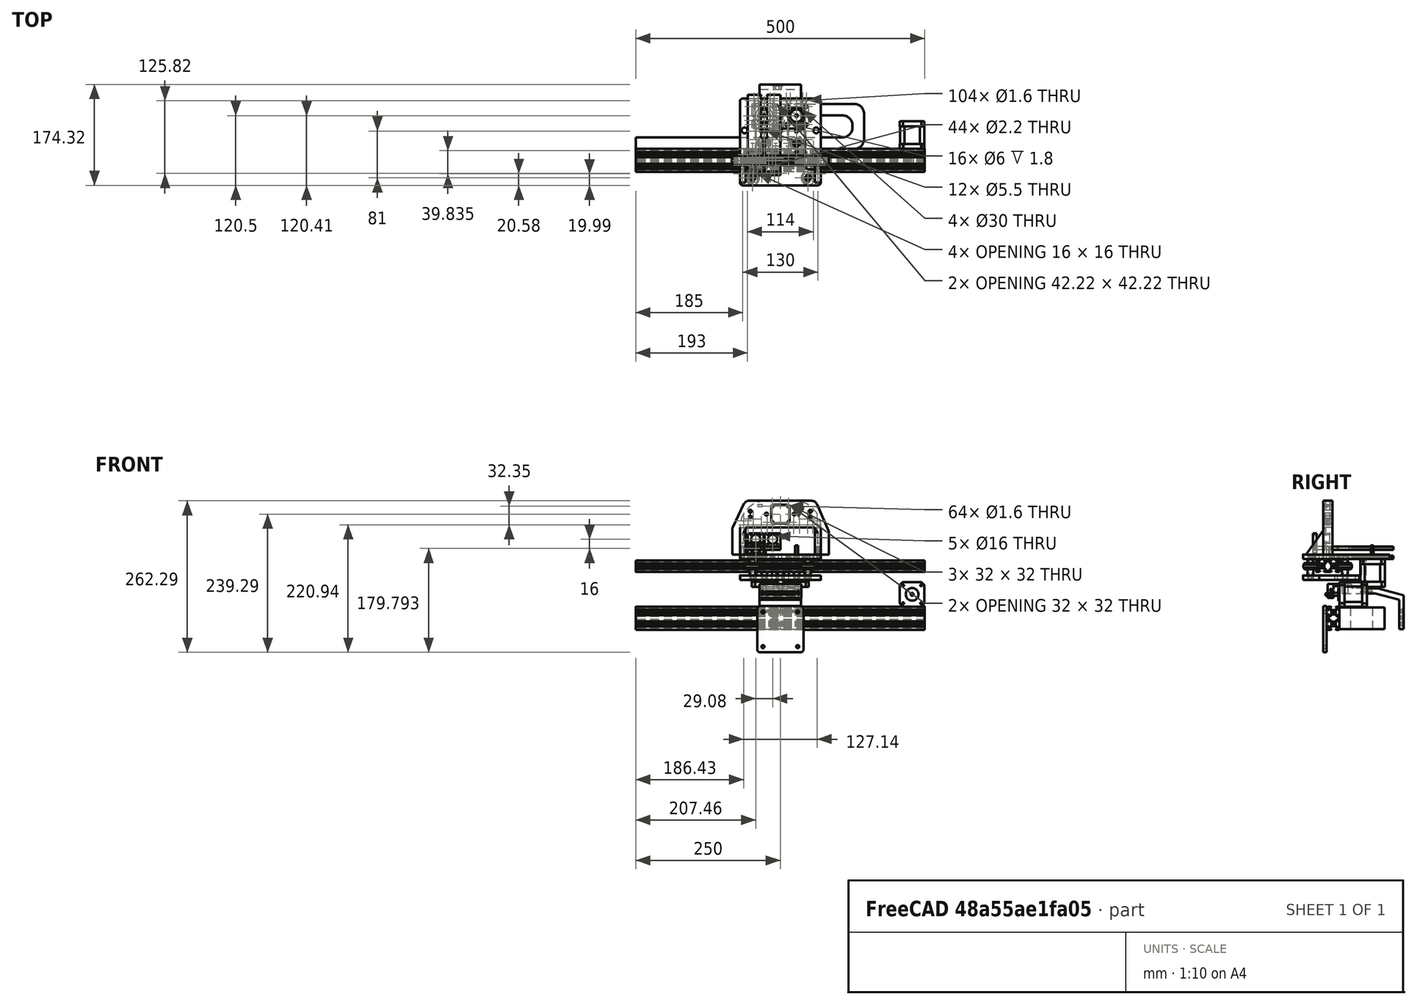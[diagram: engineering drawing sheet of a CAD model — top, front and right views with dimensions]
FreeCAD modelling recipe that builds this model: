
FCSTD DOCUMENT  (FreeCAD 0.18R16146 (Git))
Label: Head
License: All rights reserved
LicenseURL: http://en.wikipedia.org/wiki/All_rights_reserved
objects: Drawing::FeatureViewPython×332, Sketcher::SketchObject×49, Part::Feature×35, PartDesign::Hole×22, PartDesign::Pocket×15, PartDesign::Body×13, Drawing::FeatureViewPart×13, PartDesign::Pad×12, App::Part×8, App::DocumentObjectGroup×6, Drawing::FeaturePage×5, Part::MultiFuse×3, Mesh::Feature×2, Part::Mirroring×2, PartDesign::FeatureBase×1
note: 201 computed .brp shape members not serialized (recipe doc carries the construction recipe); baked Part::Feature solids carry a one-line shape summary decoded from their .brp

FEATURE [Part::Feature] Part__Feature001  label="Nema 17 Stepper Motor"
  Placement = pos=(-28,-9,0) rot=(0,0,1;0rad)
  shape: bbox 42.42 x 42.42 x 72 mm, 64 faces (baked)
FEATURE [Part::Feature] Part__Feature002  label="Nema 17 Stepper Motor001"
  Placement = pos=(28,-9,0) rot=(0,0,1;0rad)
  shape: bbox 42.42 x 42.42 x 72 mm, 64 faces (baked)
FEATURE [Part::Feature] Part__Feature  label="V-Slot 20x40x500 Linear Rail"
  Placement = pos=(-250,-86.5,-12) rot=(0,1,0;1.5708rad)
  shape: bbox 500 x 40 x 20 mm, 116 faces (baked)
FEATURE [Part::Feature] Part__Feature003  label="Solid V Wheel"
  Placement = pos=(-28,-56.5666,-12.1) rot=(0,1,0;1.5708rad)
  shape: bbox 23.9 x 23.9 x 10.2 mm, 16 faces (baked)
FEATURE [Part::Feature] Part__Feature004  label="Solid V Wheel001"
  Placement = pos=(28,-56.57,-12.1) rot=(0,1,0;1.5708rad)
  shape: bbox 23.9 x 23.9 x 10.2 mm, 16 faces (baked)
FEATURE [Part::Feature] Part__Feature005  label="Solid V Wheel002"
  Placement = pos=(-48,-116.57,-12.1) rot=(0,1,0;1.5708rad)
  shape: bbox 23.9 x 23.9 x 10.2 mm, 16 faces (baked)
FEATURE [Part::Feature] Part__Feature006  label="Solid V Wheel003"
  Placement = pos=(48,-116.57,-12.1) rot=(0,1,0;1.5708rad)
  shape: bbox 23.9 x 23.9 x 10.2 mm, 16 faces (baked)
FEATURE [Part::Feature] Part__Feature007  label="V-Slot 20x40x500 Linear Rail001"
  Placement = pos=(-250,-76.5,-102) rot=(0.57735,0.57735,0.57735;2.0944rad)
  shape: bbox 500 x 20 x 40 mm, 116 faces (baked)
FEATURE [Part::Feature] Part__Feature008  label="Nema 17 Stepper Motor002"
  Placement = pos=(228,-66.5,-60.85) rot=(1,0,0;1.5708rad)
  shape: bbox 42.42 x 72 x 42.42 mm, 64 faces (baked)
FEATURE [Part::Feature] Body006021001  label="Cable Chain Support Main001"
  shape: bbox 72 x 106 x 78.33 mm, 55 faces (baked)
FEATURE [Mesh::Feature] Mesh  label="Cable Chain Support Main001 (Meshed)"
FEATURE [Sketcher::SketchObject] Sketch025  label="BottomWheel"
  MapMode = 5
  Placement = pos=(0,0,8) rot=(0,0,1;0rad)
  sketch-geometry (2):
    g0: Circle CenterX=-48 CenterY=-116.56 CenterZ=0 NormalX=0 NormalY=0 NormalZ=1 AngleXU=0 Radius=2.6
    g1: Circle CenterX=48 CenterY=-116.56 CenterZ=0 NormalX=0 NormalY=0 NormalZ=1 AngleXU=0 Radius=2.6
  constraints (6):
    c: DistanceX(g0,g-1) = 48
    c: DistanceX(g-1,g1) = 48
    c: Radius(g0) = 2.6  'M5 Hole'
    c: Equal(g0,g1)
    c: Horizontal(g1,g0)
    c: DistanceY(g0,g-1) = 116.56
FEATURE [Sketcher::SketchObject] Sketch027  label="TopWheel"
  ExternalGeometry = -> [Sketch025]
  MapMode = 5
  Placement = pos=(0,0,8) rot=(0,0,1;0rad)
  sketch-geometry (2):
    g0: Circle CenterX=-28 CenterY=-56.56 CenterZ=0 NormalX=0 NormalY=0 NormalZ=1 AngleXU=0 Radius=2.6
    g1: Circle CenterX=28 CenterY=-56.56 CenterZ=0 NormalX=0 NormalY=0 NormalZ=1 AngleXU=0 Radius=2.6
  constraints (6):
    c: Horizontal(g0,g1)
    c: DistanceX(g0,g-1) = 28
    c: DistanceX(g-1,g1) = 28
    c: Equal(g-3,g0)
    c: Equal(g0,g1)
    c: DistanceY(g-3,g0) = 60
FEATURE [Sketcher::SketchObject] Sketch029  label="StepperFixHoles"
  MapMode = 5
  Placement = pos=(0,0,8) rot=(0,0,1;0rad)
  sketch-geometry (14):
    g0: Circle CenterX=-43.5 CenterY=6.59 CenterZ=0 NormalX=0 NormalY=0 NormalZ=1 AngleXU=0 Radius=1.6
    g1: Circle CenterX=-12.5 CenterY=6.59 CenterZ=0 NormalX=0 NormalY=0 NormalZ=1 AngleXU=0 Radius=1.6
    g2: LineSegment [constr] StartX=-43.5 StartY=6.59 StartZ=0 EndX=-12.5 EndY=6.59 EndZ=0
    g3: Circle CenterX=-43.5 CenterY=-24.41 CenterZ=0 NormalX=0 NormalY=0 NormalZ=1 AngleXU=0 Radius=1.6
    g4: LineSegment [constr] StartX=-43.5 StartY=6.59 StartZ=0 EndX=-43.5 EndY=-24.41 EndZ=0
    g5: Circle CenterX=-12.5 CenterY=-24.41 CenterZ=0 NormalX=0 NormalY=0 NormalZ=1 AngleXU=0 Radius=1.6
    g6: LineSegment [constr] StartX=-43.5 StartY=-24.41 StartZ=0 EndX=-12.5 EndY=-24.41 EndZ=0
    g7: Circle CenterX=12.5 CenterY=6.59 CenterZ=0 NormalX=0 NormalY=0 NormalZ=1 AngleXU=0 Radius=1.6
    g8: Circle CenterX=43.5 CenterY=6.59 CenterZ=0 NormalX=0 NormalY=0 NormalZ=1 AngleXU=0 Radius=1.6
    g9: LineSegment [constr] StartX=12.5 StartY=6.59 StartZ=0 EndX=43.5 EndY=6.59 EndZ=0
    g10: Circle CenterX=12.5 CenterY=-24.41 CenterZ=0 NormalX=0 NormalY=0 NormalZ=1 AngleXU=0 Radius=1.6
    g11: LineSegment [constr] StartX=12.5 StartY=6.59 StartZ=0 EndX=12.5 EndY=-24.41 EndZ=0
    g12: Circle CenterX=43.5 CenterY=-24.41 CenterZ=0 NormalX=0 NormalY=0 NormalZ=1 AngleXU=0 Radius=1.6
    g13: LineSegment [constr] StartX=12.5 StartY=-24.41 StartZ=0 EndX=43.5 EndY=-24.41 EndZ=0
  constraints (36):
    c: Radius(g0) = 1.6
    c: Equal(g0,g1) = 1.6
    c: Coincident(g0,g2)
    c: Coincident(g1,g2)
    c: Distance(g2) = 31
    c: Angle(g2) = 0
    c: Equal(g0,g3) = 1.6
    c: Coincident(g0,g4)
    c: Coincident(g3,g4)
    c: Distance(g4) = 31
    c: Perpendicular(g4,g2)
    c: Equal(g0,g5) = 1.6
    c: Coincident(g3,g6)
    c: Coincident(g5,g6)
    c: Equal(g2,g6)
    c: Parallel(g6,g2)
    c: Radius(g7) = 1.6
    c: Equal(g7,g8) = 1.6
    c: Coincident(g7,g9)
    c: Coincident(g8,g9)
    c: Distance(g9) = 31
    c: Angle(g9) = 0
    c: Equal(g7,g10) = 1.6
    c: Coincident(g7,g11)
    c: Coincident(g10,g11)
    c: Distance(g11) = 31
    c: Perpendicular(g11,g9)
    c: Equal(g7,g12) = 1.6
    c: Coincident(g10,g13)
    c: Coincident(g12,g13)
    c: Equal(g9,g13)
    c: Parallel(g13,g9)
    c: Horizontal(g1,g8)
    c: DistanceX(g-1,g7) = 12.5
    c: DistanceX(g5,g-1) = 12.5
    c: DistanceY(g5,g-1) = 24.41
FEATURE [Part::Feature] Part__Feature009  label="BeltTensor"
  Placement = pos=(16.6,-86.5,-58.6) rot=(0,0.707107,0.707107;3.14159rad)
  shape: bbox 72 x 20 x 24.2 mm, 41 faces, 2 solids (baked)
FEATURE [Part::Feature] Part__Feature012  label="Aluminum Spacer 35mm002"
  Placement = pos=(-28,-56.56,-35) rot=(0,0,-1;0.087266rad)
  shape: bbox 10 x 10 x 35 mm, 14 faces (baked)
FEATURE [Part::Feature] Part__Feature013  label="Aluminum Spacer 35mm003"
  Placement = pos=(28,-56.56,-35) rot=(0,0,1;0rad)
  shape: bbox 10 x 10 x 35 mm, 14 faces (baked)
FEATURE [Part::Feature] Part__Feature014  label="Aluminum Spacer 35mm004"
  Placement = pos=(-48,-116.56,-35) rot=(0,0,1;0rad)
  shape: bbox 10 x 10 x 35 mm, 14 faces (baked)
FEATURE [Part::Feature] Part__Feature016  label="Aluminum Spacer 35mm006"
  Placement = pos=(48,-116.56,-35) rot=(0,0,1;0rad)
  shape: bbox 10 x 10 x 35 mm, 14 faces (baked)
FEATURE [App::DocumentObjectGroup] Group  label="Spacer"
  Group = -> [Part__Feature012,Part__Feature013,Part__Feature014,Part__Feature016]
FEATURE [App::DocumentObjectGroup] Group001  label="Wheel"
  Group = -> [Part__Feature003,Part__Feature004,Part__Feature005,Part__Feature006]
FEATURE [App::DocumentObjectGroup] Group002  label="Motor"
  Group = -> [Part__Feature001,Part__Feature002]
FEATURE [Mesh::Feature] gear
  Placement = pos=(-28,-8.91,17) rot=(0,0,1;0rad)
FEATURE [Sketcher::SketchObject] Sketch040
  MapMode = 5
  Placement = pos=(0,0,0) rot=(1,0,0;1.5708rad)
  Support = -> [XZ_Plane020]
  sketch-geometry (4):
    g0: LineSegment StartX=-56.04 StartY=30.9627 StartZ=0 EndX=-29.04 EndY=30.9627 EndZ=0
    g1: LineSegment StartX=-29.04 StartY=30.9627 StartZ=0 EndX=-29.04 EndY=7.9627 EndZ=0
    g2: LineSegment StartX=-29.04 StartY=7.9627 StartZ=0 EndX=-56.04 EndY=7.9627 EndZ=0
    g3: LineSegment StartX=-56.04 StartY=7.9627 StartZ=0 EndX=-56.04 EndY=30.9627 EndZ=0
  constraints (11):
    c: Coincident(g0,g1)
    c: Coincident(g1,g2)
    c: Coincident(g2,g3)
    c: Coincident(g3,g0)
    c: Horizontal(g0)
    c: Horizontal(g2)
    c: Vertical(g1)
    c: Vertical(g3)
    c: DistanceY(g1,g1) = 23
    c: DistanceX(g2,g2) = 27
    c: DistanceX(g2,g-1) = 56.04
FEATURE [PartDesign::Pad] Pad011
  Length = 6
  Length2 = 100
  Placement = pos=(0,0,0) rot=(1,0,0;1.5708rad)
  Profile = -> Sketch040
  Type = 0
FEATURE [Sketcher::SketchObject] Sketch041
  ExternalGeometry = -> [Sketch040]
  MapMode = 5
  Placement = pos=(0,-6,1.3e-15) rot=(1,0,0;1.5708rad)
  Support = -> [Pad011]
  sketch-geometry (2):
    g0: Circle CenterX=-42.54 CenterY=20.4627 CenterZ=0 NormalX=0 NormalY=0 NormalZ=1 AngleXU=0 Radius=8
    g1: GeomPoint X=-42.54 Y=30.9627 Z=0
  constraints (4):
    c: Symmetric(g-3,g-3,g1)
    c: Radius(g0) = 8
    c: Vertical(g0,g1)
    c: DistanceY(g0,g-3) = 10.5
FEATURE [PartDesign::Hole] Hole013
  BaseFeature = -> Pad011
  Depth = 25
  DepthType = 0
  Diameter = 16
  DrillPoint = 1
  DrillPointAngle = 118
  HoleCutCountersinkAngle = 90
  HoleCutDepth = 0
  HoleCutDiameter = 0
  HoleCutType = 0
  ModelActualThread = false
  Placement = pos=(0,0,0) rot=(1,0,0;1.5708rad)
  Profile = -> Sketch041
  Tapered = false
  TaperedAngle = 90
  ThreadAngle = 0
  ThreadClass = 0
  ThreadCutOffInner = 0
  ThreadCutOffOuter = 0
  ThreadDirection = 0
  ThreadFit = 0
  ThreadPitch = 0
  ThreadSize = 0
  ThreadType = 0
  Threaded = false
FEATURE [Sketcher::SketchObject] Sketch042
  ExternalGeometry = -> [Sketch041]
  MapMode = 5
  Placement = pos=(0,-6,1.3e-15) rot=(1,0,0;1.5708rad)
  Support = -> [Hole013]
  sketch-geometry (6):
    g0: Circle CenterX=-50.54 CenterY=28.4627 CenterZ=0 NormalX=0 NormalY=0 NormalZ=1 AngleXU=0 Radius=1.2
    g1: Circle CenterX=-34.54 CenterY=28.4627 CenterZ=0 NormalX=0 NormalY=0 NormalZ=1 AngleXU=0 Radius=1.2
    g2: Circle CenterX=-50.54 CenterY=12.4627 CenterZ=0 NormalX=0 NormalY=0 NormalZ=1 AngleXU=0 Radius=1.2
    g3: Circle CenterX=-34.54 CenterY=12.4627 CenterZ=0 NormalX=0 NormalY=0 NormalZ=1 AngleXU=0 Radius=1.2
    g4: LineSegment [constr] StartX=-50.54 StartY=28.4627 StartZ=0 EndX=-34.54 EndY=12.4627 EndZ=0
    g5: GeomPoint X=-42.54 Y=20.4627 Z=0
  constraints (15):
    c: Equal(g0,g1)
    c: Equal(g1,g3)
    c: Equal(g3,g2)
    c: Radius(g1) = 1.2
    c: Horizontal(g0,g1)
    c: Vertical(g0,g2)
    c: Vertical(g3,g1)
    c: Horizontal(g2,g3)
    c: DistanceY(g3,g1) = 16
    c: DistanceX(g0,g1) = 16
    c: Coincident(g4,g0)
    c: Coincident(g4,g3)
    c: Symmetric(g4,g4,g5)
    c: Vertical(g5,g-3)
    c: Horizontal(g5,g-3)
FEATURE [PartDesign::Hole] Hole014
  BaseFeature = -> Hole013
  Depth = 25
  DepthType = 0
  Diameter = 2.2
  DrillPoint = 1
  DrillPointAngle = 118
  HoleCutCountersinkAngle = 90
  HoleCutDepth = 0
  HoleCutDiameter = 2
  HoleCutType = 0
  ModelActualThread = false
  Placement = pos=(0,0,0) rot=(1,0,0;1.5708rad)
  Profile = -> Sketch042
  Tapered = false
  TaperedAngle = 90
  ThreadAngle = 0
  ThreadClass = 0
  ThreadCutOffInner = 0
  ThreadCutOffOuter = 0
  ThreadDirection = 0
  ThreadFit = 0
  ThreadPitch = 0
  ThreadSize = 1
  ThreadType = 1
  Threaded = false
FEATURE [Sketcher::SketchObject] Sketch043
  ExternalGeometry = -> [Sketch040]
  Placement = pos=(0,1.2e-14,7.9627) rot=(1,0,0;3.14159rad)
  Support = -> [Hole014]
  sketch-geometry (7):
    g0: Circle CenterX=-53.04 CenterY=3 CenterZ=0 NormalX=0 NormalY=0 NormalZ=1 AngleXU=0 Radius=1.1
    g1: Circle CenterX=-46.04 CenterY=3 CenterZ=0 NormalX=0 NormalY=0 NormalZ=1 AngleXU=0 Radius=1.1
    g2: Circle CenterX=-39.04 CenterY=3 CenterZ=0 NormalX=0 NormalY=0 NormalZ=1 AngleXU=0 Radius=1.1
    g3: Circle CenterX=-32.04 CenterY=3 CenterZ=0 NormalX=0 NormalY=0 NormalZ=1 AngleXU=0 Radius=1.1
    g4: LineSegment [constr] StartX=-46.04 StartY=3 StartZ=0 EndX=-39.04 EndY=3 EndZ=0
    g5: GeomPoint X=-42.54 Y=3 Z=0
    g6: GeomPoint X=-42.54 Y=4.13e-14 Z=0
  constraints (16):
    c: Equal(g0,g1)
    c: Equal(g1,g3)
    c: Equal(g3,g2)
    c: Radius(g3) = 1.1
    c: Horizontal(g0,g1)
    c: Horizontal(g1,g2)
    c: Horizontal(g2,g3)
    c: DistanceY(g3,g-3) = -3
    c: DistanceX(g0,g1) = 7
    c: DistanceX(g1,g2) = 7
    c: DistanceX(g2,g3) = 7
    c: Coincident(g4,g1)
    c: Coincident(g4,g2)
    c: Symmetric(g-3,g-3,g6)
    c: Symmetric(g4,g4,g5)
    c: Vertical(g5,g6)
FEATURE [PartDesign::Hole] Hole015
  BaseFeature = -> Hole014
  Depth = 4
  DepthType = 0
  Diameter = 1.6
  DrillPoint = 1
  DrillPointAngle = 118
  HoleCutCountersinkAngle = 90
  HoleCutDepth = 0
  HoleCutDiameter = 2
  HoleCutType = 0
  ModelActualThread = false
  Placement = pos=(0,0,0) rot=(1,0,0;1.5708rad)
  Profile = -> Sketch043
  Tapered = false
  TaperedAngle = 90
  ThreadAngle = 60
  ThreadClass = 0
  ThreadCutOffInner = 0.0433013
  ThreadCutOffOuter = 0.0866025
  ThreadDirection = 1
  ThreadFit = 0
  ThreadPitch = 0.4
  ThreadSize = 1
  ThreadType = 1
  Threaded = true
FEATURE [PartDesign::Body] Body006021004  label="Fix"
  Group = -> [Sketch040,Pad011,Sketch041,Hole013,Sketch042,Hole014,Sketch043,Hole015]
  Origin = -> Origin020
  Placement = pos=(0,-105.83,-1.96) rot=(0,0,1;0rad)
  Tip = -> Hole015
FEATURE [Part::Mirroring] Part__Mirroring001  label="Fix (Mirror #2)"
  Base = (0,0,0)
  Normal = (1,0,0)
  Placement = pos=(-56,0,16) rot=(0,0,1;0rad)
  Source = -> Body006021004
FEATURE [Sketcher::SketchObject] Sketch045  label="Camera Support Contour"
  MapMode = 5
  Placement = pos=(0,0,0) rot=(1,0,0;1.5708rad)
  Support = -> [XZ_Plane022]
  sketch-geometry (11):
    g0: LineSegment StartX=-70 StartY=0 StartZ=0 EndX=-70 EndY=47 EndZ=0
    g1: LineSegment StartX=-24 StartY=93 StartZ=0 EndX=24 EndY=93 EndZ=0
    g2: LineSegment StartX=70 StartY=47 StartZ=0 EndX=70 EndY=0 EndZ=0
    g3: LineSegment StartX=70 StartY=0 StartZ=0 EndX=60 EndY=0 EndZ=0
    g4: LineSegment StartX=60 StartY=0 StartZ=0 EndX=60 EndY=47 EndZ=0
    g5: LineSegment StartX=60 StartY=47 StartZ=0 EndX=-60 EndY=47 EndZ=0
    g6: LineSegment StartX=-60 StartY=47 StartZ=0 EndX=-60 EndY=0 EndZ=0
    g7: LineSegment StartX=-60 StartY=0 StartZ=0 EndX=-70 EndY=0 EndZ=0
    g8: ArcOfCircle CenterX=24 CenterY=47 CenterZ=0 NormalX=0 NormalY=0 NormalZ=1 AngleXU=0 Radius=46 StartAngle=0 EndAngle=1.5708
    g9: ArcOfCircle CenterX=-24 CenterY=47 CenterZ=0 NormalX=0 NormalY=0 NormalZ=1 AngleXU=0 Radius=46 StartAngle=1.5708 EndAngle=3.14159
    g10: GeomPoint X=0 Y=47 Z=0
  constraints (29):
    c: PointOnObject(g0,g-1)
    c: Vertical(g0)
    c: Horizontal(g1)
    c: PointOnObject(g2,g-1)
    c: Vertical(g2)
    c: Coincident(g2,g3)
    c: Horizontal(g3)
    c: Coincident(g3,g4)
    c: Vertical(g4)
    c: Coincident(g4,g5)
    c: Horizontal(g5)
    c: Coincident(g5,g6)
    c: Vertical(g6)
    c: Coincident(g6,g7)
    c: Coincident(g7,g0)
    c: Horizontal(g7)
    c: DistanceX(g7,g7) = 10
    c: Equal(g7,g3)
    c: DistanceY(g4,g4) = 47
    c: Tangent(g1,g8) = 1.5708
    c: Tangent(g2,g8) = 1.5708
    c: Tangent(g0,g9) = 1.5708
    c: Tangent(g1,g9) = 1.5708
    c: DistanceY(g4,g1) = 46
    c: Equal(g9,g8)
    c: Symmetric(g5,g5,g10)
    c: Vertical(g10,g-1)
    c: DistanceX(g5,g5) = 120
    c: Horizontal(g0,g5)
FEATURE [PartDesign::Pad] Pad012
  Length = 8
  Length2 = 100
  Placement = pos=(0,0,0) rot=(1,0,0;1.5708rad)
  Profile = -> Sketch045
  Type = 0
FEATURE [Sketcher::SketchObject] Sketch046  label="Camera Hole"
  ExternalGeometry = -> [Sketch045]
  MapMode = 5
  Placement = pos=(0,0,0) rot=(1,0,0;1.5708rad)
  Support = -> [XZ_Plane022]
  sketch-geometry (17):
    g0: GeomPoint X=1.12e-14 Y=93 Z=0
    g1: LineSegment StartX=-12 StartY=82 StartZ=0 EndX=-12 EndY=86 EndZ=0
    g2: LineSegment StartX=-12 StartY=86 StartZ=0 EndX=12 EndY=86 EndZ=0
    g3: LineSegment StartX=12 StartY=86 StartZ=0 EndX=12 EndY=82 EndZ=0
    g4: LineSegment StartX=12 StartY=82 StartZ=0 EndX=16 EndY=82 EndZ=0
    g5: LineSegment StartX=16 StartY=82 StartZ=0 EndX=16 EndY=58 EndZ=0
    g6: LineSegment StartX=16 StartY=58 StartZ=0 EndX=12 EndY=58 EndZ=0
    g7: LineSegment StartX=12 StartY=58 StartZ=0 EndX=12 EndY=54 EndZ=0
    g8: LineSegment StartX=12 StartY=54 StartZ=0 EndX=-12 EndY=54 EndZ=0
    g9: LineSegment StartX=-12 StartY=54 StartZ=0 EndX=-12 EndY=58 EndZ=0
    g10: LineSegment StartX=-12 StartY=58 StartZ=0 EndX=-16 EndY=58 EndZ=0
    g11: LineSegment StartX=-16 StartY=58 StartZ=0 EndX=-16 EndY=82 EndZ=0
    g12: LineSegment StartX=-16 StartY=82 StartZ=0 EndX=-12 EndY=82 EndZ=0
    g13: LineSegment [constr] StartX=1.12e-14 StartY=93 StartZ=0 EndX=1.12e-14 EndY=47 EndZ=0
    g14: GeomPoint X=1.12e-14 Y=70 Z=0
    g15: LineSegment [constr] StartX=-12 StartY=82 StartZ=0 EndX=12 EndY=58 EndZ=0
    g16: GeomPoint X=1.12e-14 Y=70 Z=0
  constraints (44):
    c: Symmetric(g-3,g-3,g0)
    c: Vertical(g1)
    c: Coincident(g1,g2)
    c: Horizontal(g2)
    c: Coincident(g2,g3)
    c: Vertical(g3)
    c: Coincident(g3,g4)
    c: Horizontal(g4)
    c: Coincident(g4,g5)
    c: Vertical(g5)
    c: Coincident(g5,g6)
    c: Horizontal(g6)
    c: Coincident(g6,g7)
    c: Vertical(g7)
    c: Coincident(g7,g8)
    c: Horizontal(g8)
    c: Coincident(g8,g9)
    c: Vertical(g9)
    c: Coincident(g9,g10)
    c: Horizontal(g10)
    c: Coincident(g10,g11)
    c: Vertical(g11)
    c: Coincident(g11,g12)
    c: Coincident(g12,g1)
    c: Horizontal(g12)
    c: Coincident(g13,g0)
    c: PointOnObject(g13,g-4)
    c: Vertical(g13)
    c: Symmetric(g13,g13,g14)
    c: Equal(g11,g2)
    c: Equal(g2,g5)
    c: Equal(g5,g8)
    c: Coincident(g15,g1)
    c: Coincident(g15,g6)
    c: Symmetric(g15,g15,g16)
    c: Horizontal(g16,g14)
    c: Vertical(g16,g14)
    c: DistanceX(g2,g2) = 24
    c: DistanceX(g10,g10) = 4
    c: Horizontal(g1,g3)
    c: Vertical(g6,g3)
    c: DistanceY(g9,g9) = 4
    c: DistanceX(g6,g6) = 4
    c: DistanceY(g3,g3) = 4
FEATURE [PartDesign::Pocket] Pocket
  BaseFeature = -> Pad012
  Length = 5
  Length2 = 100
  Placement = pos=(0,0,0) rot=(1,0,0;1.5708rad)
  Profile = -> Sketch046
  Reversed = true
  Type = 1
FEATURE [Drawing::FeatureViewPython] dim001  # drawing view (typed FeaturePython)
  Rotation = 0
  ViewResult = <g> \n  <line x1="83.000000" y1="159.410000" x2="30.711514" y2="159.410000" style="stroke:rgb(0,0,255);stroke-width:0.50" />\n<line x1="110.000000" y1="61.560000" x2="30.711514" y2="61.560000" style="stroke:rgb(0,0,255);stroke-width:0.50" />\n<line x1="31.711514" y1="159.410000" x2="31.711514" y2="61.560000" style="stroke:rgb(0,0,255);stroke-width:0.50" /> \n  <polygon points="31.711514,61.560000 30.711514,64.560000 31.711514,65.560000 32.711514,64.560000" style="fill:rgb(0,0,255);stroke:rgb(0,0,255);stroke-width:0" /><polygon points="31.711514,159.410000 32.711514,156.410000 31.711514,155.410000 30.711514,156.410000" style="fill:rgb(0,0,255);stroke:rgb(0,0,255);stroke-width:0" /> \n  <text x="29.711514" y="110.485000" font-family="inherit" font-size="3.6" fill="rgb(0,0,255)" text-anchor="middle" transform="rotate(-90.000000 29.711514,110.485000)" >97.85</text> </g>
  Visible = true
  X = 0
  Y = 0
  arrowL1 = 3
  arrowL2 = 1
  arrowW = 2
  arrow_scheme = 0
  autoPlaceOffset = 2
  autoPlaceText = true
  click1_x = 31.7115
  click1_y = 70.7978
  click2_x = 31.7115
  click2_y = 70.7978
  comma_decimal_place = false
  dimension_line_overshoot = 1
  gap_datum_points = 2
  halfDimension_linear = false
  lineColor = rgb(0,0,255)
  strokeWidth = 0.5
  textFormat_linear = %(value)3.3f
  textRenderer_color = rgb(0,0,255)
  textRenderer_family = inherit
  textRenderer_size = 3.6
  unit_custom_scale = 1
  unit_scheme = 0
FEATURE [Drawing::FeatureViewPython] dim002  # drawing view (typed FeaturePython)
  Rotation = 0
  ViewResult = <g> \n  <line x1="83.000000" y1="159.410000" x2="46.716721" y2="159.410000" style="stroke:rgb(0,0,255);stroke-width:0.50" />\n<line x1="83.000000" y1="131.544000" x2="46.716721" y2="131.544000" style="stroke:rgb(0,0,255);stroke-width:0.50" />\n<line x1="47.716721" y1="159.410000" x2="47.716721" y2="131.544000" style="stroke:rgb(0,0,255);stroke-width:0.50" /> \n  <polygon points="47.716721,131.544000 46.716721,134.544000 47.716721,135.544000 48.716721,134.544000" style="fill:rgb(0,0,255);stroke:rgb(0,0,255);stroke-width:0" /><polygon points="47.716721,159.410000 48.716721,156.410000 47.716721,155.410000 46.716721,156.410000" style="fill:rgb(0,0,255);stroke:rgb(0,0,255);stroke-width:0" /> \n  <text x="45.716721" y="145.477000" font-family="inherit" font-size="3.6" fill="rgb(0,0,255)" text-anchor="middle" transform="rotate(-90.000000 45.716721,145.477000)" >27.866</text> </g>
  Visible = true
  X = 0
  Y = 0
  arrowL1 = 3
  arrowL2 = 1
  arrowW = 2
  arrow_scheme = 0
  autoPlaceOffset = 2
  autoPlaceText = true
  click1_x = 47.7167
  click1_y = 130
  click2_x = 47.7167
  click2_y = 130
  comma_decimal_place = false
  dimension_line_overshoot = 1
  gap_datum_points = 2
  halfDimension_linear = false
  lineColor = rgb(0,0,255)
  strokeWidth = 0.5
  textFormat_linear = %(value)3.3f
  textRenderer_color = rgb(0,0,255)
  textRenderer_family = inherit
  textRenderer_size = 3.6
  unit_custom_scale = 1
  unit_scheme = 0
FEATURE [Drawing::FeatureViewPython] dim003  # drawing view (typed FeaturePython)
  Rotation = 0
  ViewResult = <g> \n  <line x1="78.000000" y1="154.410000" x2="64.751387" y2="154.410000" style="stroke:rgb(0,0,255);stroke-width:0.50" />\n<line x1="78.000000" y1="136.544000" x2="64.751387" y2="136.544000" style="stroke:rgb(0,0,255);stroke-width:0.50" />\n<line x1="65.751387" y1="154.410000" x2="65.751387" y2="136.544000" style="stroke:rgb(0,0,255);stroke-width:0.50" /> \n  <polygon points="65.751387,136.544000 64.751387,139.544000 65.751387,140.544000 66.751387,139.544000" style="fill:rgb(0,0,255);stroke:rgb(0,0,255);stroke-width:0" /><polygon points="65.751387,154.410000 66.751387,151.410000 65.751387,150.410000 64.751387,151.410000" style="fill:rgb(0,0,255);stroke:rgb(0,0,255);stroke-width:0" /> \n  <text x="63.751387" y="145.477000" font-family="inherit" font-size="3.6" fill="rgb(0,0,255)" text-anchor="middle" transform="rotate(-90.000000 63.751387,145.477000)" >17.866</text> </g>
  Visible = true
  X = 0
  Y = 0
  arrowL1 = 3
  arrowL2 = 1
  arrowW = 2
  arrow_scheme = 0
  autoPlaceOffset = 2
  autoPlaceText = true
  click1_x = 65.7514
  click1_y = 139.017
  click2_x = 65.7514
  click2_y = 139.017
  comma_decimal_place = false
  dimension_line_overshoot = 1
  gap_datum_points = 2
  halfDimension_linear = false
  lineColor = rgb(0,0,255)
  strokeWidth = 0.5
  textFormat_linear = %(value)3.3f
  textRenderer_color = rgb(0,0,255)
  textRenderer_family = inherit
  textRenderer_size = 3.6
  unit_custom_scale = 1
  unit_scheme = 0
FEATURE [Drawing::FeatureViewPython] dim004  # drawing view (typed FeaturePython)
  Rotation = 0
  ViewResult = <g> \n  <line x1="107.000000" y1="64.560000" x2="107.000000" y2="24.173388" style="stroke:rgb(0,0,255);stroke-width:0.50" />\n<line x1="193.000000" y1="64.560000" x2="193.000000" y2="24.173388" style="stroke:rgb(0,0,255);stroke-width:0.50" />\n<line x1="107.000000" y1="25.173388" x2="193.000000" y2="25.173388" style="stroke:rgb(0,0,255);stroke-width:0.50" /> \n  <polygon points="193.000000,25.173388 190.000000,24.173388 189.000000,25.173388 190.000000,26.173388" style="fill:rgb(0,0,255);stroke:rgb(0,0,255);stroke-width:0" /><polygon points="107.000000,25.173388 110.000000,26.173388 111.000000,25.173388 110.000000,24.173388" style="fill:rgb(0,0,255);stroke:rgb(0,0,255);stroke-width:0" /> \n  <text x="150.000000" y="23.173388" font-family="inherit" font-size="3.6" fill="rgb(0,0,255)" text-anchor="middle" transform="rotate(0.000000 150.000000,23.173388)" >86</text> </g>
  Visible = true
  X = 0
  Y = 0
  arrowL1 = 3
  arrowL2 = 1
  arrowW = 2
  arrow_scheme = 0
  autoPlaceOffset = 2
  autoPlaceText = true
  click1_x = 187.861
  click1_y = 25.1734
  click2_x = 187.861
  click2_y = 25.1734
  comma_decimal_place = false
  dimension_line_overshoot = 1
  gap_datum_points = 2
  halfDimension_linear = false
  lineColor = rgb(0,0,255)
  strokeWidth = 0.5
  textFormat_linear = %(value)3.3f
  textRenderer_color = rgb(0,0,255)
  textRenderer_family = inherit
  textRenderer_size = 3.6
  unit_custom_scale = 1
  unit_scheme = 0
FEATURE [Drawing::FeatureViewPython] dim005  # drawing view (typed FeaturePython)
  Rotation = 0
  ViewResult = <g> \n  <line x1="112.000000" y1="59.560000" x2="112.000000" y2="37.699388" style="stroke:rgb(0,0,255);stroke-width:0.50" />\n<line x1="188.000000" y1="59.560000" x2="188.000000" y2="37.699388" style="stroke:rgb(0,0,255);stroke-width:0.50" />\n<line x1="112.000000" y1="38.699388" x2="188.000000" y2="38.699388" style="stroke:rgb(0,0,255);stroke-width:0.50" /> \n  <polygon points="188.000000,38.699388 185.000000,37.699388 184.000000,38.699388 185.000000,39.699388" style="fill:rgb(0,0,255);stroke:rgb(0,0,255);stroke-width:0" /><polygon points="112.000000,38.699388 115.000000,39.699388 116.000000,38.699388 115.000000,37.699388" style="fill:rgb(0,0,255);stroke:rgb(0,0,255);stroke-width:0" /> \n  <text x="150.000000" y="36.699388" font-family="inherit" font-size="3.6" fill="rgb(0,0,255)" text-anchor="middle" transform="rotate(0.000000 150.000000,36.699388)" >76</text> </g>
  Visible = true
  X = 0
  Y = 0
  arrowL1 = 3
  arrowL2 = 1
  arrowW = 2
  arrow_scheme = 0
  autoPlaceOffset = 2
  autoPlaceText = true
  click1_x = 186.358
  click1_y = 38.6994
  click2_x = 186.358
  click2_y = 38.6994
  comma_decimal_place = false
  dimension_line_overshoot = 1
  gap_datum_points = 2
  halfDimension_linear = false
  lineColor = rgb(0,0,255)
  strokeWidth = 0.5
  textFormat_linear = %(value)3.3f
  textRenderer_color = rgb(0,0,255)
  textRenderer_family = inherit
  textRenderer_size = 3.6
  unit_custom_scale = 1
  unit_scheme = 0
FEATURE [Drawing::FeatureViewPython] centerLines001  # drawing view (typed FeaturePython)
  Rotation = 0
  ViewResult = <g transform="scale(1.000000,1.000000)" stroke="rgb(0,0,255)"  stroke-width="0.320000" > <path d="M 150.000000,62.810000 L 150.000000,65.810000 M 150.000000,67.810000 L 150.000000,73.810000 M 150.000000,75.810000 L 150.000000,78.810000 M 150.000000,80.810000 L 150.000000,86.810000 M 150.000000,88.810000 L 150.000000,91.810000 M 150.000000,93.810000 L 150.000000,99.810000 M 150.000000,101.810000 L 150.000000,104.810000 M 150.000000,106.810000 L 150.000000,112.810000 M 150.000000,114.810000 L 150.000000,117.810000 M 150.000000,119.810000 L 150.000000,125.810000 M 150.000000,127.810000 L 150.000000,130.810000 M 150.000000,132.810000 L 150.000000,138.810000 M 150.000000,140.810000 L 150.000000,143.810000 M 150.000000,145.810000 L 150.000000,151.810000 M 150.000000,153.810000 L 150.000000,156.810000 M 150.000000,158.810000 L 150.000000,164.810000 M 150.000000,166.810000 L 150.000000,169.810000 "/>\n<path d="M 150.000000,62.810000 L 150.000000,65.810000 M 150.000000,67.810000 L 150.000000,73.810000 M 150.000000,75.810000 L 150.000000,78.810000 M 150.000000,80.810000 L 150.000000,86.810000 M 150.000000,88.810000 L 150.000000,91.810000 M 150.000000,93.810000 L 150.000000,99.810000 M 150.000000,101.810000 L 150.000000,104.810000 M 150.000000,106.810000 L 150.000000,112.810000 M 150.000000,114.810000 L 150.000000,117.810000 M 150.000000,119.810000 L 150.000000,125.810000 M 150.000000,127.810000 L 150.000000,130.810000 M 150.000000,132.810000 L 150.000000,138.810000 M 150.000000,140.810000 L 150.000000,143.810000 M 150.000000,145.810000 L 150.000000,151.810000 M 150.000000,153.810000 L 150.000000,156.810000 M 150.000000,158.810000 L 150.000000,164.810000 M 150.000000,166.810000 L 150.000000,169.810000 "/> </g> 
  Visible = true
  X = 0
  Y = 0
  centerLine_color = rgb(0,0,255)
  centerLine_len_dash = 6
  centerLine_len_dot = 3
  centerLine_len_gap = 2
  centerLine_width = 0.32
  click1_x = 151.04
  click1_y = 170.578
  click2_x = 152.919
  click2_y = 170.954
FEATURE [Drawing::FeatureViewPython] dim006  # drawing view (typed FeaturePython)
  Rotation = 0
  ViewResult = <g> \n  <line x1="102.000000" y1="146.460000" x2="102.000000" y2="176.608774" style="stroke:rgb(0,0,255);stroke-width:0.50" />\n<line x1="150.000000" y1="171.810000" x2="150.000000" y2="176.608774" style="stroke:rgb(0,0,255);stroke-width:0.50" />\n<line x1="102.000000" y1="175.608774" x2="150.000000" y2="175.608774" style="stroke:rgb(0,0,255);stroke-width:0.50" /> \n  <polygon points="150.000000,175.608774 147.000000,174.608774 146.000000,175.608774 147.000000,176.608774" style="fill:rgb(0,0,255);stroke:rgb(0,0,255);stroke-width:0" /><polygon points="102.000000,175.608774 105.000000,176.608774 106.000000,175.608774 105.000000,174.608774" style="fill:rgb(0,0,255);stroke:rgb(0,0,255);stroke-width:0" /> \n  <text x="126.000000" y="173.608774" font-family="inherit" font-size="3.6" fill="rgb(0,0,255)" text-anchor="middle" transform="rotate(0.000000 126.000000,173.608774)" >48</text> </g>
  Visible = true
  X = 0
  Y = 0
  arrowL1 = 3
  arrowL2 = 1
  arrowW = 2
  arrow_scheme = 0
  autoPlaceOffset = 2
  autoPlaceText = true
  click1_x = 126.219
  click1_y = 175.609
  click2_x = 126.219
  click2_y = 175.609
  comma_decimal_place = false
  dimension_line_overshoot = 1
  gap_datum_points = 2
  halfDimension_linear = false
  lineColor = rgb(0,0,255)
  strokeWidth = 0.5
  textFormat_linear = %(value)3.3f
  textRenderer_color = rgb(0,0,255)
  textRenderer_family = inherit
  textRenderer_size = 3.6
  unit_custom_scale = 1
  unit_scheme = 0
FEATURE [Drawing::FeatureViewPython] dim007  # drawing view (typed FeaturePython)
  Rotation = 0
  ViewResult = <g> \n  <line x1="198.000000" y1="146.460000" x2="198.000000" y2="176.606407" style="stroke:rgb(0,0,255);stroke-width:0.50" />\n<line x1="150.000000" y1="171.810000" x2="150.000000" y2="176.606407" style="stroke:rgb(0,0,255);stroke-width:0.50" />\n<line x1="198.000000" y1="175.606407" x2="150.000000" y2="175.606407" style="stroke:rgb(0,0,255);stroke-width:0.50" /> \n  <polygon points="150.000000,175.606407 153.000000,176.606407 154.000000,175.606407 153.000000,174.606407" style="fill:rgb(0,0,255);stroke:rgb(0,0,255);stroke-width:0" /><polygon points="198.000000,175.606407 195.000000,174.606407 194.000000,175.606407 195.000000,176.606407" style="fill:rgb(0,0,255);stroke:rgb(0,0,255);stroke-width:0" /> \n  <text x="174.000000" y="173.606407" font-family="inherit" font-size="3.6" fill="rgb(0,0,255)" text-anchor="middle" transform="rotate(0.000000 174.000000,173.606407)" >48</text> </g>
  Visible = true
  X = 0
  Y = 0
  arrowL1 = 3
  arrowL2 = 1
  arrowW = 2
  arrow_scheme = 0
  autoPlaceOffset = 2
  autoPlaceText = true
  click1_x = 157.789
  click1_y = 175.606
  click2_x = 157.789
  click2_y = 175.606
  comma_decimal_place = false
  dimension_line_overshoot = 1
  gap_datum_points = 2
  halfDimension_linear = false
  lineColor = rgb(0,0,255)
  strokeWidth = 0.5
  textFormat_linear = %(value)3.3f
  textRenderer_color = rgb(0,0,255)
  textRenderer_family = inherit
  textRenderer_size = 3.6
  unit_custom_scale = 1
  unit_scheme = 0
FEATURE [Drawing::FeatureViewPython] dim008  # drawing view (typed FeaturePython)
  Rotation = 0
  ViewResult = <g> \n  <line x1="80.000000" y1="156.410000" x2="80.000000" y2="210.604290" style="stroke:rgb(0,0,255);stroke-width:0.50" />\n<line x1="220.000000" y1="156.410000" x2="220.000000" y2="210.604290" style="stroke:rgb(0,0,255);stroke-width:0.50" />\n<line x1="80.000000" y1="209.604290" x2="220.000000" y2="209.604290" style="stroke:rgb(0,0,255);stroke-width:0.50" /> \n  <polygon points="220.000000,209.604290 217.000000,208.604290 216.000000,209.604290 217.000000,210.604290" style="fill:rgb(0,0,255);stroke:rgb(0,0,255);stroke-width:0" /><polygon points="80.000000,209.604290 83.000000,210.604290 84.000000,209.604290 83.000000,208.604290" style="fill:rgb(0,0,255);stroke:rgb(0,0,255);stroke-width:0" /> \n  <text x="150.000000" y="207.604290" font-family="inherit" font-size="3.6" fill="rgb(0,0,255)" text-anchor="middle" transform="rotate(0.000000 150.000000,207.604290)" >140</text> </g>
  Visible = true
  X = 0
  Y = 0
  arrowL1 = 3
  arrowL2 = 1
  arrowW = 2
  arrow_scheme = 0
  autoPlaceOffset = 2
  autoPlaceText = true
  click1_x = 216.127
  click1_y = 209.604
  click2_x = 216.127
  click2_y = 209.604
  comma_decimal_place = false
  dimension_line_overshoot = 1
  gap_datum_points = 2
  halfDimension_linear = false
  lineColor = rgb(0,0,255)
  strokeWidth = 0.5
  textFormat_linear = %(value)3.3f
  textRenderer_color = rgb(0,0,255)
  textRenderer_family = inherit
  textRenderer_size = 3.6
  unit_custom_scale = 1
  unit_scheme = 0
FEATURE [Drawing::FeatureViewPython] dim009  # drawing view (typed FeaturePython)
  Rotation = 0
  ViewResult = <g> \n  <line x1="85.000000" y1="161.410000" x2="85.000000" y2="197.993244" style="stroke:rgb(0,0,255);stroke-width:0.50" />\n<line x1="215.000000" y1="161.410000" x2="215.000000" y2="197.993244" style="stroke:rgb(0,0,255);stroke-width:0.50" />\n<line x1="85.000000" y1="196.993244" x2="215.000000" y2="196.993244" style="stroke:rgb(0,0,255);stroke-width:0.50" /> \n  <polygon points="215.000000,196.993244 212.000000,195.993244 211.000000,196.993244 212.000000,197.993244" style="fill:rgb(0,0,255);stroke:rgb(0,0,255);stroke-width:0" /><polygon points="85.000000,196.993244 88.000000,197.993244 89.000000,196.993244 88.000000,195.993244" style="fill:rgb(0,0,255);stroke:rgb(0,0,255);stroke-width:0" /> \n  <text x="150.000000" y="194.993244" font-family="inherit" font-size="3.6" fill="rgb(0,0,255)" text-anchor="middle" transform="rotate(0.000000 150.000000,194.993244)" >130</text> </g>
  Visible = true
  X = 0
  Y = 0
  arrowL1 = 3
  arrowL2 = 1
  arrowW = 2
  arrow_scheme = 0
  autoPlaceOffset = 2
  autoPlaceText = true
  click1_x = 207.43
  click1_y = 196.993
  click2_x = 207.43
  click2_y = 196.993
  comma_decimal_place = false
  dimension_line_overshoot = 1
  gap_datum_points = 2
  halfDimension_linear = false
  lineColor = rgb(0,0,255)
  strokeWidth = 0.5
  textFormat_linear = %(value)3.3f
  textRenderer_color = rgb(0,0,255)
  textRenderer_family = inherit
  textRenderer_size = 3.6
  unit_custom_scale = 1
  unit_scheme = 0
FEATURE [Drawing::FeatureViewPython] dim010  # drawing view (typed FeaturePython)
  Rotation = 0
  ViewResult = <g> \n  <line x1="122.000000" y1="101.470000" x2="122.000000" y2="118.791475" style="stroke:rgb(0,0,255);stroke-width:0.50" />\n<line x1="150.000000" y1="67.560000" x2="150.000000" y2="118.791475" style="stroke:rgb(0,0,255);stroke-width:0.50" />\n<line x1="122.000000" y1="117.791475" x2="150.000000" y2="117.791475" style="stroke:rgb(0,0,255);stroke-width:0.50" /> \n  <polygon points="150.000000,117.791475 147.000000,116.791475 146.000000,117.791475 147.000000,118.791475" style="fill:rgb(0,0,255);stroke:rgb(0,0,255);stroke-width:0" /><polygon points="122.000000,117.791475 125.000000,118.791475 126.000000,117.791475 125.000000,116.791475" style="fill:rgb(0,0,255);stroke:rgb(0,0,255);stroke-width:0" /> \n  <text x="136.000000" y="115.791475" font-family="inherit" font-size="3.6" fill="rgb(0,0,255)" text-anchor="middle" transform="rotate(0.000000 136.000000,115.791475)" >28</text> </g>
  Visible = true
  X = 0
  Y = 0
  arrowL1 = 3
  arrowL2 = 1
  arrowW = 2
  arrow_scheme = 0
  autoPlaceOffset = 2
  autoPlaceText = true
  click1_x = 133.156
  click1_y = 117.791
  click2_x = 133.156
  click2_y = 117.791
  comma_decimal_place = false
  dimension_line_overshoot = 1
  gap_datum_points = 2
  halfDimension_linear = false
  lineColor = rgb(0,0,255)
  strokeWidth = 0.5
  textFormat_linear = %(value)3.3f
  textRenderer_color = rgb(0,0,255)
  textRenderer_family = inherit
  textRenderer_size = 3.6
  unit_custom_scale = 1
  unit_scheme = 0
FEATURE [Drawing::FeatureViewPython] dim011  # drawing view (typed FeaturePython)
  Rotation = 0
  ViewResult = <g> \n  <line x1="150.000000" y1="67.560000" x2="150.000000" y2="118.775578" style="stroke:rgb(0,0,255);stroke-width:0.50" />\n<line x1="178.000000" y1="103.570000" x2="178.000000" y2="118.775578" style="stroke:rgb(0,0,255);stroke-width:0.50" />\n<line x1="150.000000" y1="117.775578" x2="178.000000" y2="117.775578" style="stroke:rgb(0,0,255);stroke-width:0.50" /> \n  <polygon points="178.000000,117.775578 175.000000,116.775578 174.000000,117.775578 175.000000,118.775578" style="fill:rgb(0,0,255);stroke:rgb(0,0,255);stroke-width:0" /><polygon points="150.000000,117.775578 153.000000,118.775578 154.000000,117.775578 153.000000,116.775578" style="fill:rgb(0,0,255);stroke:rgb(0,0,255);stroke-width:0" /> \n  <text x="164.000000" y="115.775578" font-family="inherit" font-size="3.6" fill="rgb(0,0,255)" text-anchor="middle" transform="rotate(0.000000 164.000000,115.775578)" >28</text> </g>
  Visible = true
  X = 0
  Y = 0
  arrowL1 = 3
  arrowL2 = 1
  arrowW = 2
  arrow_scheme = 0
  autoPlaceOffset = 2
  autoPlaceText = true
  click1_x = 175.606
  click1_y = 117.776
  click2_x = 175.606
  click2_y = 117.776
  comma_decimal_place = false
  dimension_line_overshoot = 1
  gap_datum_points = 2
  halfDimension_linear = false
  lineColor = rgb(0,0,255)
  strokeWidth = 0.5
  textFormat_linear = %(value)3.3f
  textRenderer_color = rgb(0,0,255)
  textRenderer_family = inherit
  textRenderer_size = 3.6
  unit_custom_scale = 1
  unit_scheme = 0
FEATURE [Drawing::FeatureViewPython] dim012  # drawing view (typed FeaturePython)
  Rotation = 0
  ViewResult = <g> \n  <line x1="122.000000" y1="88.560000" x2="122.000000" y2="96.428417" style="stroke:rgb(0,0,255);stroke-width:0.50" />\n<line x1="150.000000" y1="67.560000" x2="150.000000" y2="96.428417" style="stroke:rgb(0,0,255);stroke-width:0.50" />\n<line x1="122.000000" y1="95.428417" x2="150.000000" y2="95.428417" style="stroke:rgb(0,0,255);stroke-width:0.50" /> \n  <polygon points="150.000000,95.428417 147.000000,94.428417 146.000000,95.428417 147.000000,96.428417" style="fill:rgb(0,0,255);stroke:rgb(0,0,255);stroke-width:0" /><polygon points="122.000000,95.428417 125.000000,96.428417 126.000000,95.428417 125.000000,94.428417" style="fill:rgb(0,0,255);stroke:rgb(0,0,255);stroke-width:0" /> \n  <text x="136.000000" y="93.428417" font-family="inherit" font-size="3.6" fill="rgb(0,0,255)" text-anchor="middle" transform="rotate(0.000000 136.000000,93.428417)" >28</text> </g>
  Visible = true
  X = 0
  Y = 0
  arrowL1 = 3
  arrowL2 = 1
  arrowW = 2
  arrow_scheme = 0
  autoPlaceOffset = 2
  autoPlaceText = true
  click1_x = 145.559
  click1_y = 95.4284
  click2_x = 145.559
  click2_y = 95.4284
  comma_decimal_place = false
  dimension_line_overshoot = 1
  gap_datum_points = 2
  halfDimension_linear = false
  lineColor = rgb(0,0,255)
  strokeWidth = 0.5
  textFormat_linear = %(value)3.3f
  textRenderer_color = rgb(0,0,255)
  textRenderer_family = inherit
  textRenderer_size = 3.6
  unit_custom_scale = 1
  unit_scheme = 0
FEATURE [Drawing::FeatureViewPython] dim013  # drawing view (typed FeaturePython)
  Rotation = 0
  ViewResult = <g> \n  <line x1="150.000000" y1="67.560000" x2="150.000000" y2="96.428417" style="stroke:rgb(0,0,255);stroke-width:0.50" />\n<line x1="178.000000" y1="88.560000" x2="178.000000" y2="96.428417" style="stroke:rgb(0,0,255);stroke-width:0.50" />\n<line x1="150.000000" y1="95.428417" x2="178.000000" y2="95.428417" style="stroke:rgb(0,0,255);stroke-width:0.50" /> \n  <polygon points="178.000000,95.428417 175.000000,94.428417 174.000000,95.428417 175.000000,96.428417" style="fill:rgb(0,0,255);stroke:rgb(0,0,255);stroke-width:0" /><polygon points="150.000000,95.428417 153.000000,96.428417 154.000000,95.428417 153.000000,94.428417" style="fill:rgb(0,0,255);stroke:rgb(0,0,255);stroke-width:0" /> \n  <text x="164.000000" y="93.428417" font-family="inherit" font-size="3.6" fill="rgb(0,0,255)" text-anchor="middle" transform="rotate(0.000000 164.000000,93.428417)" >28</text> </g>
  Visible = true
  X = 0
  Y = 0
  arrowL1 = 3
  arrowL2 = 1
  arrowW = 2
  arrow_scheme = 0
  autoPlaceOffset = 2
  autoPlaceText = true
  click1_x = 177.569
  click1_y = 95.4284
  click2_x = 177.569
  click2_y = 95.4284
  comma_decimal_place = false
  dimension_line_overshoot = 1
  gap_datum_points = 2
  halfDimension_linear = false
  lineColor = rgb(0,0,255)
  strokeWidth = 0.5
  textFormat_linear = %(value)3.3f
  textRenderer_color = rgb(0,0,255)
  textRenderer_family = inherit
  textRenderer_size = 3.6
  unit_custom_scale = 1
  unit_scheme = 0
FEATURE [Drawing::FeatureViewPython] dim014  # drawing view (typed FeaturePython)
  Rotation = 0
  ViewResult = <g> \n  <line x1="122.000000" y1="67.560000" x2="122.000000" y2="78.611086" style="stroke:rgb(0,0,255);stroke-width:0.50" />\n<line x1="150.000000" y1="67.560000" x2="150.000000" y2="78.611086" style="stroke:rgb(0,0,255);stroke-width:0.50" />\n<line x1="122.000000" y1="77.611086" x2="150.000000" y2="77.611086" style="stroke:rgb(0,0,255);stroke-width:0.50" /> \n  <polygon points="150.000000,77.611086 147.000000,76.611086 146.000000,77.611086 147.000000,78.611086" style="fill:rgb(0,0,255);stroke:rgb(0,0,255);stroke-width:0" /><polygon points="122.000000,77.611086 125.000000,78.611086 126.000000,77.611086 125.000000,76.611086" style="fill:rgb(0,0,255);stroke:rgb(0,0,255);stroke-width:0" /> \n  <text x="136.000000" y="75.611086" font-family="inherit" font-size="3.6" fill="rgb(0,0,255)" text-anchor="middle" transform="rotate(0.000000 136.000000,75.611086)" >28</text> </g>
  Visible = true
  X = 0
  Y = 0
  arrowL1 = 3
  arrowL2 = 1
  arrowW = 2
  arrow_scheme = 0
  autoPlaceOffset = 2
  autoPlaceText = true
  click1_x = 149.484
  click1_y = 77.6111
  click2_x = 149.484
  click2_y = 77.6111
  comma_decimal_place = false
  dimension_line_overshoot = 1
  gap_datum_points = 2
  halfDimension_linear = false
  lineColor = rgb(0,0,255)
  strokeWidth = 0.5
  textFormat_linear = %(value)3.3f
  textRenderer_color = rgb(0,0,255)
  textRenderer_family = inherit
  textRenderer_size = 3.6
  unit_custom_scale = 1
  unit_scheme = 0
FEATURE [Drawing::FeatureViewPython] dim015  # drawing view (typed FeaturePython)
  Rotation = 0
  ViewResult = <g> \n  <line x1="178.000000" y1="67.560000" x2="178.000000" y2="78.611086" style="stroke:rgb(0,0,255);stroke-width:0.50" />\n<line x1="150.000000" y1="67.560000" x2="150.000000" y2="78.611086" style="stroke:rgb(0,0,255);stroke-width:0.50" />\n<line x1="178.000000" y1="77.611086" x2="150.000000" y2="77.611086" style="stroke:rgb(0,0,255);stroke-width:0.50" /> \n  <polygon points="150.000000,77.611086 153.000000,78.611086 154.000000,77.611086 153.000000,76.611086" style="fill:rgb(0,0,255);stroke:rgb(0,0,255);stroke-width:0" /><polygon points="178.000000,77.611086 175.000000,76.611086 174.000000,77.611086 175.000000,78.611086" style="fill:rgb(0,0,255);stroke:rgb(0,0,255);stroke-width:0" /> \n  <text x="164.000000" y="75.611086" font-family="inherit" font-size="3.6" fill="rgb(0,0,255)" text-anchor="middle" transform="rotate(0.000000 164.000000,75.611086)" >28</text> </g>
  Visible = true
  X = 0
  Y = 0
  arrowL1 = 3
  arrowL2 = 1
  arrowW = 2
  arrow_scheme = 0
  autoPlaceOffset = 2
  autoPlaceText = true
  click1_x = 152.353
  click1_y = 77.6111
  click2_x = 152.353
  click2_y = 77.6111
  comma_decimal_place = false
  dimension_line_overshoot = 1
  gap_datum_points = 2
  halfDimension_linear = false
  lineColor = rgb(0,0,255)
  strokeWidth = 0.5
  textFormat_linear = %(value)3.3f
  textRenderer_color = rgb(0,0,255)
  textRenderer_family = inherit
  textRenderer_size = 3.6
  unit_custom_scale = 1
  unit_scheme = 0
FEATURE [Drawing::FeatureViewPython] rad001  # drawing view (typed FeaturePython)
  Rotation = 0
  ViewResult = <g>  <circle cx ="112.000000" cy ="66.560000" r="0.250000" stroke="none" fill="rgb(0,0,255)" /> \n<line x1="102.555350" y1="71.208926" x2="112.000000" y2="66.560000" style="stroke:rgb(0,0,255);stroke-width:0.50" />\n<polygon points="107.514006,68.768134 110.647229,68.340453 111.102801,67.001627 109.763976,66.546055" style="fill:rgb(0,0,255);stroke:rgb(0,0,255);stroke-width:0" />\n<line x1="102.555350" y1="71.208926" x2="95.488815" y2="71.208926" style="stroke:rgb(0,0,255);stroke-width:0.50" />\n<text x="99.022082" y="69.208926" font-family="inherit" font-size="3.6" fill="rgb(0,0,255)" text-anchor="middle" transform="rotate(0.000000 99.022082,69.208926)" >R5</text> </g>
  Visible = true
  X = 0
  Y = 0
  arrowL1 = 3
  arrowL2 = 1
  arrowW = 2
  arrow_scheme = 0
  autoPlaceOffset = 2
  autoPlaceText = true
  centerPointDia = 0.5
  click1_x = 102.555
  click1_y = 71.2089
  click2_x = 95.4888
  click2_y = 71.5713
  click3_x = 95.4888
  click3_y = 71.5713
  comma_decimal_place = false
  lineColor = rgb(0,0,255)
  strokeWidth = 0.5
  textFormat_radial = R%(value)3.3f
  textRenderer_color = rgb(0,0,255)
  textRenderer_family = inherit
  textRenderer_size = 3.6
  unit_custom_scale = 1
  unit_scheme = 0
FEATURE [Drawing::FeatureViewPython] centerLines002  # drawing view (typed FeaturePython)
  Rotation = 0
  ViewResult = <g transform="scale(1.000000,1.000000)" stroke="rgb(0,0,255)"  stroke-width="0.320000" > <path d="M 102.000000,146.560000 L 105.000000,146.560000 M 107.000000,146.560000 L 113.000000,146.560000 M 115.000000,146.560000 L 118.000000,146.560000 M 120.000000,146.560000 L 126.000000,146.560000 M 128.000000,146.560000 L 131.000000,146.560000 M 133.000000,146.560000 L 139.000000,146.560000 M 141.000000,146.560000 L 144.000000,146.560000 M 146.000000,146.560000 L 152.000000,146.560000 M 154.000000,146.560000 L 157.000000,146.560000 M 159.000000,146.560000 L 165.000000,146.560000 M 167.000000,146.560000 L 170.000000,146.560000 M 172.000000,146.560000 L 178.000000,146.560000 M 180.000000,146.560000 L 183.000000,146.560000 M 185.000000,146.560000 L 191.000000,146.560000 M 193.000000,146.560000 L 196.000000,146.560000 M 198.000000,146.560000 L 198.026247,146.560000 "/>\n<path d="M 102.000000,146.560000 L 105.000000,146.560000 M 107.000000,146.560000 L 113.000000,146.560000 M 115.000000,146.560000 L 118.000000,146.560000 M 120.000000,146.560000 L 126.000000,146.560000 M 128.000000,146.560000 L 131.000000,146.560000 M 133.000000,146.560000 L 139.000000,146.560000 M 141.000000,146.560000 L 144.000000,146.560000 M 146.000000,146.560000 L 152.000000,146.560000 M 154.000000,146.560000 L 157.000000,146.560000 M 159.000000,146.560000 L 165.000000,146.560000 M 167.000000,146.560000 L 170.000000,146.560000 M 172.000000,146.560000 L 178.000000,146.560000 M 180.000000,146.560000 L 183.000000,146.560000 M 185.000000,146.560000 L 191.000000,146.560000 M 193.000000,146.560000 L 196.000000,146.560000 M 198.000000,146.560000 L 198.026247,146.560000 "/> </g> 
  Visible = true
  X = 0
  Y = 0
  centerLine_color = rgb(0,0,255)
  centerLine_len_dash = 6
  centerLine_len_dot = 3
  centerLine_len_gap = 2
  centerLine_width = 0.32
  click1_x = 198.026
  click1_y = 146.386
  click2_x = 198.026
  click2_y = 146.386
FEATURE [Drawing::FeatureViewPython] dim016  # drawing view (typed FeaturePython)
  Rotation = 0
  ViewResult = <g> \n  <line x1="180.000000" y1="101.570000" x2="231.575967" y2="101.570000" style="stroke:rgb(0,0,255);stroke-width:0.50" />\n<line x1="200.000000" y1="146.560000" x2="231.575967" y2="146.560000" style="stroke:rgb(0,0,255);stroke-width:0.50" />\n<line x1="230.575967" y1="101.570000" x2="230.575967" y2="146.560000" style="stroke:rgb(0,0,255);stroke-width:0.50" /> \n  <polygon points="230.575967,146.560000 231.575967,143.560000 230.575967,142.560000 229.575967,143.560000" style="fill:rgb(0,0,255);stroke:rgb(0,0,255);stroke-width:0" /><polygon points="230.575967,101.570000 229.575967,104.570000 230.575967,105.570000 231.575967,104.570000" style="fill:rgb(0,0,255);stroke:rgb(0,0,255);stroke-width:0" /> \n  <text x="228.575967" y="124.065000" font-family="inherit" font-size="3.6" fill="rgb(0,0,255)" text-anchor="middle" transform="rotate(-90.000000 228.575967,124.065000)" >44.99</text> </g>
  Visible = true
  X = 0
  Y = 0
  arrowL1 = 3
  arrowL2 = 1
  arrowW = 2
  arrow_scheme = 0
  autoPlaceOffset = 2
  autoPlaceText = true
  click1_x = 230.576
  click1_y = 143.903
  click2_x = 230.576
  click2_y = 143.903
  comma_decimal_place = false
  dimension_line_overshoot = 1
  gap_datum_points = 2
  halfDimension_linear = false
  lineColor = rgb(0,0,255)
  strokeWidth = 0.5
  textFormat_linear = %(value)3.3f
  textRenderer_color = rgb(0,0,255)
  textRenderer_family = inherit
  textRenderer_size = 3.6
  unit_custom_scale = 1
  unit_scheme = 0
FEATURE [Drawing::FeatureViewPython] dim017  # drawing view (typed FeaturePython)
  Rotation = 0
  ViewResult = <g> \n  <line x1="180.000000" y1="86.560000" x2="242.658169" y2="86.560000" style="stroke:rgb(0,0,255);stroke-width:0.50" />\n<line x1="200.000000" y1="146.560000" x2="242.658169" y2="146.560000" style="stroke:rgb(0,0,255);stroke-width:0.50" />\n<line x1="241.658169" y1="86.560000" x2="241.658169" y2="146.560000" style="stroke:rgb(0,0,255);stroke-width:0.50" /> \n  <polygon points="241.658169,146.560000 242.658169,143.560000 241.658169,142.560000 240.658169,143.560000" style="fill:rgb(0,0,255);stroke:rgb(0,0,255);stroke-width:0" /><polygon points="241.658169,86.560000 240.658169,89.560000 241.658169,90.560000 242.658169,89.560000" style="fill:rgb(0,0,255);stroke:rgb(0,0,255);stroke-width:0" /> \n  <text x="239.658169" y="116.560000" font-family="inherit" font-size="3.6" fill="rgb(0,0,255)" text-anchor="middle" transform="rotate(-90.000000 239.658169,116.560000)" >60</text> </g>
  Visible = true
  X = 0
  Y = 0
  arrowL1 = 3
  arrowL2 = 1
  arrowW = 2
  arrow_scheme = 0
  autoPlaceOffset = 2
  autoPlaceText = true
  click1_x = 241.658
  click1_y = 122.235
  click2_x = 241.658
  click2_y = 122.235
  comma_decimal_place = false
  dimension_line_overshoot = 1
  gap_datum_points = 2
  halfDimension_linear = false
  lineColor = rgb(0,0,255)
  strokeWidth = 0.5
  textFormat_linear = %(value)3.3f
  textRenderer_color = rgb(0,0,255)
  textRenderer_family = inherit
  textRenderer_size = 3.6
  unit_custom_scale = 1
  unit_scheme = 0
FEATURE [Drawing::FeatureViewPython] dim018  # drawing view (typed FeaturePython)
  Rotation = 0
  ViewResult = <g> \n  <line x1="180.000000" y1="65.560000" x2="252.086311" y2="65.560000" style="stroke:rgb(0,0,255);stroke-width:0.50" />\n<line x1="200.000000" y1="146.560000" x2="252.086311" y2="146.560000" style="stroke:rgb(0,0,255);stroke-width:0.50" />\n<line x1="251.086311" y1="65.560000" x2="251.086311" y2="146.560000" style="stroke:rgb(0,0,255);stroke-width:0.50" /> \n  <polygon points="251.086311,146.560000 252.086311,143.560000 251.086311,142.560000 250.086311,143.560000" style="fill:rgb(0,0,255);stroke:rgb(0,0,255);stroke-width:0" /><polygon points="251.086311,65.560000 250.086311,68.560000 251.086311,69.560000 252.086311,68.560000" style="fill:rgb(0,0,255);stroke:rgb(0,0,255);stroke-width:0" /> \n  <text x="249.086311" y="106.060000" font-family="inherit" font-size="3.6" fill="rgb(0,0,255)" text-anchor="middle" transform="rotate(-90.000000 249.086311,106.060000)" >81</text> </g>
  Visible = true
  X = 0
  Y = 0
  arrowL1 = 3
  arrowL2 = 1
  arrowW = 2
  arrow_scheme = 0
  autoPlaceOffset = 2
  autoPlaceText = true
  click1_x = 251.086
  click1_y = 144.896
  click2_x = 251.086
  click2_y = 144.896
  comma_decimal_place = false
  dimension_line_overshoot = 1
  gap_datum_points = 2
  halfDimension_linear = false
  lineColor = rgb(0,0,255)
  strokeWidth = 0.5
  textFormat_linear = %(value)3.3f
  textRenderer_color = rgb(0,0,255)
  textRenderer_family = inherit
  textRenderer_size = 3.6
  unit_custom_scale = 1
  unit_scheme = 0
FEATURE [Drawing::FeatureViewPython] dim019  # drawing view (typed FeaturePython)
  Rotation = 0
  ViewResult = <g> \n  <line x1="102.000000" y1="144.560000" x2="102.000000" y2="138.543928" style="stroke:rgb(0,0,255);stroke-width:0.50" />\n<line x1="80.000000" y1="138.544000" x2="80.000000" y2="140.543928" style="stroke:rgb(0,0,255);stroke-width:0.50" />\n<line x1="102.000000" y1="139.543928" x2="80.000000" y2="139.543928" style="stroke:rgb(0,0,255);stroke-width:0.50" /> \n  <polygon points="80.000000,139.543928 83.000000,140.543928 84.000000,139.543928 83.000000,138.543928" style="fill:rgb(0,0,255);stroke:rgb(0,0,255);stroke-width:0" /><polygon points="102.000000,139.543928 99.000000,138.543928 98.000000,139.543928 99.000000,140.543928" style="fill:rgb(0,0,255);stroke:rgb(0,0,255);stroke-width:0" /> \n  <text x="91.000000" y="137.543928" font-family="inherit" font-size="3.6" fill="rgb(0,0,255)" text-anchor="middle" transform="rotate(0.000000 91.000000,137.543928)" >22</text> </g>
  Visible = true
  X = 0
  Y = 0
  arrowL1 = 3
  arrowL2 = 1
  arrowW = 2
  arrow_scheme = 0
  autoPlaceOffset = 2
  autoPlaceText = true
  click1_x = 86.3184
  click1_y = 139.544
  click2_x = 86.3184
  click2_y = 139.544
  comma_decimal_place = false
  dimension_line_overshoot = 1
  gap_datum_points = 2
  halfDimension_linear = false
  lineColor = rgb(0,0,255)
  strokeWidth = 0.5
  textFormat_linear = %(value)3.3f
  textRenderer_color = rgb(0,0,255)
  textRenderer_family = inherit
  textRenderer_size = 3.6
  unit_custom_scale = 1
  unit_scheme = 0
FEATURE [Drawing::FeatureViewPython] dim020  # drawing view (typed FeaturePython)
  Rotation = 0
  ViewResult = <g> \n  <line x1="198.000000" y1="144.560000" x2="198.000000" y2="138.156375" style="stroke:rgb(0,0,255);stroke-width:0.50" />\n<line x1="220.000000" y1="138.544000" x2="220.000000" y2="140.156375" style="stroke:rgb(0,0,255);stroke-width:0.50" />\n<line x1="198.000000" y1="139.156375" x2="220.000000" y2="139.156375" style="stroke:rgb(0,0,255);stroke-width:0.50" /> \n  <polygon points="220.000000,139.156375 217.000000,138.156375 216.000000,139.156375 217.000000,140.156375" style="fill:rgb(0,0,255);stroke:rgb(0,0,255);stroke-width:0" /><polygon points="198.000000,139.156375 201.000000,140.156375 202.000000,139.156375 201.000000,138.156375" style="fill:rgb(0,0,255);stroke:rgb(0,0,255);stroke-width:0" /> \n  <text x="209.000000" y="137.156375" font-family="inherit" font-size="3.6" fill="rgb(0,0,255)" text-anchor="middle" transform="rotate(0.000000 209.000000,137.156375)" >22</text> </g>
  Visible = true
  X = 0
  Y = 0
  arrowL1 = 3
  arrowL2 = 1
  arrowW = 2
  arrow_scheme = 0
  autoPlaceOffset = 2
  autoPlaceText = true
  click1_x = 218.338
  click1_y = 139.156
  click2_x = 218.338
  click2_y = 139.156
  comma_decimal_place = false
  dimension_line_overshoot = 1
  gap_datum_points = 2
  halfDimension_linear = false
  lineColor = rgb(0,0,255)
  strokeWidth = 0.5
  textFormat_linear = %(value)3.3f
  textRenderer_color = rgb(0,0,255)
  textRenderer_family = inherit
  textRenderer_size = 3.6
  unit_custom_scale = 1
  unit_scheme = 0
FEATURE [Drawing::FeatureViewPython] dia001  # drawing view (typed FeaturePython)
  Rotation = 0
  ViewResult = <g>  <circle cx ="102.000000" cy ="146.560000" r="0.250000" stroke="none" fill="rgb(0,0,255)" /> \n<line x1="107.846191" y1="141.113262" x2="100.463512" y2="147.991504" style="stroke:rgb(0,0,255);stroke-width:0.50" />\n<polygon points="103.536488,145.128496 106.413140,143.815150 106.463132,142.401821 105.049802,142.351829" style="fill:rgb(0,0,255);stroke:rgb(0,0,255);stroke-width:0" />\n<polygon points="100.463512,147.991504 97.586860,149.304850 97.536868,150.718179 98.950198,150.768171" style="fill:rgb(0,0,255);stroke:rgb(0,0,255);stroke-width:0" />\n<line x1="107.846191" y1="141.113262" x2="115.238873" y2="141.113262" style="stroke:rgb(0,0,255);stroke-width:0.50" />\n<text x="111.542532" y="139.113262" font-family="inherit" font-size="3.6" fill="rgb(0,0,255)" text-anchor="middle" transform="rotate(0.000000 111.542532,139.113262)" >Ø4.2</text> </g>
  Visible = true
  X = 0
  Y = 0
  arrowL1 = 3
  arrowL2 = 1
  arrowW = 2
  arrow_scheme = 0
  autoPlaceOffset = 2
  autoPlaceText = true
  centerPointDia = 0.5
  click1_x = 107.846
  click1_y = 141.113
  click2_x = 115.239
  click2_y = 141.113
  click3_x = 115.239
  click3_y = 141.113
  comma_decimal_place = false
  lineColor = rgb(0,0,255)
  strokeWidth = 0.5
  textFormat_circular = Ø%(value)3.3f
  textRenderer_color = rgb(0,0,255)
  textRenderer_family = inherit
  textRenderer_size = 3.6
  unit_custom_scale = 1
  unit_scheme = 0
FEATURE [Drawing::FeatureViewPython] text001  # drawing view (typed FeaturePython)
  Rotation = 0
  ViewResult = <g> <text x="109.066180" y="144.483051" font-family="inherit" font-size="3,6" fill="rgb(0,0,255)" text-anchor="inherit" transform="rotate(0.000000 109.066180,144.483051)" >H1</text> </g>
  Visible = true
  X = 0
  Y = 0
  click1_x = 109.066
  click1_y = 144.483
  rotation = 0
  text = H1
  textRenderer_addText_color = rgb(0,0,255)
  textRenderer_addText_family = inherit
  textRenderer_addText_size = 3,6
FEATURE [Drawing::FeatureViewPython] dia002  # drawing view (typed FeaturePython)
  Rotation = 0
  ViewResult = <g>  <circle cx ="198.000000" cy ="146.560000" r="0.250000" stroke="none" fill="rgb(0,0,255)" /> \n<line x1="193.524401" y1="141.557185" x2="199.400164" y2="148.125101" style="stroke:rgb(0,0,255);stroke-width:0.50" />\n<polygon points="196.599836,144.994899 195.344887,142.092297 193.932856,142.013755 193.854315,143.425786" style="fill:rgb(0,0,255);stroke:rgb(0,0,255);stroke-width:0" />\n<polygon points="199.400164,148.125101 200.655113,151.027703 202.067144,151.106245 202.145685,149.694214" style="fill:rgb(0,0,255);stroke:rgb(0,0,255);stroke-width:0" />\n<line x1="193.524401" y1="141.557185" x2="186.603827" y2="141.557185" style="stroke:rgb(0,0,255);stroke-width:0.50" />\n<text x="190.064114" y="139.557185" font-family="inherit" font-size="3.6" fill="rgb(0,0,255)" text-anchor="middle" transform="rotate(0.000000 190.064114,139.557185)" >Ø4.2</text> </g>
  Visible = true
  X = 0
  Y = 0
  arrowL1 = 3
  arrowL2 = 1
  arrowW = 2
  arrow_scheme = 0
  autoPlaceOffset = 2
  autoPlaceText = true
  centerPointDia = 0.5
  click1_x = 193.524
  click1_y = 141.557
  click2_x = 186.604
  click2_y = 141.18
  click3_x = 186.604
  click3_y = 141.18
  comma_decimal_place = false
  lineColor = rgb(0,0,255)
  strokeWidth = 0.5
  textFormat_circular = Ø%(value)3.3f
  textRenderer_color = rgb(0,0,255)
  textRenderer_family = inherit
  textRenderer_size = 3.6
  unit_custom_scale = 2.6
  unit_scheme = 0
FEATURE [Drawing::FeatureViewPython] text002  # drawing view (typed FeaturePython)
  Rotation = 0
  ViewResult = <g> <text x="187.383965" y="144.954558" font-family="inherit" font-size="3,6" fill="rgb(0,0,255)" text-anchor="inherit" transform="rotate(0.000000 187.383965,144.954558)" >H1</text> </g>
  Visible = true
  X = 0
  Y = 0
  click1_x = 187.384
  click1_y = 144.955
  rotation = 0
  text = H1
  textRenderer_addText_color = rgb(0,0,255)
  textRenderer_addText_family = inherit
  textRenderer_addText_size = 3,6
FEATURE [Drawing::FeatureViewPython] dia003  # drawing view (typed FeaturePython)
  Rotation = 0
  ViewResult = <g>  <circle cx ="122.000000" cy ="101.570000" r="0.250000" stroke="none" fill="rgb(0,0,255)" /> \n<line x1="131.328829" y1="101.540668" x2="119.900010" y2="101.576603" style="stroke:rgb(0,0,255);stroke-width:0.50" />\n<polygon points="124.099990,101.563397 127.103119,102.553959 128.099970,101.550820 127.096831,100.553969" style="fill:rgb(0,0,255);stroke:rgb(0,0,255);stroke-width:0" />\n<polygon points="119.900010,101.576603 116.896881,100.586041 115.900030,101.589180 116.903169,102.586031" style="fill:rgb(0,0,255);stroke:rgb(0,0,255);stroke-width:0" />\n<line x1="131.328829" y1="101.540668" x2="136.547193" y2="101.540668" style="stroke:rgb(0,0,255);stroke-width:0.50" />\n<text x="133.938011" y="99.540668" font-family="inherit" font-size="3.6" fill="rgb(0,0,255)" text-anchor="middle" transform="rotate(0.000000 133.938011,99.540668)" >Ø4.2</text> </g>
  Visible = true
  X = 0
  Y = 0
  arrowL1 = 3
  arrowL2 = 1
  arrowW = 2
  arrow_scheme = 0
  autoPlaceOffset = 2
  autoPlaceText = true
  centerPointDia = 0.5
  click1_x = 131.329
  click1_y = 101.541
  click2_x = 136.547
  click2_y = 101.758
  click3_x = 136.547
  click3_y = 101.758
  comma_decimal_place = false
  lineColor = rgb(0,0,255)
  strokeWidth = 0.5
  textFormat_circular = Ø%(value)3.3f
  textRenderer_color = rgb(0,0,255)
  textRenderer_family = inherit
  textRenderer_size = 3.6
  unit_custom_scale = 2.6
  unit_scheme = 0
FEATURE [Drawing::FeatureViewPython] dia004  # drawing view (typed FeaturePython)
  Rotation = 0
  ViewResult = <g>  <circle cx ="178.000000" cy ="101.570000" r="0.250000" stroke="none" fill="rgb(0,0,255)" /> \n<line x1="169.596833" y1="101.758100" x2="180.099474" y2="101.523005" style="stroke:rgb(0,0,255);stroke-width:0.50" />\n<polygon points="175.900526,101.616995 172.878898,100.684382 171.901528,101.706510 172.923656,102.683881" style="fill:rgb(0,0,255);stroke:rgb(0,0,255);stroke-width:0" />\n<polygon points="180.099474,101.523005 183.121102,102.455618 184.098472,101.433490 183.076344,100.456119" style="fill:rgb(0,0,255);stroke:rgb(0,0,255);stroke-width:0" />\n<line x1="169.596833" y1="101.758100" x2="162.421582" y2="101.758100" style="stroke:rgb(0,0,255);stroke-width:0.50" />\n<text x="166.009207" y="99.758100" font-family="inherit" font-size="3.6" fill="rgb(0,0,255)" text-anchor="middle" transform="rotate(0.000000 166.009207,99.758100)" >Ø4.2</text> </g>
  Visible = true
  X = 0
  Y = 0
  arrowL1 = 3
  arrowL2 = 1
  arrowW = 2
  arrow_scheme = 0
  autoPlaceOffset = 2
  autoPlaceText = true
  centerPointDia = 0.5
  click1_x = 169.597
  click1_y = 101.758
  click2_x = 162.422
  click2_y = 100.888
  click3_x = 162.422
  click3_y = 100.888
  comma_decimal_place = false
  lineColor = rgb(0,0,255)
  strokeWidth = 0.5
  textFormat_circular = Ø%(value)3.3f
  textRenderer_color = rgb(0,0,255)
  textRenderer_family = inherit
  textRenderer_size = 3.6
  unit_custom_scale = 2.6
  unit_scheme = 0
FEATURE [Drawing::FeatureViewPython] text003  # drawing view (typed FeaturePython)
  Rotation = 0
  ViewResult = <g> <text x="130.241670" y="105.019577" font-family="inherit" font-size="3,6" fill="rgb(0,0,255)" text-anchor="inherit" transform="rotate(0.000000 130.241670,105.019577)" >H1</text> </g>
  Visible = true
  X = 0
  Y = 0
  click1_x = 130.242
  click1_y = 105.02
  rotation = 0
  text = H1
  textRenderer_addText_color = rgb(0,0,255)
  textRenderer_addText_family = inherit
  textRenderer_addText_size = 3,6
FEATURE [Drawing::FeatureViewPython] text004  # drawing view (typed FeaturePython)
  Rotation = 0
  ViewResult = <g> <text x="164.161037" y="105.019577" font-family="inherit" font-size="3,6" fill="rgb(0,0,255)" text-anchor="inherit" transform="rotate(0.000000 164.161037,105.019577)" >H1</text> </g>
  Visible = true
  X = 0
  Y = 0
  click1_x = 164.161
  click1_y = 105.02
  rotation = 0
  text = H1
  textRenderer_addText_color = rgb(0,0,255)
  textRenderer_addText_family = inherit
  textRenderer_addText_size = 3,6
FEATURE [Drawing::FeatureViewPython] dia005  # drawing view (typed FeaturePython)
  Rotation = 0
  ViewResult = <g>  <circle cx ="150.000000" cy ="65.560000" r="0.250000" stroke="none" fill="rgb(0,0,255)" /> \n<line x1="149.906723" y1="52.636287" x2="150.019848" y2="68.309928" style="stroke:rgb(0,0,255);stroke-width:0.50" />\n<polygon points="149.980152,62.810072 150.958474,59.802932 149.951283,58.810176 148.958526,59.817367" style="fill:rgb(0,0,255);stroke:rgb(0,0,255);stroke-width:0" />\n<polygon points="150.019848,68.309928 149.041526,71.317068 150.048717,72.309824 151.041474,71.302633" style="fill:rgb(0,0,255);stroke:rgb(0,0,255);stroke-width:0" />\n<line x1="149.906723" y1="52.636287" x2="141.726759" y2="52.636287" style="stroke:rgb(0,0,255);stroke-width:0.50" />\n<text x="145.816741" y="50.636287" font-family="inherit" font-size="3.6" fill="rgb(0,0,255)" text-anchor="middle" transform="rotate(0.000000 145.816741,50.636287)" >Ø5.5</text> </g>
  Visible = true
  X = 0
  Y = 0
  arrowL1 = 3
  arrowL2 = 1
  arrowW = 2
  arrow_scheme = 0
  autoPlaceOffset = 2
  autoPlaceText = true
  centerPointDia = 0.5
  click1_x = 149.907
  click1_y = 52.6363
  click2_x = 141.727
  click2_y = 47.1237
  click3_x = 141.727
  click3_y = 47.1237
  comma_decimal_place = false
  lineColor = rgb(0,0,255)
  strokeWidth = 0.5
  textFormat_circular = Ø%(value)3.3f
  textRenderer_color = rgb(0,0,255)
  textRenderer_family = inherit
  textRenderer_size = 3.6
  unit_custom_scale = 2.6
  unit_scheme = 0
FEATURE [Drawing::FeatureViewPython] dia006  # drawing view (typed FeaturePython)
  Rotation = 0
  ViewResult = <g>  <circle cx ="178.000000" cy ="65.560000" r="0.250000" stroke="none" fill="rgb(0,0,255)" /> \n<line x1="177.647469" y1="53.525413" x2="178.080522" y2="68.308821" style="stroke:rgb(0,0,255);stroke-width:0.50" />\n<polygon points="177.919478,62.811179 178.831208,59.783185 177.802356,58.812894 176.832065,59.841746" style="fill:rgb(0,0,255);stroke:rgb(0,0,255);stroke-width:0" />\n<polygon points="178.080522,68.308821 177.168792,71.336815 178.197644,72.307106 179.167935,71.278254" style="fill:rgb(0,0,255);stroke:rgb(0,0,255);stroke-width:0" />\n<line x1="177.647469" y1="53.525413" x2="167.867077" y2="53.525413" style="stroke:rgb(0,0,255);stroke-width:0.50" />\n<text x="172.757273" y="51.525413" font-family="inherit" font-size="3.6" fill="rgb(0,0,255)" text-anchor="middle" transform="rotate(0.000000 172.757273,51.525413)" >Ø5.5</text> </g>
  Visible = true
  X = 0
  Y = 0
  arrowL1 = 3
  arrowL2 = 1
  arrowW = 2
  arrow_scheme = 0
  autoPlaceOffset = 2
  autoPlaceText = true
  centerPointDia = 0.5
  click1_x = 177.647
  click1_y = 53.5254
  click2_x = 167.867
  click2_y = 52.9919
  click3_x = 167.867
  click3_y = 52.9919
  comma_decimal_place = false
  lineColor = rgb(0,0,255)
  strokeWidth = 0.5
  textFormat_circular = Ø%(value)3.3f
  textRenderer_color = rgb(0,0,255)
  textRenderer_family = inherit
  textRenderer_size = 3.6
  unit_custom_scale = 2.6
  unit_scheme = 0
FEATURE [Drawing::FeatureViewPython] dia007  # drawing view (typed FeaturePython)
  Rotation = 0
  ViewResult = <g>  <circle cx ="122.000000" cy ="65.560000" r="0.250000" stroke="none" fill="rgb(0,0,255)" /> \n<line x1="121.988152" y1="52.102811" x2="122.002421" y2="68.309999" style="stroke:rgb(0,0,255);stroke-width:0.50" />\n<polygon points="121.997579,62.810001 122.994937,59.809122 121.994057,58.810003 120.994938,59.810883" style="fill:rgb(0,0,255);stroke:rgb(0,0,255);stroke-width:0" />\n<polygon points="122.002421,68.309999 121.005063,71.310878 122.005943,72.309997 123.005062,71.309117" style="fill:rgb(0,0,255);stroke:rgb(0,0,255);stroke-width:0" />\n<line x1="121.988152" y1="52.102811" x2="130.523766" y2="52.102811" style="stroke:rgb(0,0,255);stroke-width:0.50" />\n<text x="126.255959" y="50.102811" font-family="inherit" font-size="3.6" fill="rgb(0,0,255)" text-anchor="middle" transform="rotate(0.000000 126.255959,50.102811)" >Ø5.5</text> </g>
  Visible = true
  X = 0
  Y = 0
  arrowL1 = 3
  arrowL2 = 1
  arrowW = 2
  arrow_scheme = 0
  autoPlaceOffset = 2
  autoPlaceText = true
  centerPointDia = 0.5
  click1_x = 121.988
  click1_y = 52.1028
  click2_x = 130.524
  click2_y = 52.2806
  click3_x = 130.524
  click3_y = 52.2806
  comma_decimal_place = false
  lineColor = rgb(0,0,255)
  strokeWidth = 0.5
  textFormat_circular = Ø%(value)3.3f
  textRenderer_color = rgb(0,0,255)
  textRenderer_family = inherit
  textRenderer_size = 3.6
  unit_custom_scale = 2.6
  unit_scheme = 0
FEATURE [Drawing::FeatureViewPython] text005  # drawing view (typed FeaturePython)
  Rotation = 0
  ViewResult = <g> <text x="123.944230" y="55.481492" font-family="inherit" font-size="3,6" fill="rgb(0,0,255)" text-anchor="inherit" transform="rotate(0.000000 123.944230,55.481492)" >H3</text> </g>
  Visible = true
  X = 0
  Y = 0
  click1_x = 123.944
  click1_y = 55.4815
  rotation = 0
  text = H3
  textRenderer_addText_color = rgb(0,0,255)
  textRenderer_addText_family = inherit
  textRenderer_addText_size = 3,6
FEATURE [Drawing::FeatureViewPython] text006  # drawing view (typed FeaturePython)
  Rotation = 0
  ViewResult = <g> <text x="142.971536" y="55.837142" font-family="inherit" font-size="3,6" fill="rgb(0,0,255)" text-anchor="inherit" transform="rotate(0.000000 142.971536,55.837142)" >H3</text> </g>
  Visible = true
  X = 0
  Y = 0
  click1_x = 142.972
  click1_y = 55.8371
  rotation = 0
  text = H3
  textRenderer_addText_color = rgb(0,0,255)
  textRenderer_addText_family = inherit
  textRenderer_addText_size = 3,6
FEATURE [Drawing::FeatureViewPython] text007  # drawing view (typed FeaturePython)
  Rotation = 0
  ViewResult = <g> <text x="170.712282" y="56.726269" font-family="inherit" font-size="3,6" fill="rgb(0,0,255)" text-anchor="inherit" transform="rotate(0.000000 170.712282,56.726269)" >H3</text> </g>
  Visible = true
  X = 0
  Y = 0
  click1_x = 170.712
  click1_y = 56.7263
  rotation = 0
  text = H3
  textRenderer_addText_color = rgb(0,0,255)
  textRenderer_addText_family = inherit
  textRenderer_addText_size = 3,6
FEATURE [Drawing::FeatureViewPython] dia008  # drawing view (typed FeaturePython)
  Rotation = 0
  ViewResult = <g>  <circle cx ="122.000000" cy ="86.560000" r="0.250000" stroke="none" fill="rgb(0,0,255)" /> \n<line x1="130.168115" y1="84.075799" x2="118.555769" y2="87.607508" style="stroke:rgb(0,0,255);stroke-width:0.50" />\n<polygon points="125.444231,85.512492 128.605398,85.596300 129.271155,84.348595 128.023449,83.682839" style="fill:rgb(0,0,255);stroke:rgb(0,0,255);stroke-width:0" />\n<polygon points="118.555769,87.607508 115.394602,87.523700 114.728845,88.771405 115.976551,89.437161" style="fill:rgb(0,0,255);stroke:rgb(0,0,255);stroke-width:0" />\n<line x1="130.168115" y1="84.075799" x2="140.624242" y2="84.075799" style="stroke:rgb(0,0,255);stroke-width:0.50" />\n<text x="135.396179" y="82.075799" font-family="inherit" font-size="3.6" fill="rgb(0,0,255)" text-anchor="middle" transform="rotate(0.000000 135.396179,82.075799)" >Ø7.2</text> </g>
  Visible = true
  X = 0
  Y = 0
  arrowL1 = 3
  arrowL2 = 1
  arrowW = 2
  arrow_scheme = 0
  autoPlaceOffset = 2
  autoPlaceText = true
  centerPointDia = 0.5
  click1_x = 130.168
  click1_y = 84.0758
  click2_x = 140.624
  click2_y = 84.2892
  click3_x = 140.624
  click3_y = 84.2892
  comma_decimal_place = false
  lineColor = rgb(0,0,255)
  strokeWidth = 0.5
  textFormat_circular = Ø%(value)3.3f
  textRenderer_color = rgb(0,0,255)
  textRenderer_family = inherit
  textRenderer_size = 3.6
  unit_custom_scale = 2.6
  unit_scheme = 0
FEATURE [Drawing::FeatureViewPython] dia009  # drawing view (typed FeaturePython)
  Rotation = 0
  ViewResult = <g>  <circle cx ="178.000000" cy ="86.560000" r="0.250000" stroke="none" fill="rgb(0,0,255)" /> \n<line x1="170.498892" y1="83.435628" x2="181.323248" y2="87.944204" style="stroke:rgb(0,0,255);stroke-width:0.50" />\n<polygon points="174.676752,85.175796 172.291879,83.099168 170.984254,83.637791 171.522877,84.945417" style="fill:rgb(0,0,255);stroke:rgb(0,0,255);stroke-width:0" />\n<polygon points="181.323248,87.944204 183.708121,90.020832 185.015746,89.482209 184.477123,88.174583" style="fill:rgb(0,0,255);stroke:rgb(0,0,255);stroke-width:0" />\n<line x1="170.498892" y1="83.435628" x2="160.256155" y2="83.435628" style="stroke:rgb(0,0,255);stroke-width:0.50" />\n<text x="165.377523" y="81.435628" font-family="inherit" font-size="3.6" fill="rgb(0,0,255)" text-anchor="middle" transform="rotate(0.000000 165.377523,81.435628)" >Ø7.2</text> </g>
  Visible = true
  X = 0
  Y = 0
  arrowL1 = 3
  arrowL2 = 1
  arrowW = 2
  arrow_scheme = 0
  autoPlaceOffset = 2
  autoPlaceText = true
  centerPointDia = 0.5
  click1_x = 170.499
  click1_y = 83.4356
  click2_x = 160.256
  click2_y = 83.2222
  click3_x = 160.256
  click3_y = 83.2222
  comma_decimal_place = false
  lineColor = rgb(0,0,255)
  strokeWidth = 0.5
  textFormat_circular = Ø%(value)3.3f
  textRenderer_color = rgb(0,0,255)
  textRenderer_family = inherit
  textRenderer_size = 3.6
  unit_custom_scale = 2.6
  unit_scheme = 0
FEATURE [Drawing::FeatureViewPython] text008  # drawing view (typed FeaturePython)
  Rotation = 0
  ViewResult = <g> <text x="132.942190" y="87.276654" font-family="inherit" font-size="3,6" fill="rgb(0,0,255)" text-anchor="inherit" transform="rotate(0.000000 132.942190,87.276654)" >H2</text> </g>
  Visible = true
  X = 0
  Y = 0
  click1_x = 132.942
  click1_y = 87.2767
  rotation = 0
  text = H2
  textRenderer_addText_color = rgb(0,0,255)
  textRenderer_addText_family = inherit
  textRenderer_addText_size = 3,6
FEATURE [Drawing::FeatureViewPython] text009  # drawing view (typed FeaturePython)
  Rotation = 0
  ViewResult = <g> <text x="163.030229" y="86.849874" font-family="inherit" font-size="3,6" fill="rgb(0,0,255)" text-anchor="inherit" transform="rotate(0.000000 163.030229,86.849874)" >H2</text> </g>
  Visible = true
  X = 0
  Y = 0
  click1_x = 163.03
  click1_y = 86.8499
  rotation = 0
  text = H2
  textRenderer_addText_color = rgb(0,0,255)
  textRenderer_addText_family = inherit
  textRenderer_addText_size = 3,6
FEATURE [Drawing::FeatureViewPython] text010  # drawing view (typed FeaturePython)
  Rotation = 0
  ViewResult = <g> <text x="20.000000" y="270.000000" font-family="inherit" font-size="10" fill="rgb(0,0,255)" text-anchor="inherit" transform="rotate(0.000000 20.000000,270.000000)" >Material: aluminium 8mm</text> </g>
  Visible = true
  X = 0
  Y = 0
  click1_x = 20
  click1_y = 270
  rotation = 0
  text = Material: aluminium 8mm
  textRenderer_addText_color = rgb(0,0,255)
  textRenderer_addText_family = inherit
  textRenderer_addText_size = 10
FEATURE [Drawing::FeatureViewPython] table001  # drawing view (typed FeaturePython)
  Rotation = 0
  ViewResult = <blob: 3741 chars omitted>
  Visible = true
  X = 0
  Y = 0
  border_color = rgb(0,0,0)
  border_width = 0.3
  click1_x = 270
  click1_y = 190
  column_widths = [20,20,20,24,22]
  contents = Ref | Metric | Drill | Threaded | Direction | H1 | M5 | 4.2 | Yes | CCW | H2 | - | 7.2 | No | - | H3 | M5 | 5.5 | No | -
  extra_rows = 0
  padding_x = 1
  padding_y = 1
  row_heights = [7]
  textRenderer_table_color = rgb(0,0,0)
  textRenderer_table_family = inherit
  textRenderer_table_size = 5
FEATURE [Drawing::FeatureViewPython] dim021  # drawing view (typed FeaturePython)
  Rotation = 0
  ViewResult = <g> \n  <line x1="113.563320" y1="201.092000" x2="113.563320" y2="213.762131" style="stroke:rgb(0,0,255);stroke-width:0.50" />\n<line x1="145.963320" y1="201.092000" x2="145.963320" y2="213.762131" style="stroke:rgb(0,0,255);stroke-width:0.50" />\n<line x1="113.563320" y1="212.762131" x2="145.963320" y2="212.762131" style="stroke:rgb(0,0,255);stroke-width:0.50" /> \n  <polygon points="145.963320,212.762131 142.963320,211.762131 141.963320,212.762131 142.963320,213.762131" style="fill:rgb(0,0,255);stroke:rgb(0,0,255);stroke-width:0" /><polygon points="113.563320,212.762131 116.563320,213.762131 117.563320,212.762131 116.563320,211.762131" style="fill:rgb(0,0,255);stroke:rgb(0,0,255);stroke-width:0" /> \n  <text x="129.763320" y="210.762131" font-family="inherit" font-size="3.6" fill="rgb(0,0,255)" text-anchor="middle" transform="rotate(0.000000 129.763320,210.762131)" >27</text> </g>
  Visible = false
  X = 0
  Y = 0
  arrowL1 = 3
  arrowL2 = 1
  arrowW = 2
  arrow_scheme = 0
  autoPlaceOffset = 2
  autoPlaceText = true
  click1_x = 150.814
  click1_y = 212.762
  click2_x = 150.814
  click2_y = 212.762
  comma_decimal_place = false
  dimension_line_overshoot = 1
  gap_datum_points = 2
  halfDimension_linear = false
  lineColor = rgb(0,0,255)
  strokeWidth = 0.5
  textFormat_linear = %(value)3.3f
  textRenderer_color = rgb(0,0,255)
  textRenderer_family = inherit
  textRenderer_size = 3.6
  unit_custom_scale = 1
  unit_scheme = 0
FEATURE [Drawing::FeatureViewPython] dim022  # drawing view (typed FeaturePython)
  Rotation = 0
  ViewResult = <g> \n  <line x1="147.963320" y1="199.092000" x2="162.876214" y2="199.092000" style="stroke:rgb(0,0,255);stroke-width:0.50" />\n<line x1="147.963320" y1="123.840000" x2="162.876214" y2="123.840000" style="stroke:rgb(0,0,255);stroke-width:0.50" />\n<line x1="161.876214" y1="199.092000" x2="161.876214" y2="123.840000" style="stroke:rgb(0,0,255);stroke-width:0.50" /> \n  <polygon points="161.876214,123.840000 160.876214,126.840000 161.876214,127.840000 162.876214,126.840000" style="fill:rgb(0,0,255);stroke:rgb(0,0,255);stroke-width:0" /><polygon points="161.876214,199.092000 162.876214,196.092000 161.876214,195.092000 160.876214,196.092000" style="fill:rgb(0,0,255);stroke:rgb(0,0,255);stroke-width:0" /> \n  <text x="159.876214" y="161.466000" font-family="inherit" font-size="3.6" fill="rgb(0,0,255)" text-anchor="middle" transform="rotate(-90.000000 159.876214,161.466000)" >62.71</text> </g>
  Visible = false
  X = 0
  Y = 0
  arrowL1 = 3
  arrowL2 = 1
  arrowW = 2
  arrow_scheme = 0
  autoPlaceOffset = 2
  autoPlaceText = true
  click1_x = 161.876
  click1_y = 129.427
  click2_x = 161.876
  click2_y = 129.427
  comma_decimal_place = false
  dimension_line_overshoot = 1
  gap_datum_points = 2
  halfDimension_linear = false
  lineColor = rgb(0,0,255)
  strokeWidth = 0.5
  textFormat_linear = %(value)3.3f
  textRenderer_color = rgb(0,0,255)
  textRenderer_family = inherit
  textRenderer_size = 3.6
  unit_custom_scale = 1
  unit_scheme = 0
FEATURE [Drawing::FeatureViewPython] dim023  # drawing view (typed FeaturePython)
  Rotation = 0
  ViewResult = <g> \n  <line x1="111.563320" y1="199.092000" x2="72.378967" y2="199.092000" style="stroke:rgb(0,0,255);stroke-width:0.50" />\n<line x1="111.563320" y1="32.472000" x2="72.378967" y2="32.472000" style="stroke:rgb(0,0,255);stroke-width:0.50" />\n<line x1="73.378967" y1="199.092000" x2="73.378967" y2="32.472000" style="stroke:rgb(0,0,255);stroke-width:0.50" /> \n  <polygon points="73.378967,32.472000 72.378967,35.472000 73.378967,36.472000 74.378967,35.472000" style="fill:rgb(0,0,255);stroke:rgb(0,0,255);stroke-width:0" /><polygon points="73.378967,199.092000 74.378967,196.092000 73.378967,195.092000 72.378967,196.092000" style="fill:rgb(0,0,255);stroke:rgb(0,0,255);stroke-width:0" /> \n  <text x="71.378967" y="115.782000" font-family="inherit" font-size="3.6" fill="rgb(0,0,255)" text-anchor="middle" transform="rotate(-90.000000 71.378967,115.782000)" >138.85</text> </g>
  Visible = false
  X = 0
  Y = 0
  arrowL1 = 3
  arrowL2 = 1
  arrowW = 2
  arrow_scheme = 0
  autoPlaceOffset = 2
  autoPlaceText = true
  click1_x = 73.379
  click1_y = 40.5612
  click2_x = 73.379
  click2_y = 40.5612
  comma_decimal_place = false
  dimension_line_overshoot = 1
  gap_datum_points = 2
  halfDimension_linear = false
  lineColor = rgb(0,0,255)
  strokeWidth = 0.5
  textFormat_linear = %(value)3.3f
  textRenderer_color = rgb(0,0,255)
  textRenderer_family = inherit
  textRenderer_size = 3.6
  unit_custom_scale = 1
  unit_scheme = 0
FEATURE [Drawing::FeatureViewPython] dim024  # drawing view (typed FeaturePython)
  Rotation = 0
  ViewResult = <g> \n  <line x1="142.010000" y1="32.472000" x2="162.880620" y2="32.472000" style="stroke:rgb(0,0,255);stroke-width:0.50" />\n<line x1="142.010000" y1="118.692000" x2="162.880620" y2="118.692000" style="stroke:rgb(0,0,255);stroke-width:0.50" />\n<line x1="161.880620" y1="32.472000" x2="161.880620" y2="118.692000" style="stroke:rgb(0,0,255);stroke-width:0.50" /> \n  <polygon points="161.880620,118.692000 162.880620,115.692000 161.880620,114.692000 160.880620,115.692000" style="fill:rgb(0,0,255);stroke:rgb(0,0,255);stroke-width:0" /><polygon points="161.880620,32.472000 160.880620,35.472000 161.880620,36.472000 162.880620,35.472000" style="fill:rgb(0,0,255);stroke:rgb(0,0,255);stroke-width:0" /> \n  <text x="159.880620" y="75.582000" font-family="inherit" font-size="3.6" fill="rgb(0,0,255)" text-anchor="middle" transform="rotate(-90.000000 159.880620,75.582000)" >71.85</text> </g>
  Visible = false
  X = 0
  Y = 0
  arrowL1 = 3
  arrowL2 = 1
  arrowW = 2
  arrow_scheme = 0
  autoPlaceOffset = 2
  autoPlaceText = true
  click1_x = 161.881
  click1_y = 134.374
  click2_x = 161.881
  click2_y = 134.374
  comma_decimal_place = false
  dimension_line_overshoot = 1
  gap_datum_points = 2
  halfDimension_linear = false
  lineColor = rgb(0,0,255)
  strokeWidth = 0.5
  textFormat_linear = %(value)3.3f
  textRenderer_color = rgb(0,0,255)
  textRenderer_family = inherit
  textRenderer_size = 3.6
  unit_custom_scale = 1
  unit_scheme = 0
FEATURE [Drawing::FeatureViewPython] rad002  # drawing view (typed FeaturePython)
  Rotation = 0
  ViewResult = <g>  <circle cx ="147.209997" cy ="116.381991" r="0.250000" stroke="none" fill="rgb(0,0,255)" /> \n<line x1="152.396277" y1="107.762128" x2="147.209997" y2="116.381991" style="stroke:rgb(0,0,255);stroke-width:0.50" />\n<polygon points="151.108285,109.902836 148.704788,111.957878 149.046105,113.330286 150.418512,112.988968" style="fill:rgb(0,0,255);stroke:rgb(0,0,255);stroke-width:0" />\n<line x1="152.396277" y1="107.762128" x2="158.442337" y2="107.762128" style="stroke:rgb(0,0,255);stroke-width:0.50" />\n<text x="155.419307" y="105.762128" font-family="inherit" font-size="3.6" fill="rgb(0,0,255)" text-anchor="middle" transform="rotate(0.000000 155.419307,105.762128)" >R6.301</text> </g>
  Visible = false
  X = 0
  Y = 0
  arrowL1 = 3
  arrowL2 = 1
  arrowW = 2
  arrow_scheme = 0
  autoPlaceOffset = 2
  autoPlaceText = true
  centerPointDia = 0.5
  click1_x = 152.396
  click1_y = 107.762
  click2_x = 158.442
  click2_y = 107.406
  click3_x = 158.442
  click3_y = 107.406
  comma_decimal_place = false
  lineColor = rgb(0,0,255)
  strokeWidth = 0.5
  textFormat_radial = R%(value)3.3f
  textRenderer_color = rgb(0,0,255)
  textRenderer_family = inherit
  textRenderer_size = 3.6
  unit_custom_scale = 1
  unit_scheme = 0
FEATURE [Drawing::FeatureViewPython] dim025  # drawing view (typed FeaturePython)
  Rotation = 0
  ViewResult = <g> \n  <line x1="113.563320" y1="30.472000" x2="113.563320" y2="22.265476" style="stroke:rgb(0,0,255);stroke-width:0.50" />\n<line x1="140.010000" y1="30.472000" x2="140.010000" y2="22.265476" style="stroke:rgb(0,0,255);stroke-width:0.50" />\n<line x1="113.563320" y1="23.265476" x2="140.010000" y2="23.265476" style="stroke:rgb(0,0,255);stroke-width:0.50" /> \n  <polygon points="140.010000,23.265476 137.010000,22.265476 136.010000,23.265476 137.010000,24.265476" style="fill:rgb(0,0,255);stroke:rgb(0,0,255);stroke-width:0" /><polygon points="113.563320,23.265476 116.563320,24.265476 117.563320,23.265476 116.563320,22.265476" style="fill:rgb(0,0,255);stroke:rgb(0,0,255);stroke-width:0" /> \n  <text x="126.786660" y="21.265476" font-family="inherit" font-size="3.6" fill="rgb(0,0,255)" text-anchor="middle" transform="rotate(0.000000 126.786660,21.265476)" >22.039</text> </g>
  Visible = false
  X = 0
  Y = 0
  arrowL1 = 3
  arrowL2 = 1
  arrowW = 2
  arrow_scheme = 0
  autoPlaceOffset = 2
  autoPlaceText = true
  click1_x = 136.185
  click1_y = 23.2655
  click2_x = 136.185
  click2_y = 23.2655
  comma_decimal_place = false
  dimension_line_overshoot = 1
  gap_datum_points = 2
  halfDimension_linear = false
  lineColor = rgb(0,0,255)
  strokeWidth = 0.5
  textFormat_linear = %(value)3.3f
  textRenderer_color = rgb(0,0,255)
  textRenderer_family = inherit
  textRenderer_size = 3.6
  unit_custom_scale = 1
  unit_scheme = 0
FEATURE [Drawing::FeatureViewPython] dim026  # drawing view (typed FeaturePython)
  Rotation = 0
  ViewResult = <g> \n  <line x1="147.963320" y1="199.092000" x2="153.015928" y2="199.092000" style="stroke:rgb(0,0,255);stroke-width:0.50" />\n<line x1="144.363320" y1="195.492000" x2="153.015928" y2="195.492000" style="stroke:rgb(0,0,255);stroke-width:0.50" />\n<line x1="152.015928" y1="199.092000" x2="152.015928" y2="195.492000" style="stroke:rgb(0,0,255);stroke-width:0.50" /> \n  <polygon points="152.015928,195.492000 153.015928,192.492000 152.015928,191.492000 151.015928,192.492000" style="fill:rgb(0,0,255);stroke:rgb(0,0,255);stroke-width:0" /><polygon points="152.015928,199.092000 151.015928,202.092000 152.015928,203.092000 153.015928,202.092000" style="fill:rgb(0,0,255);stroke:rgb(0,0,255);stroke-width:0" /> \n  <text x="150.015928" y="197.292000" font-family="inherit" font-size="3.6" fill="rgb(0,0,255)" text-anchor="middle" transform="rotate(-90.000000 150.015928,197.292000)" >3</text> </g>
  Visible = false
  X = 0
  Y = 0
  arrowL1 = 3
  arrowL2 = 1
  arrowW = 2
  arrow_scheme = 0
  autoPlaceOffset = 2
  autoPlaceText = true
  click1_x = 152.016
  click1_y = 197.707
  click2_x = 152.016
  click2_y = 197.707
  comma_decimal_place = false
  dimension_line_overshoot = 1
  gap_datum_points = 2
  halfDimension_linear = false
  lineColor = rgb(0,0,255)
  strokeWidth = 0.5
  textFormat_linear = %(value)3.3f
  textRenderer_color = rgb(0,0,255)
  textRenderer_family = inherit
  textRenderer_size = 3.6
  unit_custom_scale = 1
  unit_scheme = 0
FEATURE [Drawing::FeatureViewPython] dim027  # drawing view (typed FeaturePython)
  Rotation = 0
  ViewResult = <g> \n  <line x1="144.363320" y1="195.492000" x2="153.003922" y2="195.492000" style="stroke:rgb(0,0,255);stroke-width:0.50" />\n<line x1="139.610000" y1="163.992000" x2="153.003922" y2="163.992000" style="stroke:rgb(0,0,255);stroke-width:0.50" />\n<line x1="152.003922" y1="195.492000" x2="152.003922" y2="163.992000" style="stroke:rgb(0,0,255);stroke-width:0.50" /> \n  <polygon points="152.003922,163.992000 151.003922,166.992000 152.003922,167.992000 153.003922,166.992000" style="fill:rgb(0,0,255);stroke:rgb(0,0,255);stroke-width:0" /><polygon points="152.003922,195.492000 153.003922,192.492000 152.003922,191.492000 151.003922,192.492000" style="fill:rgb(0,0,255);stroke:rgb(0,0,255);stroke-width:0" /> \n  <text x="150.003922" y="179.742000" font-family="inherit" font-size="3.6" fill="rgb(0,0,255)" text-anchor="middle" transform="rotate(-90.000000 150.003922,179.742000)" >26.25</text> </g>
  Visible = false
  X = 0
  Y = 0
  arrowL1 = 3
  arrowL2 = 1
  arrowW = 2
  arrow_scheme = 0
  autoPlaceOffset = 2
  autoPlaceText = true
  click1_x = 152.004
  click1_y = 171.371
  click2_x = 152.004
  click2_y = 171.371
  comma_decimal_place = false
  dimension_line_overshoot = 1
  gap_datum_points = 2
  halfDimension_linear = false
  lineColor = rgb(0,0,255)
  strokeWidth = 0.5
  textFormat_linear = %(value)3.3f
  textRenderer_color = rgb(0,0,255)
  textRenderer_family = inherit
  textRenderer_size = 3.6
  unit_custom_scale = 1
  unit_scheme = 0
FEATURE [Drawing::FeatureViewPython] dim028  # drawing view (typed FeaturePython)
  Rotation = 0
  ViewResult = <g> \n  <line x1="139.610000" y1="163.992000" x2="153.133630" y2="163.992000" style="stroke:rgb(0,0,255);stroke-width:0.50" />\n<line x1="139.610000" y1="148.392000" x2="153.133630" y2="148.392000" style="stroke:rgb(0,0,255);stroke-width:0.50" />\n<line x1="152.133630" y1="163.992000" x2="152.133630" y2="148.392000" style="stroke:rgb(0,0,255);stroke-width:0.50" /> \n  <polygon points="152.133630,148.392000 151.133630,151.392000 152.133630,152.392000 153.133630,151.392000" style="fill:rgb(0,0,255);stroke:rgb(0,0,255);stroke-width:0" /><polygon points="152.133630,163.992000 153.133630,160.992000 152.133630,159.992000 151.133630,160.992000" style="fill:rgb(0,0,255);stroke:rgb(0,0,255);stroke-width:0" /> \n  <text x="150.133630" y="156.192000" font-family="inherit" font-size="3.6" fill="rgb(0,0,255)" text-anchor="middle" transform="rotate(-90.000000 150.133630,156.192000)" >13</text> </g>
  Visible = false
  X = 0
  Y = 0
  arrowL1 = 3
  arrowL2 = 1
  arrowW = 2
  arrow_scheme = 0
  autoPlaceOffset = 2
  autoPlaceText = true
  click1_x = 152.134
  click1_y = 150.242
  click2_x = 152.134
  click2_y = 150.242
  comma_decimal_place = false
  dimension_line_overshoot = 1
  gap_datum_points = 2
  halfDimension_linear = false
  lineColor = rgb(0,0,255)
  strokeWidth = 0.5
  textFormat_linear = %(value)3.3f
  textRenderer_color = rgb(0,0,255)
  textRenderer_family = inherit
  textRenderer_size = 3.6
  unit_custom_scale = 1
  unit_scheme = 0
FEATURE [Drawing::FeatureViewPython] dim029  # drawing view (typed FeaturePython)
  Rotation = 0
  ViewResult = <g> \n  <line x1="123.210000" y1="146.392000" x2="123.210000" y2="138.592856" style="stroke:rgb(0,0,255);stroke-width:0.50" />\n<line x1="137.610000" y1="146.392000" x2="137.610000" y2="138.592856" style="stroke:rgb(0,0,255);stroke-width:0.50" />\n<line x1="123.210000" y1="139.592856" x2="137.610000" y2="139.592856" style="stroke:rgb(0,0,255);stroke-width:0.50" /> \n  <polygon points="137.610000,139.592856 134.610000,138.592856 133.610000,139.592856 134.610000,140.592856" style="fill:rgb(0,0,255);stroke:rgb(0,0,255);stroke-width:0" /><polygon points="123.210000,139.592856 126.210000,140.592856 127.210000,139.592856 126.210000,138.592856" style="fill:rgb(0,0,255);stroke:rgb(0,0,255);stroke-width:0" /> \n  <text x="130.410000" y="137.592856" font-family="inherit" font-size="3.6" fill="rgb(0,0,255)" text-anchor="middle" transform="rotate(0.000000 130.410000,137.592856)" >12</text> </g>
  Visible = false
  X = 0
  Y = 0
  arrowL1 = 3
  arrowL2 = 1
  arrowW = 2
  arrow_scheme = 0
  autoPlaceOffset = 2
  autoPlaceText = true
  click1_x = 133.665
  click1_y = 139.593
  click2_x = 133.665
  click2_y = 139.593
  comma_decimal_place = false
  dimension_line_overshoot = 1
  gap_datum_points = 2
  halfDimension_linear = false
  lineColor = rgb(0,0,255)
  strokeWidth = 0.5
  textFormat_linear = %(value)3.3f
  textRenderer_color = rgb(0,0,255)
  textRenderer_family = inherit
  textRenderer_size = 3.6
  unit_custom_scale = 1
  unit_scheme = 0
FEATURE [Drawing::FeatureViewPython] dim030  # drawing view (typed FeaturePython)
  Rotation = 0
  ViewResult = <g> \n  <line x1="115.163320" y1="195.492000" x2="107.228856" y2="195.492000" style="stroke:rgb(0,0,255);stroke-width:0.50" />\n<line x1="111.563320" y1="199.092000" x2="107.228856" y2="199.092000" style="stroke:rgb(0,0,255);stroke-width:0.50" />\n<line x1="108.228856" y1="195.492000" x2="108.228856" y2="199.092000" style="stroke:rgb(0,0,255);stroke-width:0.50" /> \n  <polygon points="108.228856,199.092000 107.228856,202.092000 108.228856,203.092000 109.228856,202.092000" style="fill:rgb(0,0,255);stroke:rgb(0,0,255);stroke-width:0" /><polygon points="108.228856,195.492000 109.228856,192.492000 108.228856,191.492000 107.228856,192.492000" style="fill:rgb(0,0,255);stroke:rgb(0,0,255);stroke-width:0" /> \n  <text x="106.228856" y="197.292000" font-family="inherit" font-size="3.6" fill="rgb(0,0,255)" text-anchor="middle" transform="rotate(-90.000000 106.228856,197.292000)" >3</text> </g>
  Visible = false
  X = 0
  Y = 0
  arrowL1 = 3
  arrowL2 = 1
  arrowW = 2
  arrow_scheme = 0
  autoPlaceOffset = 2
  autoPlaceText = true
  click1_x = 108.229
  click1_y = 196.821
  click2_x = 108.229
  click2_y = 196.821
  comma_decimal_place = false
  dimension_line_overshoot = 1
  gap_datum_points = 2
  halfDimension_linear = false
  lineColor = rgb(0,0,255)
  strokeWidth = 0.5
  textFormat_linear = %(value)3.3f
  textRenderer_color = rgb(0,0,255)
  textRenderer_family = inherit
  textRenderer_size = 3.6
  unit_custom_scale = 1
  unit_scheme = 0
FEATURE [Drawing::FeatureViewPython] dim031  # drawing view (typed FeaturePython)
  Rotation = 0
  ViewResult = <g> \n  <line x1="113.563320" y1="197.092000" x2="113.563320" y2="188.318951" style="stroke:rgb(0,0,255);stroke-width:0.50" />\n<line x1="117.163320" y1="193.492000" x2="117.163320" y2="188.318951" style="stroke:rgb(0,0,255);stroke-width:0.50" />\n<line x1="113.563320" y1="189.318951" x2="117.163320" y2="189.318951" style="stroke:rgb(0,0,255);stroke-width:0.50" /> \n  <polygon points="117.163320,189.318951 120.163320,190.318951 121.163320,189.318951 120.163320,188.318951" style="fill:rgb(0,0,255);stroke:rgb(0,0,255);stroke-width:0" /><polygon points="113.563320,189.318951 110.563320,188.318951 109.563320,189.318951 110.563320,190.318951" style="fill:rgb(0,0,255);stroke:rgb(0,0,255);stroke-width:0" /> \n  <text x="115.363320" y="187.318951" font-family="inherit" font-size="3.6" fill="rgb(0,0,255)" text-anchor="middle" transform="rotate(0.000000 115.363320,187.318951)" >3</text> </g>
  Visible = false
  X = 0
  Y = 0
  arrowL1 = 3
  arrowL2 = 1
  arrowW = 2
  arrow_scheme = 0
  autoPlaceOffset = 2
  autoPlaceText = true
  click1_x = 116.644
  click1_y = 189.319
  click2_x = 116.644
  click2_y = 189.319
  comma_decimal_place = false
  dimension_line_overshoot = 1
  gap_datum_points = 2
  halfDimension_linear = false
  lineColor = rgb(0,0,255)
  strokeWidth = 0.5
  textFormat_linear = %(value)3.3f
  textRenderer_color = rgb(0,0,255)
  textRenderer_family = inherit
  textRenderer_size = 3.6
  unit_custom_scale = 1
  unit_scheme = 0
FEATURE [Drawing::FeatureViewPython] dim032  # drawing view (typed FeaturePython)
  Rotation = 0
  ViewResult = <g> \n  <line x1="117.163320" y1="193.492000" x2="117.163320" y2="179.316189" style="stroke:rgb(0,0,255);stroke-width:0.50" />\n<line x1="125.563320" y1="193.492000" x2="125.563320" y2="179.316189" style="stroke:rgb(0,0,255);stroke-width:0.50" />\n<line x1="117.163320" y1="180.316189" x2="125.563320" y2="180.316189" style="stroke:rgb(0,0,255);stroke-width:0.50" /> \n  <polygon points="125.563320,180.316189 128.563320,181.316189 129.563320,180.316189 128.563320,179.316189" style="fill:rgb(0,0,255);stroke:rgb(0,0,255);stroke-width:0" /><polygon points="117.163320,180.316189 114.163320,179.316189 113.163320,180.316189 114.163320,181.316189" style="fill:rgb(0,0,255);stroke:rgb(0,0,255);stroke-width:0" /> \n  <text x="121.363320" y="178.316189" font-family="inherit" font-size="3.6" fill="rgb(0,0,255)" text-anchor="middle" transform="rotate(0.000000 121.363320,178.316189)" >7</text> </g>
  Visible = false
  X = 0
  Y = 0
  arrowL1 = 3
  arrowL2 = 1
  arrowW = 2
  arrow_scheme = 0
  autoPlaceOffset = 2
  autoPlaceText = true
  click1_x = 129.561
  click1_y = 180.316
  click2_x = 129.561
  click2_y = 180.316
  comma_decimal_place = false
  dimension_line_overshoot = 1
  gap_datum_points = 2
  halfDimension_linear = false
  lineColor = rgb(0,0,255)
  strokeWidth = 0.5
  textFormat_linear = %(value)3.3f
  textRenderer_color = rgb(0,0,255)
  textRenderer_family = inherit
  textRenderer_size = 3.6
  unit_custom_scale = 1
  unit_scheme = 0
FEATURE [Drawing::FeatureViewPython] dim033  # drawing view (typed FeaturePython)
  Rotation = 0
  ViewResult = <g> \n  <line x1="125.563320" y1="193.492000" x2="125.563320" y2="179.250952" style="stroke:rgb(0,0,255);stroke-width:0.50" />\n<line x1="133.963320" y1="193.492000" x2="133.963320" y2="179.250952" style="stroke:rgb(0,0,255);stroke-width:0.50" />\n<line x1="125.563320" y1="180.250952" x2="133.963320" y2="180.250952" style="stroke:rgb(0,0,255);stroke-width:0.50" /> \n  <polygon points="133.963320,180.250952 136.963320,181.250952 137.963320,180.250952 136.963320,179.250952" style="fill:rgb(0,0,255);stroke:rgb(0,0,255);stroke-width:0" /><polygon points="125.563320,180.250952 122.563320,179.250952 121.563320,180.250952 122.563320,181.250952" style="fill:rgb(0,0,255);stroke:rgb(0,0,255);stroke-width:0" /> \n  <text x="129.763320" y="178.250952" font-family="inherit" font-size="3.6" fill="rgb(0,0,255)" text-anchor="middle" transform="rotate(0.000000 129.763320,178.250952)" >7</text> </g>
  Visible = false
  X = 0
  Y = 0
  arrowL1 = 3
  arrowL2 = 1
  arrowW = 2
  arrow_scheme = 0
  autoPlaceOffset = 2
  autoPlaceText = true
  click1_x = 137.912
  click1_y = 180.251
  click2_x = 137.912
  click2_y = 180.251
  comma_decimal_place = false
  dimension_line_overshoot = 1
  gap_datum_points = 2
  halfDimension_linear = false
  lineColor = rgb(0,0,255)
  strokeWidth = 0.5
  textFormat_linear = %(value)3.3f
  textRenderer_color = rgb(0,0,255)
  textRenderer_family = inherit
  textRenderer_size = 3.6
  unit_custom_scale = 1
  unit_scheme = 0
FEATURE [Drawing::FeatureViewPython] dim034  # drawing view (typed FeaturePython)
  Rotation = 0
  ViewResult = <g> \n  <line x1="133.963320" y1="193.492000" x2="133.963320" y2="179.250952" style="stroke:rgb(0,0,255);stroke-width:0.50" />\n<line x1="142.363320" y1="193.492000" x2="142.363320" y2="179.250952" style="stroke:rgb(0,0,255);stroke-width:0.50" />\n<line x1="133.963320" y1="180.250952" x2="142.363320" y2="180.250952" style="stroke:rgb(0,0,255);stroke-width:0.50" /> \n  <polygon points="142.363320,180.250952 145.363320,181.250952 146.363320,180.250952 145.363320,179.250952" style="fill:rgb(0,0,255);stroke:rgb(0,0,255);stroke-width:0" /><polygon points="133.963320,180.250952 130.963320,179.250952 129.963320,180.250952 130.963320,181.250952" style="fill:rgb(0,0,255);stroke:rgb(0,0,255);stroke-width:0" /> \n  <text x="138.163320" y="178.250952" font-family="inherit" font-size="3.6" fill="rgb(0,0,255)" text-anchor="middle" transform="rotate(0.000000 138.163320,178.250952)" >7</text> </g>
  Visible = false
  X = 0
  Y = 0
  arrowL1 = 3
  arrowL2 = 1
  arrowW = 2
  arrow_scheme = 0
  autoPlaceOffset = 2
  autoPlaceText = true
  click1_x = 144.175
  click1_y = 180.251
  click2_x = 144.175
  click2_y = 180.251
  comma_decimal_place = false
  dimension_line_overshoot = 1
  gap_datum_points = 2
  halfDimension_linear = false
  lineColor = rgb(0,0,255)
  strokeWidth = 0.5
  textFormat_linear = %(value)3.3f
  textRenderer_color = rgb(0,0,255)
  textRenderer_family = inherit
  textRenderer_size = 3.6
  unit_custom_scale = 1
  unit_scheme = 0
FEATURE [Drawing::FeatureViewPython] dim035  # drawing view (typed FeaturePython)
  Rotation = 0
  ViewResult = <g> \n  <line x1="117.163320" y1="192.172000" x2="117.163320" y2="155.487606" style="stroke:rgb(0,0,255);stroke-width:0.50" />\n<line x1="123.210000" y1="160.672000" x2="123.210000" y2="155.487606" style="stroke:rgb(0,0,255);stroke-width:0.50" />\n<line x1="117.163320" y1="156.487606" x2="123.210000" y2="156.487606" style="stroke:rgb(0,0,255);stroke-width:0.50" /> \n  <polygon points="123.210000,156.487606 126.210000,157.487606 127.210000,156.487606 126.210000,155.487606" style="fill:rgb(0,0,255);stroke:rgb(0,0,255);stroke-width:0" /><polygon points="117.163320,156.487606 114.163320,155.487606 113.163320,156.487606 114.163320,157.487606" style="fill:rgb(0,0,255);stroke:rgb(0,0,255);stroke-width:0" /> \n  <text x="120.186660" y="154.487606" font-family="inherit" font-size="3.6" fill="rgb(0,0,255)" text-anchor="middle" transform="rotate(0.000000 120.186660,154.487606)" >5.039</text> </g>
  Visible = false
  X = 0
  Y = 0
  arrowL1 = 3
  arrowL2 = 1
  arrowW = 2
  arrow_scheme = 0
  autoPlaceOffset = 2
  autoPlaceText = true
  click1_x = 123.21
  click1_y = 156.488
  click2_x = 123.21
  click2_y = 156.488
  comma_decimal_place = false
  dimension_line_overshoot = 1
  gap_datum_points = 2
  halfDimension_linear = false
  lineColor = rgb(0,0,255)
  strokeWidth = 0.5
  textFormat_linear = %(value)3.3f
  textRenderer_color = rgb(0,0,255)
  textRenderer_family = inherit
  textRenderer_size = 3.6
  unit_custom_scale = 1
  unit_scheme = 0
FEATURE [Drawing::FeatureViewPython] dia010  # drawing view (typed FeaturePython)
  Rotation = 0
  ViewResult = <g>  <circle cx ="123.210000" cy ="148.392000" r="0.250000" stroke="none" fill="rgb(0,0,255)" /> \n<line x1="105.570203" y1="134.384955" x2="124.243736" y2="149.212847" style="stroke:rgb(0,0,255);stroke-width:0.50" />\n<polygon points="122.176264,147.571153 120.448719,144.922457 119.043732,145.083736 119.205011,146.488723" style="fill:rgb(0,0,255);stroke:rgb(0,0,255);stroke-width:0" />\n<polygon points="124.243736,149.212847 125.971281,151.861543 127.376268,151.700264 127.214989,150.295277" style="fill:rgb(0,0,255);stroke:rgb(0,0,255);stroke-width:0" />\n<line x1="105.570203" y1="134.384955" x2="87.954198" y2="134.384955" style="stroke:rgb(0,0,255);stroke-width:0.50" />\n<text x="96.762200" y="132.384955" font-family="inherit" font-size="3.6" fill="rgb(0,0,255)" text-anchor="middle" transform="rotate(0.000000 96.762200,132.384955)" >Ø2.2</text> </g>
  Visible = false
  X = 0
  Y = 0
  arrowL1 = 3
  arrowL2 = 1
  arrowW = 2
  arrow_scheme = 0
  autoPlaceOffset = 2
  autoPlaceText = true
  centerPointDia = 0.5
  click1_x = 105.57
  click1_y = 134.385
  click2_x = 87.9542
  click2_y = 134.259
  click3_x = 87.9542
  click3_y = 134.259
  comma_decimal_place = false
  lineColor = rgb(0,0,255)
  strokeWidth = 0.5
  textFormat_circular = Ø%(value)3.3f
  textRenderer_color = rgb(0,0,255)
  textRenderer_family = inherit
  textRenderer_size = 3.6
  unit_custom_scale = 1
  unit_scheme = 0
FEATURE [Drawing::FeatureViewPython] text011  # drawing view (typed FeaturePython)
  Rotation = 0
  ViewResult = <g> <text x="93.993971" y="138.033984" font-family="inherit" font-size="3,6" fill="rgb(0,0,255)" text-anchor="inherit" transform="rotate(0.000000 93.993971,138.033984)" >H1</text> </g>
  Visible = false
  X = 0
  Y = 0
  click1_x = 93.994
  click1_y = 138.034
  rotation = 0
  text = H1
  textRenderer_addText_color = rgb(0,0,255)
  textRenderer_addText_family = inherit
  textRenderer_addText_size = 3,6
FEATURE [Drawing::FeatureViewPython] text012  # drawing view (typed FeaturePython)
  Rotation = 0
  ViewResult = <g> <text x="135.265755" y="152.755932" font-family="inherit" font-size="3,6" fill="rgb(0,0,255)" text-anchor="inherit" transform="rotate(0.000000 135.265755,152.755932)" >H1</text> </g>
  Visible = false
  X = 0
  Y = 0
  click1_x = 135.266
  click1_y = 152.756
  rotation = 0
  text = H1
  textRenderer_addText_color = rgb(0,0,255)
  textRenderer_addText_family = inherit
  textRenderer_addText_size = 3,6
FEATURE [Drawing::FeatureViewPython] text013  # drawing view (typed FeaturePython)
  Rotation = 0
  ViewResult = <g> <text x="120.921293" y="168.358679" font-family="inherit" font-size="3,6" fill="rgb(0,0,255)" text-anchor="inherit" transform="rotate(0.000000 120.921293,168.358679)" >H1</text> </g>
  Visible = false
  X = 0
  Y = 0
  click1_x = 120.921
  click1_y = 168.359
  rotation = 0
  text = H1
  textRenderer_addText_color = rgb(0,0,255)
  textRenderer_addText_family = inherit
  textRenderer_addText_size = 3,6
FEATURE [Drawing::FeatureViewPython] text014  # drawing view (typed FeaturePython)
  Rotation = 0
  ViewResult = <g> <text x="135.265755" y="168.358679" font-family="inherit" font-size="3,6" fill="rgb(0,0,255)" text-anchor="inherit" transform="rotate(0.000000 135.265755,168.358679)" >H1</text> </g>
  Visible = false
  X = 0
  Y = 0
  click1_x = 135.266
  click1_y = 168.359
  rotation = 0
  text = H1
  textRenderer_addText_color = rgb(0,0,255)
  textRenderer_addText_family = inherit
  textRenderer_addText_size = 3,6
FEATURE [Drawing::FeatureViewPython] dia011  # drawing view (typed FeaturePython)
  Rotation = 0
  ViewResult = <g>  <circle cx ="142.363320" cy ="195.492000" r="0.250000" stroke="none" fill="rgb(0,0,255)" /> \n<line x1="155.647048" y1="210.065623" x2="141.474111" y2="194.516445" style="stroke:rgb(0,0,255);stroke-width:0.50" />\n<polygon points="143.252529,196.467555 144.534403,199.358368 145.947103,199.423781 146.012516,198.011081" style="fill:rgb(0,0,255);stroke:rgb(0,0,255);stroke-width:0" />\n<polygon points="141.474111,194.516445 140.192237,191.625632 138.779537,191.560219 138.714124,192.972919" style="fill:rgb(0,0,255);stroke:rgb(0,0,255);stroke-width:0" />\n<line x1="155.647048" y1="210.065623" x2="174.834144" y2="210.065623" style="stroke:rgb(0,0,255);stroke-width:0.50" />\n<text x="165.240596" y="208.065623" font-family="inherit" font-size="3.6" fill="rgb(0,0,255)" text-anchor="middle" transform="rotate(0.000000 165.240596,208.065623)" >Ø2.2</text> </g>
  Visible = false
  X = 0
  Y = 0
  arrowL1 = 3
  arrowL2 = 1
  arrowW = 2
  arrow_scheme = 0
  autoPlaceOffset = 2
  autoPlaceText = true
  centerPointDia = 0.5
  click1_x = 155.647
  click1_y = 210.066
  click2_x = 174.834
  click2_y = 213.539
  click3_x = 174.834
  click3_y = 213.539
  comma_decimal_place = false
  lineColor = rgb(0,0,255)
  strokeWidth = 0.5
  textFormat_circular = Ø%(value)3.3f
  textRenderer_color = rgb(0,0,255)
  textRenderer_family = inherit
  textRenderer_size = 3.6
  unit_custom_scale = 1
  unit_scheme = 0
FEATURE [Drawing::FeatureViewPython] text015  # drawing view (typed FeaturePython)
  Rotation = 0
  ViewResult = <g> <text x="163.255724" y="213.704555" font-family="inherit" font-size="3,6" fill="rgb(0,0,255)" text-anchor="inherit" transform="rotate(0.000000 163.255724,213.704555)" >H1</text> </g>
  Visible = false
  X = 0
  Y = 0
  click1_x = 163.256
  click1_y = 213.705
  rotation = 0
  text = H1
  textRenderer_addText_color = rgb(0,0,255)
  textRenderer_addText_family = inherit
  textRenderer_addText_size = 3,6
FEATURE [Drawing::FeatureViewPython] text016  # drawing view (typed FeaturePython)
  Rotation = 0
  ViewResult = <g> <text x="135.561879" y="198.063551" font-family="inherit" font-size="3,6" fill="rgb(0,0,255)" text-anchor="inherit" transform="rotate(0.000000 135.561879,198.063551)" >H1</text> </g>
  Visible = false
  X = 0
  Y = 0
  click1_x = 135.562
  click1_y = 198.064
  rotation = 0
  text = H1
  textRenderer_addText_color = rgb(0,0,255)
  textRenderer_addText_family = inherit
  textRenderer_addText_size = 3,6
FEATURE [Drawing::FeatureViewPython] text017  # drawing view (typed FeaturePython)
  Rotation = 0
  ViewResult = <g> <text x="127.127188" y="198.063551" font-family="inherit" font-size="3,6" fill="rgb(0,0,255)" text-anchor="inherit" transform="rotate(0.000000 127.127188,198.063551)" >H1</text> </g>
  Visible = false
  X = 0
  Y = 0
  click1_x = 127.127
  click1_y = 198.064
  rotation = 0
  text = H1
  textRenderer_addText_color = rgb(0,0,255)
  textRenderer_addText_family = inherit
  textRenderer_addText_size = 3,6
FEATURE [Drawing::FeatureViewPython] text018  # drawing view (typed FeaturePython)
  Rotation = 0
  ViewResult = <g> <text x="118.753177" y="197.820827" font-family="inherit" font-size="3,6" fill="rgb(0,0,255)" text-anchor="inherit" transform="rotate(0.000000 118.753177,197.820827)" >H1</text> </g>
  Visible = false
  X = 0
  Y = 0
  click1_x = 118.753
  click1_y = 197.821
  rotation = 0
  text = H1
  textRenderer_addText_color = rgb(0,0,255)
  textRenderer_addText_family = inherit
  textRenderer_addText_size = 3,6
FEATURE [Drawing::FeatureViewPart] Ortho001  label="Ortho_Right_Nozzle_Fix"
  Direction = (0,1,0)
  HiddenWidth = 0.15
  LineWidth = 0.35
  Rotation = -90
  Scale = 1.2
  ShowHiddenLines = false
  ShowSmoothLines = false
  Source = -> Body006021004
  Tolerance = 0.05
  ViewResult = <g id="Ortho_Right_Nozzle_Fix"\n   transform="rotate(-90,180,160) translate(180,160) scale(1.2,1.2)"\n  >\n<g   fill="none"\n   stroke="rgb(0, 0, 0)"\n   stroke-linecap="butt"\n   stroke-linejoin="miter"\n   stroke-width="0.291667"\n   transform="scale(1,-1)"\n  >\n<path id= "1" d=" M 29.0027 -56.04 L 29.0027 -29.04 " />\n<path id= "2" d=" M 6.0027 -56.04 L 29.0027 -56.04 " />\n<path id= "3" d=" M 29.0027 -29.04 L 6.0027 -29.04 " />\n<path id= "4" d=" M 6.0027 -29.04 L 6.0027 -56.04 " />\n<circle cx ="26.5027" cy ="-34.54" r ="1.1" /><circle cx ="18.5027" cy ="-42.54" r ="8" /><circle cx ="10.5027" cy ="-50.54" r ="1.1" /><circle cx ="10.5027" cy ="-34.54" r ="1.1" /><circle cx ="26.5027" cy ="-50.54" r ="1.1" /></g>\n</g>
  Visible = false
  X = 180
  Y = 160
FEATURE [Drawing::FeatureViewPython] dim036  # drawing view (typed FeaturePython)
  Rotation = 0
  ViewResult = <g> \n  <line x1="214.848000" y1="123.196760" x2="214.848000" y2="111.746176" style="stroke:rgb(0,0,255);stroke-width:0.50" />\n<line x1="247.248000" y1="123.196760" x2="247.248000" y2="111.746176" style="stroke:rgb(0,0,255);stroke-width:0.50" />\n<line x1="214.848000" y1="112.746176" x2="247.248000" y2="112.746176" style="stroke:rgb(0,0,255);stroke-width:0.50" /> \n  <polygon points="247.248000,112.746176 244.248000,111.746176 243.248000,112.746176 244.248000,113.746176" style="fill:rgb(0,0,255);stroke:rgb(0,0,255);stroke-width:0" /><polygon points="214.848000,112.746176 217.848000,113.746176 218.848000,112.746176 217.848000,111.746176" style="fill:rgb(0,0,255);stroke:rgb(0,0,255);stroke-width:0" /> \n  <text x="231.048000" y="110.746176" font-family="inherit" font-size="3.6" fill="rgb(0,0,255)" text-anchor="middle" transform="rotate(0.000000 231.048000,110.746176)" >27</text> </g>
  Visible = false
  X = 0
  Y = 0
  arrowL1 = 3
  arrowL2 = 1
  arrowW = 2
  arrow_scheme = 0
  autoPlaceOffset = 2
  autoPlaceText = true
  click1_x = 248.832
  click1_y = 112.746
  click2_x = 248.832
  click2_y = 112.746
  comma_decimal_place = false
  dimension_line_overshoot = 1
  gap_datum_points = 2
  halfDimension_linear = false
  lineColor = rgb(0,0,255)
  strokeWidth = 0.5
  textFormat_linear = %(value)3.3f
  textRenderer_color = rgb(0,0,255)
  textRenderer_family = inherit
  textRenderer_size = 3.6
  unit_custom_scale = 1
  unit_scheme = 0
FEATURE [Drawing::FeatureViewPython] centerLines003  # drawing view (typed FeaturePython)
  Rotation = 0
  ViewResult = <g transform="scale(1.200000,1.200000)" stroke="rgb(0,0,255)"  stroke-width="0.266667" > <path d="M 192.540000,114.830633 L 192.540000,117.330633 M 192.540000,118.997300 L 192.540000,123.997300 M 192.540000,125.663967 L 192.540000,128.163967 M 192.540000,129.830633 L 192.540000,133.220783 "/>\n<path d="M 192.540000,114.830633 L 192.540000,117.330633 M 192.540000,118.997300 L 192.540000,123.997300 M 192.540000,125.663967 L 192.540000,128.163967 M 192.540000,129.830633 L 192.540000,133.220783 "/> </g> 
  Visible = false
  X = 0
  Y = 0
  centerLine_color = rgb(0,0,255)
  centerLine_len_dash = 6
  centerLine_len_dot = 3
  centerLine_len_gap = 2
  centerLine_width = 0.32
  click1_x = 230.995
  click1_y = 159.865
  click2_x = 230.995
  click2_y = 159.865
FEATURE [Drawing::FeatureViewPython] centerLines004  # drawing view (typed FeaturePython)
  Rotation = 0
  ViewResult = <g transform="scale(1.200000,1.200000)" stroke="rgb(0,0,255)"  stroke-width="0.266667" > <path d="M 192.540000,114.830633 L 192.540000,112.330633 M 192.540000,110.663967 L 192.540000,105.663967 M 192.540000,103.997300 L 192.540000,101.497300 M 192.540000,99.830633 L 192.540000,98.100287 "/>\n<path d="M 192.540000,114.830633 L 192.540000,112.330633 M 192.540000,110.663967 L 192.540000,105.663967 M 192.540000,103.997300 L 192.540000,101.497300 M 192.540000,99.830633 L 192.540000,98.100287 "/> </g> 
  Visible = false
  X = 0
  Y = 0
  centerLine_color = rgb(0,0,255)
  centerLine_len_dash = 6
  centerLine_len_dot = 3
  centerLine_len_gap = 2
  centerLine_width = 0.32
  click1_x = 232.24
  click1_y = 117.72
  click2_x = 232.24
  click2_y = 117.72
FEATURE [Drawing::FeatureViewPython] centerLines006  # drawing view (typed FeaturePython)
  Rotation = 0
  ViewResult = <g transform="scale(1.200000,1.200000)" stroke="rgb(0,0,255)"  stroke-width="0.266667" > <path d="M 192.540000,114.830633 L 190.040000,114.830633 M 188.373333,114.830633 L 183.373333,114.830633 M 181.706667,114.830633 L 179.206667,114.830633 M 177.540000,114.830633 L 174.416976,114.830633 "/>\n<path d="M 192.540000,114.830633 L 190.040000,114.830633 M 188.373333,114.830633 L 183.373333,114.830633 M 181.706667,114.830633 L 179.206667,114.830633 M 177.540000,114.830633 L 174.416976,114.830633 "/> </g> 
  Visible = false
  X = 0
  Y = 0
  centerLine_color = rgb(0,0,255)
  centerLine_len_dash = 6
  centerLine_len_dot = 3
  centerLine_len_gap = 2
  centerLine_width = 0.32
  click1_x = 209.3
  click1_y = 139.771
  click2_x = 209.3
  click2_y = 139.771
FEATURE [Drawing::FeatureViewPython] rad003  # drawing view (typed FeaturePython)
  Rotation = 0
  ViewResult = <g>  <circle cx ="231.048000" cy ="137.796760" r="0.250000" stroke="none" fill="rgb(0,0,255)" /> \n<line x1="221.095559" y1="169.311798" x2="231.048000" y2="137.796760" style="stroke:rgb(0,0,255);stroke-width:0.50" />\n<polygon points="228.157053,146.951127 230.014054,144.391527 229.361614,143.136807 228.106894,143.789247" style="fill:rgb(0,0,255);stroke:rgb(0,0,255);stroke-width:0" />\n<line x1="221.095559" y1="169.311798" x2="211.680330" y2="169.311798" style="stroke:rgb(0,0,255);stroke-width:0.50" />\n<text x="216.387944" y="167.311798" font-family="inherit" font-size="3.6" fill="rgb(0,0,255)" text-anchor="middle" transform="rotate(0.000000 216.387944,167.311798)" >R8</text> </g>
  Visible = false
  X = 0
  Y = 0
  arrowL1 = 3
  arrowL2 = 1
  arrowW = 2
  arrow_scheme = 0
  autoPlaceOffset = 2
  autoPlaceText = true
  centerPointDia = 0.5
  click1_x = 221.096
  click1_y = 169.312
  click2_x = 211.68
  click2_y = 173.532
  click3_x = 211.68
  click3_y = 173.532
  comma_decimal_place = false
  lineColor = rgb(0,0,255)
  strokeWidth = 0.5
  textFormat_radial = R%(value)3.3f
  textRenderer_color = rgb(0,0,255)
  textRenderer_family = inherit
  textRenderer_size = 3.6
  unit_custom_scale = 1
  unit_scheme = 0
FEATURE [Drawing::FeatureViewPython] dim038  # drawing view (typed FeaturePython)
  Rotation = 0
  ViewResult = <g> \n  <line x1="221.448000" y1="126.196760" x2="221.448000" y2="117.756012" style="stroke:rgb(0,0,255);stroke-width:0.50" />\n<line x1="231.048000" y1="119.720344" x2="231.048000" y2="119.756012" style="stroke:rgb(0,0,255);stroke-width:0.50" />\n<line x1="221.448000" y1="118.756012" x2="231.048000" y2="118.756012" style="stroke:rgb(0,0,255);stroke-width:0.50" /> \n  <polygon points="231.048000,118.756012 234.048000,119.756012 235.048000,118.756012 234.048000,117.756012" style="fill:rgb(0,0,255);stroke:rgb(0,0,255);stroke-width:0" /><polygon points="221.448000,118.756012 218.448000,117.756012 217.448000,118.756012 218.448000,119.756012" style="fill:rgb(0,0,255);stroke:rgb(0,0,255);stroke-width:0" /> \n  <text x="226.248000" y="116.756012" font-family="inherit" font-size="3.6" fill="rgb(0,0,255)" text-anchor="middle" transform="rotate(0.000000 226.248000,116.756012)" >8</text> </g>
  Visible = false
  X = 0
  Y = 0
  arrowL1 = 3
  arrowL2 = 1
  arrowW = 2
  arrow_scheme = 0
  autoPlaceOffset = 2
  autoPlaceText = true
  click1_x = 230.823
  click1_y = 118.756
  click2_x = 230.823
  click2_y = 118.756
  comma_decimal_place = false
  dimension_line_overshoot = 1
  gap_datum_points = 2
  halfDimension_linear = false
  lineColor = rgb(0,0,255)
  strokeWidth = 0.5
  textFormat_linear = %(value)3.3f
  textRenderer_color = rgb(0,0,255)
  textRenderer_family = inherit
  textRenderer_size = 3.6
  unit_custom_scale = 1
  unit_scheme = 0
FEATURE [Drawing::FeatureViewPython] dim040  # drawing view (typed FeaturePython)
  Rotation = 0
  ViewResult = <g> \n  <line x1="219.448000" y1="128.196760" x2="208.103656" y2="128.196760" style="stroke:rgb(0,0,255);stroke-width:0.50" />\n<line x1="207.300371" y1="137.796760" x2="208.103656" y2="137.796760" style="stroke:rgb(0,0,255);stroke-width:0.50" />\n<line x1="209.103656" y1="128.196760" x2="209.103656" y2="137.796760" style="stroke:rgb(0,0,255);stroke-width:0.50" /> \n  <polygon points="209.103656,137.796760 208.103656,140.796760 209.103656,141.796760 210.103656,140.796760" style="fill:rgb(0,0,255);stroke:rgb(0,0,255);stroke-width:0" /><polygon points="209.103656,128.196760 210.103656,125.196760 209.103656,124.196760 208.103656,125.196760" style="fill:rgb(0,0,255);stroke:rgb(0,0,255);stroke-width:0" /> \n  <text x="207.103656" y="132.996760" font-family="inherit" font-size="3.6" fill="rgb(0,0,255)" text-anchor="middle" transform="rotate(-90.000000 207.103656,132.996760)" >8</text> </g>
  Visible = false
  X = 0
  Y = 0
  arrowL1 = 3
  arrowL2 = 1
  arrowW = 2
  arrow_scheme = 0
  autoPlaceOffset = 2
  autoPlaceText = true
  click1_x = 209.104
  click1_y = 131.637
  click2_x = 209.104
  click2_y = 131.637
  comma_decimal_place = false
  dimension_line_overshoot = 1
  gap_datum_points = 2
  halfDimension_linear = false
  lineColor = rgb(0,0,255)
  strokeWidth = 0.5
  textFormat_linear = %(value)3.3f
  textRenderer_color = rgb(0,0,255)
  textRenderer_family = inherit
  textRenderer_size = 3.6
  unit_custom_scale = 1
  unit_scheme = 0
FEATURE [Drawing::FeatureViewPython] dim041  # drawing view (typed FeaturePython)
  Rotation = 0
  ViewResult = <g> \n  <line x1="219.448000" y1="147.396760" x2="208.139719" y2="147.396760" style="stroke:rgb(0,0,255);stroke-width:0.50" />\n<line x1="207.300371" y1="137.796760" x2="208.139719" y2="137.796760" style="stroke:rgb(0,0,255);stroke-width:0.50" />\n<line x1="209.139719" y1="147.396760" x2="209.139719" y2="137.796760" style="stroke:rgb(0,0,255);stroke-width:0.50" /> \n  <polygon points="209.139719,137.796760 210.139719,134.796760 209.139719,133.796760 208.139719,134.796760" style="fill:rgb(0,0,255);stroke:rgb(0,0,255);stroke-width:0" /><polygon points="209.139719,147.396760 208.139719,150.396760 209.139719,151.396760 210.139719,150.396760" style="fill:rgb(0,0,255);stroke:rgb(0,0,255);stroke-width:0" /> \n  <text x="207.139719" y="142.596760" font-family="inherit" font-size="3.6" fill="rgb(0,0,255)" text-anchor="middle" transform="rotate(-90.000000 207.139719,142.596760)" >8</text> </g>
  Visible = false
  X = 0
  Y = 0
  arrowL1 = 3
  arrowL2 = 1
  arrowW = 2
  arrow_scheme = 0
  autoPlaceOffset = 2
  autoPlaceText = true
  click1_x = 209.14
  click1_y = 141.15
  click2_x = 209.14
  click2_y = 141.15
  comma_decimal_place = false
  dimension_line_overshoot = 1
  gap_datum_points = 2
  halfDimension_linear = false
  lineColor = rgb(0,0,255)
  strokeWidth = 0.5
  textFormat_linear = %(value)3.3f
  textRenderer_color = rgb(0,0,255)
  textRenderer_family = inherit
  textRenderer_size = 3.6
  unit_custom_scale = 1
  unit_scheme = 0
FEATURE [Drawing::FeatureViewPython] dia012  # drawing view (typed FeaturePython)
  Rotation = 0
  ViewResult = <g>  <circle cx ="240.648000" cy ="147.396760" r="0.250000" stroke="none" fill="rgb(0,0,255)" /> \n<line x1="235.380735" y1="166.065167" x2="241.006442" y2="146.126359" style="stroke:rgb(0,0,255);stroke-width:0.50" />\n<polygon points="240.289558,148.667161 238.512492,151.282890 239.203370,152.516862 240.437342,151.825984" style="fill:rgb(0,0,255);stroke:rgb(0,0,255);stroke-width:0" />\n<polygon points="241.006442,146.126359 242.783508,143.510630 242.092630,142.276658 240.858658,142.967536" style="fill:rgb(0,0,255);stroke:rgb(0,0,255);stroke-width:0" />\n<line x1="235.380735" y1="166.065167" x2="226.939495" y2="166.065167" style="stroke:rgb(0,0,255);stroke-width:0.50" />\n<text x="231.160115" y="164.065167" font-family="inherit" font-size="3.6" fill="rgb(0,0,255)" text-anchor="middle" transform="rotate(0.000000 231.160115,164.065167)" >Ø2.2</text> </g>
  Visible = false
  X = 0
  Y = 0
  arrowL1 = 3
  arrowL2 = 1
  arrowW = 2
  arrow_scheme = 0
  autoPlaceOffset = 2
  autoPlaceText = true
  centerPointDia = 0.5
  click1_x = 235.381
  click1_y = 166.065
  click2_x = 226.939
  click2_y = 166.39
  click3_x = 226.939
  click3_y = 166.39
  comma_decimal_place = false
  lineColor = rgb(0,0,255)
  strokeWidth = 0.5
  textFormat_circular = Ø%(value)3.3f
  textRenderer_color = rgb(0,0,255)
  textRenderer_family = inherit
  textRenderer_size = 3.6
  unit_custom_scale = 1
  unit_scheme = 0
FEATURE [Drawing::FeatureViewPython] text019  # drawing view (typed FeaturePython)
  Rotation = 0
  ViewResult = <g> <text x="228.950066" y="168.687050" font-family="inherit" font-size="3,6" fill="rgb(0,0,255)" text-anchor="inherit" transform="rotate(0.000000 228.950066,168.687050)" >H1</text> </g>
  Visible = false
  X = 0
  Y = 0
  click1_x = 228.95
  click1_y = 168.687
  rotation = 0
  text = H1
  textRenderer_addText_color = rgb(0,0,255)
  textRenderer_addText_family = inherit
  textRenderer_addText_size = 3,6
FEATURE [Drawing::FeatureViewPython] text020  # drawing view (typed FeaturePython)
  Rotation = 0
  ViewResult = <g> <text x="219.108616" y="151.360746" font-family="inherit" font-size="3,6" fill="rgb(0,0,255)" text-anchor="inherit" transform="rotate(0.000000 219.108616,151.360746)" >H1</text> </g>
  Visible = false
  X = 0
  Y = 0
  click1_x = 219.109
  click1_y = 151.361
  rotation = 0
  text = H1
  textRenderer_addText_color = rgb(0,0,255)
  textRenderer_addText_family = inherit
  textRenderer_addText_size = 3,6
FEATURE [Drawing::FeatureViewPython] text021  # drawing view (typed FeaturePython)
  Rotation = 0
  ViewResult = <g> <text x="218.165291" y="131.979710" font-family="inherit" font-size="3,6" fill="rgb(0,0,255)" text-anchor="inherit" transform="rotate(0.000000 218.165291,131.979710)" >H1</text> </g>
  Visible = false
  X = 0
  Y = 0
  click1_x = 218.165
  click1_y = 131.98
  rotation = 0
  text = H1
  textRenderer_addText_color = rgb(0,0,255)
  textRenderer_addText_family = inherit
  textRenderer_addText_size = 3,6
FEATURE [Drawing::FeatureViewPython] text022  # drawing view (typed FeaturePython)
  Rotation = 0
  ViewResult = <g> <text x="239.947517" y="131.979710" font-family="inherit" font-size="3,6" fill="rgb(0,0,255)" text-anchor="inherit" transform="rotate(0.000000 239.947517,131.979710)" >H1</text> </g>
  Visible = false
  X = 0
  Y = 0
  click1_x = 239.948
  click1_y = 131.98
  rotation = 0
  text = H1
  textRenderer_addText_color = rgb(0,0,255)
  textRenderer_addText_family = inherit
  textRenderer_addText_size = 3,6
FEATURE [Drawing::FeatureViewPython] dim039  # drawing view (typed FeaturePython)
  Rotation = 0
  ViewResult = <g> \n  <line x1="240.648000" y1="126.196760" x2="240.648000" y2="117.771342" style="stroke:rgb(0,0,255);stroke-width:0.50" />\n<line x1="231.048000" y1="119.720344" x2="231.048000" y2="119.771342" style="stroke:rgb(0,0,255);stroke-width:0.50" />\n<line x1="240.648000" y1="118.771342" x2="231.048000" y2="118.771342" style="stroke:rgb(0,0,255);stroke-width:0.50" /> \n  <polygon points="231.048000,118.771342 228.048000,117.771342 227.048000,118.771342 228.048000,119.771342" style="fill:rgb(0,0,255);stroke:rgb(0,0,255);stroke-width:0" /><polygon points="240.648000,118.771342 243.648000,119.771342 244.648000,118.771342 243.648000,117.771342" style="fill:rgb(0,0,255);stroke:rgb(0,0,255);stroke-width:0" /> \n  <text x="235.848000" y="116.771342" font-family="inherit" font-size="3.6" fill="rgb(0,0,255)" text-anchor="middle" transform="rotate(0.000000 235.848000,116.771342)" >8</text> </g>
  Visible = false
  X = 0
  Y = 0
  arrowL1 = 3
  arrowL2 = 1
  arrowW = 2
  arrow_scheme = 0
  autoPlaceOffset = 2
  autoPlaceText = true
  click1_x = 232.484
  click1_y = 118.771
  click2_x = 232.484
  click2_y = 118.771
  comma_decimal_place = false
  dimension_line_overshoot = 1
  gap_datum_points = 2
  halfDimension_linear = false
  lineColor = rgb(0,0,255)
  strokeWidth = 0.5
  textFormat_linear = %(value)3.3f
  textRenderer_color = rgb(0,0,255)
  textRenderer_family = inherit
  textRenderer_size = 3.6
  unit_custom_scale = 1
  unit_scheme = 0
FEATURE [Drawing::FeatureViewPython] dim037  # drawing view (typed FeaturePython)
  Rotation = 0
  ViewResult = <g> \n  <line x1="249.248000" y1="125.196760" x2="257.544710" y2="125.196760" style="stroke:rgb(0,0,255);stroke-width:0.50" />\n<line x1="249.248000" y1="152.796760" x2="257.544710" y2="152.796760" style="stroke:rgb(0,0,255);stroke-width:0.50" />\n<line x1="256.544710" y1="125.196760" x2="256.544710" y2="152.796760" style="stroke:rgb(0,0,255);stroke-width:0.50" /> \n  <polygon points="256.544710,152.796760 257.544710,149.796760 256.544710,148.796760 255.544710,149.796760" style="fill:rgb(0,0,255);stroke:rgb(0,0,255);stroke-width:0" /><polygon points="256.544710,125.196760 255.544710,128.196760 256.544710,129.196760 257.544710,128.196760" style="fill:rgb(0,0,255);stroke:rgb(0,0,255);stroke-width:0" /> \n  <text x="254.544710" y="138.996760" font-family="inherit" font-size="3.6" fill="rgb(0,0,255)" text-anchor="middle" transform="rotate(-90.000000 254.544710,138.996760)" >23</text> </g>
  Visible = false
  X = 0
  Y = 0
  arrowL1 = 3
  arrowL2 = 1
  arrowW = 2
  arrow_scheme = 0
  autoPlaceOffset = 2
  autoPlaceText = true
  click1_x = 256.545
  click1_y = 153.001
  click2_x = 256.545
  click2_y = 153.001
  comma_decimal_place = false
  dimension_line_overshoot = 1
  gap_datum_points = 2
  halfDimension_linear = false
  lineColor = rgb(0,0,255)
  strokeWidth = 0.5
  textFormat_linear = %(value)3.3f
  textRenderer_color = rgb(0,0,255)
  textRenderer_family = inherit
  textRenderer_size = 3.6
  unit_custom_scale = 1
  unit_scheme = 0
FEATURE [Drawing::FeatureViewPart] Ortho007  label="Ortho_Right_Nozzle_Fix_Section"
  Direction = (0,0,-1)
  HiddenWidth = 0.15
  LineWidth = 0.35
  Rotation = 180
  Scale = 1.2
  ShowHiddenLines = false
  ShowSmoothLines = false
  Source = -> Body006021004
  Tolerance = 0.05
  ViewResult = <g id="Ortho_Right_Nozzle_Fix_Section"\n   transform="rotate(180,282.1,317) translate(282.1,317) scale(1.2,1.2)"\n  >\n<g   fill="none"\n   stroke="rgb(0, 0, 0)"\n   stroke-linecap="butt"\n   stroke-linejoin="miter"\n   stroke-width="0.291667"\n   transform="scale(1,-1)"\n  >\n<path id= "1" d=" M 56.04 -105.83 L 56.04 -111.83 " />\n<path id= "2" d=" M 29.04 -105.83 L 29.04 -111.83 " />\n<path id= "3" d=" M 29.04 -105.83 L 56.04 -105.83 " />\n<path id= "4" d=" M 29.04 -111.83 L 56.04 -111.83 " />\n<circle cx ="46.04" cy ="-108.83" r ="0.8" /><circle cx ="53.04" cy ="-108.83" r ="0.8" /><circle cx ="32.04" cy ="-108.83" r ="0.8" /><circle cx ="39.04" cy ="-108.83" r ="0.8" /></g>\n</g>
  Visible = false
  X = 282.1
  Y = 317
FEATURE [Drawing::FeatureViewPython] dim042  # drawing view (typed FeaturePython)
  Rotation = 0
  ViewResult = <g> \n  <line x1="249.252000" y1="182.804000" x2="257.068423" y2="182.804000" style="stroke:rgb(0,0,255);stroke-width:0.50" />\n<line x1="249.252000" y1="190.004000" x2="257.068423" y2="190.004000" style="stroke:rgb(0,0,255);stroke-width:0.50" />\n<line x1="256.068423" y1="182.804000" x2="256.068423" y2="190.004000" style="stroke:rgb(0,0,255);stroke-width:0.50" /> \n  <polygon points="256.068423,190.004000 255.068423,193.004000 256.068423,194.004000 257.068423,193.004000" style="fill:rgb(0,0,255);stroke:rgb(0,0,255);stroke-width:0" /><polygon points="256.068423,182.804000 257.068423,179.804000 256.068423,178.804000 255.068423,179.804000" style="fill:rgb(0,0,255);stroke:rgb(0,0,255);stroke-width:0" /> \n  <text x="254.068423" y="186.404000" font-family="inherit" font-size="3.6" fill="rgb(0,0,255)" text-anchor="middle" transform="rotate(-90.000000 254.068423,186.404000)" >6</text> </g>
  Visible = false
  X = 0
  Y = 0
  arrowL1 = 3
  arrowL2 = 1
  arrowW = 2
  arrow_scheme = 0
  autoPlaceOffset = 2
  autoPlaceText = true
  click1_x = 256.068
  click1_y = 191.162
  click2_x = 256.068
  click2_y = 191.162
  comma_decimal_place = false
  dimension_line_overshoot = 1
  gap_datum_points = 2
  halfDimension_linear = false
  lineColor = rgb(0,0,255)
  strokeWidth = 0.5
  textFormat_linear = %(value)3.3f
  textRenderer_color = rgb(0,0,255)
  textRenderer_family = inherit
  textRenderer_size = 3.6
  unit_custom_scale = 1
  unit_scheme = 0
FEATURE [Drawing::FeatureViewPython] dim043  # drawing view (typed FeaturePython)
  Rotation = 0
  ViewResult = <g> \n  <line x1="214.852000" y1="180.804000" x2="214.852000" y2="175.580517" style="stroke:rgb(0,0,255);stroke-width:0.50" />\n<line x1="247.252000" y1="180.804000" x2="247.252000" y2="175.580517" style="stroke:rgb(0,0,255);stroke-width:0.50" />\n<line x1="214.852000" y1="176.580517" x2="247.252000" y2="176.580517" style="stroke:rgb(0,0,255);stroke-width:0.50" /> \n  <polygon points="247.252000,176.580517 244.252000,175.580517 243.252000,176.580517 244.252000,177.580517" style="fill:rgb(0,0,255);stroke:rgb(0,0,255);stroke-width:0" /><polygon points="214.852000,176.580517 217.852000,177.580517 218.852000,176.580517 217.852000,175.580517" style="fill:rgb(0,0,255);stroke:rgb(0,0,255);stroke-width:0" /> \n  <text x="231.052000" y="174.580517" font-family="inherit" font-size="3.6" fill="rgb(0,0,255)" text-anchor="middle" transform="rotate(0.000000 231.052000,174.580517)" >27</text> </g>
  Visible = false
  X = 0
  Y = 0
  arrowL1 = 3
  arrowL2 = 1
  arrowW = 2
  arrow_scheme = 0
  autoPlaceOffset = 2
  autoPlaceText = true
  click1_x = 249.489
  click1_y = 176.581
  click2_x = 249.489
  click2_y = 176.581
  comma_decimal_place = false
  dimension_line_overshoot = 1
  gap_datum_points = 2
  halfDimension_linear = false
  lineColor = rgb(0,0,255)
  strokeWidth = 0.5
  textFormat_linear = %(value)3.3f
  textRenderer_color = rgb(0,0,255)
  textRenderer_family = inherit
  textRenderer_size = 3.6
  unit_custom_scale = 1
  unit_scheme = 0
FEATURE [Drawing::FeatureViewPython] dim044  # drawing view (typed FeaturePython)
  Rotation = 0
  ViewResult = <g> \n  <line x1="218.452000" y1="188.404000" x2="218.452000" y2="197.886490" style="stroke:rgb(0,0,255);stroke-width:0.50" />\n<line x1="226.852000" y1="188.404000" x2="226.852000" y2="197.886490" style="stroke:rgb(0,0,255);stroke-width:0.50" />\n<line x1="218.452000" y1="196.886490" x2="226.852000" y2="196.886490" style="stroke:rgb(0,0,255);stroke-width:0.50" /> \n  <polygon points="226.852000,196.886490 229.852000,197.886490 230.852000,196.886490 229.852000,195.886490" style="fill:rgb(0,0,255);stroke:rgb(0,0,255);stroke-width:0" /><polygon points="218.452000,196.886490 215.452000,195.886490 214.452000,196.886490 215.452000,197.886490" style="fill:rgb(0,0,255);stroke:rgb(0,0,255);stroke-width:0" /> \n  <text x="222.652000" y="194.886490" font-family="inherit" font-size="3.6" fill="rgb(0,0,255)" text-anchor="middle" transform="rotate(0.000000 222.652000,194.886490)" >7</text> </g>
  Visible = false
  X = 0
  Y = 0
  arrowL1 = 3
  arrowL2 = 1
  arrowW = 2
  arrow_scheme = 0
  autoPlaceOffset = 2
  autoPlaceText = true
  click1_x = 228.005
  click1_y = 196.886
  click2_x = 228.005
  click2_y = 196.886
  comma_decimal_place = false
  dimension_line_overshoot = 1
  gap_datum_points = 2
  halfDimension_linear = false
  lineColor = rgb(0,0,255)
  strokeWidth = 0.5
  textFormat_linear = %(value)3.3f
  textRenderer_color = rgb(0,0,255)
  textRenderer_family = inherit
  textRenderer_size = 3.6
  unit_custom_scale = 1
  unit_scheme = 0
FEATURE [Drawing::FeatureViewPython] dim045  # drawing view (typed FeaturePython)
  Rotation = 0
  ViewResult = <g> \n  <line x1="226.852000" y1="188.404000" x2="226.852000" y2="197.882564" style="stroke:rgb(0,0,255);stroke-width:0.50" />\n<line x1="235.252000" y1="188.404000" x2="235.252000" y2="197.882564" style="stroke:rgb(0,0,255);stroke-width:0.50" />\n<line x1="226.852000" y1="196.882564" x2="235.252000" y2="196.882564" style="stroke:rgb(0,0,255);stroke-width:0.50" /> \n  <polygon points="235.252000,196.882564 238.252000,197.882564 239.252000,196.882564 238.252000,195.882564" style="fill:rgb(0,0,255);stroke:rgb(0,0,255);stroke-width:0" /><polygon points="226.852000,196.882564 223.852000,195.882564 222.852000,196.882564 223.852000,197.882564" style="fill:rgb(0,0,255);stroke:rgb(0,0,255);stroke-width:0" /> \n  <text x="231.052000" y="194.882564" font-family="inherit" font-size="3.6" fill="rgb(0,0,255)" text-anchor="middle" transform="rotate(0.000000 231.052000,194.882564)" >7</text> </g>
  Visible = false
  X = 0
  Y = 0
  arrowL1 = 3
  arrowL2 = 1
  arrowW = 2
  arrow_scheme = 0
  autoPlaceOffset = 2
  autoPlaceText = true
  click1_x = 235.995
  click1_y = 196.883
  click2_x = 235.995
  click2_y = 196.883
  comma_decimal_place = false
  dimension_line_overshoot = 1
  gap_datum_points = 2
  halfDimension_linear = false
  lineColor = rgb(0,0,255)
  strokeWidth = 0.5
  textFormat_linear = %(value)3.3f
  textRenderer_color = rgb(0,0,255)
  textRenderer_family = inherit
  textRenderer_size = 3.6
  unit_custom_scale = 1
  unit_scheme = 0
FEATURE [Drawing::FeatureViewPython] dim046  # drawing view (typed FeaturePython)
  Rotation = 0
  ViewResult = <g> \n  <line x1="235.252000" y1="188.404000" x2="235.252000" y2="197.874076" style="stroke:rgb(0,0,255);stroke-width:0.50" />\n<line x1="243.652000" y1="188.404000" x2="243.652000" y2="197.874076" style="stroke:rgb(0,0,255);stroke-width:0.50" />\n<line x1="235.252000" y1="196.874076" x2="243.652000" y2="196.874076" style="stroke:rgb(0,0,255);stroke-width:0.50" /> \n  <polygon points="243.652000,196.874076 246.652000,197.874076 247.652000,196.874076 246.652000,195.874076" style="fill:rgb(0,0,255);stroke:rgb(0,0,255);stroke-width:0" /><polygon points="235.252000,196.874076 232.252000,195.874076 231.252000,196.874076 232.252000,197.874076" style="fill:rgb(0,0,255);stroke:rgb(0,0,255);stroke-width:0" /> \n  <text x="239.452000" y="194.874076" font-family="inherit" font-size="3.6" fill="rgb(0,0,255)" text-anchor="middle" transform="rotate(0.000000 239.452000,194.874076)" >7</text> </g>
  Visible = false
  X = 0
  Y = 0
  arrowL1 = 3
  arrowL2 = 1
  arrowW = 2
  arrow_scheme = 0
  autoPlaceOffset = 2
  autoPlaceText = true
  click1_x = 244.635
  click1_y = 196.874
  click2_x = 244.635
  click2_y = 196.874
  comma_decimal_place = false
  dimension_line_overshoot = 1
  gap_datum_points = 2
  halfDimension_linear = false
  lineColor = rgb(0,0,255)
  strokeWidth = 0.5
  textFormat_linear = %(value)3.3f
  textRenderer_color = rgb(0,0,255)
  textRenderer_family = inherit
  textRenderer_size = 3.6
  unit_custom_scale = 1
  unit_scheme = 0
FEATURE [Drawing::FeatureViewPython] dim047  # drawing view (typed FeaturePython)
  Rotation = 0
  ViewResult = <g> \n  <line x1="214.852000" y1="192.004000" x2="214.852000" y2="204.726084" style="stroke:rgb(0,0,255);stroke-width:0.50" />\n<line x1="218.452000" y1="188.404000" x2="218.452000" y2="204.726084" style="stroke:rgb(0,0,255);stroke-width:0.50" />\n<line x1="214.852000" y1="203.726084" x2="218.452000" y2="203.726084" style="stroke:rgb(0,0,255);stroke-width:0.50" /> \n  <polygon points="218.452000,203.726084 221.452000,204.726084 222.452000,203.726084 221.452000,202.726084" style="fill:rgb(0,0,255);stroke:rgb(0,0,255);stroke-width:0" /><polygon points="214.852000,203.726084 211.852000,202.726084 210.852000,203.726084 211.852000,204.726084" style="fill:rgb(0,0,255);stroke:rgb(0,0,255);stroke-width:0" /> \n  <text x="216.652000" y="201.726084" font-family="inherit" font-size="3.6" fill="rgb(0,0,255)" text-anchor="middle" transform="rotate(0.000000 216.652000,201.726084)" >3</text> </g>
  Visible = false
  X = 0
  Y = 0
  arrowL1 = 3
  arrowL2 = 1
  arrowW = 2
  arrow_scheme = 0
  autoPlaceOffset = 2
  autoPlaceText = true
  click1_x = 215.36
  click1_y = 203.726
  click2_x = 215.36
  click2_y = 203.726
  comma_decimal_place = false
  dimension_line_overshoot = 1
  gap_datum_points = 2
  halfDimension_linear = false
  lineColor = rgb(0,0,255)
  strokeWidth = 0.5
  textFormat_linear = %(value)3.3f
  textRenderer_color = rgb(0,0,255)
  textRenderer_family = inherit
  textRenderer_size = 3.6
  unit_custom_scale = 1
  unit_scheme = 0
FEATURE [Drawing::FeatureViewPython] dim048  # drawing view (typed FeaturePython)
  Rotation = 0
  ViewResult = <g> \n  <line x1="243.652000" y1="187.444000" x2="243.652000" y2="204.996637" style="stroke:rgb(0,0,255);stroke-width:0.50" />\n<line x1="247.252000" y1="192.004000" x2="247.252000" y2="204.996637" style="stroke:rgb(0,0,255);stroke-width:0.50" />\n<line x1="243.652000" y1="203.996637" x2="247.252000" y2="203.996637" style="stroke:rgb(0,0,255);stroke-width:0.50" /> \n  <polygon points="247.252000,203.996637 250.252000,204.996637 251.252000,203.996637 250.252000,202.996637" style="fill:rgb(0,0,255);stroke:rgb(0,0,255);stroke-width:0" /><polygon points="243.652000,203.996637 240.652000,202.996637 239.652000,203.996637 240.652000,204.996637" style="fill:rgb(0,0,255);stroke:rgb(0,0,255);stroke-width:0" /> \n  <text x="245.452000" y="201.996637" font-family="inherit" font-size="3.6" fill="rgb(0,0,255)" text-anchor="middle" transform="rotate(0.000000 245.452000,201.996637)" >3</text> </g>
  Visible = false
  X = 0
  Y = 0
  arrowL1 = 3
  arrowL2 = 1
  arrowW = 2
  arrow_scheme = 0
  autoPlaceOffset = 2
  autoPlaceText = true
  click1_x = 246.338
  click1_y = 203.997
  click2_x = 246.338
  click2_y = 203.997
  comma_decimal_place = false
  dimension_line_overshoot = 1
  gap_datum_points = 2
  halfDimension_linear = false
  lineColor = rgb(0,0,255)
  strokeWidth = 0.5
  textFormat_linear = %(value)3.3f
  textRenderer_color = rgb(0,0,255)
  textRenderer_family = inherit
  textRenderer_size = 3.6
  unit_custom_scale = 1
  unit_scheme = 0
FEATURE [Drawing::FeatureViewPython] dim049  # drawing view (typed FeaturePython)
  Rotation = 0
  ViewResult = <g> \n  <line x1="217.412000" y1="186.404000" x2="208.829730" y2="186.404000" style="stroke:rgb(0,0,255);stroke-width:0.50" />\n<line x1="212.852000" y1="182.804000" x2="208.829730" y2="182.804000" style="stroke:rgb(0,0,255);stroke-width:0.50" />\n<line x1="209.829730" y1="186.404000" x2="209.829730" y2="182.804000" style="stroke:rgb(0,0,255);stroke-width:0.50" /> \n  <polygon points="209.829730,182.804000 210.829730,179.804000 209.829730,178.804000 208.829730,179.804000" style="fill:rgb(0,0,255);stroke:rgb(0,0,255);stroke-width:0" /><polygon points="209.829730,186.404000 208.829730,189.404000 209.829730,190.404000 210.829730,189.404000" style="fill:rgb(0,0,255);stroke:rgb(0,0,255);stroke-width:0" /> \n  <text x="207.829730" y="184.604000" font-family="inherit" font-size="3.6" fill="rgb(0,0,255)" text-anchor="middle" transform="rotate(-90.000000 207.829730,184.604000)" >3</text> </g>
  Visible = false
  X = 0
  Y = 0
  arrowL1 = 3
  arrowL2 = 1
  arrowW = 2
  arrow_scheme = 0
  autoPlaceOffset = 2
  autoPlaceText = true
  click1_x = 209.83
  click1_y = 183.691
  click2_x = 209.83
  click2_y = 183.691
  comma_decimal_place = false
  dimension_line_overshoot = 1
  gap_datum_points = 2
  halfDimension_linear = false
  lineColor = rgb(0,0,255)
  strokeWidth = 0.5
  textFormat_linear = %(value)3.3f
  textRenderer_color = rgb(0,0,255)
  textRenderer_family = inherit
  textRenderer_size = 3.6
  unit_custom_scale = 1
  unit_scheme = 0
FEATURE [Drawing::FeatureViewPython] dia013  # drawing view (typed FeaturePython)
  Rotation = 0
  ViewResult = <g>  <circle cx ="218.452000" cy ="186.404000" r="0.250000" stroke="none" fill="rgb(0,0,255)" /> \n<line x1="205.559042" y1="198.784255" x2="219.144451" y2="185.739085" style="stroke:rgb(0,0,255);stroke-width:0.50" />\n<polygon points="217.759549,187.068915 214.903020,188.425471 214.874337,189.839393 216.288260,189.868077" style="fill:rgb(0,0,255);stroke:rgb(0,0,255);stroke-width:0" />\n<polygon points="219.144451,185.739085 222.000980,184.382529 222.029663,182.968607 220.615740,182.939923" style="fill:rgb(0,0,255);stroke:rgb(0,0,255);stroke-width:0" />\n<line x1="205.559042" y1="198.784255" x2="190.465846" y2="198.784255" style="stroke:rgb(0,0,255);stroke-width:0.50" />\n<text x="198.012444" y="196.784255" font-family="inherit" font-size="3.6" fill="rgb(0,0,255)" text-anchor="middle" transform="rotate(0.000000 198.012444,196.784255)" >Ø1.6</text> </g>
  Visible = false
  X = 0
  Y = 0
  arrowL1 = 3
  arrowL2 = 1
  arrowW = 2
  arrow_scheme = 0
  autoPlaceOffset = 2
  autoPlaceText = true
  centerPointDia = 0.5
  click1_x = 205.559
  click1_y = 198.784
  click2_x = 190.466
  click2_y = 197.584
  click3_x = 190.466
  click3_y = 197.584
  comma_decimal_place = false
  lineColor = rgb(0,0,255)
  strokeWidth = 0.5
  textFormat_circular = Ø%(value)3.3f
  textRenderer_color = rgb(0,0,255)
  textRenderer_family = inherit
  textRenderer_size = 3.6
  unit_custom_scale = 1
  unit_scheme = 0
FEATURE [Drawing::FeatureViewPython] text023  # drawing view (typed FeaturePython)
  Rotation = 0
  ViewResult = <g> <text x="195.203678" y="202.508598" font-family="inherit" font-size="3,6" fill="rgb(0,0,255)" text-anchor="inherit" transform="rotate(0.000000 195.203678,202.508598)" >H2</text> </g>
  Visible = false
  X = 0
  Y = 0
  click1_x = 195.204
  click1_y = 202.509
  rotation = 0
  text = H2
  textRenderer_addText_color = rgb(0,0,255)
  textRenderer_addText_family = inherit
  textRenderer_addText_size = 3,6
FEATURE [Drawing::FeatureViewPython] text024  # drawing view (typed FeaturePython)
  Rotation = 0
  ViewResult = <g> <text x="224.516058" y="185.091753" font-family="inherit" font-size="3,6" fill="rgb(0,0,255)" text-anchor="inherit" transform="rotate(0.000000 224.516058,185.091753)" >H2</text> </g>
  Visible = false
  X = 0
  Y = 0
  click1_x = 224.516
  click1_y = 185.092
  rotation = 0
  text = H2
  textRenderer_addText_color = rgb(0,0,255)
  textRenderer_addText_family = inherit
  textRenderer_addText_size = 3,6
FEATURE [Drawing::FeatureViewPython] text025  # drawing view (typed FeaturePython)
  Rotation = 0
  ViewResult = <g> <text x="232.913078" y="185.091753" font-family="inherit" font-size="3,6" fill="rgb(0,0,255)" text-anchor="inherit" transform="rotate(0.000000 232.913078,185.091753)" >H2</text> </g>
  Visible = false
  X = 0
  Y = 0
  click1_x = 232.913
  click1_y = 185.092
  rotation = 0
  text = H2
  textRenderer_addText_color = rgb(0,0,255)
  textRenderer_addText_family = inherit
  textRenderer_addText_size = 3,6
FEATURE [Drawing::FeatureViewPython] text026  # drawing view (typed FeaturePython)
  Rotation = 0
  ViewResult = <g> <text x="241.369651" y="185.091753" font-family="inherit" font-size="3,6" fill="rgb(0,0,255)" text-anchor="inherit" transform="rotate(0.000000 241.369651,185.091753)" >H2</text> </g>
  Visible = false
  X = 0
  Y = 0
  click1_x = 241.37
  click1_y = 185.092
  rotation = 0
  text = H2
  textRenderer_addText_color = rgb(0,0,255)
  textRenderer_addText_family = inherit
  textRenderer_addText_size = 3,6
FEATURE [Drawing::FeatureViewPython] dim050  # drawing view (typed FeaturePython)
  Rotation = 0
  ViewResult = <g> \n  <line x1="32.800000" y1="201.092000" x2="32.800000" y2="211.918439" style="stroke:rgb(0,0,255);stroke-width:0.50" />\n<line x1="40.000000" y1="201.092000" x2="40.000000" y2="211.918439" style="stroke:rgb(0,0,255);stroke-width:0.50" />\n<line x1="32.800000" y1="210.918439" x2="40.000000" y2="210.918439" style="stroke:rgb(0,0,255);stroke-width:0.50" /> \n  <polygon points="40.000000,210.918439 43.000000,211.918439 44.000000,210.918439 43.000000,209.918439" style="fill:rgb(0,0,255);stroke:rgb(0,0,255);stroke-width:0" /><polygon points="32.800000,210.918439 29.800000,209.918439 28.800000,210.918439 29.800000,211.918439" style="fill:rgb(0,0,255);stroke:rgb(0,0,255);stroke-width:0" /> \n  <text x="36.400000" y="208.918439" font-family="inherit" font-size="3.6" fill="rgb(0,0,255)" text-anchor="middle" transform="rotate(0.000000 36.400000,208.918439)" >6</text> </g>
  Visible = false
  X = 0
  Y = 0
  arrowL1 = 3
  arrowL2 = 1
  arrowW = 2
  arrow_scheme = 0
  autoPlaceOffset = 2
  autoPlaceText = true
  click1_x = 43.1424
  click1_y = 210.918
  click2_x = 43.1424
  click2_y = 210.918
  comma_decimal_place = false
  dimension_line_overshoot = 1
  gap_datum_points = 2
  halfDimension_linear = false
  lineColor = rgb(0,0,255)
  strokeWidth = 0.5
  textFormat_linear = %(value)3.3f
  textRenderer_color = rgb(0,0,255)
  textRenderer_family = inherit
  textRenderer_size = 3.6
  unit_custom_scale = 1
  unit_scheme = 0
FEATURE [Drawing::FeatureViewPython] dim051  # drawing view (typed FeaturePython)
  Rotation = 0
  ViewResult = <g> \n  <line x1="42.000000" y1="199.092000" x2="55.948016" y2="199.092000" style="stroke:rgb(0,0,255);stroke-width:0.50" />\n<line x1="42.000000" y1="123.840000" x2="55.948016" y2="123.840000" style="stroke:rgb(0,0,255);stroke-width:0.50" />\n<line x1="54.948016" y1="199.092000" x2="54.948016" y2="123.840000" style="stroke:rgb(0,0,255);stroke-width:0.50" /> \n  <polygon points="54.948016,123.840000 53.948016,126.840000 54.948016,127.840000 55.948016,126.840000" style="fill:rgb(0,0,255);stroke:rgb(0,0,255);stroke-width:0" /><polygon points="54.948016,199.092000 55.948016,196.092000 54.948016,195.092000 53.948016,196.092000" style="fill:rgb(0,0,255);stroke:rgb(0,0,255);stroke-width:0" /> \n  <text x="52.948016" y="161.466000" font-family="inherit" font-size="3.6" fill="rgb(0,0,255)" text-anchor="middle" transform="rotate(-90.000000 52.948016,161.466000)" >62.71</text> </g>
  Visible = false
  X = 0
  Y = 0
  arrowL1 = 3
  arrowL2 = 1
  arrowW = 2
  arrow_scheme = 0
  autoPlaceOffset = 2
  autoPlaceText = true
  click1_x = 54.948
  click1_y = 125.189
  click2_x = 54.948
  click2_y = 125.189
  comma_decimal_place = false
  dimension_line_overshoot = 1
  gap_datum_points = 2
  halfDimension_linear = false
  lineColor = rgb(0,0,255)
  strokeWidth = 0.5
  textFormat_linear = %(value)3.3f
  textRenderer_color = rgb(0,0,255)
  textRenderer_family = inherit
  textRenderer_size = 3.6
  unit_custom_scale = 1
  unit_scheme = 0
FEATURE [Drawing::FeatureViewPython] dim052  # drawing view (typed FeaturePython)
  Rotation = 0
  ViewResult = <g> \n  <line x1="42.000000" y1="118.692000" x2="55.829466" y2="118.692000" style="stroke:rgb(0,0,255);stroke-width:0.50" />\n<line x1="42.000000" y1="32.472000" x2="55.829466" y2="32.472000" style="stroke:rgb(0,0,255);stroke-width:0.50" />\n<line x1="54.829466" y1="118.692000" x2="54.829466" y2="32.472000" style="stroke:rgb(0,0,255);stroke-width:0.50" /> \n  <polygon points="54.829466,32.472000 53.829466,35.472000 54.829466,36.472000 55.829466,35.472000" style="fill:rgb(0,0,255);stroke:rgb(0,0,255);stroke-width:0" /><polygon points="54.829466,118.692000 55.829466,115.692000 54.829466,114.692000 53.829466,115.692000" style="fill:rgb(0,0,255);stroke:rgb(0,0,255);stroke-width:0" /> \n  <text x="52.829466" y="75.582000" font-family="inherit" font-size="3.6" fill="rgb(0,0,255)" text-anchor="middle" transform="rotate(-90.000000 52.829466,75.582000)" >71.85</text> </g>
  Visible = false
  X = 0
  Y = 0
  arrowL1 = 3
  arrowL2 = 1
  arrowW = 2
  arrow_scheme = 0
  autoPlaceOffset = 2
  autoPlaceText = true
  click1_x = 54.8295
  click1_y = 83.1333
  click2_x = 54.8295
  click2_y = 83.1333
  comma_decimal_place = false
  dimension_line_overshoot = 1
  gap_datum_points = 2
  halfDimension_linear = false
  lineColor = rgb(0,0,255)
  strokeWidth = 0.5
  textFormat_linear = %(value)3.3f
  textRenderer_color = rgb(0,0,255)
  textRenderer_family = inherit
  textRenderer_size = 3.6
  unit_custom_scale = 1
  unit_scheme = 0
FEATURE [Drawing::FeatureViewPython] dim053  # drawing view (typed FeaturePython)
  Rotation = 0
  ViewResult = <g> \n  <line x1="30.800000" y1="199.092000" x2="20.924377" y2="199.092000" style="stroke:rgb(0,0,255);stroke-width:0.50" />\n<line x1="30.800000" y1="32.472000" x2="20.924377" y2="32.472000" style="stroke:rgb(0,0,255);stroke-width:0.50" />\n<line x1="21.924377" y1="199.092000" x2="21.924377" y2="32.472000" style="stroke:rgb(0,0,255);stroke-width:0.50" /> \n  <polygon points="21.924377,32.472000 20.924377,35.472000 21.924377,36.472000 22.924377,35.472000" style="fill:rgb(0,0,255);stroke:rgb(0,0,255);stroke-width:0" /><polygon points="21.924377,199.092000 22.924377,196.092000 21.924377,195.092000 20.924377,196.092000" style="fill:rgb(0,0,255);stroke:rgb(0,0,255);stroke-width:0" /> \n  <text x="19.924377" y="115.782000" font-family="inherit" font-size="3.6" fill="rgb(0,0,255)" text-anchor="middle" transform="rotate(-90.000000 19.924377,115.782000)" >138.85</text> </g>
  Visible = false
  X = 0
  Y = 0
  arrowL1 = 3
  arrowL2 = 1
  arrowW = 2
  arrow_scheme = 0
  autoPlaceOffset = 2
  autoPlaceText = true
  click1_x = 21.9244
  click1_y = 52.0024
  click2_x = 21.9244
  click2_y = 52.0024
  comma_decimal_place = false
  dimension_line_overshoot = 1
  gap_datum_points = 2
  halfDimension_linear = false
  lineColor = rgb(0,0,255)
  strokeWidth = 0.5
  textFormat_linear = %(value)3.3f
  textRenderer_color = rgb(0,0,255)
  textRenderer_family = inherit
  textRenderer_size = 3.6
  unit_custom_scale = 1
  unit_scheme = 0
FEATURE [Drawing::FeatureViewPython] dim054  # drawing view (typed FeaturePython)
  Rotation = 0
  ViewResult = <g> \n  <line x1="140.010000" y1="120.692000" x2="140.010000" y2="126.599630" style="stroke:rgb(0,0,255);stroke-width:0.50" />\n<line x1="141.726000" y1="119.384000" x2="141.726000" y2="126.599630" style="stroke:rgb(0,0,255);stroke-width:0.50" />\n<line x1="140.010000" y1="125.599630" x2="141.726000" y2="125.599630" style="stroke:rgb(0,0,255);stroke-width:0.50" /> \n  <polygon points="141.726000,125.599630 144.726000,126.599630 145.726000,125.599630 144.726000,124.599630" style="fill:rgb(0,0,255);stroke:rgb(0,0,255);stroke-width:0" /><polygon points="140.010000,125.599630 137.010000,124.599630 136.010000,125.599630 137.010000,126.599630" style="fill:rgb(0,0,255);stroke:rgb(0,0,255);stroke-width:0" /> \n  <text x="128.825435" y="126.840324" font-family="inherit" font-size="3.6" fill="rgb(0,0,255)" text-anchor="inherit" transform="rotate(0.000000 128.825435,126.840324)" >1.43</text> </g>
  Visible = false
  X = 0
  Y = 0
  arrowL1 = 3
  arrowL2 = 1
  arrowW = 2
  arrow_scheme = 0
  autoPlaceOffset = 2
  autoPlaceText = false
  click1_x = 141.067
  click1_y = 125.6
  click2_x = 128.825
  click2_y = 126.84
  comma_decimal_place = false
  dimension_line_overshoot = 1
  gap_datum_points = 2
  halfDimension_linear = false
  lineColor = rgb(0,0,255)
  strokeWidth = 0.5
  textFormat_linear = %(value)3.3f
  textRenderer_color = rgb(0,0,255)
  textRenderer_family = inherit
  textRenderer_size = 3.6
  unit_custom_scale = 1
  unit_scheme = 0
FEATURE [Drawing::FeatureViewPython] dim055  # drawing view (typed FeaturePython)
  Rotation = 0
  ViewResult = <g> \n  <line x1="138.010000" y1="118.692000" x2="132.736682" y2="118.692000" style="stroke:rgb(0,0,255);stroke-width:0.50" />\n<line x1="138.010000" y1="116.292000" x2="132.736682" y2="116.292000" style="stroke:rgb(0,0,255);stroke-width:0.50" />\n<line x1="133.736682" y1="118.692000" x2="133.736682" y2="116.292000" style="stroke:rgb(0,0,255);stroke-width:0.50" /> \n  <polygon points="133.736682,116.292000 134.736682,113.292000 133.736682,112.292000 132.736682,113.292000" style="fill:rgb(0,0,255);stroke:rgb(0,0,255);stroke-width:0" /><polygon points="133.736682,118.692000 132.736682,121.692000 133.736682,122.692000 134.736682,121.692000" style="fill:rgb(0,0,255);stroke:rgb(0,0,255);stroke-width:0" /> \n  <text x="131.844797" y="118.601603" font-family="inherit" font-size="3.6" fill="rgb(0,0,255)" text-anchor="inherit" transform="rotate(-90.000000 131.844797,118.601603)" >2</text> </g>
  Visible = false
  X = 0
  Y = 0
  arrowL1 = 3
  arrowL2 = 1
  arrowW = 2
  arrow_scheme = 0
  autoPlaceOffset = 2
  autoPlaceText = false
  click1_x = 133.737
  click1_y = 116.123
  click2_x = 131.845
  click2_y = 118.602
  comma_decimal_place = false
  dimension_line_overshoot = 1
  gap_datum_points = 2
  halfDimension_linear = false
  lineColor = rgb(0,0,255)
  strokeWidth = 0.5
  textFormat_linear = %(value)3.3f
  textRenderer_color = rgb(0,0,255)
  textRenderer_family = inherit
  textRenderer_size = 3.6
  unit_custom_scale = 1
  unit_scheme = 0
FEATURE [Drawing::FeatureViewPython] dim056  # drawing view (typed FeaturePython)
  Rotation = 0
  ViewResult = <g> \n  <line x1="143.726000" y1="110.184000" x2="145.913106" y2="110.184000" style="stroke:rgb(0,0,255);stroke-width:0.50" />\n<line x1="143.726000" y1="107.784000" x2="145.913106" y2="107.784000" style="stroke:rgb(0,0,255);stroke-width:0.50" />\n<line x1="144.913106" y1="110.184000" x2="144.913106" y2="107.784000" style="stroke:rgb(0,0,255);stroke-width:0.50" /> \n  <polygon points="144.913106,107.784000 145.913106,104.784000 144.913106,103.784000 143.913106,104.784000" style="fill:rgb(0,0,255);stroke:rgb(0,0,255);stroke-width:0" /><polygon points="144.913106,110.184000 143.913106,113.184000 144.913106,114.184000 145.913106,113.184000" style="fill:rgb(0,0,255);stroke:rgb(0,0,255);stroke-width:0" /> \n  <text x="145.905661" y="103.771679" font-family="inherit" font-size="3.6" fill="rgb(0,0,255)" text-anchor="inherit" transform="rotate(-90.000000 145.905661,103.771679)" >2</text> </g>
  Visible = false
  X = 0
  Y = 0
  arrowL1 = 3
  arrowL2 = 1
  arrowW = 2
  arrow_scheme = 0
  autoPlaceOffset = 2
  autoPlaceText = false
  click1_x = 144.913
  click1_y = 107.99
  click2_x = 145.906
  click2_y = 103.772
  comma_decimal_place = false
  dimension_line_overshoot = 1
  gap_datum_points = 2
  halfDimension_linear = false
  lineColor = rgb(0,0,255)
  strokeWidth = 0.5
  textFormat_linear = %(value)3.3f
  textRenderer_color = rgb(0,0,255)
  textRenderer_family = inherit
  textRenderer_size = 3.6
  unit_custom_scale = 1
  unit_scheme = 0
FEATURE [Drawing::FeatureViewPython] text027  # drawing view (typed FeaturePython)
  Rotation = 0
  ViewResult = <g> <text x="20.000000" y="270.000000" font-family="inherit" font-size="10" fill="rgb(0,0,255)" text-anchor="inherit" transform="rotate(0.000000 20.000000,270.000000)" >Material: aluminium 6mm</text> </g>
  Visible = false
  X = 0
  Y = 0
  click1_x = 20
  click1_y = 270
  rotation = 0
  text = Material: aluminium 6mm
  textRenderer_addText_color = rgb(0,0,255)
  textRenderer_addText_family = inherit
  textRenderer_addText_size = 10
FEATURE [Drawing::FeatureViewPython] table002  # drawing view (typed FeaturePython)
  Rotation = 0
  ViewResult = <blob: 4355 chars omitted>
  Visible = false
  X = 0
  Y = 0
  border_color = rgb(0,0,0)
  border_width = 0.3
  click1_x = 270
  click1_y = 190
  column_widths = [20,20,20,20,24,22]
  contents = Ref | Metric | Drill | Depth | Threaded | Direction | H1 | M2 | 2.20 | - | No | - | H2 | M2 | 1.60 | 4.00 | Yes | CW | H3 | M2 | 1.60 | - | Yes | CCW
  extra_rows = 0
  padding_x = 1
  padding_y = 1
  row_heights = [7]
  textRenderer_table_color = rgb(0,0,0)
  textRenderer_table_family = inherit
  textRenderer_table_size = 5
FEATURE [Drawing::FeatureViewPython] centerLines005  # drawing view (typed FeaturePython)
  Rotation = 0
  ViewResult = <blob: 2584 chars omitted>
  Visible = false
  X = 0
  Y = 0
  centerLine_color = rgb(0,0,255)
  centerLine_len_dash = 6
  centerLine_len_dot = 3
  centerLine_len_gap = 2
  centerLine_width = 0.32
  click1_x = 139.752
  click1_y = 213.5
  click2_x = 139.752
  click2_y = 213.5
FEATURE [Drawing::FeatureViewPython] text028  # drawing view (typed FeaturePython)
  Rotation = 0
  ViewResult = <g> <text x="91.000000" y="106.500000" font-family="inherit" font-size="3,6" fill="rgb(0,0,255)" text-anchor="inherit" transform="rotate(0.000000 91.000000,106.500000)" >H1</text> </g>
  Visible = false
  X = 0
  Y = 0
  click1_x = 91
  click1_y = 106.5
  rotation = 0
  text = H1
  textRenderer_addText_color = rgb(0,0,255)
  textRenderer_addText_family = inherit
  textRenderer_addText_size = 3,6
FEATURE [Drawing::FeatureViewPython] text029  # drawing view (typed FeaturePython)
  Rotation = 0
  ViewResult = <g> <text x="91.000000" y="121.500000" font-family="inherit" font-size="3,6" fill="rgb(0,0,255)" text-anchor="inherit" transform="rotate(0.000000 91.000000,121.500000)" >H1</text> </g>
  Visible = false
  X = 0
  Y = 0
  click1_x = 91
  click1_y = 121.5
  rotation = 0
  text = H1
  textRenderer_addText_color = rgb(0,0,255)
  textRenderer_addText_family = inherit
  textRenderer_addText_size = 3,6
FEATURE [Drawing::FeatureViewPython] text030  # drawing view (typed FeaturePython)
  Rotation = 0
  ViewResult = <g> <text x="91.000000" y="136.500000" font-family="inherit" font-size="3,6" fill="rgb(0,0,255)" text-anchor="inherit" transform="rotate(0.000000 91.000000,136.500000)" >H1</text> </g>
  Visible = false
  X = 0
  Y = 0
  click1_x = 91
  click1_y = 136.5
  rotation = 0
  text = H1
  textRenderer_addText_color = rgb(0,0,255)
  textRenderer_addText_family = inherit
  textRenderer_addText_size = 3,6
FEATURE [Drawing::FeatureViewPython] text031  # drawing view (typed FeaturePython)
  Rotation = 0
  ViewResult = <g> <text x="91.000000" y="151.500000" font-family="inherit" font-size="3,6" fill="rgb(0,0,255)" text-anchor="inherit" transform="rotate(0.000000 91.000000,151.500000)" >H1</text> </g>
  Visible = false
  X = 0
  Y = 0
  click1_x = 91
  click1_y = 151.5
  rotation = 0
  text = H1
  textRenderer_addText_color = rgb(0,0,255)
  textRenderer_addText_family = inherit
  textRenderer_addText_size = 3,6
FEATURE [Drawing::FeatureViewPython] text032  # drawing view (typed FeaturePython)
  Rotation = 0
  ViewResult = <g> <text x="91.000000" y="166.500000" font-family="inherit" font-size="3,6" fill="rgb(0,0,255)" text-anchor="inherit" transform="rotate(0.000000 91.000000,166.500000)" >H1</text> </g>
  Visible = false
  X = 0
  Y = 0
  click1_x = 91
  click1_y = 166.5
  rotation = 0
  text = H1
  textRenderer_addText_color = rgb(0,0,255)
  textRenderer_addText_family = inherit
  textRenderer_addText_size = 3,6
FEATURE [Drawing::FeatureViewPython] text033  # drawing view (typed FeaturePython)
  Rotation = 0
  ViewResult = <g> <text x="128.000000" y="106.500000" font-family="inherit" font-size="3,6" fill="rgb(0,0,255)" text-anchor="inherit" transform="rotate(0.000000 128.000000,106.500000)" >H1</text> </g>
  Visible = false
  X = 0
  Y = 0
  click1_x = 128
  click1_y = 106.5
  rotation = 0
  text = H1
  textRenderer_addText_color = rgb(0,0,255)
  textRenderer_addText_family = inherit
  textRenderer_addText_size = 3,6
FEATURE [Drawing::FeatureViewPython] text034  # drawing view (typed FeaturePython)
  Rotation = 0
  ViewResult = <g> <text x="128.000000" y="121.000000" font-family="inherit" font-size="3,6" fill="rgb(0,0,255)" text-anchor="inherit" transform="rotate(0.000000 128.000000,121.000000)" >H1</text> </g>
  Visible = false
  X = 0
  Y = 0
  click1_x = 128
  click1_y = 121
  rotation = 0
  text = H1
  textRenderer_addText_color = rgb(0,0,255)
  textRenderer_addText_family = inherit
  textRenderer_addText_size = 3,6
FEATURE [Drawing::FeatureViewPython] text035  # drawing view (typed FeaturePython)
  Rotation = 0
  ViewResult = <g> <text x="128.000000" y="136.500000" font-family="inherit" font-size="3,6" fill="rgb(0,0,255)" text-anchor="inherit" transform="rotate(0.000000 128.000000,136.500000)" >H1</text> </g>
  Visible = false
  X = 0
  Y = 0
  click1_x = 128
  click1_y = 136.5
  rotation = 0
  text = H1
  textRenderer_addText_color = rgb(0,0,255)
  textRenderer_addText_family = inherit
  textRenderer_addText_size = 3,6
FEATURE [Drawing::FeatureViewPython] text036  # drawing view (typed FeaturePython)
  Rotation = 0
  ViewResult = <g> <text x="128.000000" y="151.500000" font-family="inherit" font-size="3,6" fill="rgb(0,0,255)" text-anchor="inherit" transform="rotate(0.000000 128.000000,151.500000)" >H1</text> </g>
  Visible = false
  X = 0
  Y = 0
  click1_x = 128
  click1_y = 151.5
  rotation = 0
  text = H1
  textRenderer_addText_color = rgb(0,0,255)
  textRenderer_addText_family = inherit
  textRenderer_addText_size = 3,6
FEATURE [Drawing::FeatureViewPython] text037  # drawing view (typed FeaturePython)
  Rotation = 0
  ViewResult = <g> <text x="128.000000" y="166.500000" font-family="inherit" font-size="3,6" fill="rgb(0,0,255)" text-anchor="inherit" transform="rotate(0.000000 128.000000,166.500000)" >H1</text> </g>
  Visible = false
  X = 0
  Y = 0
  click1_x = 128
  click1_y = 166.5
  rotation = 0
  text = H1
  textRenderer_addText_color = rgb(0,0,255)
  textRenderer_addText_family = inherit
  textRenderer_addText_size = 3,6
FEATURE [Drawing::FeatureViewPython] text038  # drawing view (typed FeaturePython)
  Rotation = 0
  ViewResult = <g> <text x="147.500000" y="106.500000" font-family="inherit" font-size="3,6" fill="rgb(0,0,255)" text-anchor="inherit" transform="rotate(0.000000 147.500000,106.500000)" >H1</text> </g>
  Visible = false
  X = 0
  Y = 0
  click1_x = 147.5
  click1_y = 106.5
  rotation = 0
  text = H1
  textRenderer_addText_color = rgb(0,0,255)
  textRenderer_addText_family = inherit
  textRenderer_addText_size = 3,6
FEATURE [Drawing::FeatureViewPython] text039  # drawing view (typed FeaturePython)
  Rotation = 0
  ViewResult = <g> <text x="147.500000" y="121.500000" font-family="inherit" font-size="3,6" fill="rgb(0,0,255)" text-anchor="inherit" transform="rotate(0.000000 147.500000,121.500000)" >H1</text> </g>
  Visible = false
  X = 0
  Y = 0
  click1_x = 147.5
  click1_y = 121.5
  rotation = 0
  text = H1
  textRenderer_addText_color = rgb(0,0,255)
  textRenderer_addText_family = inherit
  textRenderer_addText_size = 3,6
FEATURE [Drawing::FeatureViewPython] text040  # drawing view (typed FeaturePython)
  Rotation = 0
  ViewResult = <g> <text x="147.500000" y="136.500000" font-family="inherit" font-size="3,6" fill="rgb(0,0,255)" text-anchor="inherit" transform="rotate(0.000000 147.500000,136.500000)" >H1</text> </g>
  Visible = false
  X = 0
  Y = 0
  click1_x = 147.5
  click1_y = 136.5
  rotation = 0
  text = H1
  textRenderer_addText_color = rgb(0,0,255)
  textRenderer_addText_family = inherit
  textRenderer_addText_size = 3,6
FEATURE [Drawing::FeatureViewPython] text041  # drawing view (typed FeaturePython)
  Rotation = 0
  ViewResult = <g> <text x="147.500000" y="151.500000" font-family="inherit" font-size="3,6" fill="rgb(0,0,255)" text-anchor="inherit" transform="rotate(0.000000 147.500000,151.500000)" >H1</text> </g>
  Visible = false
  X = 0
  Y = 0
  click1_x = 147.5
  click1_y = 151.5
  rotation = 0
  text = H1
  textRenderer_addText_color = rgb(0,0,255)
  textRenderer_addText_family = inherit
  textRenderer_addText_size = 3,6
FEATURE [Drawing::FeatureViewPython] text042  # drawing view (typed FeaturePython)
  Rotation = 0
  ViewResult = <g> <text x="147.500000" y="166.500000" font-family="inherit" font-size="3,6" fill="rgb(0,0,255)" text-anchor="inherit" transform="rotate(0.000000 147.500000,166.500000)" >H1</text> </g>
  Visible = false
  X = 0
  Y = 0
  click1_x = 147.5
  click1_y = 166.5
  rotation = 0
  text = H1
  textRenderer_addText_color = rgb(0,0,255)
  textRenderer_addText_family = inherit
  textRenderer_addText_size = 3,6
FEATURE [Drawing::FeatureViewPython] text043  # drawing view (typed FeaturePython)
  Rotation = 0
  ViewResult = <g> <text x="184.500000" y="106.500000" font-family="inherit" font-size="3,6" fill="rgb(0,0,255)" text-anchor="inherit" transform="rotate(0.000000 184.500000,106.500000)" >H1</text> </g>
  Visible = false
  X = 0
  Y = 0
  click1_x = 184.5
  click1_y = 106.5
  rotation = 0
  text = H1
  textRenderer_addText_color = rgb(0,0,255)
  textRenderer_addText_family = inherit
  textRenderer_addText_size = 3,6
FEATURE [Drawing::FeatureViewPython] text044  # drawing view (typed FeaturePython)
  Rotation = 0
  ViewResult = <g> <text x="184.500000" y="121.500000" font-family="inherit" font-size="3,6" fill="rgb(0,0,255)" text-anchor="inherit" transform="rotate(0.000000 184.500000,121.500000)" >H1</text> </g>
  Visible = false
  X = 0
  Y = 0
  click1_x = 184.5
  click1_y = 121.5
  rotation = 0
  text = H1
  textRenderer_addText_color = rgb(0,0,255)
  textRenderer_addText_family = inherit
  textRenderer_addText_size = 3,6
FEATURE [Drawing::FeatureViewPython] text045  # drawing view (typed FeaturePython)
  Rotation = 0
  ViewResult = <g> <text x="184.000000" y="136.500000" font-family="inherit" font-size="3,6" fill="rgb(0,0,255)" text-anchor="inherit" transform="rotate(0.000000 184.000000,136.500000)" >H1</text> </g>
  Visible = false
  X = 0
  Y = 0
  click1_x = 184
  click1_y = 136.5
  rotation = 0
  text = H1
  textRenderer_addText_color = rgb(0,0,255)
  textRenderer_addText_family = inherit
  textRenderer_addText_size = 3,6
FEATURE [Drawing::FeatureViewPython] text046  # drawing view (typed FeaturePython)
  Rotation = 0
  ViewResult = <g> <text x="184.000000" y="151.500000" font-family="inherit" font-size="3,6" fill="rgb(0,0,255)" text-anchor="inherit" transform="rotate(0.000000 184.000000,151.500000)" >H1</text> </g>
  Visible = false
  X = 0
  Y = 0
  click1_x = 184
  click1_y = 151.5
  rotation = 0
  text = H1
  textRenderer_addText_color = rgb(0,0,255)
  textRenderer_addText_family = inherit
  textRenderer_addText_size = 3,6
FEATURE [Drawing::FeatureViewPython] text047  # drawing view (typed FeaturePython)
  Rotation = 0
  ViewResult = <g> <text x="183.500000" y="166.500000" font-family="inherit" font-size="3,6" fill="rgb(0,0,255)" text-anchor="inherit" transform="rotate(0.000000 183.500000,166.500000)" >H1</text> </g>
  Visible = false
  X = 0
  Y = 0
  click1_x = 183.5
  click1_y = 166.5
  rotation = 0
  text = H1
  textRenderer_addText_color = rgb(0,0,255)
  textRenderer_addText_family = inherit
  textRenderer_addText_size = 3,6
FEATURE [Drawing::FeatureViewPython] dim057  # drawing view (typed FeaturePython)
  Rotation = 0
  ViewResult = <g> \n  <line x1="92.000000" y1="188.560000" x2="92.000000" y2="218.000000" style="stroke:rgb(0,0,255);stroke-width:0.50" />\n<line x1="70.000000" y1="196.420000" x2="70.000000" y2="218.000000" style="stroke:rgb(0,0,255);stroke-width:0.50" />\n<line x1="92.000000" y1="217.000000" x2="70.000000" y2="217.000000" style="stroke:rgb(0,0,255);stroke-width:0.50" /> \n  <polygon points="70.000000,217.000000 73.000000,218.000000 74.000000,217.000000 73.000000,216.000000" style="fill:rgb(0,0,255);stroke:rgb(0,0,255);stroke-width:0" /><polygon points="92.000000,217.000000 89.000000,216.000000 88.000000,217.000000 89.000000,218.000000" style="fill:rgb(0,0,255);stroke:rgb(0,0,255);stroke-width:0" /> \n  <text x="81.000000" y="215.000000" font-family="inherit" font-size="3.6" fill="rgb(0,0,255)" text-anchor="middle" transform="rotate(0.000000 81.000000,215.000000)" >22</text> </g>
  Visible = false
  X = 0
  Y = 0
  arrowL1 = 3
  arrowL2 = 1
  arrowW = 2
  arrow_scheme = 0
  autoPlaceOffset = 2
  autoPlaceText = true
  click1_x = 88.5
  click1_y = 217
  click2_x = 88.5
  click2_y = 217
  comma_decimal_place = false
  dimension_line_overshoot = 1
  gap_datum_points = 2
  halfDimension_linear = false
  lineColor = rgb(0,0,255)
  strokeWidth = 0.5
  textFormat_linear = %(value)3.3f
  textRenderer_color = rgb(0,0,255)
  textRenderer_family = inherit
  textRenderer_size = 3.6
  unit_custom_scale = 1
  unit_scheme = 0
FEATURE [Drawing::FeatureViewPython] dim058  # drawing view (typed FeaturePython)
  Rotation = 0
  ViewResult = <g> \n  <line x1="73.000000" y1="199.410000" x2="61.000000" y2="199.410000" style="stroke:rgb(0,0,255);stroke-width:0.50" />\n<line x1="90.000000" y1="186.560000" x2="61.000000" y2="186.560000" style="stroke:rgb(0,0,255);stroke-width:0.50" />\n<line x1="62.000000" y1="199.410000" x2="62.000000" y2="186.560000" style="stroke:rgb(0,0,255);stroke-width:0.50" /> \n  <polygon points="62.000000,186.560000 61.000000,189.560000 62.000000,190.560000 63.000000,189.560000" style="fill:rgb(0,0,255);stroke:rgb(0,0,255);stroke-width:0" /><polygon points="62.000000,199.410000 63.000000,196.410000 62.000000,195.410000 61.000000,196.410000" style="fill:rgb(0,0,255);stroke:rgb(0,0,255);stroke-width:0" /> \n  <text x="60.000000" y="192.985000" font-family="inherit" font-size="3.6" fill="rgb(0,0,255)" text-anchor="middle" transform="rotate(-90.000000 60.000000,192.985000)" >12.85</text> </g>
  Visible = false
  X = 0
  Y = 0
  arrowL1 = 3
  arrowL2 = 1
  arrowW = 2
  arrow_scheme = 0
  autoPlaceOffset = 2
  autoPlaceText = true
  click1_x = 62
  click1_y = 190.5
  click2_x = 62
  click2_y = 190.5
  comma_decimal_place = false
  dimension_line_overshoot = 1
  gap_datum_points = 2
  halfDimension_linear = false
  lineColor = rgb(0,0,255)
  strokeWidth = 0.5
  textFormat_linear = %(value)3.3f
  textRenderer_color = rgb(0,0,255)
  textRenderer_family = inherit
  textRenderer_size = 3.6
  unit_custom_scale = 1
  unit_scheme = 0
FEATURE [Drawing::FeatureViewPython] dim059  # drawing view (typed FeaturePython)
  Rotation = 0
  ViewResult = <g> \n  <line x1="92.000000" y1="188.560000" x2="92.000000" y2="218.000000" style="stroke:rgb(0,0,255);stroke-width:0.50" />\n<line x1="140.000000" y1="215.499609" x2="140.000000" y2="218.000000" style="stroke:rgb(0,0,255);stroke-width:0.50" />\n<line x1="92.000000" y1="217.000000" x2="140.000000" y2="217.000000" style="stroke:rgb(0,0,255);stroke-width:0.50" /> \n  <polygon points="140.000000,217.000000 137.000000,216.000000 136.000000,217.000000 137.000000,218.000000" style="fill:rgb(0,0,255);stroke:rgb(0,0,255);stroke-width:0" /><polygon points="92.000000,217.000000 95.000000,218.000000 96.000000,217.000000 95.000000,216.000000" style="fill:rgb(0,0,255);stroke:rgb(0,0,255);stroke-width:0" /> \n  <text x="116.000000" y="215.000000" font-family="inherit" font-size="3.6" fill="rgb(0,0,255)" text-anchor="middle" transform="rotate(0.000000 116.000000,215.000000)" >48</text> </g>
  Visible = false
  X = 0
  Y = 0
  arrowL1 = 3
  arrowL2 = 1
  arrowW = 2
  arrow_scheme = 0
  autoPlaceOffset = 2
  autoPlaceText = true
  click1_x = 139.5
  click1_y = 217
  click2_x = 139.5
  click2_y = 217
  comma_decimal_place = false
  dimension_line_overshoot = 1
  gap_datum_points = 2
  halfDimension_linear = false
  lineColor = rgb(0,0,255)
  strokeWidth = 0.5
  textFormat_linear = %(value)3.3f
  textRenderer_color = rgb(0,0,255)
  textRenderer_family = inherit
  textRenderer_size = 3.6
  unit_custom_scale = 1
  unit_scheme = 0
FEATURE [Drawing::FeatureViewPython] dim060  # drawing view (typed FeaturePython)
  Rotation = 0
  ViewResult = <g> \n  <line x1="188.000000" y1="188.560000" x2="188.000000" y2="218.000000" style="stroke:rgb(0,0,255);stroke-width:0.50" />\n<line x1="140.000000" y1="215.499609" x2="140.000000" y2="218.000000" style="stroke:rgb(0,0,255);stroke-width:0.50" />\n<line x1="188.000000" y1="217.000000" x2="140.000000" y2="217.000000" style="stroke:rgb(0,0,255);stroke-width:0.50" /> \n  <polygon points="140.000000,217.000000 143.000000,218.000000 144.000000,217.000000 143.000000,216.000000" style="fill:rgb(0,0,255);stroke:rgb(0,0,255);stroke-width:0" /><polygon points="188.000000,217.000000 185.000000,216.000000 184.000000,217.000000 185.000000,218.000000" style="fill:rgb(0,0,255);stroke:rgb(0,0,255);stroke-width:0" /> \n  <text x="164.000000" y="215.000000" font-family="inherit" font-size="3.6" fill="rgb(0,0,255)" text-anchor="middle" transform="rotate(0.000000 164.000000,215.000000)" >48</text> </g>
  Visible = false
  X = 0
  Y = 0
  arrowL1 = 3
  arrowL2 = 1
  arrowW = 2
  arrow_scheme = 0
  autoPlaceOffset = 2
  autoPlaceText = true
  click1_x = 145.5
  click1_y = 217
  click2_x = 145.5
  click2_y = 217
  comma_decimal_place = false
  dimension_line_overshoot = 1
  gap_datum_points = 2
  halfDimension_linear = false
  lineColor = rgb(0,0,255)
  strokeWidth = 0.5
  textFormat_linear = %(value)3.3f
  textRenderer_color = rgb(0,0,255)
  textRenderer_family = inherit
  textRenderer_size = 3.6
  unit_custom_scale = 1
  unit_scheme = 0
FEATURE [Drawing::FeatureViewPython] dim061  # drawing view (typed FeaturePython)
  Rotation = 0
  ViewResult = <g> \n  <line x1="190.000000" y1="186.560000" x2="221.000000" y2="186.560000" style="stroke:rgb(0,0,255);stroke-width:0.50" />\n<line x1="207.000000" y1="199.410000" x2="221.000000" y2="199.410000" style="stroke:rgb(0,0,255);stroke-width:0.50" />\n<line x1="220.000000" y1="186.560000" x2="220.000000" y2="199.410000" style="stroke:rgb(0,0,255);stroke-width:0.50" /> \n  <polygon points="220.000000,199.410000 221.000000,196.410000 220.000000,195.410000 219.000000,196.410000" style="fill:rgb(0,0,255);stroke:rgb(0,0,255);stroke-width:0" /><polygon points="220.000000,186.560000 219.000000,189.560000 220.000000,190.560000 221.000000,189.560000" style="fill:rgb(0,0,255);stroke:rgb(0,0,255);stroke-width:0" /> \n  <text x="218.000000" y="192.985000" font-family="inherit" font-size="3.6" fill="rgb(0,0,255)" text-anchor="middle" transform="rotate(-90.000000 218.000000,192.985000)" >12.85</text> </g>
  Visible = false
  X = 0
  Y = 0
  arrowL1 = 3
  arrowL2 = 1
  arrowW = 2
  arrow_scheme = 0
  autoPlaceOffset = 2
  autoPlaceText = true
  click1_x = 220
  click1_y = 195
  click2_x = 220
  click2_y = 195
  comma_decimal_place = false
  dimension_line_overshoot = 1
  gap_datum_points = 2
  halfDimension_linear = false
  lineColor = rgb(0,0,255)
  strokeWidth = 0.5
  textFormat_linear = %(value)3.3f
  textRenderer_color = rgb(0,0,255)
  textRenderer_family = inherit
  textRenderer_size = 3.6
  unit_custom_scale = 1
  unit_scheme = 0
FEATURE [Drawing::FeatureViewPython] dim062  # drawing view (typed FeaturePython)
  Rotation = 0
  ViewResult = <g> \n  <line x1="188.000000" y1="188.560000" x2="188.000000" y2="218.000000" style="stroke:rgb(0,0,255);stroke-width:0.50" />\n<line x1="210.000000" y1="196.420000" x2="210.000000" y2="218.000000" style="stroke:rgb(0,0,255);stroke-width:0.50" />\n<line x1="188.000000" y1="217.000000" x2="210.000000" y2="217.000000" style="stroke:rgb(0,0,255);stroke-width:0.50" /> \n  <polygon points="210.000000,217.000000 207.000000,216.000000 206.000000,217.000000 207.000000,218.000000" style="fill:rgb(0,0,255);stroke:rgb(0,0,255);stroke-width:0" /><polygon points="188.000000,217.000000 191.000000,218.000000 192.000000,217.000000 191.000000,216.000000" style="fill:rgb(0,0,255);stroke:rgb(0,0,255);stroke-width:0" /> \n  <text x="199.000000" y="215.000000" font-family="inherit" font-size="3.6" fill="rgb(0,0,255)" text-anchor="middle" transform="rotate(0.000000 199.000000,215.000000)" >22</text> </g>
  Visible = false
  X = 0
  Y = 0
  arrowL1 = 3
  arrowL2 = 1
  arrowW = 2
  arrow_scheme = 0
  autoPlaceOffset = 2
  autoPlaceText = true
  click1_x = 210
  click1_y = 217
  click2_x = 210
  click2_y = 217
  comma_decimal_place = false
  dimension_line_overshoot = 1
  gap_datum_points = 2
  halfDimension_linear = false
  lineColor = rgb(0,0,255)
  strokeWidth = 0.5
  textFormat_linear = %(value)3.3f
  textRenderer_color = rgb(0,0,255)
  textRenderer_family = inherit
  textRenderer_size = 3.6
  unit_custom_scale = 1
  unit_scheme = 0
FEATURE [Drawing::FeatureViewPython] dim063  # drawing view (typed FeaturePython)
  Rotation = 0
  ViewResult = <g> \n  <line x1="100.000000" y1="165.560000" x2="107.500000" y2="165.560000" style="stroke:rgb(0,0,255);stroke-width:0.50" />\n<line x1="94.000000" y1="186.560000" x2="107.500000" y2="186.560000" style="stroke:rgb(0,0,255);stroke-width:0.50" />\n<line x1="106.500000" y1="165.560000" x2="106.500000" y2="186.560000" style="stroke:rgb(0,0,255);stroke-width:0.50" /> \n  <polygon points="106.500000,186.560000 107.500000,183.560000 106.500000,182.560000 105.500000,183.560000" style="fill:rgb(0,0,255);stroke:rgb(0,0,255);stroke-width:0" /><polygon points="106.500000,165.560000 105.500000,168.560000 106.500000,169.560000 107.500000,168.560000" style="fill:rgb(0,0,255);stroke:rgb(0,0,255);stroke-width:0" /> \n  <text x="104.500000" y="176.060000" font-family="inherit" font-size="3.6" fill="rgb(0,0,255)" text-anchor="middle" transform="rotate(-90.000000 104.500000,176.060000)" >21</text> </g>
  Visible = false
  X = 0
  Y = 0
  arrowL1 = 3
  arrowL2 = 1
  arrowW = 2
  arrow_scheme = 0
  autoPlaceOffset = 2
  autoPlaceText = true
  click1_x = 106.5
  click1_y = 182
  click2_x = 106.5
  click2_y = 182
  comma_decimal_place = false
  dimension_line_overshoot = 1
  gap_datum_points = 2
  halfDimension_linear = false
  lineColor = rgb(0,0,255)
  strokeWidth = 0.5
  textFormat_linear = %(value)3.3f
  textRenderer_color = rgb(0,0,255)
  textRenderer_family = inherit
  textRenderer_size = 3.6
  unit_custom_scale = 1
  unit_scheme = 0
FEATURE [Drawing::FeatureViewPython] dim064  # drawing view (typed FeaturePython)
  Rotation = 0
  ViewResult = <g> \n  <line x1="100.000000" y1="165.560000" x2="107.500000" y2="165.560000" style="stroke:rgb(0,0,255);stroke-width:0.50" />\n<line x1="100.000000" y1="150.560000" x2="107.500000" y2="150.560000" style="stroke:rgb(0,0,255);stroke-width:0.50" />\n<line x1="106.500000" y1="165.560000" x2="106.500000" y2="150.560000" style="stroke:rgb(0,0,255);stroke-width:0.50" /> \n  <polygon points="106.500000,150.560000 105.500000,153.560000 106.500000,154.560000 107.500000,153.560000" style="fill:rgb(0,0,255);stroke:rgb(0,0,255);stroke-width:0" /><polygon points="106.500000,165.560000 107.500000,162.560000 106.500000,161.560000 105.500000,162.560000" style="fill:rgb(0,0,255);stroke:rgb(0,0,255);stroke-width:0" /> \n  <text x="104.500000" y="158.060000" font-family="inherit" font-size="3.6" fill="rgb(0,0,255)" text-anchor="middle" transform="rotate(-90.000000 104.500000,158.060000)" >15</text> </g>
  Visible = false
  X = 0
  Y = 0
  arrowL1 = 3
  arrowL2 = 1
  arrowW = 2
  arrow_scheme = 0
  autoPlaceOffset = 2
  autoPlaceText = true
  click1_x = 106.5
  click1_y = 151
  click2_x = 106.5
  click2_y = 151
  comma_decimal_place = false
  dimension_line_overshoot = 1
  gap_datum_points = 2
  halfDimension_linear = false
  lineColor = rgb(0,0,255)
  strokeWidth = 0.5
  textFormat_linear = %(value)3.3f
  textRenderer_color = rgb(0,0,255)
  textRenderer_family = inherit
  textRenderer_size = 3.6
  unit_custom_scale = 1
  unit_scheme = 0
FEATURE [Drawing::FeatureViewPython] dim065  # drawing view (typed FeaturePython)
  Rotation = 0
  ViewResult = <g> \n  <line x1="98.000000" y1="148.560000" x2="98.000000" y2="145.500000" style="stroke:rgb(0,0,255);stroke-width:0.50" />\n<line x1="126.000000" y1="148.560000" x2="126.000000" y2="145.500000" style="stroke:rgb(0,0,255);stroke-width:0.50" />\n<line x1="98.000000" y1="146.500000" x2="126.000000" y2="146.500000" style="stroke:rgb(0,0,255);stroke-width:0.50" /> \n  <polygon points="126.000000,146.500000 123.000000,145.500000 122.000000,146.500000 123.000000,147.500000" style="fill:rgb(0,0,255);stroke:rgb(0,0,255);stroke-width:0" /><polygon points="98.000000,146.500000 101.000000,147.500000 102.000000,146.500000 101.000000,145.500000" style="fill:rgb(0,0,255);stroke:rgb(0,0,255);stroke-width:0" /> \n  <text x="112.000000" y="144.500000" font-family="inherit" font-size="3.6" fill="rgb(0,0,255)" text-anchor="middle" transform="rotate(0.000000 112.000000,144.500000)" >28</text> </g>
  Visible = false
  X = 0
  Y = 0
  arrowL1 = 3
  arrowL2 = 1
  arrowW = 2
  arrow_scheme = 0
  autoPlaceOffset = 2
  autoPlaceText = true
  click1_x = 125
  click1_y = 146.5
  click2_x = 125
  click2_y = 146.5
  comma_decimal_place = false
  dimension_line_overshoot = 1
  gap_datum_points = 2
  halfDimension_linear = false
  lineColor = rgb(0,0,255)
  strokeWidth = 0.5
  textFormat_linear = %(value)3.3f
  textRenderer_color = rgb(0,0,255)
  textRenderer_family = inherit
  textRenderer_size = 3.6
  unit_custom_scale = 1
  unit_scheme = 0
FEATURE [Drawing::FeatureViewPython] dia014  # drawing view (typed FeaturePython)
  Rotation = 0
  ViewResult = <g>  <circle cx ="98.000000" cy ="165.560000" r="0.250000" stroke="none" fill="rgb(0,0,255)" /> \n<line x1="92.500000" y1="171.000000" x2="98.568779" y2="164.997426" style="stroke:rgb(0,0,255);stroke-width:0.50" />\n<polygon points="97.431221,166.122574 94.595080,167.521255 94.587324,168.935447 96.001516,168.943203" style="fill:rgb(0,0,255);stroke:rgb(0,0,255);stroke-width:0" />\n<polygon points="98.568779,164.997426 101.404920,163.598745 101.412676,162.184553 99.998484,162.176797" style="fill:rgb(0,0,255);stroke:rgb(0,0,255);stroke-width:0" />\n<line x1="92.500000" y1="171.000000" x2="80.000000" y2="171.000000" style="stroke:rgb(0,0,255);stroke-width:0.50" />\n<text x="86.250000" y="169.000000" font-family="inherit" font-size="3.6" fill="rgb(0,0,255)" text-anchor="middle" transform="rotate(0.000000 86.250000,169.000000)" >Ø1.6</text> </g>
  Visible = false
  X = 0
  Y = 0
  arrowL1 = 3
  arrowL2 = 1
  arrowW = 2
  arrow_scheme = 0
  autoPlaceOffset = 2
  autoPlaceText = true
  centerPointDia = 0.5
  click1_x = 92.5
  click1_y = 171
  click2_x = 80
  click2_y = 170
  click3_x = 80
  click3_y = 170
  comma_decimal_place = false
  lineColor = rgb(0,0,255)
  strokeWidth = 0.5
  textFormat_circular = Ø%(value)3.3f
  textRenderer_color = rgb(0,0,255)
  textRenderer_family = inherit
  textRenderer_size = 3.6
  unit_custom_scale = 1
  unit_scheme = 0
FEATURE [Drawing::FeatureViewPython] dim066  # drawing view (typed FeaturePython)
  Rotation = 0
  ViewResult = <g> \n  <line x1="126.000000" y1="167.560000" x2="126.000000" y2="208.500000" style="stroke:rgb(0,0,255);stroke-width:0.50" />\n<line x1="140.000000" y1="211.499609" x2="140.000000" y2="206.500000" style="stroke:rgb(0,0,255);stroke-width:0.50" />\n<line x1="126.000000" y1="207.500000" x2="140.000000" y2="207.500000" style="stroke:rgb(0,0,255);stroke-width:0.50" /> \n  <polygon points="140.000000,207.500000 137.000000,206.500000 136.000000,207.500000 137.000000,208.500000" style="fill:rgb(0,0,255);stroke:rgb(0,0,255);stroke-width:0" /><polygon points="126.000000,207.500000 129.000000,208.500000 130.000000,207.500000 129.000000,206.500000" style="fill:rgb(0,0,255);stroke:rgb(0,0,255);stroke-width:0" /> \n  <text x="133.000000" y="205.500000" font-family="inherit" font-size="3.6" fill="rgb(0,0,255)" text-anchor="middle" transform="rotate(0.000000 133.000000,205.500000)" >14</text> </g>
  Visible = false
  X = 0
  Y = 0
  arrowL1 = 3
  arrowL2 = 1
  arrowW = 2
  arrow_scheme = 0
  autoPlaceOffset = 2
  autoPlaceText = true
  click1_x = 128
  click1_y = 207.5
  click2_x = 128
  click2_y = 207.5
  comma_decimal_place = false
  dimension_line_overshoot = 1
  gap_datum_points = 2
  halfDimension_linear = false
  lineColor = rgb(0,0,255)
  strokeWidth = 0.5
  textFormat_linear = %(value)3.3f
  textRenderer_color = rgb(0,0,255)
  textRenderer_family = inherit
  textRenderer_size = 3.6
  unit_custom_scale = 1
  unit_scheme = 0
FEATURE [Drawing::FeatureViewPython] dim067  # drawing view (typed FeaturePython)
  Rotation = 0
  ViewResult = <g> \n  <line x1="154.000000" y1="166.760000" x2="154.000000" y2="208.500000" style="stroke:rgb(0,0,255);stroke-width:0.50" />\n<line x1="140.000000" y1="211.499609" x2="140.000000" y2="206.500000" style="stroke:rgb(0,0,255);stroke-width:0.50" />\n<line x1="154.000000" y1="207.500000" x2="140.000000" y2="207.500000" style="stroke:rgb(0,0,255);stroke-width:0.50" /> \n  <polygon points="140.000000,207.500000 143.000000,208.500000 144.000000,207.500000 143.000000,206.500000" style="fill:rgb(0,0,255);stroke:rgb(0,0,255);stroke-width:0" /><polygon points="154.000000,207.500000 151.000000,206.500000 150.000000,207.500000 151.000000,208.500000" style="fill:rgb(0,0,255);stroke:rgb(0,0,255);stroke-width:0" /> \n  <text x="147.000000" y="205.500000" font-family="inherit" font-size="3.6" fill="rgb(0,0,255)" text-anchor="middle" transform="rotate(0.000000 147.000000,205.500000)" >14</text> </g>
  Visible = false
  X = 0
  Y = 0
  arrowL1 = 3
  arrowL2 = 1
  arrowW = 2
  arrow_scheme = 0
  autoPlaceOffset = 2
  autoPlaceText = true
  click1_x = 145.5
  click1_y = 207.5
  click2_x = 145.5
  click2_y = 207.5
  comma_decimal_place = false
  dimension_line_overshoot = 1
  gap_datum_points = 2
  halfDimension_linear = false
  lineColor = rgb(0,0,255)
  strokeWidth = 0.5
  textFormat_linear = %(value)3.3f
  textRenderer_color = rgb(0,0,255)
  textRenderer_family = inherit
  textRenderer_size = 3.6
  unit_custom_scale = 1
  unit_scheme = 0
FEATURE [Drawing::FeatureViewPython] dim068  # drawing view (typed FeaturePython)
  Rotation = 0
  ViewResult = <g> \n  <line x1="154.000000" y1="147.760000" x2="154.000000" y2="145.000000" style="stroke:rgb(0,0,255);stroke-width:0.50" />\n<line x1="182.000000" y1="147.760000" x2="182.000000" y2="145.000000" style="stroke:rgb(0,0,255);stroke-width:0.50" />\n<line x1="154.000000" y1="146.000000" x2="182.000000" y2="146.000000" style="stroke:rgb(0,0,255);stroke-width:0.50" /> \n  <polygon points="182.000000,146.000000 179.000000,145.000000 178.000000,146.000000 179.000000,147.000000" style="fill:rgb(0,0,255);stroke:rgb(0,0,255);stroke-width:0" /><polygon points="154.000000,146.000000 157.000000,147.000000 158.000000,146.000000 157.000000,145.000000" style="fill:rgb(0,0,255);stroke:rgb(0,0,255);stroke-width:0" /> \n  <text x="168.000000" y="144.000000" font-family="inherit" font-size="3.6" fill="rgb(0,0,255)" text-anchor="middle" transform="rotate(0.000000 168.000000,144.000000)" >28</text> </g>
  Visible = false
  X = 0
  Y = 0
  arrowL1 = 3
  arrowL2 = 1
  arrowW = 2
  arrow_scheme = 0
  autoPlaceOffset = 2
  autoPlaceText = true
  click1_x = 182.5
  click1_y = 146
  click2_x = 182.5
  click2_y = 146
  comma_decimal_place = false
  dimension_line_overshoot = 1
  gap_datum_points = 2
  halfDimension_linear = false
  lineColor = rgb(0,0,255)
  strokeWidth = 0.5
  textFormat_linear = %(value)3.3f
  textRenderer_color = rgb(0,0,255)
  textRenderer_family = inherit
  textRenderer_size = 3.6
  unit_custom_scale = 1
  unit_scheme = 0
FEATURE [Drawing::FeatureViewPython] dim069  # drawing view (typed FeaturePython)
  Rotation = 0
  ViewResult = <g> \n  <line x1="180.000000" y1="149.760000" x2="175.000000" y2="149.760000" style="stroke:rgb(0,0,255);stroke-width:0.50" />\n<line x1="180.000000" y1="164.760000" x2="175.000000" y2="164.760000" style="stroke:rgb(0,0,255);stroke-width:0.50" />\n<line x1="176.000000" y1="149.760000" x2="176.000000" y2="164.760000" style="stroke:rgb(0,0,255);stroke-width:0.50" /> \n  <polygon points="176.000000,164.760000 177.000000,161.760000 176.000000,160.760000 175.000000,161.760000" style="fill:rgb(0,0,255);stroke:rgb(0,0,255);stroke-width:0" /><polygon points="176.000000,149.760000 175.000000,152.760000 176.000000,153.760000 177.000000,152.760000" style="fill:rgb(0,0,255);stroke:rgb(0,0,255);stroke-width:0" /> \n  <text x="174.000000" y="157.260000" font-family="inherit" font-size="3.6" fill="rgb(0,0,255)" text-anchor="middle" transform="rotate(-90.000000 174.000000,157.260000)" >15</text> </g>
  Visible = false
  X = 0
  Y = 0
  arrowL1 = 3
  arrowL2 = 1
  arrowW = 2
  arrow_scheme = 0
  autoPlaceOffset = 2
  autoPlaceText = true
  click1_x = 176
  click1_y = 164.5
  click2_x = 176
  click2_y = 164.5
  comma_decimal_place = false
  dimension_line_overshoot = 1
  gap_datum_points = 2
  halfDimension_linear = false
  lineColor = rgb(0,0,255)
  strokeWidth = 0.5
  textFormat_linear = %(value)3.3f
  textRenderer_color = rgb(0,0,255)
  textRenderer_family = inherit
  textRenderer_size = 3.6
  unit_custom_scale = 1
  unit_scheme = 0
FEATURE [Drawing::FeatureViewPython] dim070  # drawing view (typed FeaturePython)
  Rotation = 0
  ViewResult = <g> \n  <line x1="73.000000" y1="156.560000" x2="50.500000" y2="156.560000" style="stroke:rgb(0,0,255);stroke-width:0.50" />\n<line x1="73.000000" y1="199.410000" x2="50.500000" y2="199.410000" style="stroke:rgb(0,0,255);stroke-width:0.50" />\n<line x1="51.500000" y1="156.560000" x2="51.500000" y2="199.410000" style="stroke:rgb(0,0,255);stroke-width:0.50" /> \n  <polygon points="51.500000,199.410000 52.500000,196.410000 51.500000,195.410000 50.500000,196.410000" style="fill:rgb(0,0,255);stroke:rgb(0,0,255);stroke-width:0" /><polygon points="51.500000,156.560000 50.500000,159.560000 51.500000,160.560000 52.500000,159.560000" style="fill:rgb(0,0,255);stroke:rgb(0,0,255);stroke-width:0" /> \n  <text x="49.500000" y="177.985000" font-family="inherit" font-size="3.6" fill="rgb(0,0,255)" text-anchor="middle" transform="rotate(-90.000000 49.500000,177.985000)" >42.85</text> </g>
  Visible = false
  X = 0
  Y = 0
  arrowL1 = 3
  arrowL2 = 1
  arrowW = 2
  arrow_scheme = 0
  autoPlaceOffset = 2
  autoPlaceText = true
  click1_x = 51.5
  click1_y = 198
  click2_x = 51.5
  click2_y = 198
  comma_decimal_place = false
  dimension_line_overshoot = 1
  gap_datum_points = 2
  halfDimension_linear = false
  lineColor = rgb(0,0,255)
  strokeWidth = 0.5
  textFormat_linear = %(value)3.3f
  textRenderer_color = rgb(0,0,255)
  textRenderer_family = inherit
  textRenderer_size = 3.6
  unit_custom_scale = 1
  unit_scheme = 0
FEATURE [Drawing::FeatureViewPython] dim071  # drawing view (typed FeaturePython)
  Rotation = 0
  ViewResult = <g> \n  <line x1="207.000000" y1="156.560000" x2="229.000000" y2="156.560000" style="stroke:rgb(0,0,255);stroke-width:0.50" />\n<line x1="207.000000" y1="199.410000" x2="229.000000" y2="199.410000" style="stroke:rgb(0,0,255);stroke-width:0.50" />\n<line x1="228.000000" y1="156.560000" x2="228.000000" y2="199.410000" style="stroke:rgb(0,0,255);stroke-width:0.50" /> \n  <polygon points="228.000000,199.410000 229.000000,196.410000 228.000000,195.410000 227.000000,196.410000" style="fill:rgb(0,0,255);stroke:rgb(0,0,255);stroke-width:0" /><polygon points="228.000000,156.560000 227.000000,159.560000 228.000000,160.560000 229.000000,159.560000" style="fill:rgb(0,0,255);stroke:rgb(0,0,255);stroke-width:0" /> \n  <text x="226.000000" y="177.985000" font-family="inherit" font-size="3.6" fill="rgb(0,0,255)" text-anchor="middle" transform="rotate(-90.000000 226.000000,177.985000)" >42.85</text> </g>
  Visible = false
  X = 0
  Y = 0
  arrowL1 = 3
  arrowL2 = 1
  arrowW = 2
  arrow_scheme = 0
  autoPlaceOffset = 2
  autoPlaceText = true
  click1_x = 228
  click1_y = 202
  click2_x = 228
  click2_y = 202
  comma_decimal_place = false
  dimension_line_overshoot = 1
  gap_datum_points = 2
  halfDimension_linear = false
  lineColor = rgb(0,0,255)
  strokeWidth = 0.5
  textFormat_linear = %(value)3.3f
  textRenderer_color = rgb(0,0,255)
  textRenderer_family = inherit
  textRenderer_size = 3.6
  unit_custom_scale = 1
  unit_scheme = 0
FEATURE [Drawing::FeatureViewPython] dia015  # drawing view (typed FeaturePython)
  Rotation = 0
  ViewResult = <g>  <circle cx ="205.000000" cy ="156.560000" r="0.250000" stroke="none" fill="rgb(0,0,255)" /> \n<line x1="215.500000" y1="146.500000" x2="203.014296" y2="158.462493" style="stroke:rgb(0,0,255);stroke-width:0.50" />\n<polygon points="206.985704,154.657507 209.843742,153.304134 209.874000,151.890244 208.460110,151.859985" style="fill:rgb(0,0,255);stroke:rgb(0,0,255);stroke-width:0" />\n<polygon points="203.014296,158.462493 200.156258,159.815866 200.126000,161.229756 201.539890,161.260015" style="fill:rgb(0,0,255);stroke:rgb(0,0,255);stroke-width:0" />\n<line x1="215.500000" y1="146.500000" x2="231.500000" y2="146.500000" style="stroke:rgb(0,0,255);stroke-width:0.50" />\n<text x="223.500000" y="144.500000" font-family="inherit" font-size="3.6" fill="rgb(0,0,255)" text-anchor="middle" transform="rotate(0.000000 223.500000,144.500000)" >Ø5.5</text> </g>
  Visible = false
  X = 0
  Y = 0
  arrowL1 = 3
  arrowL2 = 1
  arrowW = 2
  arrow_scheme = 0
  autoPlaceOffset = 2
  autoPlaceText = true
  centerPointDia = 0.5
  click1_x = 215.5
  click1_y = 146.5
  click2_x = 231.5
  click2_y = 144
  click3_x = 231.5
  click3_y = 144
  comma_decimal_place = false
  lineColor = rgb(0,0,255)
  strokeWidth = 0.5
  textFormat_circular = Ø%(value)3.3f
  textRenderer_color = rgb(0,0,255)
  textRenderer_family = inherit
  textRenderer_size = 3.6
  unit_custom_scale = 1
  unit_scheme = 0
FEATURE [Drawing::FeatureViewPython] text048  # drawing view (typed FeaturePython)
  Rotation = 0
  ViewResult = <g> <text x="72.500000" y="162.500000" font-family="inherit" font-size="3,6" fill="rgb(0,0,255)" text-anchor="inherit" transform="rotate(0.000000 72.500000,162.500000)" >H2</text> </g>
  Visible = false
  X = 0
  Y = 0
  click1_x = 72.5
  click1_y = 162.5
  rotation = 0
  text = H2
  textRenderer_addText_color = rgb(0,0,255)
  textRenderer_addText_family = inherit
  textRenderer_addText_size = 3,6
FEATURE [Drawing::FeatureViewPython] text049  # drawing view (typed FeaturePython)
  Rotation = 0
  ViewResult = <g> <text x="221.000000" y="150.000000" font-family="inherit" font-size="3,6" fill="rgb(0,0,255)" text-anchor="inherit" transform="rotate(0.000000 221.000000,150.000000)" >H2</text> </g>
  Visible = false
  X = 0
  Y = 0
  click1_x = 221
  click1_y = 150
  rotation = 0
  text = H2
  textRenderer_addText_color = rgb(0,0,255)
  textRenderer_addText_family = inherit
  textRenderer_addText_size = 3,6
FEATURE [Drawing::FeatureViewPython] dim072  # drawing view (typed FeaturePython)
  Rotation = 0
  ViewResult = <g> \n  <line x1="75.000000" y1="154.560000" x2="75.000000" y2="139.500000" style="stroke:rgb(0,0,255);stroke-width:0.50" />\n<line x1="140.000000" y1="211.499609" x2="140.000000" y2="139.500000" style="stroke:rgb(0,0,255);stroke-width:0.50" />\n<line x1="75.000000" y1="140.500000" x2="140.000000" y2="140.500000" style="stroke:rgb(0,0,255);stroke-width:0.50" /> \n  <polygon points="140.000000,140.500000 137.000000,139.500000 136.000000,140.500000 137.000000,141.500000" style="fill:rgb(0,0,255);stroke:rgb(0,0,255);stroke-width:0" /><polygon points="75.000000,140.500000 78.000000,141.500000 79.000000,140.500000 78.000000,139.500000" style="fill:rgb(0,0,255);stroke:rgb(0,0,255);stroke-width:0" /> \n  <text x="107.500000" y="138.500000" font-family="inherit" font-size="3.6" fill="rgb(0,0,255)" text-anchor="middle" transform="rotate(0.000000 107.500000,138.500000)" >65</text> </g>
  Visible = false
  X = 0
  Y = 0
  arrowL1 = 3
  arrowL2 = 1
  arrowW = 2
  arrow_scheme = 0
  autoPlaceOffset = 2
  autoPlaceText = true
  click1_x = 138
  click1_y = 140.5
  click2_x = 138
  click2_y = 140.5
  comma_decimal_place = false
  dimension_line_overshoot = 1
  gap_datum_points = 2
  halfDimension_linear = false
  lineColor = rgb(0,0,255)
  strokeWidth = 0.5
  textFormat_linear = %(value)3.3f
  textRenderer_color = rgb(0,0,255)
  textRenderer_family = inherit
  textRenderer_size = 3.6
  unit_custom_scale = 1
  unit_scheme = 0
FEATURE [Drawing::FeatureViewPython] dim073  # drawing view (typed FeaturePython)
  Rotation = 0
  ViewResult = <g> \n  <line x1="140.000000" y1="211.499609" x2="140.000000" y2="139.500000" style="stroke:rgb(0,0,255);stroke-width:0.50" />\n<line x1="205.000000" y1="154.560000" x2="205.000000" y2="139.500000" style="stroke:rgb(0,0,255);stroke-width:0.50" />\n<line x1="140.000000" y1="140.500000" x2="205.000000" y2="140.500000" style="stroke:rgb(0,0,255);stroke-width:0.50" /> \n  <polygon points="205.000000,140.500000 202.000000,139.500000 201.000000,140.500000 202.000000,141.500000" style="fill:rgb(0,0,255);stroke:rgb(0,0,255);stroke-width:0" /><polygon points="140.000000,140.500000 143.000000,141.500000 144.000000,140.500000 143.000000,139.500000" style="fill:rgb(0,0,255);stroke:rgb(0,0,255);stroke-width:0" /> \n  <text x="172.500000" y="138.500000" font-family="inherit" font-size="3.6" fill="rgb(0,0,255)" text-anchor="middle" transform="rotate(0.000000 172.500000,138.500000)" >65</text> </g>
  Visible = false
  X = 0
  Y = 0
  arrowL1 = 3
  arrowL2 = 1
  arrowW = 2
  arrow_scheme = 0
  autoPlaceOffset = 2
  autoPlaceText = true
  click1_x = 202.5
  click1_y = 140.5
  click2_x = 202.5
  click2_y = 140.5
  comma_decimal_place = false
  dimension_line_overshoot = 1
  gap_datum_points = 2
  halfDimension_linear = false
  lineColor = rgb(0,0,255)
  strokeWidth = 0.5
  textFormat_linear = %(value)3.3f
  textRenderer_color = rgb(0,0,255)
  textRenderer_family = inherit
  textRenderer_size = 3.6
  unit_custom_scale = 1
  unit_scheme = 0
FEATURE [Drawing::FeatureViewPython] rad004  # drawing view (typed FeaturePython)
  Rotation = 0
  ViewResult = <g>  <circle cx ="168.000000" cy ="78.910000" r="0.250000" stroke="none" fill="rgb(0,0,255)" /> \n<line x1="187.500000" y1="74.000000" x2="168.000000" y2="78.910000" style="stroke:rgb(0,0,255);stroke-width:0.50" />\n<polygon points="182.545974,75.247398 179.392605,75.010187 178.667047,76.224092 179.880952,76.949650" style="fill:rgb(0,0,255);stroke:rgb(0,0,255);stroke-width:0" />\n<line x1="187.500000" y1="74.000000" x2="198.500000" y2="74.000000" style="stroke:rgb(0,0,255);stroke-width:0.50" />\n<text x="193.000000" y="72.000000" font-family="inherit" font-size="3.6" fill="rgb(0,0,255)" text-anchor="middle" transform="rotate(0.000000 193.000000,72.000000)" >R15</text> </g>
  Visible = false
  X = 0
  Y = 0
  arrowL1 = 3
  arrowL2 = 1
  arrowW = 2
  arrow_scheme = 0
  autoPlaceOffset = 2
  autoPlaceText = true
  centerPointDia = 0.5
  click1_x = 187.5
  click1_y = 74
  click2_x = 198.5
  click2_y = 74.5
  click3_x = 198.5
  click3_y = 74.5
  comma_decimal_place = false
  lineColor = rgb(0,0,255)
  strokeWidth = 0.5
  textFormat_radial = R%(value)3.3f
  textRenderer_color = rgb(0,0,255)
  textRenderer_family = inherit
  textRenderer_size = 3.6
  unit_custom_scale = 1
  unit_scheme = 0
FEATURE [Drawing::FeatureViewPython] rad005  # drawing view (typed FeaturePython)
  Rotation = 0
  ViewResult = <g>  <circle cx ="112.000000" cy ="78.910000" r="0.250000" stroke="none" fill="rgb(0,0,255)" /> \n<line x1="93.000000" y1="74.500000" x2="112.000000" y2="78.910000" style="stroke:rgb(0,0,255);stroke-width:0.50" />\n<polygon points="97.388421,75.518576 100.084642,77.170966 101.284842,76.422955 100.536832,75.222755" style="fill:rgb(0,0,255);stroke:rgb(0,0,255);stroke-width:0" />\n<line x1="93.000000" y1="74.500000" x2="82.500000" y2="74.500000" style="stroke:rgb(0,0,255);stroke-width:0.50" />\n<text x="87.750000" y="72.500000" font-family="inherit" font-size="3.6" fill="rgb(0,0,255)" text-anchor="middle" transform="rotate(0.000000 87.750000,72.500000)" >R15</text> </g>
  Visible = false
  X = 0
  Y = 0
  arrowL1 = 3
  arrowL2 = 1
  arrowW = 2
  arrow_scheme = 0
  autoPlaceOffset = 2
  autoPlaceText = true
  centerPointDia = 0.5
  click1_x = 93
  click1_y = 74.5
  click2_x = 82.5
  click2_y = 72.5
  click3_x = 82.5
  click3_y = 72.5
  comma_decimal_place = false
  lineColor = rgb(0,0,255)
  strokeWidth = 0.5
  textFormat_radial = R%(value)3.3f
  textRenderer_color = rgb(0,0,255)
  textRenderer_family = inherit
  textRenderer_size = 3.6
  unit_custom_scale = 1
  unit_scheme = 0
FEATURE [Drawing::FeatureViewPython] text050  # drawing view (typed FeaturePython)
  Rotation = 0
  ViewResult = <g> <text x="93.500000" y="57.000000" font-family="inherit" font-size="3,6" fill="rgb(0,0,255)" text-anchor="inherit" transform="rotate(0.000000 93.500000,57.000000)" >H3</text> </g>
  Visible = false
  X = 0
  Y = 0
  click1_x = 93.5
  click1_y = 57
  rotation = 0
  text = H3
  textRenderer_addText_color = rgb(0,0,255)
  textRenderer_addText_family = inherit
  textRenderer_addText_size = 3,6
FEATURE [Drawing::FeatureViewPython] text051  # drawing view (typed FeaturePython)
  Rotation = 0
  ViewResult = <g> <text x="100.500000" y="57.000000" font-family="inherit" font-size="3,6" fill="rgb(0,0,255)" text-anchor="inherit" transform="rotate(0.000000 100.500000,57.000000)" >H3</text> </g>
  Visible = false
  X = 0
  Y = 0
  click1_x = 100.5
  click1_y = 57
  rotation = 0
  text = H3
  textRenderer_addText_color = rgb(0,0,255)
  textRenderer_addText_family = inherit
  textRenderer_addText_size = 3,6
FEATURE [Drawing::FeatureViewPython] text052  # drawing view (typed FeaturePython)
  Rotation = 0
  ViewResult = <g> <text x="121.500000" y="57.000000" font-family="inherit" font-size="3,6" fill="rgb(0,0,255)" text-anchor="inherit" transform="rotate(0.000000 121.500000,57.000000)" >H3</text> </g>
  Visible = false
  X = 0
  Y = 0
  click1_x = 121.5
  click1_y = 57
  rotation = 0
  text = H3
  textRenderer_addText_color = rgb(0,0,255)
  textRenderer_addText_family = inherit
  textRenderer_addText_size = 3,6
FEATURE [Drawing::FeatureViewPython] text053  # drawing view (typed FeaturePython)
  Rotation = 0
  ViewResult = <g> <text x="128.500000" y="57.000000" font-family="inherit" font-size="3,6" fill="rgb(0,0,255)" text-anchor="inherit" transform="rotate(0.000000 128.500000,57.000000)" >H3</text> </g>
  Visible = false
  X = 0
  Y = 0
  click1_x = 128.5
  click1_y = 57
  rotation = 0
  text = H3
  textRenderer_addText_color = rgb(0,0,255)
  textRenderer_addText_family = inherit
  textRenderer_addText_size = 3,6
FEATURE [Drawing::FeatureViewPython] text054  # drawing view (typed FeaturePython)
  Rotation = 0
  ViewResult = <g> <text x="149.500000" y="57.000000" font-family="inherit" font-size="3,6" fill="rgb(0,0,255)" text-anchor="inherit" transform="rotate(0.000000 149.500000,57.000000)" >H3</text> </g>
  Visible = false
  X = 0
  Y = 0
  click1_x = 149.5
  click1_y = 57
  rotation = 0
  text = H3
  textRenderer_addText_color = rgb(0,0,255)
  textRenderer_addText_family = inherit
  textRenderer_addText_size = 3,6
FEATURE [Drawing::FeatureViewPython] text055  # drawing view (typed FeaturePython)
  Rotation = 0
  ViewResult = <g> <text x="156.500000" y="57.000000" font-family="inherit" font-size="3,6" fill="rgb(0,0,255)" text-anchor="inherit" transform="rotate(0.000000 156.500000,57.000000)" >H3</text> </g>
  Visible = false
  X = 0
  Y = 0
  click1_x = 156.5
  click1_y = 57
  rotation = 0
  text = H3
  textRenderer_addText_color = rgb(0,0,255)
  textRenderer_addText_family = inherit
  textRenderer_addText_size = 3,6
FEATURE [Drawing::FeatureViewPython] text057  # drawing view (typed FeaturePython)
  Rotation = 0
  ViewResult = <g> <text x="185.000000" y="57.000000" font-family="inherit" font-size="3,6" fill="rgb(0,0,255)" text-anchor="inherit" transform="rotate(0.000000 185.000000,57.000000)" >H3</text> </g>
  Visible = false
  X = 0
  Y = 0
  click1_x = 185
  click1_y = 57
  rotation = 0
  text = H3
  textRenderer_addText_color = rgb(0,0,255)
  textRenderer_addText_family = inherit
  textRenderer_addText_size = 3,6
FEATURE [Drawing::FeatureViewPython] text056  # drawing view (typed FeaturePython)
  Rotation = 0
  ViewResult = <g> <text x="177.500000" y="57.000000" font-family="inherit" font-size="3,6" fill="rgb(0,0,255)" text-anchor="inherit" transform="rotate(0.000000 177.500000,57.000000)" >H3</text> </g>
  Visible = false
  X = 0
  Y = 0
  click1_x = 177.5
  click1_y = 57
  rotation = 0
  text = H3
  textRenderer_addText_color = rgb(0,0,255)
  textRenderer_addText_family = inherit
  textRenderer_addText_size = 3,6
FEATURE [Drawing::FeatureViewPython] centerLines007  # drawing view (typed FeaturePython)
  Rotation = 0
  ViewResult = <g transform="scale(1.000000,1.000000)" stroke="rgb(0,0,255)"  stroke-width="0.320000" > <path d="M 140.000000,49.410000 L 140.000000,46.410000 M 140.000000,44.410000 L 140.000000,39.500000 "/>\n<path d="M 140.000000,49.410000 L 140.000000,46.410000 M 140.000000,44.410000 L 140.000000,39.500000 "/> </g> 
  Visible = false
  X = 0
  Y = 0
  centerLine_color = rgb(0,0,255)
  centerLine_len_dash = 6
  centerLine_len_dot = 3
  centerLine_len_gap = 2
  centerLine_width = 0.32
  click1_x = 139.5
  click1_y = 39.5
  click2_x = 139.5
  click2_y = 39.5
FEATURE [Drawing::FeatureViewPython] dim074  # drawing view (typed FeaturePython)
  Rotation = 0
  ViewResult = <g> \n  <line x1="94.620000" y1="51.010000" x2="94.620000" y2="45.500000" style="stroke:rgb(0,0,255);stroke-width:0.50" />\n<line x1="101.380000" y1="51.010000" x2="101.380000" y2="45.500000" style="stroke:rgb(0,0,255);stroke-width:0.50" />\n<line x1="94.620000" y1="46.500000" x2="101.380000" y2="46.500000" style="stroke:rgb(0,0,255);stroke-width:0.50" /> \n  <polygon points="101.380000,46.500000 104.380000,47.500000 105.380000,46.500000 104.380000,45.500000" style="fill:rgb(0,0,255);stroke:rgb(0,0,255);stroke-width:0" /><polygon points="94.620000,46.500000 91.620000,45.500000 90.620000,46.500000 91.620000,47.500000" style="fill:rgb(0,0,255);stroke:rgb(0,0,255);stroke-width:0" /> \n  <text x="98.000000" y="44.500000" font-family="inherit" font-size="3.6" fill="rgb(0,0,255)" text-anchor="middle" transform="rotate(0.000000 98.000000,44.500000)" >6.76</text> </g>
  Visible = false
  X = 0
  Y = 0
  arrowL1 = 3
  arrowL2 = 1
  arrowW = 2
  arrow_scheme = 0
  autoPlaceOffset = 2
  autoPlaceText = true
  click1_x = 102
  click1_y = 46.5
  click2_x = 102
  click2_y = 46.5
  comma_decimal_place = false
  dimension_line_overshoot = 1
  gap_datum_points = 2
  halfDimension_linear = false
  lineColor = rgb(0,0,255)
  strokeWidth = 0.5
  textFormat_linear = %(value)3.3f
  textRenderer_color = rgb(0,0,255)
  textRenderer_family = inherit
  textRenderer_size = 3.6
  unit_custom_scale = 1
  unit_scheme = 0
FEATURE [Drawing::FeatureViewPython] dim075  # drawing view (typed FeaturePython)
  Rotation = 0
  ViewResult = <g> \n  <line x1="101.380000" y1="51.010000" x2="101.380000" y2="45.500000" style="stroke:rgb(0,0,255);stroke-width:0.50" />\n<line x1="122.620000" y1="51.010000" x2="122.620000" y2="45.500000" style="stroke:rgb(0,0,255);stroke-width:0.50" />\n<line x1="101.380000" y1="46.500000" x2="122.620000" y2="46.500000" style="stroke:rgb(0,0,255);stroke-width:0.50" /> \n  <polygon points="122.620000,46.500000 119.620000,45.500000 118.620000,46.500000 119.620000,47.500000" style="fill:rgb(0,0,255);stroke:rgb(0,0,255);stroke-width:0" /><polygon points="101.380000,46.500000 104.380000,47.500000 105.380000,46.500000 104.380000,45.500000" style="fill:rgb(0,0,255);stroke:rgb(0,0,255);stroke-width:0" /> \n  <text x="112.000000" y="44.500000" font-family="inherit" font-size="3.6" fill="rgb(0,0,255)" text-anchor="middle" transform="rotate(0.000000 112.000000,44.500000)" >21.24</text> </g>
  Visible = false
  X = 0
  Y = 0
  arrowL1 = 3
  arrowL2 = 1
  arrowW = 2
  arrow_scheme = 0
  autoPlaceOffset = 2
  autoPlaceText = true
  click1_x = 121
  click1_y = 46.5
  click2_x = 121
  click2_y = 46.5
  comma_decimal_place = false
  dimension_line_overshoot = 1
  gap_datum_points = 2
  halfDimension_linear = false
  lineColor = rgb(0,0,255)
  strokeWidth = 0.5
  textFormat_linear = %(value)3.3f
  textRenderer_color = rgb(0,0,255)
  textRenderer_family = inherit
  textRenderer_size = 3.6
  unit_custom_scale = 1
  unit_scheme = 0
FEATURE [Drawing::FeatureViewPython] dim076  # drawing view (typed FeaturePython)
  Rotation = 0
  ViewResult = <g> \n  <line x1="122.620000" y1="51.010000" x2="122.620000" y2="45.500000" style="stroke:rgb(0,0,255);stroke-width:0.50" />\n<line x1="129.380000" y1="51.010000" x2="129.380000" y2="45.500000" style="stroke:rgb(0,0,255);stroke-width:0.50" />\n<line x1="122.620000" y1="46.500000" x2="129.380000" y2="46.500000" style="stroke:rgb(0,0,255);stroke-width:0.50" /> \n  <polygon points="129.380000,46.500000 132.380000,47.500000 133.380000,46.500000 132.380000,45.500000" style="fill:rgb(0,0,255);stroke:rgb(0,0,255);stroke-width:0" /><polygon points="122.620000,46.500000 119.620000,45.500000 118.620000,46.500000 119.620000,47.500000" style="fill:rgb(0,0,255);stroke:rgb(0,0,255);stroke-width:0" /> \n  <text x="126.000000" y="44.500000" font-family="inherit" font-size="3.6" fill="rgb(0,0,255)" text-anchor="middle" transform="rotate(0.000000 126.000000,44.500000)" >6.76</text> </g>
  Visible = false
  X = 0
  Y = 0
  arrowL1 = 3
  arrowL2 = 1
  arrowW = 2
  arrow_scheme = 0
  autoPlaceOffset = 2
  autoPlaceText = true
  click1_x = 129
  click1_y = 46.5
  click2_x = 129
  click2_y = 46.5
  comma_decimal_place = false
  dimension_line_overshoot = 1
  gap_datum_points = 2
  halfDimension_linear = false
  lineColor = rgb(0,0,255)
  strokeWidth = 0.5
  textFormat_linear = %(value)3.3f
  textRenderer_color = rgb(0,0,255)
  textRenderer_family = inherit
  textRenderer_size = 3.6
  unit_custom_scale = 1
  unit_scheme = 0
FEATURE [Drawing::FeatureViewPython] dim077  # drawing view (typed FeaturePython)
  Rotation = 0
  ViewResult = <g> \n  <line x1="129.380000" y1="51.010000" x2="129.380000" y2="45.500000" style="stroke:rgb(0,0,255);stroke-width:0.50" />\n<line x1="140.000000" y1="41.500000" x2="140.000000" y2="47.500000" style="stroke:rgb(0,0,255);stroke-width:0.50" />\n<line x1="129.380000" y1="46.500000" x2="140.000000" y2="46.500000" style="stroke:rgb(0,0,255);stroke-width:0.50" /> \n  <polygon points="140.000000,46.500000 137.000000,45.500000 136.000000,46.500000 137.000000,47.500000" style="fill:rgb(0,0,255);stroke:rgb(0,0,255);stroke-width:0" /><polygon points="129.380000,46.500000 132.380000,47.500000 133.380000,46.500000 132.380000,45.500000" style="fill:rgb(0,0,255);stroke:rgb(0,0,255);stroke-width:0" /> \n  <text x="134.690000" y="44.500000" font-family="inherit" font-size="3.6" fill="rgb(0,0,255)" text-anchor="middle" transform="rotate(0.000000 134.690000,44.500000)" >10.62</text> </g>
  Visible = false
  X = 0
  Y = 0
  arrowL1 = 3
  arrowL2 = 1
  arrowW = 2
  arrow_scheme = 0
  autoPlaceOffset = 2
  autoPlaceText = true
  click1_x = 139
  click1_y = 46.5
  click2_x = 139
  click2_y = 46.5
  comma_decimal_place = false
  dimension_line_overshoot = 1
  gap_datum_points = 2
  halfDimension_linear = false
  lineColor = rgb(0,0,255)
  strokeWidth = 0.5
  textFormat_linear = %(value)3.3f
  textRenderer_color = rgb(0,0,255)
  textRenderer_family = inherit
  textRenderer_size = 3.6
  unit_custom_scale = 1
  unit_scheme = 0
FEATURE [Drawing::FeatureViewPython] dim078  # drawing view (typed FeaturePython)
  Rotation = 0
  ViewResult = <g> \n  <line x1="150.620000" y1="50.210000" x2="150.620000" y2="45.500000" style="stroke:rgb(0,0,255);stroke-width:0.50" />\n<line x1="157.380000" y1="50.210000" x2="157.380000" y2="45.500000" style="stroke:rgb(0,0,255);stroke-width:0.50" />\n<line x1="150.620000" y1="46.500000" x2="157.380000" y2="46.500000" style="stroke:rgb(0,0,255);stroke-width:0.50" /> \n  <polygon points="157.380000,46.500000 160.380000,47.500000 161.380000,46.500000 160.380000,45.500000" style="fill:rgb(0,0,255);stroke:rgb(0,0,255);stroke-width:0" /><polygon points="150.620000,46.500000 147.620000,45.500000 146.620000,46.500000 147.620000,47.500000" style="fill:rgb(0,0,255);stroke:rgb(0,0,255);stroke-width:0" /> \n  <text x="154.000000" y="44.500000" font-family="inherit" font-size="3.6" fill="rgb(0,0,255)" text-anchor="middle" transform="rotate(0.000000 154.000000,44.500000)" >6.76</text> </g>
  Visible = false
  X = 0
  Y = 0
  arrowL1 = 3
  arrowL2 = 1
  arrowW = 2
  arrow_scheme = 0
  autoPlaceOffset = 2
  autoPlaceText = true
  click1_x = 157
  click1_y = 46.5
  click2_x = 157
  click2_y = 46.5
  comma_decimal_place = false
  dimension_line_overshoot = 1
  gap_datum_points = 2
  halfDimension_linear = false
  lineColor = rgb(0,0,255)
  strokeWidth = 0.5
  textFormat_linear = %(value)3.3f
  textRenderer_color = rgb(0,0,255)
  textRenderer_family = inherit
  textRenderer_size = 3.6
  unit_custom_scale = 1
  unit_scheme = 0
FEATURE [Drawing::FeatureViewPython] dim079  # drawing view (typed FeaturePython)
  Rotation = 0
  ViewResult = <g> \n  <line x1="157.380000" y1="50.210000" x2="157.380000" y2="45.500000" style="stroke:rgb(0,0,255);stroke-width:0.50" />\n<line x1="178.620000" y1="50.210000" x2="178.620000" y2="45.500000" style="stroke:rgb(0,0,255);stroke-width:0.50" />\n<line x1="157.380000" y1="46.500000" x2="178.620000" y2="46.500000" style="stroke:rgb(0,0,255);stroke-width:0.50" /> \n  <polygon points="178.620000,46.500000 175.620000,45.500000 174.620000,46.500000 175.620000,47.500000" style="fill:rgb(0,0,255);stroke:rgb(0,0,255);stroke-width:0" /><polygon points="157.380000,46.500000 160.380000,47.500000 161.380000,46.500000 160.380000,45.500000" style="fill:rgb(0,0,255);stroke:rgb(0,0,255);stroke-width:0" /> \n  <text x="168.000000" y="44.500000" font-family="inherit" font-size="3.6" fill="rgb(0,0,255)" text-anchor="middle" transform="rotate(0.000000 168.000000,44.500000)" >21.24</text> </g>
  Visible = false
  X = 0
  Y = 0
  arrowL1 = 3
  arrowL2 = 1
  arrowW = 2
  arrow_scheme = 0
  autoPlaceOffset = 2
  autoPlaceText = true
  click1_x = 177
  click1_y = 46.5
  click2_x = 177
  click2_y = 46.5
  comma_decimal_place = false
  dimension_line_overshoot = 1
  gap_datum_points = 2
  halfDimension_linear = false
  lineColor = rgb(0,0,255)
  strokeWidth = 0.5
  textFormat_linear = %(value)3.3f
  textRenderer_color = rgb(0,0,255)
  textRenderer_family = inherit
  textRenderer_size = 3.6
  unit_custom_scale = 1
  unit_scheme = 0
FEATURE [Drawing::FeatureViewPython] dim080  # drawing view (typed FeaturePython)
  Rotation = 0
  ViewResult = <g> \n  <line x1="178.620000" y1="50.210000" x2="178.620000" y2="45.500000" style="stroke:rgb(0,0,255);stroke-width:0.50" />\n<line x1="185.380000" y1="50.210000" x2="185.380000" y2="45.500000" style="stroke:rgb(0,0,255);stroke-width:0.50" />\n<line x1="178.620000" y1="46.500000" x2="185.380000" y2="46.500000" style="stroke:rgb(0,0,255);stroke-width:0.50" /> \n  <polygon points="185.380000,46.500000 188.380000,47.500000 189.380000,46.500000 188.380000,45.500000" style="fill:rgb(0,0,255);stroke:rgb(0,0,255);stroke-width:0" /><polygon points="178.620000,46.500000 175.620000,45.500000 174.620000,46.500000 175.620000,47.500000" style="fill:rgb(0,0,255);stroke:rgb(0,0,255);stroke-width:0" /> \n  <text x="182.000000" y="44.500000" font-family="inherit" font-size="3.6" fill="rgb(0,0,255)" text-anchor="middle" transform="rotate(0.000000 182.000000,44.500000)" >6.76</text> </g>
  Visible = false
  X = 0
  Y = 0
  arrowL1 = 3
  arrowL2 = 1
  arrowW = 2
  arrow_scheme = 0
  autoPlaceOffset = 2
  autoPlaceText = true
  click1_x = 185.5
  click1_y = 46.5
  click2_x = 185.5
  click2_y = 46.5
  comma_decimal_place = false
  dimension_line_overshoot = 1
  gap_datum_points = 2
  halfDimension_linear = false
  lineColor = rgb(0,0,255)
  strokeWidth = 0.5
  textFormat_linear = %(value)3.3f
  textRenderer_color = rgb(0,0,255)
  textRenderer_family = inherit
  textRenderer_size = 3.6
  unit_custom_scale = 1
  unit_scheme = 0
FEATURE [Drawing::FeatureViewPython] dim081  # drawing view (typed FeaturePython)
  Rotation = 0
  ViewResult = <g> \n  <line x1="150.620000" y1="50.210000" x2="150.620000" y2="45.500000" style="stroke:rgb(0,0,255);stroke-width:0.50" />\n<line x1="140.000000" y1="41.500000" x2="140.000000" y2="47.500000" style="stroke:rgb(0,0,255);stroke-width:0.50" />\n<line x1="150.620000" y1="46.500000" x2="140.000000" y2="46.500000" style="stroke:rgb(0,0,255);stroke-width:0.50" /> \n  <polygon points="140.000000,46.500000 143.000000,47.500000 144.000000,46.500000 143.000000,45.500000" style="fill:rgb(0,0,255);stroke:rgb(0,0,255);stroke-width:0" /><polygon points="150.620000,46.500000 147.620000,45.500000 146.620000,46.500000 147.620000,47.500000" style="fill:rgb(0,0,255);stroke:rgb(0,0,255);stroke-width:0" /> \n  <text x="145.310000" y="44.500000" font-family="inherit" font-size="3.6" fill="rgb(0,0,255)" text-anchor="middle" transform="rotate(0.000000 145.310000,44.500000)" >10.62</text> </g>
  Visible = false
  X = 0
  Y = 0
  arrowL1 = 3
  arrowL2 = 1
  arrowW = 2
  arrow_scheme = 0
  autoPlaceOffset = 2
  autoPlaceText = true
  click1_x = 141
  click1_y = 46.5
  click2_x = 141
  click2_y = 46.5
  comma_decimal_place = false
  dimension_line_overshoot = 1
  gap_datum_points = 2
  halfDimension_linear = false
  lineColor = rgb(0,0,255)
  strokeWidth = 0.5
  textFormat_linear = %(value)3.3f
  textRenderer_color = rgb(0,0,255)
  textRenderer_family = inherit
  textRenderer_size = 3.6
  unit_custom_scale = 1
  unit_scheme = 0
FEATURE [Drawing::FeatureViewPython] dim082  # drawing view (typed FeaturePython)
  Rotation = 0
  ViewResult = <g> \n  <line x1="187.380000" y1="53.010000" x2="215.000000" y2="53.010000" style="stroke:rgb(0,0,255);stroke-width:0.50" />\n<line x1="207.000000" y1="49.410000" x2="215.000000" y2="49.410000" style="stroke:rgb(0,0,255);stroke-width:0.50" />\n<line x1="214.000000" y1="53.010000" x2="214.000000" y2="49.410000" style="stroke:rgb(0,0,255);stroke-width:0.50" /> \n  <polygon points="214.000000,49.410000 215.000000,46.410000 214.000000,45.410000 213.000000,46.410000" style="fill:rgb(0,0,255);stroke:rgb(0,0,255);stroke-width:0" /><polygon points="214.000000,53.010000 213.000000,56.010000 214.000000,57.010000 215.000000,56.010000" style="fill:rgb(0,0,255);stroke:rgb(0,0,255);stroke-width:0" /> \n  <text x="218.500000" y="54.000000" font-family="inherit" font-size="3.6" fill="rgb(0,0,255)" text-anchor="inherit" transform="rotate(-90.000000 218.500000,54.000000)" >3.6</text> </g>
  Visible = false
  X = 0
  Y = 0
  arrowL1 = 3
  arrowL2 = 1
  arrowW = 2
  arrow_scheme = 0
  autoPlaceOffset = 2
  autoPlaceText = false
  click1_x = 214
  click1_y = 50.5
  click2_x = 218.5
  click2_y = 54
  comma_decimal_place = false
  dimension_line_overshoot = 1
  gap_datum_points = 2
  halfDimension_linear = false
  lineColor = rgb(0,0,255)
  strokeWidth = 0.5
  textFormat_linear = %(value)3.3f
  textRenderer_color = rgb(0,0,255)
  textRenderer_family = inherit
  textRenderer_size = 3.6
  unit_custom_scale = 1
  unit_scheme = 0
FEATURE [Drawing::FeatureViewPython] dia016  # drawing view (typed FeaturePython)
  Rotation = 0
  ViewResult = <g>  <circle cx ="96.500000" cy ="94.410000" r="0.250000" stroke="none" fill="rgb(0,0,255)" /> \n<line x1="89.500000" y1="88.500000" x2="97.760748" y2="95.474432" style="stroke:rgb(0,0,255);stroke-width:0.50" />\n<polygon points="95.239252,93.345568 93.592093,90.646149 92.182893,90.765128 92.301873,92.174328" style="fill:rgb(0,0,255);stroke:rgb(0,0,255);stroke-width:0" />\n<polygon points="97.760748,95.474432 99.407907,98.173851 100.817107,98.054872 100.698127,96.645672" style="fill:rgb(0,0,255);stroke:rgb(0,0,255);stroke-width:0" />\n<line x1="89.500000" y1="88.500000" x2="78.000000" y2="88.500000" style="stroke:rgb(0,0,255);stroke-width:0.50" />\n<text x="83.750000" y="86.500000" font-family="inherit" font-size="3.6" fill="rgb(0,0,255)" text-anchor="middle" transform="rotate(0.000000 83.750000,86.500000)" >Ø3.3</text> </g>
  Visible = false
  X = 0
  Y = 0
  arrowL1 = 3
  arrowL2 = 1
  arrowW = 2
  arrow_scheme = 0
  autoPlaceOffset = 2
  autoPlaceText = true
  centerPointDia = 0.5
  click1_x = 89.5
  click1_y = 88.5
  click2_x = 78
  click2_y = 87
  click3_x = 78
  click3_y = 87
  comma_decimal_place = false
  lineColor = rgb(0,0,255)
  strokeWidth = 0.5
  textFormat_circular = Ø%(value)3.3f
  textRenderer_color = rgb(0,0,255)
  textRenderer_family = inherit
  textRenderer_size = 3.6
  unit_custom_scale = 1
  unit_scheme = 0
FEATURE [Drawing::FeatureViewPython] text058  # drawing view (typed FeaturePython)
  Rotation = 0
  ViewResult = <g> <text x="82.000000" y="92.000000" font-family="inherit" font-size="3,6" fill="rgb(0,0,255)" text-anchor="inherit" transform="rotate(0.000000 82.000000,92.000000)" >H4</text> </g>
  Visible = false
  X = 0
  Y = 0
  click1_x = 82
  click1_y = 92
  rotation = 0
  text = H4
  textRenderer_addText_color = rgb(0,0,255)
  textRenderer_addText_family = inherit
  textRenderer_addText_size = 3,6
FEATURE [Drawing::FeatureViewPython] text059  # drawing view (typed FeaturePython)
  Rotation = 0
  ViewResult = <g> <text x="132.500000" y="95.500000" font-family="inherit" font-size="3,6" fill="rgb(0,0,255)" text-anchor="inherit" transform="rotate(0.000000 132.500000,95.500000)" >H4</text> </g>
  Visible = false
  X = 0
  Y = 0
  click1_x = 132.5
  click1_y = 95.5
  rotation = 0
  text = H4
  textRenderer_addText_color = rgb(0,0,255)
  textRenderer_addText_family = inherit
  textRenderer_addText_size = 3,6
FEATURE [Drawing::FeatureViewPython] text060  # drawing view (typed FeaturePython)
  Rotation = 0
  ViewResult = <g> <text x="132.500000" y="64.000000" font-family="inherit" font-size="3,6" fill="rgb(0,0,255)" text-anchor="inherit" transform="rotate(0.000000 132.500000,64.000000)" >H4</text> </g>
  Visible = false
  X = 0
  Y = 0
  click1_x = 132.5
  click1_y = 64
  rotation = 0
  text = H4
  textRenderer_addText_color = rgb(0,0,255)
  textRenderer_addText_family = inherit
  textRenderer_addText_size = 3,6
FEATURE [Drawing::FeatureViewPython] text061  # drawing view (typed FeaturePython)
  Rotation = 0
  ViewResult = <g> <text x="143.500000" y="64.000000" font-family="inherit" font-size="3,6" fill="rgb(0,0,255)" text-anchor="inherit" transform="rotate(0.000000 143.500000,64.000000)" >H4</text> </g>
  Visible = false
  X = 0
  Y = 0
  click1_x = 143.5
  click1_y = 64
  rotation = 0
  text = H4
  textRenderer_addText_color = rgb(0,0,255)
  textRenderer_addText_family = inherit
  textRenderer_addText_size = 3,6
FEATURE [Drawing::FeatureViewPython] text062  # drawing view (typed FeaturePython)
  Rotation = 0
  ViewResult = <g> <text x="144.000000" y="95.500000" font-family="inherit" font-size="3,6" fill="rgb(0,0,255)" text-anchor="inherit" transform="rotate(0.000000 144.000000,95.500000)" >H4</text> </g>
  Visible = false
  X = 0
  Y = 0
  click1_x = 144
  click1_y = 95.5
  rotation = 0
  text = H4
  textRenderer_addText_color = rgb(0,0,255)
  textRenderer_addText_family = inherit
  textRenderer_addText_size = 3,6
FEATURE [Drawing::FeatureViewPython] text063  # drawing view (typed FeaturePython)
  Rotation = 0
  ViewResult = <g> <text x="188.000000" y="64.000000" font-family="inherit" font-size="3,6" fill="rgb(0,0,255)" text-anchor="inherit" transform="rotate(0.000000 188.000000,64.000000)" >H4</text> </g>
  Visible = false
  X = 0
  Y = 0
  click1_x = 188
  click1_y = 64
  rotation = 0
  text = H4
  textRenderer_addText_color = rgb(0,0,255)
  textRenderer_addText_family = inherit
  textRenderer_addText_size = 3,6
FEATURE [Drawing::FeatureViewPython] text064  # drawing view (typed FeaturePython)
  Rotation = 0
  ViewResult = <g> <text x="188.000000" y="95.500000" font-family="inherit" font-size="3,6" fill="rgb(0,0,255)" text-anchor="inherit" transform="rotate(0.000000 188.000000,95.500000)" >H4</text> </g>
  Visible = false
  X = 0
  Y = 0
  click1_x = 188
  click1_y = 95.5
  rotation = 0
  text = H4
  textRenderer_addText_color = rgb(0,0,255)
  textRenderer_addText_family = inherit
  textRenderer_addText_size = 3,6
FEATURE [Drawing::FeatureViewPython] dim083  # drawing view (typed FeaturePython)
  Rotation = 0
  ViewResult = <g> \n  <line x1="96.500000" y1="96.410000" x2="96.500000" y2="103.000000" style="stroke:rgb(0,0,255);stroke-width:0.50" />\n<line x1="127.500000" y1="96.410000" x2="127.500000" y2="103.000000" style="stroke:rgb(0,0,255);stroke-width:0.50" />\n<line x1="96.500000" y1="102.000000" x2="127.500000" y2="102.000000" style="stroke:rgb(0,0,255);stroke-width:0.50" /> \n  <polygon points="127.500000,102.000000 124.500000,101.000000 123.500000,102.000000 124.500000,103.000000" style="fill:rgb(0,0,255);stroke:rgb(0,0,255);stroke-width:0" /><polygon points="96.500000,102.000000 99.500000,103.000000 100.500000,102.000000 99.500000,101.000000" style="fill:rgb(0,0,255);stroke:rgb(0,0,255);stroke-width:0" /> \n  <text x="112.000000" y="100.000000" font-family="inherit" font-size="3.6" fill="rgb(0,0,255)" text-anchor="middle" transform="rotate(0.000000 112.000000,100.000000)" >31</text> </g>
  Visible = false
  X = 0
  Y = 0
  arrowL1 = 3
  arrowL2 = 1
  arrowW = 2
  arrow_scheme = 0
  autoPlaceOffset = 2
  autoPlaceText = true
  click1_x = 129
  click1_y = 102
  click2_x = 129
  click2_y = 102
  comma_decimal_place = false
  dimension_line_overshoot = 1
  gap_datum_points = 2
  halfDimension_linear = false
  lineColor = rgb(0,0,255)
  strokeWidth = 0.5
  textFormat_linear = %(value)3.3f
  textRenderer_color = rgb(0,0,255)
  textRenderer_family = inherit
  textRenderer_size = 3.6
  unit_custom_scale = 1
  unit_scheme = 0
FEATURE [Drawing::FeatureViewPython] dim084  # drawing view (typed FeaturePython)
  Rotation = 0
  ViewResult = <g> \n  <line x1="125.500000" y1="94.410000" x2="121.000000" y2="94.410000" style="stroke:rgb(0,0,255);stroke-width:0.50" />\n<line x1="125.500000" y1="63.410000" x2="121.000000" y2="63.410000" style="stroke:rgb(0,0,255);stroke-width:0.50" />\n<line x1="122.000000" y1="94.410000" x2="122.000000" y2="63.410000" style="stroke:rgb(0,0,255);stroke-width:0.50" /> \n  <polygon points="122.000000,63.410000 121.000000,66.410000 122.000000,67.410000 123.000000,66.410000" style="fill:rgb(0,0,255);stroke:rgb(0,0,255);stroke-width:0" /><polygon points="122.000000,94.410000 123.000000,91.410000 122.000000,90.410000 121.000000,91.410000" style="fill:rgb(0,0,255);stroke:rgb(0,0,255);stroke-width:0" /> \n  <text x="120.000000" y="78.910000" font-family="inherit" font-size="3.6" fill="rgb(0,0,255)" text-anchor="middle" transform="rotate(-90.000000 120.000000,78.910000)" >31</text> </g>
  Visible = false
  X = 0
  Y = 0
  arrowL1 = 3
  arrowL2 = 1
  arrowW = 2
  arrow_scheme = 0
  autoPlaceOffset = 2
  autoPlaceText = true
  click1_x = 122
  click1_y = 79
  click2_x = 122
  click2_y = 79
  comma_decimal_place = false
  dimension_line_overshoot = 1
  gap_datum_points = 2
  halfDimension_linear = false
  lineColor = rgb(0,0,255)
  strokeWidth = 0.5
  textFormat_linear = %(value)3.3f
  textRenderer_color = rgb(0,0,255)
  textRenderer_family = inherit
  textRenderer_size = 3.6
  unit_custom_scale = 1
  unit_scheme = 0
FEATURE [Drawing::FeatureViewPython] dim085  # drawing view (typed FeaturePython)
  Rotation = 0
  ViewResult = <g> \n  <line x1="154.500000" y1="94.410000" x2="160.000000" y2="94.410000" style="stroke:rgb(0,0,255);stroke-width:0.50" />\n<line x1="154.500000" y1="63.410000" x2="160.000000" y2="63.410000" style="stroke:rgb(0,0,255);stroke-width:0.50" />\n<line x1="159.000000" y1="94.410000" x2="159.000000" y2="63.410000" style="stroke:rgb(0,0,255);stroke-width:0.50" /> \n  <polygon points="159.000000,63.410000 158.000000,66.410000 159.000000,67.410000 160.000000,66.410000" style="fill:rgb(0,0,255);stroke:rgb(0,0,255);stroke-width:0" /><polygon points="159.000000,94.410000 160.000000,91.410000 159.000000,90.410000 158.000000,91.410000" style="fill:rgb(0,0,255);stroke:rgb(0,0,255);stroke-width:0" /> \n  <text x="157.000000" y="78.910000" font-family="inherit" font-size="3.6" fill="rgb(0,0,255)" text-anchor="middle" transform="rotate(-90.000000 157.000000,78.910000)" >31</text> </g>
  Visible = false
  X = 0
  Y = 0
  arrowL1 = 3
  arrowL2 = 1
  arrowW = 2
  arrow_scheme = 0
  autoPlaceOffset = 2
  autoPlaceText = true
  click1_x = 159
  click1_y = 64
  click2_x = 159
  click2_y = 64
  comma_decimal_place = false
  dimension_line_overshoot = 1
  gap_datum_points = 2
  halfDimension_linear = false
  lineColor = rgb(0,0,255)
  strokeWidth = 0.5
  textFormat_linear = %(value)3.3f
  textRenderer_color = rgb(0,0,255)
  textRenderer_family = inherit
  textRenderer_size = 3.6
  unit_custom_scale = 1
  unit_scheme = 0
FEATURE [Drawing::FeatureViewPython] dim086  # drawing view (typed FeaturePython)
  Rotation = 0
  ViewResult = <g> \n  <line x1="152.500000" y1="96.410000" x2="152.500000" y2="103.000000" style="stroke:rgb(0,0,255);stroke-width:0.50" />\n<line x1="183.500000" y1="96.410000" x2="183.500000" y2="103.000000" style="stroke:rgb(0,0,255);stroke-width:0.50" />\n<line x1="152.500000" y1="102.000000" x2="183.500000" y2="102.000000" style="stroke:rgb(0,0,255);stroke-width:0.50" /> \n  <polygon points="183.500000,102.000000 180.500000,101.000000 179.500000,102.000000 180.500000,103.000000" style="fill:rgb(0,0,255);stroke:rgb(0,0,255);stroke-width:0" /><polygon points="152.500000,102.000000 155.500000,103.000000 156.500000,102.000000 155.500000,101.000000" style="fill:rgb(0,0,255);stroke:rgb(0,0,255);stroke-width:0" /> \n  <text x="168.000000" y="100.000000" font-family="inherit" font-size="3.6" fill="rgb(0,0,255)" text-anchor="middle" transform="rotate(0.000000 168.000000,100.000000)" >31</text> </g>
  Visible = false
  X = 0
  Y = 0
  arrowL1 = 3
  arrowL2 = 1
  arrowW = 2
  arrow_scheme = 0
  autoPlaceOffset = 2
  autoPlaceText = true
  click1_x = 183.5
  click1_y = 102
  click2_x = 183.5
  click2_y = 102
  comma_decimal_place = false
  dimension_line_overshoot = 1
  gap_datum_points = 2
  halfDimension_linear = false
  lineColor = rgb(0,0,255)
  strokeWidth = 0.5
  textFormat_linear = %(value)3.3f
  textRenderer_color = rgb(0,0,255)
  textRenderer_family = inherit
  textRenderer_size = 3.6
  unit_custom_scale = 1
  unit_scheme = 0
FEATURE [Drawing::FeatureViewPython] dim087  # drawing view (typed FeaturePython)
  Rotation = 0
  ViewResult = <g> \n  <line x1="140.000000" y1="41.500000" x2="140.000000" y2="72.500000" style="stroke:rgb(0,0,255);stroke-width:0.50" />\n<line x1="152.500000" y1="65.410000" x2="152.500000" y2="72.500000" style="stroke:rgb(0,0,255);stroke-width:0.50" />\n<line x1="140.000000" y1="71.500000" x2="152.500000" y2="71.500000" style="stroke:rgb(0,0,255);stroke-width:0.50" /> \n  <polygon points="152.500000,71.500000 149.500000,70.500000 148.500000,71.500000 149.500000,72.500000" style="fill:rgb(0,0,255);stroke:rgb(0,0,255);stroke-width:0" /><polygon points="140.000000,71.500000 143.000000,72.500000 144.000000,71.500000 143.000000,70.500000" style="fill:rgb(0,0,255);stroke:rgb(0,0,255);stroke-width:0" /> \n  <text x="146.250000" y="69.500000" font-family="inherit" font-size="3.6" fill="rgb(0,0,255)" text-anchor="middle" transform="rotate(0.000000 146.250000,69.500000)" >12.5</text> </g>
  Visible = false
  X = 0
  Y = 0
  arrowL1 = 3
  arrowL2 = 1
  arrowW = 2
  arrow_scheme = 0
  autoPlaceOffset = 2
  autoPlaceText = true
  click1_x = 143
  click1_y = 71.5
  click2_x = 143
  click2_y = 71.5
  comma_decimal_place = false
  dimension_line_overshoot = 1
  gap_datum_points = 2
  halfDimension_linear = false
  lineColor = rgb(0,0,255)
  strokeWidth = 0.5
  textFormat_linear = %(value)3.3f
  textRenderer_color = rgb(0,0,255)
  textRenderer_family = inherit
  textRenderer_size = 3.6
  unit_custom_scale = 1
  unit_scheme = 0
FEATURE [Drawing::FeatureViewPython] dim088  # drawing view (typed FeaturePython)
  Rotation = 0
  ViewResult = <g> \n  <line x1="127.500000" y1="65.410000" x2="127.500000" y2="72.500000" style="stroke:rgb(0,0,255);stroke-width:0.50" />\n<line x1="140.000000" y1="41.500000" x2="140.000000" y2="72.500000" style="stroke:rgb(0,0,255);stroke-width:0.50" />\n<line x1="127.500000" y1="71.500000" x2="140.000000" y2="71.500000" style="stroke:rgb(0,0,255);stroke-width:0.50" /> \n  <polygon points="140.000000,71.500000 137.000000,70.500000 136.000000,71.500000 137.000000,72.500000" style="fill:rgb(0,0,255);stroke:rgb(0,0,255);stroke-width:0" /><polygon points="127.500000,71.500000 130.500000,72.500000 131.500000,71.500000 130.500000,70.500000" style="fill:rgb(0,0,255);stroke:rgb(0,0,255);stroke-width:0" /> \n  <text x="133.750000" y="69.500000" font-family="inherit" font-size="3.6" fill="rgb(0,0,255)" text-anchor="middle" transform="rotate(0.000000 133.750000,69.500000)" >12.5</text> </g>
  Visible = false
  X = 0
  Y = 0
  arrowL1 = 3
  arrowL2 = 1
  arrowW = 2
  arrow_scheme = 0
  autoPlaceOffset = 2
  autoPlaceText = true
  click1_x = 138
  click1_y = 71.5
  click2_x = 138
  click2_y = 71.5
  comma_decimal_place = false
  dimension_line_overshoot = 1
  gap_datum_points = 2
  halfDimension_linear = false
  lineColor = rgb(0,0,255)
  strokeWidth = 0.5
  textFormat_linear = %(value)3.3f
  textRenderer_color = rgb(0,0,255)
  textRenderer_family = inherit
  textRenderer_size = 3.6
  unit_custom_scale = 1
  unit_scheme = 0
FEATURE [Drawing::FeatureViewPython] dim090  # drawing view (typed FeaturePython)
  Rotation = 0
  ViewResult = <g> \n  <line x1="181.500000" y1="63.410000" x2="173.500000" y2="63.410000" style="stroke:rgb(0,0,255);stroke-width:0.50" />\n<line x1="203.000000" y1="49.410000" x2="173.500000" y2="49.410000" style="stroke:rgb(0,0,255);stroke-width:0.50" />\n<line x1="174.500000" y1="63.410000" x2="174.500000" y2="49.410000" style="stroke:rgb(0,0,255);stroke-width:0.50" /> \n  <polygon points="174.500000,49.410000 173.500000,52.410000 174.500000,53.410000 175.500000,52.410000" style="fill:rgb(0,0,255);stroke:rgb(0,0,255);stroke-width:0" /><polygon points="174.500000,63.410000 175.500000,60.410000 174.500000,59.410000 173.500000,60.410000" style="fill:rgb(0,0,255);stroke:rgb(0,0,255);stroke-width:0" /> \n  <text x="172.500000" y="56.410000" font-family="inherit" font-size="3.6" fill="rgb(0,0,255)" text-anchor="middle" transform="rotate(-90.000000 172.500000,56.410000)" >14</text> </g>
  Visible = false
  X = 0
  Y = 0
  arrowL1 = 3
  arrowL2 = 1
  arrowW = 2
  arrow_scheme = 0
  autoPlaceOffset = 2
  autoPlaceText = true
  click1_x = 174.5
  click1_y = 59.5
  click2_x = 174.5
  click2_y = 59.5
  comma_decimal_place = false
  dimension_line_overshoot = 1
  gap_datum_points = 2
  halfDimension_linear = false
  lineColor = rgb(0,0,255)
  strokeWidth = 0.5
  textFormat_linear = %(value)3.3f
  textRenderer_color = rgb(0,0,255)
  textRenderer_family = inherit
  textRenderer_size = 3.6
  unit_custom_scale = 1
  unit_scheme = 0
FEATURE [Drawing::FeatureViewPython] text065  # drawing view (typed FeaturePython)
  Rotation = 0
  ViewResult = <g> <text x="101.000000" y="64.000000" font-family="inherit" font-size="3,6" fill="rgb(0,0,255)" text-anchor="inherit" transform="rotate(0.000000 101.000000,64.000000)" >H4</text> </g>
  Visible = false
  X = 0
  Y = 0
  click1_x = 101
  click1_y = 64
  rotation = 0
  text = H4
  textRenderer_addText_color = rgb(0,0,255)
  textRenderer_addText_family = inherit
  textRenderer_addText_size = 3,6
FEATURE [Drawing::FeatureViewPython] dim089  # drawing view (typed FeaturePython)
  Rotation = 0
  ViewResult = <g> \n  <line x1="112.000000" y1="80.910000" x2="112.000000" y2="86.500000" style="stroke:rgb(0,0,255);stroke-width:0.50" />\n<line x1="140.000000" y1="41.500000" x2="140.000000" y2="86.500000" style="stroke:rgb(0,0,255);stroke-width:0.50" />\n<line x1="112.000000" y1="85.500000" x2="140.000000" y2="85.500000" style="stroke:rgb(0,0,255);stroke-width:0.50" /> \n  <polygon points="140.000000,85.500000 137.000000,84.500000 136.000000,85.500000 137.000000,86.500000" style="fill:rgb(0,0,255);stroke:rgb(0,0,255);stroke-width:0" /><polygon points="112.000000,85.500000 115.000000,86.500000 116.000000,85.500000 115.000000,84.500000" style="fill:rgb(0,0,255);stroke:rgb(0,0,255);stroke-width:0" /> \n  <text x="130.000000" y="84.000000" font-family="inherit" font-size="3.6" fill="rgb(0,0,255)" text-anchor="inherit" transform="rotate(0.000000 130.000000,84.000000)" >28</text> </g>
  Visible = false
  X = 0
  Y = 0
  arrowL1 = 3
  arrowL2 = 1
  arrowW = 2
  arrow_scheme = 0
  autoPlaceOffset = 2
  autoPlaceText = false
  click1_x = 132
  click1_y = 85.5
  click2_x = 130
  click2_y = 84
  comma_decimal_place = false
  dimension_line_overshoot = 1
  gap_datum_points = 2
  halfDimension_linear = false
  lineColor = rgb(0,0,255)
  strokeWidth = 0.5
  textFormat_linear = %(value)3.3f
  textRenderer_color = rgb(0,0,255)
  textRenderer_family = inherit
  textRenderer_size = 3.6
  unit_custom_scale = 1
  unit_scheme = 0
FEATURE [Drawing::FeatureViewPython] dim091  # drawing view (typed FeaturePython)
  Rotation = 0
  ViewResult = <g> \n  <line x1="168.000000" y1="80.910000" x2="168.000000" y2="86.500000" style="stroke:rgb(0,0,255);stroke-width:0.50" />\n<line x1="140.000000" y1="41.500000" x2="140.000000" y2="86.500000" style="stroke:rgb(0,0,255);stroke-width:0.50" />\n<line x1="168.000000" y1="85.500000" x2="140.000000" y2="85.500000" style="stroke:rgb(0,0,255);stroke-width:0.50" /> \n  <polygon points="140.000000,85.500000 143.000000,86.500000 144.000000,85.500000 143.000000,84.500000" style="fill:rgb(0,0,255);stroke:rgb(0,0,255);stroke-width:0" /><polygon points="168.000000,85.500000 165.000000,84.500000 164.000000,85.500000 165.000000,86.500000" style="fill:rgb(0,0,255);stroke:rgb(0,0,255);stroke-width:0" /> \n  <text x="144.500000" y="83.500000" font-family="inherit" font-size="3.6" fill="rgb(0,0,255)" text-anchor="inherit" transform="rotate(0.000000 144.500000,83.500000)" >28</text> </g>
  Visible = false
  X = 0
  Y = 0
  arrowL1 = 3
  arrowL2 = 1
  arrowW = 2
  arrow_scheme = 0
  autoPlaceOffset = 2
  autoPlaceText = false
  click1_x = 142.5
  click1_y = 85.5
  click2_x = 144.5
  click2_y = 83.5
  comma_decimal_place = false
  dimension_line_overshoot = 1
  gap_datum_points = 2
  halfDimension_linear = false
  lineColor = rgb(0,0,255)
  strokeWidth = 0.5
  textFormat_linear = %(value)3.3f
  textRenderer_color = rgb(0,0,255)
  textRenderer_family = inherit
  textRenderer_size = 3.6
  unit_custom_scale = 1
  unit_scheme = 0
FEATURE [Drawing::FeatureViewPython] dim092  # drawing view (typed FeaturePython)
  Rotation = 0
  ViewResult = <g> \n  <line x1="112.000000" y1="76.910000" x2="112.000000" y2="58.000000" style="stroke:rgb(0,0,255);stroke-width:0.50" />\n<line x1="127.500000" y1="61.410000" x2="127.500000" y2="58.000000" style="stroke:rgb(0,0,255);stroke-width:0.50" />\n<line x1="112.000000" y1="59.000000" x2="127.500000" y2="59.000000" style="stroke:rgb(0,0,255);stroke-width:0.50" /> \n  <polygon points="127.500000,59.000000 124.500000,58.000000 123.500000,59.000000 124.500000,60.000000" style="fill:rgb(0,0,255);stroke:rgb(0,0,255);stroke-width:0" /><polygon points="112.000000,59.000000 115.000000,60.000000 116.000000,59.000000 115.000000,58.000000" style="fill:rgb(0,0,255);stroke:rgb(0,0,255);stroke-width:0" /> \n  <text x="116.000000" y="62.000000" font-family="inherit" font-size="3.6" fill="rgb(0,0,255)" text-anchor="inherit" transform="rotate(0.000000 116.000000,62.000000)" >15.5</text> </g>
  Visible = false
  X = 0
  Y = 0
  arrowL1 = 3
  arrowL2 = 1
  arrowW = 2
  arrow_scheme = 0
  autoPlaceOffset = 2
  autoPlaceText = false
  click1_x = 112
  click1_y = 59
  click2_x = 116
  click2_y = 62
  comma_decimal_place = false
  dimension_line_overshoot = 1
  gap_datum_points = 2
  halfDimension_linear = false
  lineColor = rgb(0,0,255)
  strokeWidth = 0.5
  textFormat_linear = %(value)3.3f
  textRenderer_color = rgb(0,0,255)
  textRenderer_family = inherit
  textRenderer_size = 3.6
  unit_custom_scale = 1
  unit_scheme = 0
FEATURE [Drawing::FeatureViewPython] dim093  # drawing view (typed FeaturePython)
  Rotation = 0
  ViewResult = <g> \n  <line x1="168.000000" y1="76.910000" x2="168.000000" y2="58.000000" style="stroke:rgb(0,0,255);stroke-width:0.50" />\n<line x1="152.500000" y1="61.410000" x2="152.500000" y2="58.000000" style="stroke:rgb(0,0,255);stroke-width:0.50" />\n<line x1="168.000000" y1="59.000000" x2="152.500000" y2="59.000000" style="stroke:rgb(0,0,255);stroke-width:0.50" /> \n  <polygon points="152.500000,59.000000 155.500000,60.000000 156.500000,59.000000 155.500000,58.000000" style="fill:rgb(0,0,255);stroke:rgb(0,0,255);stroke-width:0" /><polygon points="168.000000,59.000000 165.000000,58.000000 164.000000,59.000000 165.000000,60.000000" style="fill:rgb(0,0,255);stroke:rgb(0,0,255);stroke-width:0" /> \n  <text x="160.000000" y="63.000000" font-family="inherit" font-size="3.6" fill="rgb(0,0,255)" text-anchor="inherit" transform="rotate(0.000000 160.000000,63.000000)" >15.5</text> </g>
  Visible = false
  X = 0
  Y = 0
  arrowL1 = 3
  arrowL2 = 1
  arrowW = 2
  arrow_scheme = 0
  autoPlaceOffset = 2
  autoPlaceText = false
  click1_x = 166
  click1_y = 59
  click2_x = 160
  click2_y = 63
  comma_decimal_place = false
  dimension_line_overshoot = 1
  gap_datum_points = 2
  halfDimension_linear = false
  lineColor = rgb(0,0,255)
  strokeWidth = 0.5
  textFormat_linear = %(value)3.3f
  textRenderer_color = rgb(0,0,255)
  textRenderer_family = inherit
  textRenderer_size = 3.6
  unit_custom_scale = 1
  unit_scheme = 0
FEATURE [Drawing::FeatureViewPython] dia017  # drawing view (typed FeaturePython)
  Rotation = 0
  ViewResult = <g>  <circle cx ="96.500000" cy ="63.410000" r="0.250000" stroke="none" fill="rgb(0,0,255)" /> \n<line x1="90.000000" y1="59.500000" x2="97.913903" y2="64.260517" style="stroke:rgb(0,0,255);stroke-width:0.50" />\n<polygon points="95.086097,62.559483 93.030830,60.156178 91.658454,60.497624 91.999900,61.870000" style="fill:rgb(0,0,255);stroke:rgb(0,0,255);stroke-width:0" />\n<polygon points="97.913903,64.260517 99.969170,66.663822 101.341546,66.322376 101.000100,64.950000" style="fill:rgb(0,0,255);stroke:rgb(0,0,255);stroke-width:0" />\n<line x1="90.000000" y1="59.500000" x2="78.000000" y2="59.500000" style="stroke:rgb(0,0,255);stroke-width:0.50" />\n<text x="84.000000" y="57.500000" font-family="inherit" font-size="3.6" fill="rgb(0,0,255)" text-anchor="middle" transform="rotate(0.000000 84.000000,57.500000)" >Ø3.3</text> </g>
  Visible = false
  X = 0
  Y = 0
  arrowL1 = 3
  arrowL2 = 1
  arrowW = 2
  arrow_scheme = 0
  autoPlaceOffset = 2
  autoPlaceText = true
  centerPointDia = 0.5
  click1_x = 90
  click1_y = 59.5
  click2_x = 78
  click2_y = 58
  click3_x = 78
  click3_y = 58
  comma_decimal_place = false
  lineColor = rgb(0,0,255)
  strokeWidth = 0.5
  textFormat_circular = Ø%(value)3.3f
  textRenderer_color = rgb(0,0,255)
  textRenderer_family = inherit
  textRenderer_size = 3.6
  unit_custom_scale = 1
  unit_scheme = 0
FEATURE [Drawing::FeatureViewPython] dim094  # drawing view (typed FeaturePython)
  Rotation = 0
  ViewResult = <g> \n  <line x1="112.000000" y1="124.560000" x2="112.000000" y2="114.000000" style="stroke:rgb(0,0,255);stroke-width:0.50" />\n<line x1="140.000000" y1="211.499609" x2="140.000000" y2="114.000000" style="stroke:rgb(0,0,255);stroke-width:0.50" />\n<line x1="112.000000" y1="115.000000" x2="140.000000" y2="115.000000" style="stroke:rgb(0,0,255);stroke-width:0.50" /> \n  <polygon points="140.000000,115.000000 137.000000,114.000000 136.000000,115.000000 137.000000,116.000000" style="fill:rgb(0,0,255);stroke:rgb(0,0,255);stroke-width:0" /><polygon points="112.000000,115.000000 115.000000,116.000000 116.000000,115.000000 115.000000,114.000000" style="fill:rgb(0,0,255);stroke:rgb(0,0,255);stroke-width:0" /> \n  <text x="126.000000" y="113.000000" font-family="inherit" font-size="3.6" fill="rgb(0,0,255)" text-anchor="middle" transform="rotate(0.000000 126.000000,113.000000)" >28</text> </g>
  Visible = false
  X = 0
  Y = 0
  arrowL1 = 3
  arrowL2 = 1
  arrowW = 2
  arrow_scheme = 0
  autoPlaceOffset = 2
  autoPlaceText = true
  click1_x = 139
  click1_y = 115
  click2_x = 139
  click2_y = 115
  comma_decimal_place = false
  dimension_line_overshoot = 1
  gap_datum_points = 2
  halfDimension_linear = false
  lineColor = rgb(0,0,255)
  strokeWidth = 0.5
  textFormat_linear = %(value)3.3f
  textRenderer_color = rgb(0,0,255)
  textRenderer_family = inherit
  textRenderer_size = 3.6
  unit_custom_scale = 1
  unit_scheme = 0
FEATURE [Drawing::FeatureViewPython] dim095  # drawing view (typed FeaturePython)
  Rotation = 0
  ViewResult = <g> \n  <line x1="168.000000" y1="124.560000" x2="168.000000" y2="114.000000" style="stroke:rgb(0,0,255);stroke-width:0.50" />\n<line x1="140.000000" y1="211.499609" x2="140.000000" y2="114.000000" style="stroke:rgb(0,0,255);stroke-width:0.50" />\n<line x1="168.000000" y1="115.000000" x2="140.000000" y2="115.000000" style="stroke:rgb(0,0,255);stroke-width:0.50" /> \n  <polygon points="140.000000,115.000000 143.000000,116.000000 144.000000,115.000000 143.000000,114.000000" style="fill:rgb(0,0,255);stroke:rgb(0,0,255);stroke-width:0" /><polygon points="168.000000,115.000000 165.000000,114.000000 164.000000,115.000000 165.000000,116.000000" style="fill:rgb(0,0,255);stroke:rgb(0,0,255);stroke-width:0" /> \n  <text x="154.000000" y="113.000000" font-family="inherit" font-size="3.6" fill="rgb(0,0,255)" text-anchor="middle" transform="rotate(0.000000 154.000000,113.000000)" >28</text> </g>
  Visible = false
  X = 0
  Y = 0
  arrowL1 = 3
  arrowL2 = 1
  arrowW = 2
  arrow_scheme = 0
  autoPlaceOffset = 2
  autoPlaceText = true
  click1_x = 151
  click1_y = 115
  click2_x = 151
  click2_y = 115
  comma_decimal_place = false
  dimension_line_overshoot = 1
  gap_datum_points = 2
  halfDimension_linear = false
  lineColor = rgb(0,0,255)
  strokeWidth = 0.5
  textFormat_linear = %(value)3.3f
  textRenderer_color = rgb(0,0,255)
  textRenderer_family = inherit
  textRenderer_size = 3.6
  unit_custom_scale = 1
  unit_scheme = 0
FEATURE [Drawing::FeatureViewPython] dim096  # drawing view (typed FeaturePython)
  Rotation = 0
  ViewResult = <g> \n  <line x1="110.000000" y1="126.560000" x2="50.500000" y2="126.560000" style="stroke:rgb(0,0,255);stroke-width:0.50" />\n<line x1="73.000000" y1="49.410000" x2="50.500000" y2="49.410000" style="stroke:rgb(0,0,255);stroke-width:0.50" />\n<line x1="51.500000" y1="126.560000" x2="51.500000" y2="49.410000" style="stroke:rgb(0,0,255);stroke-width:0.50" /> \n  <polygon points="51.500000,49.410000 50.500000,52.410000 51.500000,53.410000 52.500000,52.410000" style="fill:rgb(0,0,255);stroke:rgb(0,0,255);stroke-width:0" /><polygon points="51.500000,126.560000 52.500000,123.560000 51.500000,122.560000 50.500000,123.560000" style="fill:rgb(0,0,255);stroke:rgb(0,0,255);stroke-width:0" /> \n  <text x="49.500000" y="87.985000" font-family="inherit" font-size="3.6" fill="rgb(0,0,255)" text-anchor="middle" transform="rotate(-90.000000 49.500000,87.985000)" >77.15</text> </g>
  Visible = false
  X = 0
  Y = 0
  arrowL1 = 3
  arrowL2 = 1
  arrowW = 2
  arrow_scheme = 0
  autoPlaceOffset = 2
  autoPlaceText = true
  click1_x = 51.5
  click1_y = 55
  click2_x = 51.5
  click2_y = 55
  comma_decimal_place = false
  dimension_line_overshoot = 1
  gap_datum_points = 2
  halfDimension_linear = false
  lineColor = rgb(0,0,255)
  strokeWidth = 0.5
  textFormat_linear = %(value)3.3f
  textRenderer_color = rgb(0,0,255)
  textRenderer_family = inherit
  textRenderer_size = 3.6
  unit_custom_scale = 1
  unit_scheme = 0
FEATURE [Drawing::FeatureViewPython] dim097  # drawing view (typed FeaturePython)
  Rotation = 0
  ViewResult = <g> \n  <line x1="170.000000" y1="126.560000" x2="229.000000" y2="126.560000" style="stroke:rgb(0,0,255);stroke-width:0.50" />\n<line x1="207.000000" y1="49.410000" x2="229.000000" y2="49.410000" style="stroke:rgb(0,0,255);stroke-width:0.50" />\n<line x1="228.000000" y1="126.560000" x2="228.000000" y2="49.410000" style="stroke:rgb(0,0,255);stroke-width:0.50" /> \n  <polygon points="228.000000,49.410000 227.000000,52.410000 228.000000,53.410000 229.000000,52.410000" style="fill:rgb(0,0,255);stroke:rgb(0,0,255);stroke-width:0" /><polygon points="228.000000,126.560000 229.000000,123.560000 228.000000,122.560000 227.000000,123.560000" style="fill:rgb(0,0,255);stroke:rgb(0,0,255);stroke-width:0" /> \n  <text x="226.000000" y="87.985000" font-family="inherit" font-size="3.6" fill="rgb(0,0,255)" text-anchor="middle" transform="rotate(-90.000000 226.000000,87.985000)" >77.15</text> </g>
  Visible = false
  X = 0
  Y = 0
  arrowL1 = 3
  arrowL2 = 1
  arrowW = 2
  arrow_scheme = 0
  autoPlaceOffset = 2
  autoPlaceText = true
  click1_x = 228
  click1_y = 59
  click2_x = 228
  click2_y = 59
  comma_decimal_place = false
  dimension_line_overshoot = 1
  gap_datum_points = 2
  halfDimension_linear = false
  lineColor = rgb(0,0,255)
  strokeWidth = 0.5
  textFormat_linear = %(value)3.3f
  textRenderer_color = rgb(0,0,255)
  textRenderer_family = inherit
  textRenderer_size = 3.6
  unit_custom_scale = 1
  unit_scheme = 0
FEATURE [Drawing::FeatureViewPython] dia018  # drawing view (typed FeaturePython)
  Rotation = 0
  ViewResult = <g>  <circle cx ="112.000000" cy ="126.560000" r="0.250000" stroke="none" fill="rgb(0,0,255)" /> \n<line x1="122.500000" y1="126.500000" x2="108.400059" y2="126.580571" style="stroke:rgb(0,0,255);stroke-width:0.50" />\n<polygon points="115.599941,126.539429 118.605606,127.522270 119.599876,126.516572 118.594178,125.522303" style="fill:rgb(0,0,255);stroke:rgb(0,0,255);stroke-width:0" />\n<polygon points="108.400059,126.580571 105.394394,125.597730 104.400124,126.603428 105.405822,127.597697" style="fill:rgb(0,0,255);stroke:rgb(0,0,255);stroke-width:0" />\n<line x1="122.500000" y1="126.500000" x2="130.500000" y2="126.500000" style="stroke:rgb(0,0,255);stroke-width:0.50" />\n<text x="126.500000" y="124.500000" font-family="inherit" font-size="3.6" fill="rgb(0,0,255)" text-anchor="middle" transform="rotate(0.000000 126.500000,124.500000)" >Ø7.2</text> </g>
  Visible = false
  X = 0
  Y = 0
  arrowL1 = 3
  arrowL2 = 1
  arrowW = 2
  arrow_scheme = 0
  autoPlaceOffset = 2
  autoPlaceText = true
  centerPointDia = 0.5
  click1_x = 122.5
  click1_y = 126.5
  click2_x = 130.5
  click2_y = 126.5
  click3_x = 130.5
  click3_y = 126.5
  comma_decimal_place = false
  lineColor = rgb(0,0,255)
  strokeWidth = 0.5
  textFormat_circular = Ø%(value)3.3f
  textRenderer_color = rgb(0,0,255)
  textRenderer_family = inherit
  textRenderer_size = 3.6
  unit_custom_scale = 1
  unit_scheme = 0
FEATURE [Drawing::FeatureViewPython] text066  # drawing view (typed FeaturePython)
  Rotation = 0
  ViewResult = <g> <text x="124.500000" y="129.500000" font-family="inherit" font-size="3,6" fill="rgb(0,0,255)" text-anchor="inherit" transform="rotate(0.000000 124.500000,129.500000)" >H5</text> </g>
  Visible = false
  X = 0
  Y = 0
  click1_x = 124.5
  click1_y = 129.5
  rotation = 0
  text = H5
  textRenderer_addText_color = rgb(0,0,255)
  textRenderer_addText_family = inherit
  textRenderer_addText_size = 3,6
FEATURE [Drawing::FeatureViewPython] text067  # drawing view (typed FeaturePython)
  Rotation = 0
  ViewResult = <g> <text x="156.500000" y="127.500000" font-family="inherit" font-size="3,6" fill="rgb(0,0,255)" text-anchor="inherit" transform="rotate(0.000000 156.500000,127.500000)" >H5</text> </g>
  Visible = false
  X = 0
  Y = 0
  click1_x = 156.5
  click1_y = 127.5
  rotation = 0
  text = H5
  textRenderer_addText_color = rgb(0,0,255)
  textRenderer_addText_family = inherit
  textRenderer_addText_size = 3,6
FEATURE [Drawing::FeatureViewPython] dim098  # drawing view (typed FeaturePython)
  Rotation = 0
  ViewResult = <g> \n  <line x1="75.000000" y1="47.410000" x2="75.000000" y2="35.000000" style="stroke:rgb(0,0,255);stroke-width:0.50" />\n<line x1="205.000000" y1="47.410000" x2="205.000000" y2="35.000000" style="stroke:rgb(0,0,255);stroke-width:0.50" />\n<line x1="75.000000" y1="36.000000" x2="205.000000" y2="36.000000" style="stroke:rgb(0,0,255);stroke-width:0.50" /> \n  <polygon points="205.000000,36.000000 202.000000,35.000000 201.000000,36.000000 202.000000,37.000000" style="fill:rgb(0,0,255);stroke:rgb(0,0,255);stroke-width:0" /><polygon points="75.000000,36.000000 78.000000,37.000000 79.000000,36.000000 78.000000,35.000000" style="fill:rgb(0,0,255);stroke:rgb(0,0,255);stroke-width:0" /> \n  <text x="140.000000" y="34.000000" font-family="inherit" font-size="3.6" fill="rgb(0,0,255)" text-anchor="middle" transform="rotate(0.000000 140.000000,34.000000)" >130</text> </g>
  Visible = false
  X = 0
  Y = 0
  arrowL1 = 3
  arrowL2 = 1
  arrowW = 2
  arrow_scheme = 0
  autoPlaceOffset = 2
  autoPlaceText = true
  click1_x = 206.5
  click1_y = 36
  click2_x = 206.5
  click2_y = 36
  comma_decimal_place = false
  dimension_line_overshoot = 1
  gap_datum_points = 2
  halfDimension_linear = false
  lineColor = rgb(0,0,255)
  strokeWidth = 0.5
  textFormat_linear = %(value)3.3f
  textRenderer_color = rgb(0,0,255)
  textRenderer_family = inherit
  textRenderer_size = 3.6
  unit_custom_scale = 1
  unit_scheme = 0
FEATURE [Drawing::FeatureViewPython] dim099  # drawing view (typed FeaturePython)
  Rotation = 0
  ViewResult = <g> \n  <line x1="70.000000" y1="52.420200" x2="70.000000" y2="26.000000" style="stroke:rgb(0,0,255);stroke-width:0.50" />\n<line x1="210.000000" y1="52.420200" x2="210.000000" y2="26.000000" style="stroke:rgb(0,0,255);stroke-width:0.50" />\n<line x1="70.000000" y1="27.000000" x2="210.000000" y2="27.000000" style="stroke:rgb(0,0,255);stroke-width:0.50" /> \n  <polygon points="210.000000,27.000000 207.000000,26.000000 206.000000,27.000000 207.000000,28.000000" style="fill:rgb(0,0,255);stroke:rgb(0,0,255);stroke-width:0" /><polygon points="70.000000,27.000000 73.000000,28.000000 74.000000,27.000000 73.000000,26.000000" style="fill:rgb(0,0,255);stroke:rgb(0,0,255);stroke-width:0" /> \n  <text x="140.000000" y="25.000000" font-family="inherit" font-size="3.6" fill="rgb(0,0,255)" text-anchor="middle" transform="rotate(0.000000 140.000000,25.000000)" >140</text> </g>
  Visible = false
  X = 0
  Y = 0
  arrowL1 = 3
  arrowL2 = 1
  arrowW = 2
  arrow_scheme = 0
  autoPlaceOffset = 2
  autoPlaceText = true
  click1_x = 227
  click1_y = 27
  click2_x = 227
  click2_y = 27
  comma_decimal_place = false
  dimension_line_overshoot = 1
  gap_datum_points = 2
  halfDimension_linear = false
  lineColor = rgb(0,0,255)
  strokeWidth = 0.5
  textFormat_linear = %(value)3.3f
  textRenderer_color = rgb(0,0,255)
  textRenderer_family = inherit
  textRenderer_size = 3.6
  unit_custom_scale = 1
  unit_scheme = 0
FEATURE [Drawing::FeatureViewPython] dim100  # drawing view (typed FeaturePython)
  Rotation = 0
  ViewResult = <g> \n  <line x1="73.000000" y1="49.410000" x2="24.500000" y2="49.410000" style="stroke:rgb(0,0,255);stroke-width:0.50" />\n<line x1="73.000000" y1="199.410000" x2="24.500000" y2="199.410000" style="stroke:rgb(0,0,255);stroke-width:0.50" />\n<line x1="25.500000" y1="49.410000" x2="25.500000" y2="199.410000" style="stroke:rgb(0,0,255);stroke-width:0.50" /> \n  <polygon points="25.500000,199.410000 26.500000,196.410000 25.500000,195.410000 24.500000,196.410000" style="fill:rgb(0,0,255);stroke:rgb(0,0,255);stroke-width:0" /><polygon points="25.500000,49.410000 24.500000,52.410000 25.500000,53.410000 26.500000,52.410000" style="fill:rgb(0,0,255);stroke:rgb(0,0,255);stroke-width:0" /> \n  <text x="23.500000" y="124.410000" font-family="inherit" font-size="3.6" fill="rgb(0,0,255)" text-anchor="middle" transform="rotate(-90.000000 23.500000,124.410000)" >150</text> </g>
  Visible = false
  X = 0
  Y = 0
  arrowL1 = 3
  arrowL2 = 1
  arrowW = 2
  arrow_scheme = 0
  autoPlaceOffset = 2
  autoPlaceText = true
  click1_x = 25.5
  click1_y = 198
  click2_x = 25.5
  click2_y = 198
  comma_decimal_place = false
  dimension_line_overshoot = 1
  gap_datum_points = 2
  halfDimension_linear = false
  lineColor = rgb(0,0,255)
  strokeWidth = 0.5
  textFormat_linear = %(value)3.3f
  textRenderer_color = rgb(0,0,255)
  textRenderer_family = inherit
  textRenderer_size = 3.6
  unit_custom_scale = 1
  unit_scheme = 0
FEATURE [Drawing::FeatureViewPython] dim101  # drawing view (typed FeaturePython)
  Rotation = 0
  ViewResult = <g> \n  <line x1="68.000000" y1="54.420200" x2="35.000000" y2="54.420200" style="stroke:rgb(0,0,255);stroke-width:0.50" />\n<line x1="68.000000" y1="194.420000" x2="35.000000" y2="194.420000" style="stroke:rgb(0,0,255);stroke-width:0.50" />\n<line x1="36.000000" y1="54.420200" x2="36.000000" y2="194.420000" style="stroke:rgb(0,0,255);stroke-width:0.50" /> \n  <polygon points="36.000000,194.420000 37.000000,191.420000 36.000000,190.420000 35.000000,191.420000" style="fill:rgb(0,0,255);stroke:rgb(0,0,255);stroke-width:0" /><polygon points="36.000000,54.420200 35.000000,57.420200 36.000000,58.420200 37.000000,57.420200" style="fill:rgb(0,0,255);stroke:rgb(0,0,255);stroke-width:0" /> \n  <text x="34.000000" y="124.420100" font-family="inherit" font-size="3.6" fill="rgb(0,0,255)" text-anchor="middle" transform="rotate(-90.000000 34.000000,124.420100)" >140</text> </g>
  Visible = false
  X = 0
  Y = 0
  arrowL1 = 3
  arrowL2 = 1
  arrowW = 2
  arrow_scheme = 0
  autoPlaceOffset = 2
  autoPlaceText = true
  click1_x = 36
  click1_y = 178.5
  click2_x = 36
  click2_y = 178.5
  comma_decimal_place = false
  dimension_line_overshoot = 1
  gap_datum_points = 2
  halfDimension_linear = false
  lineColor = rgb(0,0,255)
  strokeWidth = 0.5
  textFormat_linear = %(value)3.3f
  textRenderer_color = rgb(0,0,255)
  textRenderer_family = inherit
  textRenderer_size = 3.6
  unit_custom_scale = 1
  unit_scheme = 0
FEATURE [Drawing::FeatureViewPython] table003  # drawing view (typed FeaturePython)
  Rotation = 0
  ViewResult = <blob: 9936 chars omitted>
  Visible = false
  X = 0
  Y = 0
  border_color = rgb(0,0,0)
  border_width = 0.3
  click1_x = 237
  click1_y = 165
  column_widths = [20,20,20,20,20,20,24,22]
  contents = Ref | Metric | Drill | Depth | ⌴ ⌀ | ⌴ depth | Threaded | Direction | H1 | M2 | 1.60 | - | - | - | Yes | CW | H2 | M5 | 5.50 | - | - | - | No | - | H3 | M2 | 1.60 | - | - | - | Yes | CCW | H4 | M3 | 3.30 | - | 6.00 | 1.80 | No | - | H5 | - | 7.20 | - | 10.00 | 3.00 | No | - | H6 | M5 | 5.50 | - | 10.00 | 3.00 | No | - | H7 | M2 | 2.2 | - | - | - | No | -
  extra_rows = 0
  padding_x = 1
  padding_y = 1
  row_heights = [7]
  textRenderer_table_color = rgb(0,0,0)
  textRenderer_table_family = inherit
  textRenderer_table_size = 5
FEATURE [Drawing::FeatureViewPython] dia019  # drawing view (typed FeaturePython)
  Rotation = 0
  ViewResult = <g>  <circle cx ="92.000000" cy ="186.560000" r="0.250000" stroke="none" fill="rgb(0,0,255)" /> \n<line x1="98.616411" y1="193.715639" x2="90.133023" y2="184.540867" style="stroke:rgb(0,0,255);stroke-width:0.50" />\n<polygon points="93.866977,188.579133 95.169449,191.460724 96.582580,191.516053 96.637909,190.102922" style="fill:rgb(0,0,255);stroke:rgb(0,0,255);stroke-width:0" />\n<polygon points="90.133023,184.540867 88.830551,181.659276 87.417420,181.603947 87.362091,183.017078" style="fill:rgb(0,0,255);stroke:rgb(0,0,255);stroke-width:0" />\n<line x1="98.616411" y1="193.715639" x2="115.796499" y2="193.715639" style="stroke:rgb(0,0,255);stroke-width:0.50" />\n<text x="107.206455" y="191.715639" font-family="inherit" font-size="3.6" fill="rgb(0,0,255)" text-anchor="middle" transform="rotate(0.000000 107.206455,191.715639)" >Ø5.5</text> </g>
  Visible = false
  X = 0
  Y = 0
  arrowL1 = 3
  arrowL2 = 1
  arrowW = 2
  arrow_scheme = 0
  autoPlaceOffset = 2
  autoPlaceText = true
  centerPointDia = 0.5
  click1_x = 98.6164
  click1_y = 193.716
  click2_x = 115.796
  click2_y = 193.58
  click3_x = 115.796
  click3_y = 193.58
  comma_decimal_place = false
  lineColor = rgb(0,0,255)
  strokeWidth = 0.5
  textFormat_circular = Ø%(value)3.3f
  textRenderer_color = rgb(0,0,255)
  textRenderer_family = inherit
  textRenderer_size = 3.6
  unit_custom_scale = 1
  unit_scheme = 0
FEATURE [Drawing::FeatureViewPython] text068  # drawing view (typed FeaturePython)
  Rotation = 0
  ViewResult = <g> <text x="105.515502" y="197.097546" font-family="inherit" font-size="3,6" fill="rgb(0,0,255)" text-anchor="inherit" transform="rotate(0.000000 105.515502,197.097546)" >H6</text> </g>
  Visible = false
  X = 0
  Y = 0
  click1_x = 105.516
  click1_y = 197.098
  rotation = 0
  text = H6
  textRenderer_addText_color = rgb(0,0,255)
  textRenderer_addText_family = inherit
  textRenderer_addText_size = 3,6
FEATURE [Drawing::FeatureViewPython] text069  # drawing view (typed FeaturePython)
  Rotation = 0
  ViewResult = <g> <text x="176.535551" y="187.357654" font-family="inherit" font-size="3,6" fill="rgb(0,0,255)" text-anchor="inherit" transform="rotate(0.000000 176.535551,187.357654)" >H6</text> </g>
  Visible = false
  X = 0
  Y = 0
  click1_x = 176.536
  click1_y = 187.358
  rotation = 0
  text = H6
  textRenderer_addText_color = rgb(0,0,255)
  textRenderer_addText_family = inherit
  textRenderer_addText_size = 3,6
FEATURE [Drawing::FeatureViewPython] noteCircle002  # drawing view (typed FeaturePython)
  Rotation = 0
  ViewResult = <g> <line x1="360.995020" y1="49.410963" x2="374.905440" y2="64.399080" style="stroke:rgb(0,0,255);stroke-width:0.50" />\n<line x1="360.995020" y1="49.410963" x2="344.033048" y2="49.410963" style="stroke:rgb(0,0,255);stroke-width:0.50" />\n <circle cx ="344.033048" cy ="49.410963" r="4.500000" stroke="rgb(0,0,255)" fill="rgb(255,255,255)" /> \n<text x="342.533048" y="50.910963" font-family="inherit" font-size="5" fill="rgb(0,150,0)" text-anchor="inherit"  >3</text> </g>
  Visible = false
  X = 0
  Y = 0
  click1_x = 360.995
  click1_y = 49.411
  click2_x = 344.033
  click2_y = 50.1484
  lineColor = rgb(0,0,255)
  noteCircle_fill = rgb(255,255,255)
  noteCircle_radius = 4.5
  noteText = 3
  strokeWidth = 0.5
  textRenderer_noteCircle_color = rgb(0,150,0)
  textRenderer_noteCircle_family = inherit
  textRenderer_noteCircle_size = 5
FEATURE [Drawing::FeatureViewPython] text070  # drawing view (typed FeaturePython)
  Rotation = 0
  ViewResult = <g> <text x="20.000000" y="270.000000" font-family="inherit" font-size="10" fill="rgb(0,0,255)" text-anchor="inherit" transform="rotate(0.000000 20.000000,270.000000)" >Material: aluminium 8mm</text> </g>
  Visible = false
  X = 0
  Y = 0
  click1_x = 20
  click1_y = 270
  rotation = 0
  text = Material: aluminium 8mm
  textRenderer_addText_color = rgb(0,0,255)
  textRenderer_addText_family = inherit
  textRenderer_addText_size = 10
FEATURE [Drawing::FeatureViewPython] text071  # drawing view (typed FeaturePython)
  Rotation = 0
  ViewResult = <g> <text x="260.000000" y="62.000000" font-family="inherit" font-size="4" fill="rgb(0,0,255)" text-anchor="inherit" transform="rotate(0.000000 260.000000,62.000000)" >Part number: WHC-OPNP-4NH-F</text> </g>
  Visible = false
  X = 0
  Y = 0
  click1_x = 260
  click1_y = 62
  rotation = 0
  text = Part number: WHC-OPNP-4NH-F
  textRenderer_addText_color = rgb(0,0,255)
  textRenderer_addText_family = inherit
  textRenderer_addText_size = 4
FEATURE [Drawing::FeatureViewPython] noteCircle001  # drawing view (typed FeaturePython)
  Rotation = 0
  ViewResult = <g> <line x1="315.105001" y1="51.894147" x2="321.391990" y2="63.385750" style="stroke:rgb(0,0,255);stroke-width:0.50" />\n<line x1="315.105001" y1="51.894147" x2="285.417809" y2="51.894147" style="stroke:rgb(0,0,255);stroke-width:0.50" />\n <circle cx ="285.417809" cy ="51.894147" r="4.500000" stroke="rgb(0,0,255)" fill="rgb(255,255,255)" /> \n<text x="283.917809" y="53.394147" font-family="inherit" font-size="5" fill="rgb(0,150,0)" text-anchor="inherit"  >1</text> </g>
  Visible = false
  X = 0
  Y = 0
  click1_x = 315.105
  click1_y = 51.8941
  click2_x = 285.418
  click2_y = 43.9464
  lineColor = rgb(0,0,255)
  noteCircle_fill = rgb(255,255,255)
  noteCircle_radius = 4.5
  noteText = 1
  strokeWidth = 0.5
  textRenderer_noteCircle_color = rgb(0,150,0)
  textRenderer_noteCircle_family = inherit
  textRenderer_noteCircle_size = 5
FEATURE [Drawing::FeatureViewPython] text072  # drawing view (typed FeaturePython)
  Rotation = 0
  ViewResult = <g> <text x="256.000000" y="53.000000" font-family="inherit" font-size="4" fill="rgb(0,0,255)" text-anchor="inherit" transform="rotate(0.000000 256.000000,53.000000)" >Part number: WHC-OPNP-4NH-B</text> </g>
  Visible = true
  X = 0
  Y = 0
  click1_x = 256
  click1_y = 53
  rotation = 0
  text = Part number: WHC-OPNP-4NH-B
  textRenderer_addText_color = rgb(0,0,255)
  textRenderer_addText_family = inherit
  textRenderer_addText_size = 4
FEATURE [Drawing::FeatureViewPython] noteCircle004  # drawing view (typed FeaturePython)
  Rotation = 0
  ViewResult = <g> <line x1="307.282108" y1="41.995221" x2="316.453840" y2="46.045765" style="stroke:rgb(0,0,255);stroke-width:0.50" />\n<line x1="307.282108" y1="41.995221" x2="285.004155" y2="41.995221" style="stroke:rgb(0,0,255);stroke-width:0.50" />\n <circle cx ="285.004155" cy ="41.995221" r="4.500000" stroke="rgb(0,0,255)" fill="rgb(255,255,255)" /> \n<text x="283.504155" y="43.495221" font-family="inherit" font-size="5" fill="rgb(0,150,0)" text-anchor="inherit"  >2</text> </g>
  Visible = true
  X = 0
  Y = 0
  click1_x = 307.282
  click1_y = 41.9952
  click2_x = 285.004
  click2_y = 38.9224
  lineColor = rgb(0,0,255)
  noteCircle_fill = rgb(255,255,255)
  noteCircle_radius = 4.5
  noteText = 2
  strokeWidth = 0.5
  textRenderer_noteCircle_color = rgb(0,150,0)
  textRenderer_noteCircle_family = inherit
  textRenderer_noteCircle_size = 5
FEATURE [Drawing::FeatureViewPython] text073  # drawing view (typed FeaturePython)
  Rotation = 0
  ViewResult = <g> <text x="310.000000" y="60.000000" font-family="inherit" font-size="4" fill="rgb(0,0,255)" text-anchor="inherit" transform="rotate(0.000000 310.000000,60.000000)" >Part number: WHC-OPNP-LNA</text> </g>
  Visible = false
  X = 0
  Y = 0
  click1_x = 310
  click1_y = 60
  rotation = 0
  text = Part number: WHC-OPNP-LNA
  textRenderer_addText_color = rgb(0,0,255)
  textRenderer_addText_family = inherit
  textRenderer_addText_size = 4
FEATURE [Drawing::FeatureViewPython] text074  # drawing view (typed FeaturePython)
  Rotation = 0
  ViewResult = <g> <text x="308.000000" y="123.000000" font-family="inherit" font-size="4" fill="rgb(0,0,255)" text-anchor="inherit" transform="rotate(0.000000 308.000000,123.000000)" >Part number: WHC-OPNP-NB</text> </g>
  Visible = false
  X = 0
  Y = 0
  click1_x = 308
  click1_y = 123
  rotation = 0
  text = Part number: WHC-OPNP-NB
  textRenderer_addText_color = rgb(0,0,255)
  textRenderer_addText_family = inherit
  textRenderer_addText_size = 4
FEATURE [Drawing::FeatureViewPython] noteCircle003  # drawing view (typed FeaturePython)
  Rotation = 0
  ViewResult = <g> <line x1="342.918297" y1="112.670106" x2="368.397960" y2="111.541640" style="stroke:rgb(0,0,255);stroke-width:0.50" />\n<line x1="342.918297" y1="112.670106" x2="335.022854" y2="112.670106" style="stroke:rgb(0,0,255);stroke-width:0.50" />\n <circle cx ="335.022854" cy ="112.670106" r="4.500000" stroke="rgb(0,0,255)" fill="rgb(255,255,255)" /> \n<text x="333.522854" y="114.170106" font-family="inherit" font-size="5" fill="rgb(0,150,0)" text-anchor="inherit"  >4</text> </g>
  Visible = false
  X = 0
  Y = 0
  click1_x = 342.918
  click1_y = 112.67
  click2_x = 335.023
  click2_y = 120.352
  lineColor = rgb(0,0,255)
  noteCircle_fill = rgb(255,255,255)
  noteCircle_radius = 4.5
  noteText = 4
  strokeWidth = 0.5
  textRenderer_noteCircle_color = rgb(0,150,0)
  textRenderer_noteCircle_family = inherit
  textRenderer_noteCircle_size = 5
FEATURE [Drawing::FeatureViewPython] dim102  # drawing view (typed FeaturePython)
  Rotation = 0
  ViewResult = <g> \n  <line x1="125.610000" y1="74.086000" x2="125.610000" y2="68.891789" style="stroke:rgb(0,0,255);stroke-width:0.50" />\n<line x1="135.210000" y1="74.086000" x2="135.210000" y2="68.891789" style="stroke:rgb(0,0,255);stroke-width:0.50" />\n<line x1="125.610000" y1="69.891789" x2="135.210000" y2="69.891789" style="stroke:rgb(0,0,255);stroke-width:0.50" /> \n  <polygon points="135.210000,69.891789 138.210000,70.891789 139.210000,69.891789 138.210000,68.891789" style="fill:rgb(0,0,255);stroke:rgb(0,0,255);stroke-width:0" /><polygon points="125.610000,69.891789 122.610000,68.891789 121.610000,69.891789 122.610000,70.891789" style="fill:rgb(0,0,255);stroke:rgb(0,0,255);stroke-width:0" /> \n  <text x="130.410000" y="67.891789" font-family="inherit" font-size="3.6" fill="rgb(0,0,255)" text-anchor="middle" transform="rotate(0.000000 130.410000,67.891789)" >8</text> </g>
  Visible = false
  X = 0
  Y = 0
  arrowL1 = 3
  arrowL2 = 1
  arrowW = 2
  arrow_scheme = 0
  autoPlaceOffset = 2
  autoPlaceText = true
  click1_x = 135.753
  click1_y = 69.8918
  click2_x = 135.753
  click2_y = 69.8918
  comma_decimal_place = false
  dimension_line_overshoot = 1
  gap_datum_points = 2
  halfDimension_linear = false
  lineColor = rgb(0,0,255)
  strokeWidth = 0.5
  textFormat_linear = %(value)3.3f
  textRenderer_color = rgb(0,0,255)
  textRenderer_family = inherit
  textRenderer_size = 3.6
  unit_custom_scale = 1
  unit_scheme = 0
FEATURE [Drawing::FeatureViewPython] dim103  # drawing view (typed FeaturePython)
  Rotation = 0
  ViewResult = <g> \n  <line x1="123.610000" y1="76.086000" x2="118.201948" y2="76.086000" style="stroke:rgb(0,0,255);stroke-width:0.50" />\n<line x1="123.610000" y1="85.686000" x2="118.201948" y2="85.686000" style="stroke:rgb(0,0,255);stroke-width:0.50" />\n<line x1="119.201948" y1="76.086000" x2="119.201948" y2="85.686000" style="stroke:rgb(0,0,255);stroke-width:0.50" /> \n  <polygon points="119.201948,85.686000 118.201948,88.686000 119.201948,89.686000 120.201948,88.686000" style="fill:rgb(0,0,255);stroke:rgb(0,0,255);stroke-width:0" /><polygon points="119.201948,76.086000 120.201948,73.086000 119.201948,72.086000 118.201948,73.086000" style="fill:rgb(0,0,255);stroke:rgb(0,0,255);stroke-width:0" /> \n  <text x="117.201948" y="80.886000" font-family="inherit" font-size="3.6" fill="rgb(0,0,255)" text-anchor="middle" transform="rotate(-90.000000 117.201948,80.886000)" >8</text> </g>
  Visible = false
  X = 0
  Y = 0
  arrowL1 = 3
  arrowL2 = 1
  arrowW = 2
  arrow_scheme = 0
  autoPlaceOffset = 2
  autoPlaceText = true
  click1_x = 119.202
  click1_y = 84.7277
  click2_x = 119.202
  click2_y = 84.7277
  comma_decimal_place = false
  dimension_line_overshoot = 1
  gap_datum_points = 2
  halfDimension_linear = false
  lineColor = rgb(0,0,255)
  strokeWidth = 0.5
  textFormat_linear = %(value)3.3f
  textRenderer_color = rgb(0,0,255)
  textRenderer_family = inherit
  textRenderer_size = 3.6
  unit_custom_scale = 1
  unit_scheme = 0
FEATURE [Drawing::FeatureViewPython] dim104  # drawing view (typed FeaturePython)
  Rotation = 0
  ViewResult = <g> \n  <line x1="137.210000" y1="76.086000" x2="151.933262" y2="76.086000" style="stroke:rgb(0,0,255);stroke-width:0.50" />\n<line x1="142.010000" y1="32.472000" x2="151.933262" y2="32.472000" style="stroke:rgb(0,0,255);stroke-width:0.50" />\n<line x1="150.933262" y1="76.086000" x2="150.933262" y2="32.472000" style="stroke:rgb(0,0,255);stroke-width:0.50" /> \n  <polygon points="150.933262,32.472000 149.933262,35.472000 150.933262,36.472000 151.933262,35.472000" style="fill:rgb(0,0,255);stroke:rgb(0,0,255);stroke-width:0" /><polygon points="150.933262,76.086000 151.933262,73.086000 150.933262,72.086000 149.933262,73.086000" style="fill:rgb(0,0,255);stroke:rgb(0,0,255);stroke-width:0" /> \n  <text x="148.933262" y="54.279000" font-family="inherit" font-size="3.6" fill="rgb(0,0,255)" text-anchor="middle" transform="rotate(-90.000000 148.933262,54.279000)" >36.345</text> </g>
  Visible = false
  X = 0
  Y = 0
  arrowL1 = 3
  arrowL2 = 1
  arrowW = 2
  arrow_scheme = 0
  autoPlaceOffset = 2
  autoPlaceText = true
  click1_x = 150.933
  click1_y = 35.2282
  click2_x = 150.933
  click2_y = 35.2282
  comma_decimal_place = false
  dimension_line_overshoot = 1
  gap_datum_points = 2
  halfDimension_linear = false
  lineColor = rgb(0,0,255)
  strokeWidth = 0.5
  textFormat_linear = %(value)3.3f
  textRenderer_color = rgb(0,0,255)
  textRenderer_family = inherit
  textRenderer_size = 3.6
  unit_custom_scale = 1
  unit_scheme = 0
FEATURE [Drawing::FeatureViewPython] dim105  # drawing view (typed FeaturePython)
  Rotation = 0
  ViewResult = <g> \n  <line x1="125.610000" y1="87.686000" x2="125.610000" y2="99.688922" style="stroke:rgb(0,0,255);stroke-width:0.50" />\n<line x1="113.563320" y1="34.472000" x2="113.563320" y2="99.688922" style="stroke:rgb(0,0,255);stroke-width:0.50" />\n<line x1="125.610000" y1="98.688922" x2="113.563320" y2="98.688922" style="stroke:rgb(0,0,255);stroke-width:0.50" /> \n  <polygon points="113.563320,98.688922 116.563320,99.688922 117.563320,98.688922 116.563320,97.688922" style="fill:rgb(0,0,255);stroke:rgb(0,0,255);stroke-width:0" /><polygon points="125.610000,98.688922 122.610000,97.688922 121.610000,98.688922 122.610000,99.688922" style="fill:rgb(0,0,255);stroke:rgb(0,0,255);stroke-width:0" /> \n  <text x="119.586660" y="96.688922" font-family="inherit" font-size="3.6" fill="rgb(0,0,255)" text-anchor="middle" transform="rotate(0.000000 119.586660,96.688922)" >10.039</text> </g>
  Visible = false
  X = 0
  Y = 0
  arrowL1 = 3
  arrowL2 = 1
  arrowW = 2
  arrow_scheme = 0
  autoPlaceOffset = 2
  autoPlaceText = true
  click1_x = 120.814
  click1_y = 98.6889
  click2_x = 120.814
  click2_y = 98.6889
  comma_decimal_place = false
  dimension_line_overshoot = 1
  gap_datum_points = 2
  halfDimension_linear = false
  lineColor = rgb(0,0,255)
  strokeWidth = 0.5
  textFormat_linear = %(value)3.3f
  textRenderer_color = rgb(0,0,255)
  textRenderer_family = inherit
  textRenderer_size = 3.6
  unit_custom_scale = 1
  unit_scheme = 0
FEATURE [Drawing::FeatureViewPython] dia020  # drawing view (typed FeaturePython)
  Rotation = 0
  ViewResult = <g>  <circle cx ="125.610000" cy ="85.686000" r="0.250000" stroke="none" fill="rgb(0,0,255)" /> \n<line x1="129.787767" y1="93.852238" x2="125.172769" y2="84.831349" style="stroke:rgb(0,0,255);stroke-width:0.50" />\n<polygon points="126.047231,86.540651 126.523317,89.666886 127.869028,90.101699 128.303840,88.755988" style="fill:rgb(0,0,255);stroke:rgb(0,0,255);stroke-width:0" />\n<polygon points="125.172769,84.831349 124.696683,81.705114 123.350972,81.270301 122.916160,82.616012" style="fill:rgb(0,0,255);stroke:rgb(0,0,255);stroke-width:0" />\n<line x1="129.787767" y1="93.852238" x2="138.185072" y2="93.852238" style="stroke:rgb(0,0,255);stroke-width:0.50" />\n<text x="133.986419" y="91.852238" font-family="inherit" font-size="3.6" fill="rgb(0,0,255)" text-anchor="middle" transform="rotate(0.000000 133.986419,91.852238)" >Ø1.6</text> </g>
  Visible = false
  X = 0
  Y = 0
  arrowL1 = 3
  arrowL2 = 1
  arrowW = 2
  arrow_scheme = 0
  autoPlaceOffset = 2
  autoPlaceText = true
  centerPointDia = 0.5
  click1_x = 129.788
  click1_y = 93.8522
  click2_x = 138.185
  click2_y = 93.4818
  click3_x = 138.185
  click3_y = 93.4818
  comma_decimal_place = false
  lineColor = rgb(0,0,255)
  strokeWidth = 0.5
  textFormat_circular = Ø%(value)3.3f
  textRenderer_color = rgb(0,0,255)
  textRenderer_family = inherit
  textRenderer_size = 3.6
  unit_custom_scale = 1
  unit_scheme = 0
FEATURE [Drawing::FeatureViewPython] text075  # drawing view (typed FeaturePython)
  Rotation = 0
  ViewResult = <g> <text x="132.134073" y="96.692504" font-family="inherit" font-size="3,6" fill="rgb(0,0,255)" text-anchor="inherit" transform="rotate(0.000000 132.134073,96.692504)" >H3</text> </g>
  Visible = false
  X = 0
  Y = 0
  click1_x = 132.134
  click1_y = 96.6925
  rotation = 0
  text = H3
  textRenderer_addText_color = rgb(0,0,255)
  textRenderer_addText_family = inherit
  textRenderer_addText_size = 3,6
FEATURE [Drawing::FeatureViewPython] text076  # drawing view (typed FeaturePython)
  Rotation = 0
  ViewResult = <g> <text x="132.751521" y="83.849566" font-family="inherit" font-size="3,6" fill="rgb(0,0,255)" text-anchor="inherit" transform="rotate(0.000000 132.751521,83.849566)" >H3</text> </g>
  Visible = false
  X = 0
  Y = 0
  click1_x = 132.752
  click1_y = 83.8496
  rotation = 0
  text = H3
  textRenderer_addText_color = rgb(0,0,255)
  textRenderer_addText_family = inherit
  textRenderer_addText_size = 3,6
FEATURE [Drawing::FeatureViewPython] text077  # drawing view (typed FeaturePython)
  Rotation = 0
  ViewResult = <g> <text x="132.875011" y="80.021382" font-family="inherit" font-size="3,6" fill="rgb(0,0,255)" text-anchor="inherit" transform="rotate(0.000000 132.875011,80.021382)" >H3</text> </g>
  Visible = false
  X = 0
  Y = 0
  click1_x = 132.875
  click1_y = 80.0214
  rotation = 0
  text = H3
  textRenderer_addText_color = rgb(0,0,255)
  textRenderer_addText_family = inherit
  textRenderer_addText_size = 3,6
FEATURE [Drawing::FeatureViewPython] text078  # drawing view (typed FeaturePython)
  Rotation = 0
  ViewResult = <g> <text x="123.736767" y="80.021382" font-family="inherit" font-size="3,6" fill="rgb(0,0,255)" text-anchor="inherit" transform="rotate(0.000000 123.736767,80.021382)" >H3</text> </g>
  Visible = false
  X = 0
  Y = 0
  click1_x = 123.737
  click1_y = 80.0214
  rotation = 0
  text = H3
  textRenderer_addText_color = rgb(0,0,255)
  textRenderer_addText_family = inherit
  textRenderer_addText_size = 3,6
FEATURE [Drawing::FeatureViewPython] noteCircle005  # drawing view (typed FeaturePython)
  Rotation = 0
  ViewResult = <g> <line x1="96.610000" y1="55.679518" x2="113.563320" y2="32.472000" style="stroke:rgb(0,0,255);stroke-width:0.50" />\n<line x1="96.610000" y1="55.679518" x2="96.978233" y2="55.679518" style="stroke:rgb(0,0,255);stroke-width:0.50" />\n <circle cx ="96.978233" cy ="55.679518" r="4.500000" stroke="rgb(0,0,255)" fill="rgb(255,255,255)" /> \n<text x="95.478233" y="57.179518" font-family="inherit" font-size="5" fill="rgb(0,150,0)" text-anchor="inherit"  >3</text> </g>
  Visible = false
  X = 0
  Y = 0
  click1_x = 96.61
  click1_y = 55.6795
  click2_x = 96.9782
  click2_y = 63.0543
  lineColor = rgb(0,0,255)
  noteCircle_fill = rgb(255,255,255)
  noteCircle_radius = 4.5
  noteText = 3
  strokeWidth = 0.5
  textRenderer_noteCircle_color = rgb(0,150,0)
  textRenderer_noteCircle_family = inherit
  textRenderer_noteCircle_size = 5
FEATURE [Drawing::FeatureViewPython] noteCircle006  # drawing view (typed FeaturePython)
  Rotation = 0
  ViewResult = <g> <line x1="267.340000" y1="111.645833" x2="247.248000" y2="125.196760" style="stroke:rgb(0,0,255);stroke-width:0.50" />\n<line x1="267.340000" y1="111.645833" x2="274.505350" y2="111.645833" style="stroke:rgb(0,0,255);stroke-width:0.50" />\n <circle cx ="274.505350" cy ="111.645833" r="4.500000" stroke="rgb(0,0,255)" fill="rgb(255,255,255)" /> \n<text x="273.005350" y="113.145833" font-family="inherit" font-size="5" fill="rgb(0,150,0)" text-anchor="inherit"  >4</text> </g>
  Visible = false
  X = 0
  Y = 0
  click1_x = 267.34
  click1_y = 111.646
  click2_x = 274.505
  click2_y = 119.072
  lineColor = rgb(0,0,255)
  noteCircle_fill = rgb(255,255,255)
  noteCircle_radius = 4.5
  noteText = 4
  strokeWidth = 0.5
  textRenderer_noteCircle_color = rgb(0,150,0)
  textRenderer_noteCircle_family = inherit
  textRenderer_noteCircle_size = 5
FEATURE [Drawing::FeatureViewPython] noteCircle007  # drawing view (typed FeaturePython)
  Rotation = 0
  ViewResult = <g> <line x1="261.960000" y1="167.468749" x2="247.252000" y2="182.804000" style="stroke:rgb(0,0,255);stroke-width:0.50" />\n<line x1="261.960000" y1="167.468749" x2="272.200734" y2="167.468749" style="stroke:rgb(0,0,255);stroke-width:0.50" />\n <circle cx ="272.200734" cy ="167.468749" r="4.500000" stroke="rgb(0,0,255)" fill="rgb(255,255,255)" /> \n<text x="270.700734" y="168.968749" font-family="inherit" font-size="5" fill="rgb(0,150,0)" text-anchor="inherit"  >4</text> </g>
  Visible = false
  X = 0
  Y = 0
  click1_x = 261.96
  click1_y = 167.469
  click2_x = 272.201
  click2_y = 168.237
  lineColor = rgb(0,0,255)
  noteCircle_fill = rgb(255,255,255)
  noteCircle_radius = 4.5
  noteText = 4
  strokeWidth = 0.5
  textRenderer_noteCircle_color = rgb(0,150,0)
  textRenderer_noteCircle_family = inherit
  textRenderer_noteCircle_size = 5
FEATURE [Sketcher::SketchObject] Sketch059
  MapMode = 5
  Placement = pos=(0,0,0) rot=(0.57735,0.57735,0.57735;2.0944rad)
  Support = -> [YZ_Plane023]
  sketch-geometry (3):
    g0: LineSegment StartX=-124.42 StartY=8 StartZ=0 EndX=-90.56 EndY=55 EndZ=0
    g1: LineSegment StartX=-90.56 StartY=55 StartZ=0 EndX=-90.56 EndY=8 EndZ=0
    g2: LineSegment StartX=-90.56 StartY=8 StartZ=0 EndX=-124.42 EndY=8 EndZ=0
  constraints (9):
    c: Coincident(g0,g1)
    c: Vertical(g1)
    c: Coincident(g1,g2)
    c: Coincident(g2,g0)
    c: Horizontal(g2)
    c: DistanceY(g1,g1) = 47
    c: DistanceX(g2,g2) = 33.86
    c: DistanceY(g-1,g1) = 8
    c: DistanceX(g1,g-1) = 90.56
FEATURE [PartDesign::Pad] Pad013
  Length = 10
  Length2 = 100
  Placement = pos=(0,0,0) rot=(0.57735,0.57735,0.57735;2.0944rad)
  Profile = -> Sketch059
  Type = 0
FEATURE [PartDesign::Body] Body006021006  label="Left Square"
  Group = -> [Sketch059,Pad013]
  Origin = -> Origin023
  Placement = pos=(-70,0,0) rot=(0,0,1;0rad)
  Tip = -> Pad013
FEATURE [PartDesign::FeatureBase] Clone
  BaseFeature = -> Body006021006
  Placement = pos=(-70,0,0) rot=(0,0,1;0rad)
FEATURE [PartDesign::Body] Body006021007  label="Right Square"
  BaseFeature = -> Body006021006
  Group = -> [Clone]
  Origin = -> Origin024
  Placement = pos=(130,0,0) rot=(0,0,1;0rad)
  Tip = -> Clone
FEATURE [Drawing::FeatureViewPython] rad006  # drawing view (typed FeaturePython)
  Rotation = 0
  ViewResult = <g>  <circle cx ="78.000000" cy ="104.420200" r="0.250000" stroke="none" fill="rgb(0,0,255)" /> \n<line x1="81.122476" y1="114.308944" x2="78.000000" y2="104.420200" style="stroke:rgb(0,0,255);stroke-width:0.50" />\n<polygon points="79.505532,109.188153 79.555803,106.026275 78.301106,105.373791 77.648622,106.628487" style="fill:rgb(0,0,255);stroke:rgb(0,0,255);stroke-width:0" />\n<line x1="81.122476" y1="114.308944" x2="92.922109" y2="114.308944" style="stroke:rgb(0,0,255);stroke-width:0.50" />\n<text x="87.022293" y="112.308944" font-family="inherit" font-size="3.6" fill="rgb(0,0,255)" text-anchor="middle" transform="rotate(0.000000 87.022293,112.308944)" >R5</text> </g>
  Visible = false
  X = 0
  Y = 0
  arrowL1 = 3
  arrowL2 = 1
  arrowW = 2
  arrow_scheme = 0
  autoPlaceOffset = 2
  autoPlaceText = true
  centerPointDia = 0.5
  click1_x = 81.1225
  click1_y = 114.309
  click2_x = 92.9221
  click2_y = 115.784
  click3_x = 92.9221
  click3_y = 115.784
  comma_decimal_place = false
  lineColor = rgb(0,0,255)
  strokeWidth = 0.5
  textFormat_radial = R%(value)3.3f
  textRenderer_color = rgb(0,0,255)
  textRenderer_family = inherit
  textRenderer_size = 3.6
  unit_custom_scale = 1
  unit_scheme = 0
FEATURE [Drawing::FeatureViewPython] rad007  # drawing view (typed FeaturePython)
  Rotation = 0
  ViewResult = <g>  <circle cx ="202.000000" cy ="104.420200" r="0.250000" stroke="none" fill="rgb(0,0,255)" /> \n<line x1="191.744035" y1="112.833990" x2="202.000000" y2="104.420200" style="stroke:rgb(0,0,255);stroke-width:0.50" />\n<polygon points="198.134382,107.591477 201.088008,106.461834 201.226876,105.054455 199.819497,104.915587" style="fill:rgb(0,0,255);stroke:rgb(0,0,255);stroke-width:0" />\n<line x1="191.744035" y1="112.833990" x2="184.738003" y2="112.833990" style="stroke:rgb(0,0,255);stroke-width:0.50" />\n<text x="188.241019" y="110.833990" font-family="inherit" font-size="3.6" fill="rgb(0,0,255)" text-anchor="middle" transform="rotate(0.000000 188.241019,110.833990)" >R5</text> </g>
  Visible = false
  X = 0
  Y = 0
  arrowL1 = 3
  arrowL2 = 1
  arrowW = 2
  arrow_scheme = 0
  autoPlaceOffset = 2
  autoPlaceText = true
  centerPointDia = 0.5
  click1_x = 191.744
  click1_y = 112.834
  click2_x = 184.738
  click2_y = 116.153
  click3_x = 184.738
  click3_y = 116.153
  comma_decimal_place = false
  lineColor = rgb(0,0,255)
  strokeWidth = 0.5
  textFormat_radial = R%(value)3.3f
  textRenderer_color = rgb(0,0,255)
  textRenderer_family = inherit
  textRenderer_size = 3.6
  unit_custom_scale = 1
  unit_scheme = 0
FEATURE [Drawing::FeatureViewPython] dim106  # drawing view (typed FeaturePython)
  Rotation = 0
  ViewResult = <g> \n  <line x1="76.000000" y1="104.420200" x2="60.200353" y2="104.420200" style="stroke:rgb(0,0,255);stroke-width:0.50" />\n<line x1="73.000000" y1="49.410000" x2="60.200353" y2="49.410000" style="stroke:rgb(0,0,255);stroke-width:0.50" />\n<line x1="61.200353" y1="104.420200" x2="61.200353" y2="49.410000" style="stroke:rgb(0,0,255);stroke-width:0.50" /> \n  <polygon points="61.200353,49.410000 60.200353,52.410000 61.200353,53.410000 62.200353,52.410000" style="fill:rgb(0,0,255);stroke:rgb(0,0,255);stroke-width:0" /><polygon points="61.200353,104.420200 62.200353,101.420200 61.200353,100.420200 60.200353,101.420200" style="fill:rgb(0,0,255);stroke:rgb(0,0,255);stroke-width:0" /> \n  <text x="59.200353" y="76.915100" font-family="inherit" font-size="3.6" fill="rgb(0,0,255)" text-anchor="middle" transform="rotate(-90.000000 59.200353,76.915100)" >55.01</text> </g>
  Visible = false
  X = 0
  Y = 0
  arrowL1 = 3
  arrowL2 = 1
  arrowW = 2
  arrow_scheme = 0
  autoPlaceOffset = 2
  autoPlaceText = true
  click1_x = 61.2004
  click1_y = 51.9819
  click2_x = 61.2004
  click2_y = 51.9819
  comma_decimal_place = false
  dimension_line_overshoot = 1
  gap_datum_points = 2
  halfDimension_linear = false
  lineColor = rgb(0,0,255)
  strokeWidth = 0.5
  textFormat_linear = %(value)3.3f
  textRenderer_color = rgb(0,0,255)
  textRenderer_family = inherit
  textRenderer_size = 3.6
  unit_custom_scale = 1
  unit_scheme = 0
FEATURE [Drawing::FeatureViewPython] dim107  # drawing view (typed FeaturePython)
  Rotation = 0
  ViewResult = <g> \n  <line x1="204.000000" y1="104.420200" x2="221.474912" y2="104.420200" style="stroke:rgb(0,0,255);stroke-width:0.50" />\n<line x1="207.000000" y1="49.410000" x2="221.474912" y2="49.410000" style="stroke:rgb(0,0,255);stroke-width:0.50" />\n<line x1="220.474912" y1="104.420200" x2="220.474912" y2="49.410000" style="stroke:rgb(0,0,255);stroke-width:0.50" /> \n  <polygon points="220.474912,49.410000 219.474912,52.410000 220.474912,53.410000 221.474912,52.410000" style="fill:rgb(0,0,255);stroke:rgb(0,0,255);stroke-width:0" /><polygon points="220.474912,104.420200 221.474912,101.420200 220.474912,100.420200 219.474912,101.420200" style="fill:rgb(0,0,255);stroke:rgb(0,0,255);stroke-width:0" /> \n  <text x="218.474912" y="76.915100" font-family="inherit" font-size="3.6" fill="rgb(0,0,255)" text-anchor="middle" transform="rotate(-90.000000 218.474912,76.915100)" >55.01</text> </g>
  Visible = false
  X = 0
  Y = 0
  arrowL1 = 3
  arrowL2 = 1
  arrowW = 2
  arrow_scheme = 0
  autoPlaceOffset = 2
  autoPlaceText = true
  click1_x = 220.475
  click1_y = 53.0062
  click2_x = 220.475
  click2_y = 53.0062
  comma_decimal_place = false
  dimension_line_overshoot = 1
  gap_datum_points = 2
  halfDimension_linear = false
  lineColor = rgb(0,0,255)
  strokeWidth = 0.5
  textFormat_linear = %(value)3.3f
  textRenderer_color = rgb(0,0,255)
  textRenderer_family = inherit
  textRenderer_size = 3.6
  unit_custom_scale = 1
  unit_scheme = 0
FEATURE [Drawing::FeatureViewPython] dim108  # drawing view (typed FeaturePython)
  Rotation = 0
  ViewResult = <g> \n  <line x1="70.000000" y1="56.420200" x2="70.000000" y2="121.864296" style="stroke:rgb(0,0,255);stroke-width:0.50" />\n<line x1="78.000000" y1="106.420200" x2="78.000000" y2="121.864296" style="stroke:rgb(0,0,255);stroke-width:0.50" />\n<line x1="70.000000" y1="120.864296" x2="78.000000" y2="120.864296" style="stroke:rgb(0,0,255);stroke-width:0.50" /> \n  <polygon points="78.000000,120.864296 81.000000,121.864296 82.000000,120.864296 81.000000,119.864296" style="fill:rgb(0,0,255);stroke:rgb(0,0,255);stroke-width:0" /><polygon points="70.000000,120.864296 67.000000,119.864296 66.000000,120.864296 67.000000,121.864296" style="fill:rgb(0,0,255);stroke:rgb(0,0,255);stroke-width:0" /> \n  <text x="74.000000" y="118.864296" font-family="inherit" font-size="3.6" fill="rgb(0,0,255)" text-anchor="middle" transform="rotate(0.000000 74.000000,118.864296)" >8</text> </g>
  Visible = false
  X = 0
  Y = 0
  arrowL1 = 3
  arrowL2 = 1
  arrowW = 2
  arrow_scheme = 0
  autoPlaceOffset = 2
  autoPlaceText = true
  click1_x = 76.3084
  click1_y = 120.864
  click2_x = 76.3084
  click2_y = 120.864
  comma_decimal_place = false
  dimension_line_overshoot = 1
  gap_datum_points = 2
  halfDimension_linear = false
  lineColor = rgb(0,0,255)
  strokeWidth = 0.5
  textFormat_linear = %(value)3.3f
  textRenderer_color = rgb(0,0,255)
  textRenderer_family = inherit
  textRenderer_size = 3.6
  unit_custom_scale = 1
  unit_scheme = 0
FEATURE [Drawing::FeatureViewPython] dim109  # drawing view (typed FeaturePython)
  Rotation = 0
  ViewResult = <g> \n  <line x1="202.000000" y1="106.420200" x2="202.000000" y2="121.096090" style="stroke:rgb(0,0,255);stroke-width:0.50" />\n<line x1="210.000000" y1="56.420200" x2="210.000000" y2="121.096090" style="stroke:rgb(0,0,255);stroke-width:0.50" />\n<line x1="202.000000" y1="120.096090" x2="210.000000" y2="120.096090" style="stroke:rgb(0,0,255);stroke-width:0.50" /> \n  <polygon points="210.000000,120.096090 213.000000,121.096090 214.000000,120.096090 213.000000,119.096090" style="fill:rgb(0,0,255);stroke:rgb(0,0,255);stroke-width:0" /><polygon points="202.000000,120.096090 199.000000,119.096090 198.000000,120.096090 199.000000,121.096090" style="fill:rgb(0,0,255);stroke:rgb(0,0,255);stroke-width:0" /> \n  <text x="206.000000" y="118.096090" font-family="inherit" font-size="3.6" fill="rgb(0,0,255)" text-anchor="middle" transform="rotate(0.000000 206.000000,118.096090)" >8</text> </g>
  Visible = false
  X = 0
  Y = 0
  arrowL1 = 3
  arrowL2 = 1
  arrowW = 2
  arrow_scheme = 0
  autoPlaceOffset = 2
  autoPlaceText = true
  click1_x = 205.367
  click1_y = 120.096
  click2_x = 205.367
  click2_y = 120.096
  comma_decimal_place = false
  dimension_line_overshoot = 1
  gap_datum_points = 2
  halfDimension_linear = false
  lineColor = rgb(0,0,255)
  strokeWidth = 0.5
  textFormat_linear = %(value)3.3f
  textRenderer_color = rgb(0,0,255)
  textRenderer_family = inherit
  textRenderer_size = 3.6
  unit_custom_scale = 1
  unit_scheme = 0
FEATURE [Drawing::FeatureViewPython] dim110  # drawing view (typed FeaturePython)
  Rotation = 0
  ViewResult = <g> \n  <line x1="75.000000" y1="154.560000" x2="75.000000" y2="150.747525" style="stroke:rgb(0,0,255);stroke-width:0.50" />\n<line x1="83.000000" y1="147.760000" x2="83.000000" y2="152.747525" style="stroke:rgb(0,0,255);stroke-width:0.50" />\n<line x1="75.000000" y1="151.747525" x2="83.000000" y2="151.747525" style="stroke:rgb(0,0,255);stroke-width:0.50" /> \n  <polygon points="83.000000,151.747525 86.000000,152.747525 87.000000,151.747525 86.000000,150.747525" style="fill:rgb(0,0,255);stroke:rgb(0,0,255);stroke-width:0" /><polygon points="75.000000,151.747525 72.000000,150.747525 71.000000,151.747525 72.000000,152.747525" style="fill:rgb(0,0,255);stroke:rgb(0,0,255);stroke-width:0" /> \n  <text x="79.000000" y="149.747525" font-family="inherit" font-size="3.6" fill="rgb(0,0,255)" text-anchor="middle" transform="rotate(0.000000 79.000000,149.747525)" >8</text> </g>
  Visible = false
  X = 0
  Y = 0
  arrowL1 = 3
  arrowL2 = 1
  arrowW = 2
  arrow_scheme = 0
  autoPlaceOffset = 2
  autoPlaceText = true
  click1_x = 79.8671
  click1_y = 151.748
  click2_x = 79.8671
  click2_y = 151.748
  comma_decimal_place = false
  dimension_line_overshoot = 1
  gap_datum_points = 2
  halfDimension_linear = false
  lineColor = rgb(0,0,255)
  strokeWidth = 0.5
  textFormat_linear = %(value)3.3f
  textRenderer_color = rgb(0,0,255)
  textRenderer_family = inherit
  textRenderer_size = 3.6
  unit_custom_scale = 1
  unit_scheme = 0
FEATURE [Drawing::FeatureViewPython] dim111  # drawing view (typed FeaturePython)
  Rotation = 0
  ViewResult = <g> \n  <line x1="205.000000" y1="154.560000" x2="205.000000" y2="150.747525" style="stroke:rgb(0,0,255);stroke-width:0.50" />\n<line x1="197.000000" y1="147.760000" x2="197.000000" y2="152.747525" style="stroke:rgb(0,0,255);stroke-width:0.50" />\n<line x1="205.000000" y1="151.747525" x2="197.000000" y2="151.747525" style="stroke:rgb(0,0,255);stroke-width:0.50" /> \n  <polygon points="197.000000,151.747525 194.000000,150.747525 193.000000,151.747525 194.000000,152.747525" style="fill:rgb(0,0,255);stroke:rgb(0,0,255);stroke-width:0" /><polygon points="205.000000,151.747525 208.000000,152.747525 209.000000,151.747525 208.000000,150.747525" style="fill:rgb(0,0,255);stroke:rgb(0,0,255);stroke-width:0" /> \n  <text x="201.000000" y="149.747525" font-family="inherit" font-size="3.6" fill="rgb(0,0,255)" text-anchor="middle" transform="rotate(0.000000 201.000000,149.747525)" >8</text> </g>
  Visible = false
  X = 0
  Y = 0
  arrowL1 = 3
  arrowL2 = 1
  arrowW = 2
  arrow_scheme = 0
  autoPlaceOffset = 2
  autoPlaceText = true
  click1_x = 200.837
  click1_y = 151.748
  click2_x = 200.837
  click2_y = 151.748
  comma_decimal_place = false
  dimension_line_overshoot = 1
  gap_datum_points = 2
  halfDimension_linear = false
  lineColor = rgb(0,0,255)
  strokeWidth = 0.5
  textFormat_linear = %(value)3.3f
  textRenderer_color = rgb(0,0,255)
  textRenderer_family = inherit
  textRenderer_size = 3.6
  unit_custom_scale = 1
  unit_scheme = 0
FEATURE [Drawing::FeatureViewPython] dim112  # drawing view (typed FeaturePython)
  Rotation = 0
  ViewResult = <g> \n  <line x1="73.000000" y1="156.560000" x2="50.621430" y2="156.560000" style="stroke:rgb(0,0,255);stroke-width:0.50" />\n<line x1="81.000000" y1="145.760000" x2="50.621430" y2="145.760000" style="stroke:rgb(0,0,255);stroke-width:0.50" />\n<line x1="51.621430" y1="156.560000" x2="51.621430" y2="145.760000" style="stroke:rgb(0,0,255);stroke-width:0.50" /> \n  <polygon points="51.621430,145.760000 50.621430,148.760000 51.621430,149.760000 52.621430,148.760000" style="fill:rgb(0,0,255);stroke:rgb(0,0,255);stroke-width:0" /><polygon points="51.621430,156.560000 52.621430,153.560000 51.621430,152.560000 50.621430,153.560000" style="fill:rgb(0,0,255);stroke:rgb(0,0,255);stroke-width:0" /> \n  <text x="49.621430" y="151.160000" font-family="inherit" font-size="3.6" fill="rgb(0,0,255)" text-anchor="middle" transform="rotate(-90.000000 49.621430,151.160000)" >10.8</text> </g>
  Visible = false
  X = 0
  Y = 0
  arrowL1 = 3
  arrowL2 = 1
  arrowW = 2
  arrow_scheme = 0
  autoPlaceOffset = 2
  autoPlaceText = true
  click1_x = 51.6214
  click1_y = 152.722
  click2_x = 51.6214
  click2_y = 152.722
  comma_decimal_place = false
  dimension_line_overshoot = 1
  gap_datum_points = 2
  halfDimension_linear = false
  lineColor = rgb(0,0,255)
  strokeWidth = 0.5
  textFormat_linear = %(value)3.3f
  textRenderer_color = rgb(0,0,255)
  textRenderer_family = inherit
  textRenderer_size = 3.6
  unit_custom_scale = 1
  unit_scheme = 0
FEATURE [Drawing::FeatureViewPython] dim113  # drawing view (typed FeaturePython)
  Rotation = 0
  ViewResult = <g> \n  <line x1="81.000000" y1="145.760000" x2="50.675541" y2="145.760000" style="stroke:rgb(0,0,255);stroke-width:0.50" />\n<line x1="81.000000" y1="135.760000" x2="50.675541" y2="135.760000" style="stroke:rgb(0,0,255);stroke-width:0.50" />\n<line x1="51.675541" y1="145.760000" x2="51.675541" y2="135.760000" style="stroke:rgb(0,0,255);stroke-width:0.50" /> \n  <polygon points="51.675541,135.760000 52.675541,132.760000 51.675541,131.760000 50.675541,132.760000" style="fill:rgb(0,0,255);stroke:rgb(0,0,255);stroke-width:0" /><polygon points="51.675541,145.760000 50.675541,148.760000 51.675541,149.760000 52.675541,148.760000" style="fill:rgb(0,0,255);stroke:rgb(0,0,255);stroke-width:0" /> \n  <text x="49.675541" y="140.760000" font-family="inherit" font-size="3.6" fill="rgb(0,0,255)" text-anchor="middle" transform="rotate(-90.000000 49.675541,140.760000)" >10</text> </g>
  Visible = false
  X = 0
  Y = 0
  arrowL1 = 3
  arrowL2 = 1
  arrowW = 2
  arrow_scheme = 0
  autoPlaceOffset = 2
  autoPlaceText = true
  click1_x = 51.6755
  click1_y = 134.194
  click2_x = 51.6755
  click2_y = 134.194
  comma_decimal_place = false
  dimension_line_overshoot = 1
  gap_datum_points = 2
  halfDimension_linear = false
  lineColor = rgb(0,0,255)
  strokeWidth = 0.5
  textFormat_linear = %(value)3.3f
  textRenderer_color = rgb(0,0,255)
  textRenderer_family = inherit
  textRenderer_size = 3.6
  unit_custom_scale = 1
  unit_scheme = 0
FEATURE [Drawing::FeatureViewPython] text079  # drawing view (typed FeaturePython)
  Rotation = 0
  ViewResult = <g> <text x="80.552723" y="133.482644" font-family="inherit" font-size="3,6" fill="rgb(0,0,255)" text-anchor="inherit" transform="rotate(0.000000 80.552723,133.482644)" >H1</text> </g>
  Visible = false
  X = 0
  Y = 0
  click1_x = 80.5527
  click1_y = 133.483
  rotation = 0
  text = H1
  textRenderer_addText_color = rgb(0,0,255)
  textRenderer_addText_family = inherit
  textRenderer_addText_size = 3,6
FEATURE [Drawing::FeatureViewPython] text080  # drawing view (typed FeaturePython)
  Rotation = 0
  ViewResult = <g> <text x="80.387317" y="144.068628" font-family="inherit" font-size="3,6" fill="rgb(0,0,255)" text-anchor="inherit" transform="rotate(0.000000 80.387317,144.068628)" >H1</text> </g>
  Visible = false
  X = 0
  Y = 0
  click1_x = 80.3873
  click1_y = 144.069
  rotation = 0
  text = H1
  textRenderer_addText_color = rgb(0,0,255)
  textRenderer_addText_family = inherit
  textRenderer_addText_size = 3,6
FEATURE [Drawing::FeatureViewPython] text081  # drawing view (typed FeaturePython)
  Rotation = 0
  ViewResult = <g> <text x="194.682865" y="133.813456" font-family="inherit" font-size="3,6" fill="rgb(0,0,255)" text-anchor="inherit" transform="rotate(0.000000 194.682865,133.813456)" >H1</text> </g>
  Visible = false
  X = 0
  Y = 0
  click1_x = 194.683
  click1_y = 133.813
  rotation = 0
  text = H1
  textRenderer_addText_color = rgb(0,0,255)
  textRenderer_addText_family = inherit
  textRenderer_addText_size = 3,6
FEATURE [Drawing::FeatureViewPython] text082  # drawing view (typed FeaturePython)
  Rotation = 0
  ViewResult = <g> <text x="194.682865" y="144.399440" font-family="inherit" font-size="3,6" fill="rgb(0,0,255)" text-anchor="inherit" transform="rotate(0.000000 194.682865,144.399440)" >H1</text> </g>
  Visible = false
  X = 0
  Y = 0
  click1_x = 194.683
  click1_y = 144.399
  rotation = 0
  text = H1
  textRenderer_addText_color = rgb(0,0,255)
  textRenderer_addText_family = inherit
  textRenderer_addText_size = 3,6
FEATURE [Drawing::FeatureViewPython] centerLines008  # drawing view (typed FeaturePython)
  Rotation = 0
  ViewResult = <blob: 2092 chars omitted>
  Visible = true
  X = 0
  Y = 0
  centerLine_color = rgb(0,0,255)
  centerLine_len_dash = 6
  centerLine_len_dot = 3
  centerLine_len_gap = 2
  centerLine_width = 0.32
  click1_x = 139.752
  click1_y = 53.8358
  click2_x = 139.752
  click2_y = 53.8358
FEATURE [Drawing::FeatureViewPython] centerLines009  # drawing view (typed FeaturePython)
  Rotation = 0
  ViewResult = <blob: 2040 chars omitted>
  Visible = true
  X = 0
  Y = 0
  centerLine_color = rgb(0,0,255)
  centerLine_len_dash = 6
  centerLine_len_dot = 3
  centerLine_len_gap = 2
  centerLine_width = 0.32
  click1_x = 264.017
  click1_y = 188.057
  click2_x = 264.017
  click2_y = 188.057
FEATURE [Drawing::FeatureViewPython] centerLines010  # drawing view (typed FeaturePython)
  Rotation = 0
  ViewResult = <g transform="scale(1.200000,1.200000)" stroke="rgb(0,0,255)"  stroke-width="0.266667" > <path d="M 116.666667,153.583333 L 114.166667,153.583333 M 112.500000,153.583333 L 107.500000,153.583333 M 105.833333,153.583333 L 103.333333,153.583333 M 101.666667,153.583333 L 96.666667,153.583333 M 95.000000,153.583333 L 92.500000,153.583333 M 90.833333,153.583333 L 85.833333,153.583333 M 84.166667,153.583333 L 81.666667,153.583333 M 80.000000,153.583333 L 75.000000,153.583333 M 73.333333,153.583333 L 70.833333,153.583333 M 69.166667,153.583333 L 64.166667,153.583333 M 62.500000,153.583333 L 60.000000,153.583333 M 58.333333,153.583333 L 53.333333,153.583333 M 51.666667,153.583333 L 49.166667,153.583333 M 47.500000,153.583333 L 42.500000,153.583333 M 40.833333,153.583333 L 38.333333,153.583333 M 36.666667,153.583333 L 31.666667,153.583333 M 30.000000,153.583333 L 27.500000,153.583333 M 25.833333,153.583333 L 23.968004,153.583333 "/>\n<path d="M 116.666667,153.583333 L 114.166667,153.583333 M 112.500000,153.583333 L 107.500000,153.583333 M 105.833333,153.583333 L 103.333333,153.583333 M 101.666667,153.583333 L 96.666667,153.583333 M 95.000000,153.583333 L 92.500000,153.583333 M 90.833333,153.583333 L 85.833333,153.583333 M 84.166667,153.583333 L 81.666667,153.583333 M 80.000000,153.583333 L 75.000000,153.583333 M 73.333333,153.583333 L 70.833333,153.583333 M 69.166667,153.583333 L 64.166667,153.583333 M 62.500000,153.583333 L 60.000000,153.583333 M 58.333333,153.583333 L 53.333333,153.583333 M 51.666667,153.583333 L 49.166667,153.583333 M 47.500000,153.583333 L 42.500000,153.583333 M 40.833333,153.583333 L 38.333333,153.583333 M 36.666667,153.583333 L 31.666667,153.583333 M 30.000000,153.583333 L 27.500000,153.583333 M 25.833333,153.583333 L 23.968004,153.583333 "/> </g> 
  Visible = true
  X = 0
  Y = 0
  centerLine_color = rgb(0,0,255)
  centerLine_len_dash = 6
  centerLine_len_dot = 3
  centerLine_len_gap = 2
  centerLine_width = 0.32
  click1_x = 28.7616
  click1_y = 179.576
  click2_x = 28.7616
  click2_y = 179.576
FEATURE [Drawing::FeatureViewPython] dim114  # drawing view (typed FeaturePython)
  Rotation = 0
  ViewResult = <g> \n  <line x1="54.000000" y1="129.100000" x2="49.491603" y2="129.100000" style="stroke:rgb(0,0,255);stroke-width:0.50" />\n<line x1="109.200000" y1="184.300000" x2="49.491603" y2="184.300000" style="stroke:rgb(0,0,255);stroke-width:0.50" />\n<line x1="50.491603" y1="129.100000" x2="50.491603" y2="184.300000" style="stroke:rgb(0,0,255);stroke-width:0.50" /> \n  <polygon points="50.491603,184.300000 51.491603,181.300000 50.491603,180.300000 49.491603,181.300000" style="fill:rgb(0,0,255);stroke:rgb(0,0,255);stroke-width:0" /><polygon points="50.491603,129.100000 49.491603,132.100000 50.491603,133.100000 51.491603,132.100000" style="fill:rgb(0,0,255);stroke:rgb(0,0,255);stroke-width:0" /> \n  <text x="48.491603" y="156.700000" font-family="inherit" font-size="3.6" fill="rgb(0,0,255)" text-anchor="middle" transform="rotate(-90.000000 48.491603,156.700000)" >46</text> </g>
  Visible = true
  X = 0
  Y = 0
  arrowL1 = 3
  arrowL2 = 1
  arrowW = 2
  arrow_scheme = 0
  autoPlaceOffset = 2
  autoPlaceText = true
  click1_x = 50.4916
  click1_y = 156.861
  click2_x = 50.4916
  click2_y = 156.861
  comma_decimal_place = false
  dimension_line_overshoot = 1
  gap_datum_points = 2
  halfDimension_linear = false
  lineColor = rgb(0,0,255)
  strokeWidth = 0.5
  textFormat_linear = %(value)3.3f
  textRenderer_color = rgb(0,0,255)
  textRenderer_family = inherit
  textRenderer_size = 3.6
  unit_custom_scale = 1
  unit_scheme = 0
FEATURE [Drawing::FeatureViewPython] dim115  # drawing view (typed FeaturePython)
  Rotation = 0
  ViewResult = <g> \n  <line x1="60.000000" y1="114.700000" x2="42.787700" y2="114.700000" style="stroke:rgb(0,0,255);stroke-width:0.50" />\n<line x1="109.200000" y1="184.300000" x2="42.787700" y2="184.300000" style="stroke:rgb(0,0,255);stroke-width:0.50" />\n<line x1="43.787700" y1="114.700000" x2="43.787700" y2="184.300000" style="stroke:rgb(0,0,255);stroke-width:0.50" /> \n  <polygon points="43.787700,184.300000 44.787700,181.300000 43.787700,180.300000 42.787700,181.300000" style="fill:rgb(0,0,255);stroke:rgb(0,0,255);stroke-width:0" /><polygon points="43.787700,114.700000 42.787700,117.700000 43.787700,118.700000 44.787700,117.700000" style="fill:rgb(0,0,255);stroke:rgb(0,0,255);stroke-width:0" /> \n  <text x="41.787700" y="149.500000" font-family="inherit" font-size="3.6" fill="rgb(0,0,255)" text-anchor="middle" transform="rotate(-90.000000 41.787700,149.500000)" >58</text> </g>
  Visible = true
  X = 0
  Y = 0
  arrowL1 = 3
  arrowL2 = 1
  arrowW = 2
  arrow_scheme = 0
  autoPlaceOffset = 2
  autoPlaceText = true
  click1_x = 43.7877
  click1_y = 163.116
  click2_x = 43.7877
  click2_y = 163.116
  comma_decimal_place = false
  dimension_line_overshoot = 1
  gap_datum_points = 2
  halfDimension_linear = false
  lineColor = rgb(0,0,255)
  strokeWidth = 0.5
  textFormat_linear = %(value)3.3f
  textRenderer_color = rgb(0,0,255)
  textRenderer_family = inherit
  textRenderer_size = 3.6
  unit_custom_scale = 1
  unit_scheme = 0
FEATURE [Drawing::FeatureViewPython] dim116  # drawing view (typed FeaturePython)
  Rotation = 0
  ViewResult = <g> \n  <line x1="60.000000" y1="114.700000" x2="42.735966" y2="114.700000" style="stroke:rgb(0,0,255);stroke-width:0.50" />\n<line x1="60.000000" y1="96.700000" x2="42.735966" y2="96.700000" style="stroke:rgb(0,0,255);stroke-width:0.50" />\n<line x1="43.735966" y1="114.700000" x2="43.735966" y2="96.700000" style="stroke:rgb(0,0,255);stroke-width:0.50" /> \n  <polygon points="43.735966,96.700000 42.735966,99.700000 43.735966,100.700000 44.735966,99.700000" style="fill:rgb(0,0,255);stroke:rgb(0,0,255);stroke-width:0" /><polygon points="43.735966,114.700000 44.735966,111.700000 43.735966,110.700000 42.735966,111.700000" style="fill:rgb(0,0,255);stroke:rgb(0,0,255);stroke-width:0" /> \n  <text x="41.735966" y="105.700000" font-family="inherit" font-size="3.6" fill="rgb(0,0,255)" text-anchor="middle" transform="rotate(-90.000000 41.735966,105.700000)" >15</text> </g>
  Visible = true
  X = 0
  Y = 0
  arrowL1 = 3
  arrowL2 = 1
  arrowW = 2
  arrow_scheme = 0
  autoPlaceOffset = 2
  autoPlaceText = true
  click1_x = 43.736
  click1_y = 102.265
  click2_x = 43.736
  click2_y = 102.265
  comma_decimal_place = false
  dimension_line_overshoot = 1
  gap_datum_points = 2
  halfDimension_linear = false
  lineColor = rgb(0,0,255)
  strokeWidth = 0.5
  textFormat_linear = %(value)3.3f
  textRenderer_color = rgb(0,0,255)
  textRenderer_family = inherit
  textRenderer_size = 3.6
  unit_custom_scale = 1
  unit_scheme = 0
FEATURE [Drawing::FeatureViewPython] dim117  # drawing view (typed FeaturePython)
  Rotation = 0
  ViewResult = <g> \n  <line x1="54.000000" y1="72.700000" x2="27.423595" y2="72.700000" style="stroke:rgb(0,0,255);stroke-width:0.50" />\n<line x1="26.761605" y1="184.300000" x2="27.423595" y2="184.300000" style="stroke:rgb(0,0,255);stroke-width:0.50" />\n<line x1="28.423595" y1="72.700000" x2="28.423595" y2="184.300000" style="stroke:rgb(0,0,255);stroke-width:0.50" /> \n  <polygon points="28.423595,184.300000 29.423595,181.300000 28.423595,180.300000 27.423595,181.300000" style="fill:rgb(0,0,255);stroke:rgb(0,0,255);stroke-width:0" /><polygon points="28.423595,72.700000 27.423595,75.700000 28.423595,76.700000 29.423595,75.700000" style="fill:rgb(0,0,255);stroke:rgb(0,0,255);stroke-width:0" /> \n  <text x="26.423595" y="128.500000" font-family="inherit" font-size="3.6" fill="rgb(0,0,255)" text-anchor="middle" transform="rotate(-90.000000 26.423595,128.500000)" >93</text> </g>
  Visible = true
  X = 0
  Y = 0
  arrowL1 = 3
  arrowL2 = 1
  arrowW = 2
  arrow_scheme = 0
  autoPlaceOffset = 2
  autoPlaceText = true
  click1_x = 28.4236
  click1_y = 82.198
  click2_x = 28.4236
  click2_y = 82.198
  comma_decimal_place = false
  dimension_line_overshoot = 1
  gap_datum_points = 2
  halfDimension_linear = false
  lineColor = rgb(0,0,255)
  strokeWidth = 0.5
  textFormat_linear = %(value)3.3f
  textRenderer_color = rgb(0,0,255)
  textRenderer_family = inherit
  textRenderer_size = 3.6
  unit_custom_scale = 1
  unit_scheme = 0
FEATURE [Drawing::FeatureViewPython] dim118  # drawing view (typed FeaturePython)
  Rotation = 0
  ViewResult = <g> \n  <line x1="111.200000" y1="186.300000" x2="111.200000" y2="196.124138" style="stroke:rgb(0,0,255);stroke-width:0.50" />\n<line x1="168.800000" y1="186.300000" x2="168.800000" y2="196.124138" style="stroke:rgb(0,0,255);stroke-width:0.50" />\n<line x1="111.200000" y1="195.124138" x2="168.800000" y2="195.124138" style="stroke:rgb(0,0,255);stroke-width:0.50" /> \n  <polygon points="168.800000,195.124138 165.800000,194.124138 164.800000,195.124138 165.800000,196.124138" style="fill:rgb(0,0,255);stroke:rgb(0,0,255);stroke-width:0" /><polygon points="111.200000,195.124138 114.200000,196.124138 115.200000,195.124138 114.200000,194.124138" style="fill:rgb(0,0,255);stroke:rgb(0,0,255);stroke-width:0" /> \n  <text x="140.000000" y="193.124138" font-family="inherit" font-size="3.6" fill="rgb(0,0,255)" text-anchor="middle" transform="rotate(0.000000 140.000000,193.124138)" >48</text> </g>
  Visible = true
  X = 0
  Y = 0
  arrowL1 = 3
  arrowL2 = 1
  arrowW = 2
  arrow_scheme = 0
  autoPlaceOffset = 2
  autoPlaceText = true
  click1_x = 169.005
  click1_y = 195.124
  click2_x = 169.005
  click2_y = 195.124
  comma_decimal_place = false
  dimension_line_overshoot = 1
  gap_datum_points = 2
  halfDimension_linear = false
  lineColor = rgb(0,0,255)
  strokeWidth = 0.5
  textFormat_linear = %(value)3.3f
  textRenderer_color = rgb(0,0,255)
  textRenderer_family = inherit
  textRenderer_size = 3.6
  unit_custom_scale = 1
  unit_scheme = 0
FEATURE [Drawing::FeatureViewPython] rad009  # drawing view (typed FeaturePython)
  Rotation = 0
  ViewResult = <g>  <circle cx ="168.800000" cy ="129.100000" r="0.250000" stroke="none" fill="rgb(0,0,255)" /> \n<line x1="207.688792" y1="174.027724" x2="168.800000" y2="129.100000" style="stroke:rgb(0,0,255);stroke-width:0.50" />\n<polygon points="204.926393,170.836360 203.719096,167.913616 202.308539,167.811986 202.206909,169.222543" style="fill:rgb(0,0,255);stroke:rgb(0,0,255);stroke-width:0" />\n<line x1="207.688792" y1="174.027724" x2="219.806777" y2="174.027724" style="stroke:rgb(0,0,255);stroke-width:0.50" />\n<text x="213.747784" y="172.027724" font-family="inherit" font-size="3.6" fill="rgb(0,0,255)" text-anchor="middle" transform="rotate(0.000000 213.747784,172.027724)" >R46</text> </g>
  Visible = true
  X = 0
  Y = 0
  arrowL1 = 3
  arrowL2 = 1
  arrowW = 2
  arrow_scheme = 0
  autoPlaceOffset = 2
  autoPlaceText = true
  centerPointDia = 0.5
  click1_x = 207.689
  click1_y = 174.028
  click2_x = 219.807
  click2_y = 177.394
  click3_x = 219.807
  click3_y = 177.394
  comma_decimal_place = false
  lineColor = rgb(0,0,255)
  strokeWidth = 0.5
  textFormat_radial = R%(value)3.3f
  textRenderer_color = rgb(0,0,255)
  textRenderer_family = inherit
  textRenderer_size = 3.6
  unit_custom_scale = 1
  unit_scheme = 0
FEATURE [Drawing::FeatureViewPython] dim122  # drawing view (typed FeaturePython)
  Rotation = 0
  ViewResult = <g> \n  <line x1="62.000000" y1="94.700000" x2="62.000000" y2="82.973055" style="stroke:rgb(0,0,255);stroke-width:0.50" />\n<line x1="56.000000" y1="74.700000" x2="56.000000" y2="84.973055" style="stroke:rgb(0,0,255);stroke-width:0.50" />\n<line x1="62.000000" y1="83.973055" x2="56.000000" y2="83.973055" style="stroke:rgb(0,0,255);stroke-width:0.50" /> \n  <polygon points="56.000000,83.973055 53.000000,82.973055 52.000000,83.973055 53.000000,84.973055" style="fill:rgb(0,0,255);stroke:rgb(0,0,255);stroke-width:0" /><polygon points="62.000000,83.973055 65.000000,84.973055 66.000000,83.973055 65.000000,82.973055" style="fill:rgb(0,0,255);stroke:rgb(0,0,255);stroke-width:0" /> \n  <text x="59.000000" y="81.973055" font-family="inherit" font-size="3.6" fill="rgb(0,0,255)" text-anchor="middle" transform="rotate(0.000000 59.000000,81.973055)" >5</text> </g>
  Visible = true
  X = 0
  Y = 0
  arrowL1 = 3
  arrowL2 = 1
  arrowW = 2
  arrow_scheme = 0
  autoPlaceOffset = 2
  autoPlaceText = true
  click1_x = 61.5391
  click1_y = 83.9731
  click2_x = 61.5391
  click2_y = 83.9731
  comma_decimal_place = false
  dimension_line_overshoot = 1
  gap_datum_points = 2
  halfDimension_linear = false
  lineColor = rgb(0,0,255)
  strokeWidth = 0.5
  textFormat_linear = %(value)3.3f
  textRenderer_color = rgb(0,0,255)
  textRenderer_family = inherit
  textRenderer_size = 3.6
  unit_custom_scale = 1
  unit_scheme = 0
FEATURE [Drawing::FeatureViewPython] dim123  # drawing view (typed FeaturePython)
  Rotation = 0
  ViewResult = <g> \n  <line x1="218.000000" y1="94.700000" x2="218.000000" y2="82.568277" style="stroke:rgb(0,0,255);stroke-width:0.50" />\n<line x1="224.000000" y1="74.700000" x2="224.000000" y2="84.568277" style="stroke:rgb(0,0,255);stroke-width:0.50" />\n<line x1="218.000000" y1="83.568277" x2="224.000000" y2="83.568277" style="stroke:rgb(0,0,255);stroke-width:0.50" /> \n  <polygon points="224.000000,83.568277 227.000000,84.568277 228.000000,83.568277 227.000000,82.568277" style="fill:rgb(0,0,255);stroke:rgb(0,0,255);stroke-width:0" /><polygon points="218.000000,83.568277 215.000000,82.568277 214.000000,83.568277 215.000000,84.568277" style="fill:rgb(0,0,255);stroke:rgb(0,0,255);stroke-width:0" /> \n  <text x="221.000000" y="81.568277" font-family="inherit" font-size="3.6" fill="rgb(0,0,255)" text-anchor="middle" transform="rotate(0.000000 221.000000,81.568277)" >5</text> </g>
  Visible = true
  X = 0
  Y = 0
  arrowL1 = 3
  arrowL2 = 1
  arrowW = 2
  arrow_scheme = 0
  autoPlaceOffset = 2
  autoPlaceText = true
  click1_x = 219.148
  click1_y = 83.5683
  click2_x = 219.148
  click2_y = 83.5683
  comma_decimal_place = false
  dimension_line_overshoot = 1
  gap_datum_points = 2
  halfDimension_linear = false
  lineColor = rgb(0,0,255)
  strokeWidth = 0.5
  textFormat_linear = %(value)3.3f
  textRenderer_color = rgb(0,0,255)
  textRenderer_family = inherit
  textRenderer_size = 3.6
  unit_custom_scale = 1
  unit_scheme = 0
FEATURE [Drawing::FeatureViewPython] dim126  # drawing view (typed FeaturePython)
  Rotation = 0
  ViewResult = <g> \n  <line x1="85.600000" y1="134.680000" x2="90.474914" y2="134.680000" style="stroke:rgb(0,0,255);stroke-width:0.50" />\n<line x1="85.600000" y1="146.680000" x2="90.474914" y2="146.680000" style="stroke:rgb(0,0,255);stroke-width:0.50" />\n<line x1="89.474914" y1="134.680000" x2="89.474914" y2="146.680000" style="stroke:rgb(0,0,255);stroke-width:0.50" /> \n  <polygon points="89.474914,146.680000 90.474914,143.680000 89.474914,142.680000 88.474914,143.680000" style="fill:rgb(0,0,255);stroke:rgb(0,0,255);stroke-width:0" /><polygon points="89.474914,134.680000 88.474914,137.680000 89.474914,138.680000 90.474914,137.680000" style="fill:rgb(0,0,255);stroke:rgb(0,0,255);stroke-width:0" /> \n  <text x="87.474914" y="140.680000" font-family="inherit" font-size="3.6" fill="rgb(0,0,255)" text-anchor="middle" transform="rotate(-90.000000 87.474914,140.680000)" >10</text> </g>
  Visible = true
  X = 0
  Y = 0
  arrowL1 = 3
  arrowL2 = 1
  arrowW = 2
  arrow_scheme = 0
  autoPlaceOffset = 2
  autoPlaceText = true
  click1_x = 89.4749
  click1_y = 146.467
  click2_x = 89.4749
  click2_y = 146.467
  comma_decimal_place = false
  dimension_line_overshoot = 1
  gap_datum_points = 2
  halfDimension_linear = false
  lineColor = rgb(0,0,255)
  strokeWidth = 0.5
  textFormat_linear = %(value)3.3f
  textRenderer_color = rgb(0,0,255)
  textRenderer_family = inherit
  textRenderer_size = 3.6
  unit_custom_scale = 1
  unit_scheme = 0
FEATURE [Drawing::FeatureViewPython] dim127  # drawing view (typed FeaturePython)
  Rotation = 0
  ViewResult = <g> \n  <line x1="194.400000" y1="134.680000" x2="189.949886" y2="134.680000" style="stroke:rgb(0,0,255);stroke-width:0.50" />\n<line x1="194.400000" y1="146.680000" x2="189.949886" y2="146.680000" style="stroke:rgb(0,0,255);stroke-width:0.50" />\n<line x1="190.949886" y1="134.680000" x2="190.949886" y2="146.680000" style="stroke:rgb(0,0,255);stroke-width:0.50" /> \n  <polygon points="190.949886,146.680000 191.949886,143.680000 190.949886,142.680000 189.949886,143.680000" style="fill:rgb(0,0,255);stroke:rgb(0,0,255);stroke-width:0" /><polygon points="190.949886,134.680000 189.949886,137.680000 190.949886,138.680000 191.949886,137.680000" style="fill:rgb(0,0,255);stroke:rgb(0,0,255);stroke-width:0" /> \n  <text x="188.949886" y="140.680000" font-family="inherit" font-size="3.6" fill="rgb(0,0,255)" text-anchor="middle" transform="rotate(-90.000000 188.949886,140.680000)" >10</text> </g>
  Visible = true
  X = 0
  Y = 0
  arrowL1 = 3
  arrowL2 = 1
  arrowW = 2
  arrow_scheme = 0
  autoPlaceOffset = 2
  autoPlaceText = true
  click1_x = 190.95
  click1_y = 145.349
  click2_x = 190.95
  click2_y = 145.349
  comma_decimal_place = false
  dimension_line_overshoot = 1
  gap_datum_points = 2
  halfDimension_linear = false
  lineColor = rgb(0,0,255)
  strokeWidth = 0.5
  textFormat_linear = %(value)3.3f
  textRenderer_color = rgb(0,0,255)
  textRenderer_family = inherit
  textRenderer_size = 3.6
  unit_custom_scale = 1
  unit_scheme = 0
FEATURE [Drawing::FeatureViewPython] dim128  # drawing view (typed FeaturePython)
  Rotation = 0
  ViewResult = <g> \n  <line x1="63.716000" y1="144.528000" x2="63.716000" y2="151.154762" style="stroke:rgb(0,0,255);stroke-width:0.50" />\n<line x1="72.800000" y1="136.680000" x2="72.800000" y2="151.154762" style="stroke:rgb(0,0,255);stroke-width:0.50" />\n<line x1="63.716000" y1="150.154762" x2="72.800000" y2="150.154762" style="stroke:rgb(0,0,255);stroke-width:0.50" /> \n  <polygon points="72.800000,150.154762 75.800000,151.154762 76.800000,150.154762 75.800000,149.154762" style="fill:rgb(0,0,255);stroke:rgb(0,0,255);stroke-width:0" /><polygon points="63.716000,150.154762 60.716000,149.154762 59.716000,150.154762 60.716000,151.154762" style="fill:rgb(0,0,255);stroke:rgb(0,0,255);stroke-width:0" /> \n  <text x="68.258000" y="148.154762" font-family="inherit" font-size="3.6" fill="rgb(0,0,255)" text-anchor="middle" transform="rotate(0.000000 68.258000,148.154762)" >7.57</text> </g>
  Visible = true
  X = 0
  Y = 0
  arrowL1 = 3
  arrowL2 = 1
  arrowW = 2
  arrow_scheme = 0
  autoPlaceOffset = 2
  autoPlaceText = true
  click1_x = 69.0973
  click1_y = 150.155
  click2_x = 69.0973
  click2_y = 150.155
  comma_decimal_place = false
  dimension_line_overshoot = 1
  gap_datum_points = 2
  halfDimension_linear = false
  lineColor = rgb(0,0,255)
  strokeWidth = 0.5
  textFormat_linear = %(value)3.3f
  textRenderer_color = rgb(0,0,255)
  textRenderer_family = inherit
  textRenderer_size = 3.6
  unit_custom_scale = 1
  unit_scheme = 0
FEATURE [Drawing::FeatureViewPython] dim129  # drawing view (typed FeaturePython)
  Rotation = 0
  ViewResult = <g> \n  <line x1="207.200000" y1="136.680000" x2="207.200000" y2="150.750847" style="stroke:rgb(0,0,255);stroke-width:0.50" />\n<line x1="216.284000" y1="144.528000" x2="216.284000" y2="150.750847" style="stroke:rgb(0,0,255);stroke-width:0.50" />\n<line x1="207.200000" y1="149.750847" x2="216.284000" y2="149.750847" style="stroke:rgb(0,0,255);stroke-width:0.50" /> \n  <polygon points="216.284000,149.750847 219.284000,150.750847 220.284000,149.750847 219.284000,148.750847" style="fill:rgb(0,0,255);stroke:rgb(0,0,255);stroke-width:0" /><polygon points="207.200000,149.750847 204.200000,148.750847 203.200000,149.750847 204.200000,150.750847" style="fill:rgb(0,0,255);stroke:rgb(0,0,255);stroke-width:0" /> \n  <text x="211.742000" y="147.750847" font-family="inherit" font-size="3.6" fill="rgb(0,0,255)" text-anchor="middle" transform="rotate(0.000000 211.742000,147.750847)" >7.57</text> </g>
  Visible = true
  X = 0
  Y = 0
  arrowL1 = 3
  arrowL2 = 1
  arrowW = 2
  arrow_scheme = 0
  autoPlaceOffset = 2
  autoPlaceText = true
  click1_x = 211.166
  click1_y = 149.751
  click2_x = 211.166
  click2_y = 149.751
  comma_decimal_place = false
  dimension_line_overshoot = 1
  gap_datum_points = 2
  halfDimension_linear = false
  lineColor = rgb(0,0,255)
  strokeWidth = 0.5
  textFormat_linear = %(value)3.3f
  textRenderer_color = rgb(0,0,255)
  textRenderer_family = inherit
  textRenderer_size = 3.6
  unit_custom_scale = 1
  unit_scheme = 0
FEATURE [Drawing::FeatureViewPython] dim130  # drawing view (typed FeaturePython)
  Rotation = 0
  ViewResult = <g> \n  <line x1="72.800000" y1="132.680000" x2="72.800000" y2="126.171176" style="stroke:rgb(0,0,255);stroke-width:0.50" />\n<line x1="83.600000" y1="132.680000" x2="83.600000" y2="126.171176" style="stroke:rgb(0,0,255);stroke-width:0.50" />\n<line x1="72.800000" y1="127.171176" x2="83.600000" y2="127.171176" style="stroke:rgb(0,0,255);stroke-width:0.50" /> \n  <polygon points="83.600000,127.171176 80.600000,126.171176 79.600000,127.171176 80.600000,128.171176" style="fill:rgb(0,0,255);stroke:rgb(0,0,255);stroke-width:0" /><polygon points="72.800000,127.171176 75.800000,128.171176 76.800000,127.171176 75.800000,126.171176" style="fill:rgb(0,0,255);stroke:rgb(0,0,255);stroke-width:0" /> \n  <text x="78.200000" y="125.171176" font-family="inherit" font-size="3.6" fill="rgb(0,0,255)" text-anchor="middle" transform="rotate(0.000000 78.200000,125.171176)" >9</text> </g>
  Visible = true
  X = 0
  Y = 0
  arrowL1 = 3
  arrowL2 = 1
  arrowW = 2
  arrow_scheme = 0
  autoPlaceOffset = 2
  autoPlaceText = true
  click1_x = 80.6451
  click1_y = 127.171
  click2_x = 80.6451
  click2_y = 127.171
  comma_decimal_place = false
  dimension_line_overshoot = 1
  gap_datum_points = 2
  halfDimension_linear = false
  lineColor = rgb(0,0,255)
  strokeWidth = 0.5
  textFormat_linear = %(value)3.3f
  textRenderer_color = rgb(0,0,255)
  textRenderer_family = inherit
  textRenderer_size = 3.6
  unit_custom_scale = 1
  unit_scheme = 0
FEATURE [Drawing::FeatureViewPython] dim131  # drawing view (typed FeaturePython)
  Rotation = 0
  ViewResult = <g> \n  <line x1="83.600000" y1="132.680000" x2="83.600000" y2="126.165120" style="stroke:rgb(0,0,255);stroke-width:0.50" />\n<line x1="100.400000" y1="132.680000" x2="100.400000" y2="126.165120" style="stroke:rgb(0,0,255);stroke-width:0.50" />\n<line x1="83.600000" y1="127.165120" x2="100.400000" y2="127.165120" style="stroke:rgb(0,0,255);stroke-width:0.50" /> \n  <polygon points="100.400000,127.165120 97.400000,126.165120 96.400000,127.165120 97.400000,128.165120" style="fill:rgb(0,0,255);stroke:rgb(0,0,255);stroke-width:0" /><polygon points="83.600000,127.165120 86.600000,128.165120 87.600000,127.165120 86.600000,126.165120" style="fill:rgb(0,0,255);stroke:rgb(0,0,255);stroke-width:0" /> \n  <text x="92.000000" y="125.165120" font-family="inherit" font-size="3.6" fill="rgb(0,0,255)" text-anchor="middle" transform="rotate(0.000000 92.000000,125.165120)" >14</text> </g>
  Visible = true
  X = 0
  Y = 0
  arrowL1 = 3
  arrowL2 = 1
  arrowW = 2
  arrow_scheme = 0
  autoPlaceOffset = 2
  autoPlaceText = true
  click1_x = 101.43
  click1_y = 127.165
  click2_x = 101.43
  click2_y = 127.165
  comma_decimal_place = false
  dimension_line_overshoot = 1
  gap_datum_points = 2
  halfDimension_linear = false
  lineColor = rgb(0,0,255)
  strokeWidth = 0.5
  textFormat_linear = %(value)3.3f
  textRenderer_color = rgb(0,0,255)
  textRenderer_family = inherit
  textRenderer_size = 3.6
  unit_custom_scale = 1
  unit_scheme = 0
FEATURE [Drawing::FeatureViewPython] dim132  # drawing view (typed FeaturePython)
  Rotation = 0
  ViewResult = <g> \n  <line x1="179.600000" y1="132.680000" x2="179.600000" y2="126.122334" style="stroke:rgb(0,0,255);stroke-width:0.50" />\n<line x1="196.400000" y1="132.680000" x2="196.400000" y2="126.122334" style="stroke:rgb(0,0,255);stroke-width:0.50" />\n<line x1="179.600000" y1="127.122334" x2="196.400000" y2="127.122334" style="stroke:rgb(0,0,255);stroke-width:0.50" /> \n  <polygon points="196.400000,127.122334 193.400000,126.122334 192.400000,127.122334 193.400000,128.122334" style="fill:rgb(0,0,255);stroke:rgb(0,0,255);stroke-width:0" /><polygon points="179.600000,127.122334 182.600000,128.122334 183.600000,127.122334 182.600000,126.122334" style="fill:rgb(0,0,255);stroke:rgb(0,0,255);stroke-width:0" /> \n  <text x="188.000000" y="125.122334" font-family="inherit" font-size="3.6" fill="rgb(0,0,255)" text-anchor="middle" transform="rotate(0.000000 188.000000,125.122334)" >14</text> </g>
  Visible = true
  X = 0
  Y = 0
  arrowL1 = 3
  arrowL2 = 1
  arrowW = 2
  arrow_scheme = 0
  autoPlaceOffset = 2
  autoPlaceText = true
  click1_x = 193.809
  click1_y = 127.122
  click2_x = 193.809
  click2_y = 127.122
  comma_decimal_place = false
  dimension_line_overshoot = 1
  gap_datum_points = 2
  halfDimension_linear = false
  lineColor = rgb(0,0,255)
  strokeWidth = 0.5
  textFormat_linear = %(value)3.3f
  textRenderer_color = rgb(0,0,255)
  textRenderer_family = inherit
  textRenderer_size = 3.6
  unit_custom_scale = 1
  unit_scheme = 0
FEATURE [Drawing::FeatureViewPython] dim133  # drawing view (typed FeaturePython)
  Rotation = 0
  ViewResult = <g> \n  <line x1="196.400000" y1="132.680000" x2="196.400000" y2="126.190289" style="stroke:rgb(0,0,255);stroke-width:0.50" />\n<line x1="207.200000" y1="132.680000" x2="207.200000" y2="126.190289" style="stroke:rgb(0,0,255);stroke-width:0.50" />\n<line x1="196.400000" y1="127.190289" x2="207.200000" y2="127.190289" style="stroke:rgb(0,0,255);stroke-width:0.50" /> \n  <polygon points="207.200000,127.190289 204.200000,126.190289 203.200000,127.190289 204.200000,128.190289" style="fill:rgb(0,0,255);stroke:rgb(0,0,255);stroke-width:0" /><polygon points="196.400000,127.190289 199.400000,128.190289 200.400000,127.190289 199.400000,126.190289" style="fill:rgb(0,0,255);stroke:rgb(0,0,255);stroke-width:0" /> \n  <text x="201.800000" y="125.190289" font-family="inherit" font-size="3.6" fill="rgb(0,0,255)" text-anchor="middle" transform="rotate(0.000000 201.800000,125.190289)" >9</text> </g>
  Visible = true
  X = 0
  Y = 0
  arrowL1 = 3
  arrowL2 = 1
  arrowW = 2
  arrow_scheme = 0
  autoPlaceOffset = 2
  autoPlaceText = true
  click1_x = 208.209
  click1_y = 127.19
  click2_x = 208.209
  click2_y = 127.19
  comma_decimal_place = false
  dimension_line_overshoot = 1
  gap_datum_points = 2
  halfDimension_linear = false
  lineColor = rgb(0,0,255)
  strokeWidth = 0.5
  textFormat_linear = %(value)3.3f
  textRenderer_color = rgb(0,0,255)
  textRenderer_family = inherit
  textRenderer_size = 3.6
  unit_custom_scale = 1
  unit_scheme = 0
FEATURE [Drawing::FeatureViewPython] dim134  # drawing view (typed FeaturePython)
  Rotation = 0
  ViewResult = <g> \n  <line x1="209.200000" y1="134.680000" x2="232.160115" y2="134.680000" style="stroke:rgb(0,0,255);stroke-width:0.50" />\n<line x1="218.284000" y1="142.528000" x2="232.160115" y2="142.528000" style="stroke:rgb(0,0,255);stroke-width:0.50" />\n<line x1="231.160115" y1="134.680000" x2="231.160115" y2="142.528000" style="stroke:rgb(0,0,255);stroke-width:0.50" /> \n  <polygon points="231.160115,142.528000 230.160115,145.528000 231.160115,146.528000 232.160115,145.528000" style="fill:rgb(0,0,255);stroke:rgb(0,0,255);stroke-width:0" /><polygon points="231.160115,134.680000 232.160115,131.680000 231.160115,130.680000 230.160115,131.680000" style="fill:rgb(0,0,255);stroke:rgb(0,0,255);stroke-width:0" /> \n  <text x="229.160115" y="138.604000" font-family="inherit" font-size="3.6" fill="rgb(0,0,255)" text-anchor="middle" transform="rotate(-90.000000 229.160115,138.604000)" >6.54</text> </g>
  Visible = true
  X = 0
  Y = 0
  arrowL1 = 3
  arrowL2 = 1
  arrowW = 2
  arrow_scheme = 0
  autoPlaceOffset = 2
  autoPlaceText = true
  click1_x = 231.16
  click1_y = 137.819
  click2_x = 231.16
  click2_y = 137.819
  comma_decimal_place = false
  dimension_line_overshoot = 1
  gap_datum_points = 2
  halfDimension_linear = false
  lineColor = rgb(0,0,255)
  strokeWidth = 0.5
  textFormat_linear = %(value)3.3f
  textRenderer_color = rgb(0,0,255)
  textRenderer_family = inherit
  textRenderer_size = 3.6
  unit_custom_scale = 1
  unit_scheme = 0
FEATURE [Drawing::FeatureViewPython] dim135  # drawing view (typed FeaturePython)
  Rotation = 0
  ViewResult = <g> \n  <line x1="61.716000" y1="142.528000" x2="53.564566" y2="142.528000" style="stroke:rgb(0,0,255);stroke-width:0.50" />\n<line x1="70.800000" y1="134.680000" x2="53.564566" y2="134.680000" style="stroke:rgb(0,0,255);stroke-width:0.50" />\n<line x1="54.564566" y1="142.528000" x2="54.564566" y2="134.680000" style="stroke:rgb(0,0,255);stroke-width:0.50" /> \n  <polygon points="54.564566,134.680000 55.564566,131.680000 54.564566,130.680000 53.564566,131.680000" style="fill:rgb(0,0,255);stroke:rgb(0,0,255);stroke-width:0" /><polygon points="54.564566,142.528000 53.564566,145.528000 54.564566,146.528000 55.564566,145.528000" style="fill:rgb(0,0,255);stroke:rgb(0,0,255);stroke-width:0" /> \n  <text x="55.817124" y="154.456082" font-family="inherit" font-size="3.6" fill="rgb(0,0,255)" text-anchor="inherit" transform="rotate(-90.000000 55.817124,154.456082)" >6.54</text> </g>
  Visible = true
  X = 0
  Y = 0
  arrowL1 = 3
  arrowL2 = 1
  arrowW = 2
  arrow_scheme = 0
  autoPlaceOffset = 2
  autoPlaceText = false
  click1_x = 54.5646
  click1_y = 142.009
  click2_x = 55.8171
  click2_y = 154.456
  comma_decimal_place = false
  dimension_line_overshoot = 1
  gap_datum_points = 2
  halfDimension_linear = false
  lineColor = rgb(0,0,255)
  strokeWidth = 0.5
  textFormat_linear = %(value)3.3f
  textRenderer_color = rgb(0,0,255)
  textRenderer_family = inherit
  textRenderer_size = 3.6
  unit_custom_scale = 1
  unit_scheme = 0
FEATURE [Drawing::FeatureViewPython] dim136  # drawing view (typed FeaturePython)
  Rotation = 0
  ViewResult = <g> \n  <line x1="167.600000" y1="132.680000" x2="167.600000" y2="126.213297" style="stroke:rgb(0,0,255);stroke-width:0.50" />\n<line x1="140.000000" y1="55.835826" x2="140.000000" y2="128.213297" style="stroke:rgb(0,0,255);stroke-width:0.50" />\n<line x1="167.600000" y1="127.213297" x2="140.000000" y2="127.213297" style="stroke:rgb(0,0,255);stroke-width:0.50" /> \n  <polygon points="140.000000,127.213297 143.000000,128.213297 144.000000,127.213297 143.000000,126.213297" style="fill:rgb(0,0,255);stroke:rgb(0,0,255);stroke-width:0" /><polygon points="167.600000,127.213297 164.600000,126.213297 163.600000,127.213297 164.600000,128.213297" style="fill:rgb(0,0,255);stroke:rgb(0,0,255);stroke-width:0" /> \n  <text x="153.800000" y="125.213297" font-family="inherit" font-size="3.6" fill="rgb(0,0,255)" text-anchor="middle" transform="rotate(0.000000 153.800000,125.213297)" >23</text> </g>
  Visible = true
  X = 0
  Y = 0
  arrowL1 = 3
  arrowL2 = 1
  arrowW = 2
  arrow_scheme = 0
  autoPlaceOffset = 2
  autoPlaceText = true
  click1_x = 150.665
  click1_y = 127.213
  click2_x = 150.665
  click2_y = 127.213
  comma_decimal_place = false
  dimension_line_overshoot = 1
  gap_datum_points = 2
  halfDimension_linear = false
  lineColor = rgb(0,0,255)
  strokeWidth = 0.5
  textFormat_linear = %(value)3.3f
  textRenderer_color = rgb(0,0,255)
  textRenderer_family = inherit
  textRenderer_size = 3.6
  unit_custom_scale = 1
  unit_scheme = 0
FEATURE [Drawing::FeatureViewPython] dim124  # drawing view (typed FeaturePython)
  Rotation = 0
  ViewResult = <g> \n  <line x1="100.400000" y1="132.680000" x2="100.400000" y2="126.212941" style="stroke:rgb(0,0,255);stroke-width:0.50" />\n<line x1="112.400000" y1="132.680000" x2="112.400000" y2="126.212941" style="stroke:rgb(0,0,255);stroke-width:0.50" />\n<line x1="100.400000" y1="127.212941" x2="112.400000" y2="127.212941" style="stroke:rgb(0,0,255);stroke-width:0.50" /> \n  <polygon points="112.400000,127.212941 109.400000,126.212941 108.400000,127.212941 109.400000,128.212941" style="fill:rgb(0,0,255);stroke:rgb(0,0,255);stroke-width:0" /><polygon points="100.400000,127.212941 103.400000,128.212941 104.400000,127.212941 103.400000,126.212941" style="fill:rgb(0,0,255);stroke:rgb(0,0,255);stroke-width:0" /> \n  <text x="106.400000" y="125.212941" font-family="inherit" font-size="3.6" fill="rgb(0,0,255)" text-anchor="middle" transform="rotate(0.000000 106.400000,125.212941)" >10</text> </g>
  Visible = true
  X = 0
  Y = 0
  arrowL1 = 3
  arrowL2 = 1
  arrowW = 2
  arrow_scheme = 0
  autoPlaceOffset = 2
  autoPlaceText = true
  click1_x = 111.493
  click1_y = 127.213
  click2_x = 111.493
  click2_y = 127.213
  comma_decimal_place = false
  dimension_line_overshoot = 1
  gap_datum_points = 2
  halfDimension_linear = false
  lineColor = rgb(0,0,255)
  strokeWidth = 0.5
  textFormat_linear = %(value)3.3f
  textRenderer_color = rgb(0,0,255)
  textRenderer_family = inherit
  textRenderer_size = 3.6
  unit_custom_scale = 1
  unit_scheme = 0
FEATURE [Drawing::FeatureViewPython] dim125  # drawing view (typed FeaturePython)
  Rotation = 0
  ViewResult = <g> \n  <line x1="167.600000" y1="132.680000" x2="167.600000" y2="126.129819" style="stroke:rgb(0,0,255);stroke-width:0.50" />\n<line x1="179.600000" y1="132.680000" x2="179.600000" y2="126.129819" style="stroke:rgb(0,0,255);stroke-width:0.50" />\n<line x1="167.600000" y1="127.129819" x2="179.600000" y2="127.129819" style="stroke:rgb(0,0,255);stroke-width:0.50" /> \n  <polygon points="179.600000,127.129819 176.600000,126.129819 175.600000,127.129819 176.600000,128.129819" style="fill:rgb(0,0,255);stroke:rgb(0,0,255);stroke-width:0" /><polygon points="167.600000,127.129819 170.600000,128.129819 171.600000,127.129819 170.600000,126.129819" style="fill:rgb(0,0,255);stroke:rgb(0,0,255);stroke-width:0" /> \n  <text x="173.600000" y="125.129819" font-family="inherit" font-size="3.6" fill="rgb(0,0,255)" text-anchor="middle" transform="rotate(0.000000 173.600000,125.129819)" >10</text> </g>
  Visible = true
  X = 0
  Y = 0
  arrowL1 = 3
  arrowL2 = 1
  arrowW = 2
  arrow_scheme = 0
  autoPlaceOffset = 2
  autoPlaceText = true
  click1_x = 178.495
  click1_y = 127.13
  click2_x = 178.495
  click2_y = 127.13
  comma_decimal_place = false
  dimension_line_overshoot = 1
  gap_datum_points = 2
  halfDimension_linear = false
  lineColor = rgb(0,0,255)
  strokeWidth = 0.5
  textFormat_linear = %(value)3.3f
  textRenderer_color = rgb(0,0,255)
  textRenderer_family = inherit
  textRenderer_size = 3.6
  unit_custom_scale = 1
  unit_scheme = 0
FEATURE [Drawing::FeatureViewPython] text084  # drawing view (typed FeaturePython)
  Rotation = 0
  ViewResult = <g> <text x="93.852238" y="135.591787" font-family="inherit" font-size="3,6" fill="rgb(0,0,255)" text-anchor="inherit" transform="rotate(0.000000 93.852238,135.591787)" >H1</text> </g>
  Visible = true
  X = 0
  Y = 0
  click1_x = 93.8522
  click1_y = 135.592
  rotation = 0
  text = H1
  textRenderer_addText_color = rgb(0,0,255)
  textRenderer_addText_family = inherit
  textRenderer_addText_size = 3,6
FEATURE [Drawing::FeatureViewPython] text085  # drawing view (typed FeaturePython)
  Rotation = 0
  ViewResult = <g> <text x="76.563668" y="135.468297" font-family="inherit" font-size="3,6" fill="rgb(0,0,255)" text-anchor="inherit" transform="rotate(0.000000 76.563668,135.468297)" >H1</text> </g>
  Visible = true
  X = 0
  Y = 0
  click1_x = 76.5637
  click1_y = 135.468
  rotation = 0
  text = H1
  textRenderer_addText_color = rgb(0,0,255)
  textRenderer_addText_family = inherit
  textRenderer_addText_size = 3,6
FEATURE [Drawing::FeatureViewPython] text086  # drawing view (typed FeaturePython)
  Rotation = 0
  ViewResult = <g> <text x="76.687158" y="147.446806" font-family="inherit" font-size="3,6" fill="rgb(0,0,255)" text-anchor="inherit" transform="rotate(0.000000 76.687158,147.446806)" >H1</text> </g>
  Visible = true
  X = 0
  Y = 0
  click1_x = 76.6872
  click1_y = 147.447
  rotation = 0
  text = H1
  textRenderer_addText_color = rgb(0,0,255)
  textRenderer_addText_family = inherit
  textRenderer_addText_size = 3,6
FEATURE [Drawing::FeatureViewPython] text088  # drawing view (typed FeaturePython)
  Rotation = 0
  ViewResult = <g> <text x="181.900457" y="135.468297" font-family="inherit" font-size="3,6" fill="rgb(0,0,255)" text-anchor="inherit" transform="rotate(0.000000 181.900457,135.468297)" >H1</text> </g>
  Visible = true
  X = 0
  Y = 0
  click1_x = 181.9
  click1_y = 135.468
  rotation = 0
  text = H1
  textRenderer_addText_color = rgb(0,0,255)
  textRenderer_addText_family = inherit
  textRenderer_addText_size = 3,6
FEATURE [Drawing::FeatureViewPython] text089  # drawing view (typed FeaturePython)
  Rotation = 0
  ViewResult = <g> <text x="198.571578" y="135.591787" font-family="inherit" font-size="3,6" fill="rgb(0,0,255)" text-anchor="inherit" transform="rotate(0.000000 198.571578,135.591787)" >H1</text> </g>
  Visible = true
  X = 0
  Y = 0
  click1_x = 198.572
  click1_y = 135.592
  rotation = 0
  text = H1
  textRenderer_addText_color = rgb(0,0,255)
  textRenderer_addText_family = inherit
  textRenderer_addText_size = 3,6
FEATURE [Drawing::FeatureViewPython] text090  # drawing view (typed FeaturePython)
  Rotation = 0
  ViewResult = <g> <text x="198.695068" y="147.323316" font-family="inherit" font-size="3,6" fill="rgb(0,0,255)" text-anchor="inherit" transform="rotate(0.000000 198.695068,147.323316)" >H1</text> </g>
  Visible = true
  X = 0
  Y = 0
  click1_x = 198.695
  click1_y = 147.323
  rotation = 0
  text = H1
  textRenderer_addText_color = rgb(0,0,255)
  textRenderer_addText_family = inherit
  textRenderer_addText_size = 3,6
FEATURE [Drawing::FeatureViewPython] text091  # drawing view (typed FeaturePython)
  Rotation = 0
  ViewResult = <g> <text x="208.821231" y="137.691113" font-family="inherit" font-size="3,6" fill="rgb(0,0,255)" text-anchor="inherit" transform="rotate(0.000000 208.821231,137.691113)" >H1</text> </g>
  Visible = true
  X = 0
  Y = 0
  click1_x = 208.821
  click1_y = 137.691
  rotation = 0
  text = H1
  textRenderer_addText_color = rgb(0,0,255)
  textRenderer_addText_family = inherit
  textRenderer_addText_size = 3,6
FEATURE [Drawing::FeatureViewPython] text092  # drawing view (typed FeaturePython)
  Rotation = 0
  ViewResult = <g> <text x="213.266863" y="140.778358" font-family="inherit" font-size="3,6" fill="rgb(0,0,255)" text-anchor="inherit" transform="rotate(0.000000 213.266863,140.778358)" >H1</text> </g>
  Visible = true
  X = 0
  Y = 0
  click1_x = 213.267
  click1_y = 140.778
  rotation = 0
  text = H1
  textRenderer_addText_color = rgb(0,0,255)
  textRenderer_addText_family = inherit
  textRenderer_addText_size = 3,6
FEATURE [Drawing::FeatureViewPython] text093  # drawing view (typed FeaturePython)
  Rotation = 0
  ViewResult = <g> <text x="66.478669" y="132.957338" font-family="inherit" font-size="3,6" fill="rgb(0,0,255)" text-anchor="inherit" transform="rotate(0.000000 66.478669,132.957338)" >H1</text> </g>
  Visible = true
  X = 0
  Y = 0
  click1_x = 66.4787
  click1_y = 132.957
  rotation = 0
  text = H1
  textRenderer_addText_color = rgb(0,0,255)
  textRenderer_addText_family = inherit
  textRenderer_addText_size = 3,6
FEATURE [Drawing::FeatureViewPython] text094  # drawing view (typed FeaturePython)
  Rotation = 0
  ViewResult = <g> <text x="61.436169" y="140.263817" font-family="inherit" font-size="3,6" fill="rgb(0,0,255)" text-anchor="inherit" transform="rotate(0.000000 61.436169,140.263817)" >H1</text> </g>
  Visible = true
  X = 0
  Y = 0
  click1_x = 61.4362
  click1_y = 140.264
  rotation = 0
  text = H1
  textRenderer_addText_color = rgb(0,0,255)
  textRenderer_addText_family = inherit
  textRenderer_addText_size = 3,6
FEATURE [Drawing::FeatureViewPython] dim120  # drawing view (typed FeaturePython)
  Rotation = 0
  ViewResult = <g> \n  <line x1="68.000000" y1="70.700000" x2="68.000000" y2="43.320407" style="stroke:rgb(0,0,255);stroke-width:0.50" />\n<line x1="212.000000" y1="70.700000" x2="212.000000" y2="43.320407" style="stroke:rgb(0,0,255);stroke-width:0.50" />\n<line x1="68.000000" y1="44.320407" x2="212.000000" y2="44.320407" style="stroke:rgb(0,0,255);stroke-width:0.50" /> \n  <polygon points="212.000000,44.320407 209.000000,43.320407 208.000000,44.320407 209.000000,45.320407" style="fill:rgb(0,0,255);stroke:rgb(0,0,255);stroke-width:0" /><polygon points="68.000000,44.320407 71.000000,45.320407 72.000000,44.320407 71.000000,43.320407" style="fill:rgb(0,0,255);stroke:rgb(0,0,255);stroke-width:0" /> \n  <text x="140.000000" y="42.320407" font-family="inherit" font-size="3.6" fill="rgb(0,0,255)" text-anchor="middle" transform="rotate(0.000000 140.000000,42.320407)" >120</text> </g>
  Visible = true
  X = 0
  Y = 0
  arrowL1 = 3
  arrowL2 = 1
  arrowW = 2
  arrow_scheme = 0
  autoPlaceOffset = 2
  autoPlaceText = true
  click1_x = 202.808
  click1_y = 44.3204
  click2_x = 202.808
  click2_y = 44.3204
  comma_decimal_place = false
  dimension_line_overshoot = 1
  gap_datum_points = 2
  halfDimension_linear = false
  lineColor = rgb(0,0,255)
  strokeWidth = 0.5
  textFormat_linear = %(value)3.3f
  textRenderer_color = rgb(0,0,255)
  textRenderer_family = inherit
  textRenderer_size = 3.6
  unit_custom_scale = 1
  unit_scheme = 0
FEATURE [Drawing::FeatureViewPython] dim121  # drawing view (typed FeaturePython)
  Rotation = 0
  ViewResult = <g> \n  <line x1="212.000000" y1="70.700000" x2="212.000000" y2="43.316511" style="stroke:rgb(0,0,255);stroke-width:0.50" />\n<line x1="224.000000" y1="70.700000" x2="224.000000" y2="43.316511" style="stroke:rgb(0,0,255);stroke-width:0.50" />\n<line x1="212.000000" y1="44.316511" x2="224.000000" y2="44.316511" style="stroke:rgb(0,0,255);stroke-width:0.50" /> \n  <polygon points="224.000000,44.316511 221.000000,43.316511 220.000000,44.316511 221.000000,45.316511" style="fill:rgb(0,0,255);stroke:rgb(0,0,255);stroke-width:0" /><polygon points="212.000000,44.316511 215.000000,45.316511 216.000000,44.316511 215.000000,43.316511" style="fill:rgb(0,0,255);stroke:rgb(0,0,255);stroke-width:0" /> \n  <text x="218.000000" y="42.316511" font-family="inherit" font-size="3.6" fill="rgb(0,0,255)" text-anchor="middle" transform="rotate(0.000000 218.000000,42.316511)" >10</text> </g>
  Visible = true
  X = 0
  Y = 0
  arrowL1 = 3
  arrowL2 = 1
  arrowW = 2
  arrow_scheme = 0
  autoPlaceOffset = 2
  autoPlaceText = true
  click1_x = 225.154
  click1_y = 44.3165
  click2_x = 225.154
  click2_y = 44.3165
  comma_decimal_place = false
  dimension_line_overshoot = 1
  gap_datum_points = 2
  halfDimension_linear = false
  lineColor = rgb(0,0,255)
  strokeWidth = 0.5
  textFormat_linear = %(value)3.3f
  textRenderer_color = rgb(0,0,255)
  textRenderer_family = inherit
  textRenderer_size = 3.6
  unit_custom_scale = 1
  unit_scheme = 0
FEATURE [Drawing::FeatureViewPython] dim137  # drawing view (typed FeaturePython)
  Rotation = 0
  ViewResult = <g> \n  <line x1="68.000000" y1="70.700000" x2="68.000000" y2="43.299837" style="stroke:rgb(0,0,255);stroke-width:0.50" />\n<line x1="56.000000" y1="70.700000" x2="56.000000" y2="43.299837" style="stroke:rgb(0,0,255);stroke-width:0.50" />\n<line x1="68.000000" y1="44.299837" x2="56.000000" y2="44.299837" style="stroke:rgb(0,0,255);stroke-width:0.50" /> \n  <polygon points="56.000000,44.299837 59.000000,45.299837 60.000000,44.299837 59.000000,43.299837" style="fill:rgb(0,0,255);stroke:rgb(0,0,255);stroke-width:0" /><polygon points="68.000000,44.299837 65.000000,43.299837 64.000000,44.299837 65.000000,45.299837" style="fill:rgb(0,0,255);stroke:rgb(0,0,255);stroke-width:0" /> \n  <text x="62.000000" y="42.299837" font-family="inherit" font-size="3.6" fill="rgb(0,0,255)" text-anchor="middle" transform="rotate(-0.000000 62.000000,42.299837)" >10</text> </g>
  Visible = true
  X = 0
  Y = 0
  arrowL1 = 3
  arrowL2 = 1
  arrowW = 2
  arrow_scheme = 0
  autoPlaceOffset = 2
  autoPlaceText = true
  click1_x = 54.0304
  click1_y = 44.2998
  click2_x = 54.0304
  click2_y = 44.2998
  comma_decimal_place = false
  dimension_line_overshoot = 1
  gap_datum_points = 2
  halfDimension_linear = false
  lineColor = rgb(0,0,255)
  strokeWidth = 0.5
  textFormat_linear = %(value)3.3f
  textRenderer_color = rgb(0,0,255)
  textRenderer_family = inherit
  textRenderer_size = 3.6
  unit_custom_scale = 1
  unit_scheme = 0
FEATURE [Drawing::FeatureViewPython] dim150  # drawing view (typed FeaturePython)
  Rotation = 0
  ViewResult = <g> \n  <line x1="168.800000" y1="182.300000" x2="168.800000" y2="165.266650" style="stroke:rgb(0,0,255);stroke-width:0.50" />\n<line x1="177.200000" y1="170.300000" x2="177.200000" y2="165.266650" style="stroke:rgb(0,0,255);stroke-width:0.50" />\n<line x1="168.800000" y1="166.266650" x2="177.200000" y2="166.266650" style="stroke:rgb(0,0,255);stroke-width:0.50" /> \n  <polygon points="177.200000,166.266650 180.200000,167.266650 181.200000,166.266650 180.200000,165.266650" style="fill:rgb(0,0,255);stroke:rgb(0,0,255);stroke-width:0" /><polygon points="168.800000,166.266650 165.800000,165.266650 164.800000,166.266650 165.800000,167.266650" style="fill:rgb(0,0,255);stroke:rgb(0,0,255);stroke-width:0" /> \n  <text x="173.000000" y="164.266650" font-family="inherit" font-size="3.6" fill="rgb(0,0,255)" text-anchor="middle" transform="rotate(0.000000 173.000000,164.266650)" >7</text> </g>
  Visible = true
  X = 0
  Y = 0
  arrowL1 = 3
  arrowL2 = 1
  arrowW = 2
  arrow_scheme = 0
  autoPlaceOffset = 2
  autoPlaceText = true
  click1_x = 175.691
  click1_y = 166.267
  click2_x = 175.691
  click2_y = 166.267
  comma_decimal_place = false
  dimension_line_overshoot = 1
  gap_datum_points = 2
  halfDimension_linear = false
  lineColor = rgb(0,0,255)
  strokeWidth = 0.5
  textFormat_linear = %(value)3.3f
  textRenderer_color = rgb(0,0,255)
  textRenderer_family = inherit
  textRenderer_size = 3.6
  unit_custom_scale = 1
  unit_scheme = 0
FEATURE [Drawing::FeatureViewPython] dim151  # drawing view (typed FeaturePython)
  Rotation = 0
  ViewResult = <g> \n  <line x1="91.200000" y1="175.900000" x2="70.132780" y2="175.900000" style="stroke:rgb(0,0,255);stroke-width:0.50" />\n<line x1="109.200000" y1="184.300000" x2="70.132780" y2="184.300000" style="stroke:rgb(0,0,255);stroke-width:0.50" />\n<line x1="71.132780" y1="175.900000" x2="71.132780" y2="184.300000" style="stroke:rgb(0,0,255);stroke-width:0.50" /> \n  <polygon points="71.132780,184.300000 70.132780,187.300000 71.132780,188.300000 72.132780,187.300000" style="fill:rgb(0,0,255);stroke:rgb(0,0,255);stroke-width:0" /><polygon points="71.132780,175.900000 72.132780,172.900000 71.132780,171.900000 70.132780,172.900000" style="fill:rgb(0,0,255);stroke:rgb(0,0,255);stroke-width:0" /> \n  <text x="69.132780" y="180.100000" font-family="inherit" font-size="3.6" fill="rgb(0,0,255)" text-anchor="middle" transform="rotate(-90.000000 69.132780,180.100000)" >7</text> </g>
  Visible = true
  X = 0
  Y = 0
  arrowL1 = 3
  arrowL2 = 1
  arrowW = 2
  arrow_scheme = 0
  autoPlaceOffset = 2
  autoPlaceText = true
  click1_x = 71.1328
  click1_y = 179.467
  click2_x = 71.1328
  click2_y = 179.467
  comma_decimal_place = false
  dimension_line_overshoot = 1
  gap_datum_points = 2
  halfDimension_linear = false
  lineColor = rgb(0,0,255)
  strokeWidth = 0.5
  textFormat_linear = %(value)3.3f
  textRenderer_color = rgb(0,0,255)
  textRenderer_family = inherit
  textRenderer_size = 3.6
  unit_custom_scale = 1
  unit_scheme = 0
FEATURE [Drawing::FeatureViewPython] dim152  # drawing view (typed FeaturePython)
  Rotation = 0
  ViewResult = <g> \n  <line x1="170.800000" y1="184.300000" x2="205.700074" y2="184.300000" style="stroke:rgb(0,0,255);stroke-width:0.50" />\n<line x1="188.800000" y1="175.900000" x2="205.700074" y2="175.900000" style="stroke:rgb(0,0,255);stroke-width:0.50" />\n<line x1="204.700074" y1="184.300000" x2="204.700074" y2="175.900000" style="stroke:rgb(0,0,255);stroke-width:0.50" /> \n  <polygon points="204.700074,175.900000 205.700074,172.900000 204.700074,171.900000 203.700074,172.900000" style="fill:rgb(0,0,255);stroke:rgb(0,0,255);stroke-width:0" /><polygon points="204.700074,184.300000 203.700074,187.300000 204.700074,188.300000 205.700074,187.300000" style="fill:rgb(0,0,255);stroke:rgb(0,0,255);stroke-width:0" /> \n  <text x="202.700074" y="180.100000" font-family="inherit" font-size="3.6" fill="rgb(0,0,255)" text-anchor="middle" transform="rotate(-90.000000 202.700074,180.100000)" >7</text> </g>
  Visible = true
  X = 0
  Y = 0
  arrowL1 = 3
  arrowL2 = 1
  arrowW = 2
  arrow_scheme = 0
  autoPlaceOffset = 2
  autoPlaceText = true
  click1_x = 204.7
  click1_y = 176.941
  click2_x = 204.7
  click2_y = 176.941
  comma_decimal_place = false
  dimension_line_overshoot = 1
  gap_datum_points = 2
  halfDimension_linear = false
  lineColor = rgb(0,0,255)
  strokeWidth = 0.5
  textFormat_linear = %(value)3.3f
  textRenderer_color = rgb(0,0,255)
  textRenderer_family = inherit
  textRenderer_size = 3.6
  unit_custom_scale = 1
  unit_scheme = 0
FEATURE [Drawing::FeatureViewPython] dim153  # drawing view (typed FeaturePython)
  Rotation = 0
  ViewResult = <g> \n  <line x1="93.200000" y1="170.300000" x2="93.200000" y2="164.938909" style="stroke:rgb(0,0,255);stroke-width:0.50" />\n<line x1="102.800000" y1="170.300000" x2="102.800000" y2="164.938909" style="stroke:rgb(0,0,255);stroke-width:0.50" />\n<line x1="93.200000" y1="165.938909" x2="102.800000" y2="165.938909" style="stroke:rgb(0,0,255);stroke-width:0.50" /> \n  <polygon points="102.800000,165.938909 105.800000,166.938909 106.800000,165.938909 105.800000,164.938909" style="fill:rgb(0,0,255);stroke:rgb(0,0,255);stroke-width:0" /><polygon points="93.200000,165.938909 90.200000,164.938909 89.200000,165.938909 90.200000,166.938909" style="fill:rgb(0,0,255);stroke:rgb(0,0,255);stroke-width:0" /> \n  <text x="98.000000" y="163.938909" font-family="inherit" font-size="3.6" fill="rgb(0,0,255)" text-anchor="middle" transform="rotate(0.000000 98.000000,163.938909)" >8</text> </g>
  Visible = true
  X = 0
  Y = 0
  arrowL1 = 3
  arrowL2 = 1
  arrowW = 2
  arrow_scheme = 0
  autoPlaceOffset = 2
  autoPlaceText = true
  click1_x = 99.9917
  click1_y = 165.939
  click2_x = 99.9917
  click2_y = 165.939
  comma_decimal_place = false
  dimension_line_overshoot = 1
  gap_datum_points = 2
  halfDimension_linear = false
  lineColor = rgb(0,0,255)
  strokeWidth = 0.5
  textFormat_linear = %(value)3.3f
  textRenderer_color = rgb(0,0,255)
  textRenderer_family = inherit
  textRenderer_size = 3.6
  unit_custom_scale = 1
  unit_scheme = 0
FEATURE [Drawing::FeatureViewPython] dim154  # drawing view (typed FeaturePython)
  Rotation = 0
  ViewResult = <g> \n  <line x1="177.200000" y1="170.300000" x2="177.200000" y2="165.277100" style="stroke:rgb(0,0,255);stroke-width:0.50" />\n<line x1="186.800000" y1="170.300000" x2="186.800000" y2="165.277100" style="stroke:rgb(0,0,255);stroke-width:0.50" />\n<line x1="177.200000" y1="166.277100" x2="186.800000" y2="166.277100" style="stroke:rgb(0,0,255);stroke-width:0.50" /> \n  <polygon points="186.800000,166.277100 189.800000,167.277100 190.800000,166.277100 189.800000,165.277100" style="fill:rgb(0,0,255);stroke:rgb(0,0,255);stroke-width:0" /><polygon points="177.200000,166.277100 174.200000,165.277100 173.200000,166.277100 174.200000,167.277100" style="fill:rgb(0,0,255);stroke:rgb(0,0,255);stroke-width:0" /> \n  <text x="182.000000" y="164.277100" font-family="inherit" font-size="3.6" fill="rgb(0,0,255)" text-anchor="middle" transform="rotate(0.000000 182.000000,164.277100)" >8</text> </g>
  Visible = true
  X = 0
  Y = 0
  arrowL1 = 3
  arrowL2 = 1
  arrowW = 2
  arrow_scheme = 0
  autoPlaceOffset = 2
  autoPlaceText = true
  click1_x = 188.71
  click1_y = 166.277
  click2_x = 188.71
  click2_y = 166.277
  comma_decimal_place = false
  dimension_line_overshoot = 1
  gap_datum_points = 2
  halfDimension_linear = false
  lineColor = rgb(0,0,255)
  strokeWidth = 0.5
  textFormat_linear = %(value)3.3f
  textRenderer_color = rgb(0,0,255)
  textRenderer_family = inherit
  textRenderer_size = 3.6
  unit_custom_scale = 1
  unit_scheme = 0
FEATURE [Drawing::FeatureViewPython] dim156  # drawing view (typed FeaturePython)
  Rotation = 0
  ViewResult = <g> \n  <line x1="175.200000" y1="172.300000" x2="173.055486" y2="172.300000" style="stroke:rgb(0,0,255);stroke-width:0.50" />\n<line x1="175.200000" y1="175.900000" x2="173.055486" y2="175.900000" style="stroke:rgb(0,0,255);stroke-width:0.50" />\n<line x1="174.055486" y1="172.300000" x2="174.055486" y2="175.900000" style="stroke:rgb(0,0,255);stroke-width:0.50" /> \n  <polygon points="174.055486,175.900000 173.055486,178.900000 174.055486,179.900000 175.055486,178.900000" style="fill:rgb(0,0,255);stroke:rgb(0,0,255);stroke-width:0" /><polygon points="174.055486,172.300000 175.055486,169.300000 174.055486,168.300000 173.055486,169.300000" style="fill:rgb(0,0,255);stroke:rgb(0,0,255);stroke-width:0" /> \n  <text x="172.055486" y="174.100000" font-family="inherit" font-size="3.6" fill="rgb(0,0,255)" text-anchor="middle" transform="rotate(-90.000000 172.055486,174.100000)" >3</text> </g>
  Visible = true
  X = 0
  Y = 0
  arrowL1 = 3
  arrowL2 = 1
  arrowW = 2
  arrow_scheme = 0
  autoPlaceOffset = 2
  autoPlaceText = true
  click1_x = 174.055
  click1_y = 176.085
  click2_x = 174.055
  click2_y = 176.085
  comma_decimal_place = false
  dimension_line_overshoot = 1
  gap_datum_points = 2
  halfDimension_linear = false
  lineColor = rgb(0,0,255)
  strokeWidth = 0.5
  textFormat_linear = %(value)3.3f
  textRenderer_color = rgb(0,0,255)
  textRenderer_family = inherit
  textRenderer_size = 3.6
  unit_custom_scale = 1
  unit_scheme = 0
FEATURE [Drawing::FeatureViewPython] dim157  # drawing view (typed FeaturePython)
  Rotation = 0
  ViewResult = <g> \n  <line x1="66.000000" y1="129.100000" x2="35.361716" y2="129.100000" style="stroke:rgb(0,0,255);stroke-width:0.50" />\n<line x1="66.000000" y1="72.700000" x2="35.361716" y2="72.700000" style="stroke:rgb(0,0,255);stroke-width:0.50" />\n<line x1="36.361716" y1="129.100000" x2="36.361716" y2="72.700000" style="stroke:rgb(0,0,255);stroke-width:0.50" /> \n  <polygon points="36.361716,72.700000 35.361716,75.700000 36.361716,76.700000 37.361716,75.700000" style="fill:rgb(0,0,255);stroke:rgb(0,0,255);stroke-width:0" /><polygon points="36.361716,129.100000 37.361716,126.100000 36.361716,125.100000 35.361716,126.100000" style="fill:rgb(0,0,255);stroke:rgb(0,0,255);stroke-width:0" /> \n  <text x="34.569237" y="107.292669" font-family="inherit" font-size="3.6" fill="rgb(0,0,255)" text-anchor="inherit" transform="rotate(-90.000000 34.569237,107.292669)" >47</text> </g>
  Visible = true
  X = 0
  Y = 0
  arrowL1 = 3
  arrowL2 = 1
  arrowW = 2
  arrow_scheme = 0
  autoPlaceOffset = 2
  autoPlaceText = false
  click1_x = 36.3617
  click1_y = 97.0499
  click2_x = 34.5692
  click2_y = 107.293
  comma_decimal_place = false
  dimension_line_overshoot = 1
  gap_datum_points = 2
  halfDimension_linear = false
  lineColor = rgb(0,0,255)
  strokeWidth = 0.5
  textFormat_linear = %(value)3.3f
  textRenderer_color = rgb(0,0,255)
  textRenderer_family = inherit
  textRenderer_size = 3.6
  unit_custom_scale = 1
  unit_scheme = 0
FEATURE [Drawing::FeatureViewPython] dia022  # drawing view (typed FeaturePython)
  Rotation = 0
  ViewResult = <g>  <circle cx ="62.000000" cy ="96.700000" r="0.250000" stroke="none" fill="rgb(0,0,255)" /> \n<line x1="72.372812" y1="104.275469" x2="60.934015" y2="95.921491" style="stroke:rgb(0,0,255);stroke-width:0.50" />\n<polygon points="63.065985,97.478509 64.898897,100.055413 66.296241,99.837629 66.078456,98.440285" style="fill:rgb(0,0,255);stroke:rgb(0,0,255);stroke-width:0" />\n<polygon points="60.934015,95.921491 59.101103,93.344587 57.703759,93.562371 57.921544,94.959715" style="fill:rgb(0,0,255);stroke:rgb(0,0,255);stroke-width:0" />\n<line x1="72.372812" y1="104.275469" x2="79.587547" y2="104.275469" style="stroke:rgb(0,0,255);stroke-width:0.50" />\n<text x="75.980180" y="102.275469" font-family="inherit" font-size="3.6" fill="rgb(0,0,255)" text-anchor="middle" transform="rotate(0.000000 75.980180,102.275469)" >Ø2.2</text> </g>
  Visible = true
  X = 0
  Y = 0
  arrowL1 = 3
  arrowL2 = 1
  arrowW = 2
  arrow_scheme = 0
  autoPlaceOffset = 2
  autoPlaceText = true
  centerPointDia = 0.5
  click1_x = 72.3728
  click1_y = 104.275
  click2_x = 79.5875
  click2_y = 104.275
  click3_x = 79.5875
  click3_y = 104.275
  comma_decimal_place = false
  lineColor = rgb(0,0,255)
  strokeWidth = 0.5
  textFormat_circular = Ø%(value)3.3f
  textRenderer_color = rgb(0,0,255)
  textRenderer_family = inherit
  textRenderer_size = 3.6
  unit_custom_scale = 1
  unit_scheme = 0
FEATURE [Drawing::FeatureViewPython] text095  # drawing view (typed FeaturePython)
  Rotation = 0
  ViewResult = <g> <text x="73.274654" y="107.657376" font-family="inherit" font-size="3,6" fill="rgb(0,0,255)" text-anchor="inherit" transform="rotate(0.000000 73.274654,107.657376)" >H2</text> </g>
  Visible = true
  X = 0
  Y = 0
  click1_x = 73.2747
  click1_y = 107.657
  rotation = 0
  text = H2
  textRenderer_addText_color = rgb(0,0,255)
  textRenderer_addText_family = inherit
  textRenderer_addText_size = 3,6
FEATURE [Drawing::FeatureViewPython] text096  # drawing view (typed FeaturePython)
  Rotation = 0
  ViewResult = <g> <text x="59.521565" y="110.926553" font-family="inherit" font-size="3,6" fill="rgb(0,0,255)" text-anchor="inherit" transform="rotate(0.000000 59.521565,110.926553)" >H2</text> </g>
  Visible = true
  X = 0
  Y = 0
  click1_x = 59.5216
  click1_y = 110.927
  rotation = 0
  text = H2
  textRenderer_addText_color = rgb(0,0,255)
  textRenderer_addText_family = inherit
  textRenderer_addText_size = 3,6
FEATURE [Drawing::FeatureViewPython] text097  # drawing view (typed FeaturePython)
  Rotation = 0
  ViewResult = <g> <text x="215.690520" y="101.832981" font-family="inherit" font-size="3,6" fill="rgb(0,0,255)" text-anchor="inherit" transform="rotate(0.000000 215.690520,101.832981)" >H2</text> </g>
  Visible = true
  X = 0
  Y = 0
  click1_x = 215.691
  click1_y = 101.833
  rotation = 0
  text = H2
  textRenderer_addText_color = rgb(0,0,255)
  textRenderer_addText_family = inherit
  textRenderer_addText_size = 3,6
FEATURE [Drawing::FeatureViewPython] text098  # drawing view (typed FeaturePython)
  Rotation = 0
  ViewResult = <g> <text x="215.690520" y="119.963761" font-family="inherit" font-size="3,6" fill="rgb(0,0,255)" text-anchor="inherit" transform="rotate(0.000000 215.690520,119.963761)" >H2</text> </g>
  Visible = true
  X = 0
  Y = 0
  click1_x = 215.691
  click1_y = 119.964
  rotation = 0
  text = H2
  textRenderer_addText_color = rgb(0,0,255)
  textRenderer_addText_family = inherit
  textRenderer_addText_size = 3,6
FEATURE [Drawing::FeatureViewPython] dim119  # drawing view (typed FeaturePython)
  Rotation = 0
  ViewResult = <g> \n  <line x1="112.400000" y1="132.680000" x2="112.400000" y2="126.212941" style="stroke:rgb(0,0,255);stroke-width:0.50" />\n<line x1="140.000000" y1="55.835826" x2="140.000000" y2="128.212941" style="stroke:rgb(0,0,255);stroke-width:0.50" />\n<line x1="112.400000" y1="127.212941" x2="140.000000" y2="127.212941" style="stroke:rgb(0,0,255);stroke-width:0.50" /> \n  <polygon points="140.000000,127.212941 137.000000,126.212941 136.000000,127.212941 137.000000,128.212941" style="fill:rgb(0,0,255);stroke:rgb(0,0,255);stroke-width:0" /><polygon points="112.400000,127.212941 115.400000,128.212941 116.400000,127.212941 115.400000,126.212941" style="fill:rgb(0,0,255);stroke:rgb(0,0,255);stroke-width:0" /> \n  <text x="126.200000" y="125.212941" font-family="inherit" font-size="3.6" fill="rgb(0,0,255)" text-anchor="middle" transform="rotate(0.000000 126.200000,125.212941)" >23</text> </g>
  Visible = true
  X = 0
  Y = 0
  arrowL1 = 3
  arrowL2 = 1
  arrowW = 2
  arrow_scheme = 0
  autoPlaceOffset = 2
  autoPlaceText = true
  click1_x = 120.559
  click1_y = 127.213
  click2_x = 120.559
  click2_y = 127.213
  comma_decimal_place = false
  dimension_line_overshoot = 1
  gap_datum_points = 2
  halfDimension_linear = false
  lineColor = rgb(0,0,255)
  strokeWidth = 0.5
  textFormat_linear = %(value)3.3f
  textRenderer_color = rgb(0,0,255)
  textRenderer_family = inherit
  textRenderer_size = 3.6
  unit_custom_scale = 1
  unit_scheme = 0
FEATURE [Drawing::FeatureViewPython] dim138  # drawing view (typed FeaturePython)
  Rotation = 0
  ViewResult = <g> \n  <line x1="109.200000" y1="184.300000" x2="110.133225" y2="184.300000" style="stroke:rgb(0,0,255);stroke-width:0.50" />\n<line x1="118.800000" y1="175.900000" x2="110.133225" y2="175.900000" style="stroke:rgb(0,0,255);stroke-width:0.50" />\n<line x1="111.133225" y1="184.300000" x2="111.133225" y2="175.900000" style="stroke:rgb(0,0,255);stroke-width:0.50" /> \n  <polygon points="111.133225,175.900000 112.133225,172.900000 111.133225,171.900000 110.133225,172.900000" style="fill:rgb(0,0,255);stroke:rgb(0,0,255);stroke-width:0" /><polygon points="111.133225,184.300000 110.133225,187.300000 111.133225,188.300000 112.133225,187.300000" style="fill:rgb(0,0,255);stroke:rgb(0,0,255);stroke-width:0" /> \n  <text x="109.133225" y="180.100000" font-family="inherit" font-size="3.6" fill="rgb(0,0,255)" text-anchor="middle" transform="rotate(-90.000000 109.133225,180.100000)" >7</text> </g>
  Visible = true
  X = 0
  Y = 0
  arrowL1 = 3
  arrowL2 = 1
  arrowW = 2
  arrow_scheme = 0
  autoPlaceOffset = 2
  autoPlaceText = true
  click1_x = 111.133
  click1_y = 181.965
  click2_x = 111.133
  click2_y = 181.965
  comma_decimal_place = false
  dimension_line_overshoot = 1
  gap_datum_points = 2
  halfDimension_linear = false
  lineColor = rgb(0,0,255)
  strokeWidth = 0.5
  textFormat_linear = %(value)3.3f
  textRenderer_color = rgb(0,0,255)
  textRenderer_family = inherit
  textRenderer_size = 3.6
  unit_custom_scale = 1
  unit_scheme = 0
FEATURE [Drawing::FeatureViewPython] centerLines011  # drawing view (typed FeaturePython)
  Rotation = 0
  ViewResult = <g transform="scale(1.200000,1.200000)" stroke="rgb(0,0,255)"  stroke-width="0.266667" > <path d="M 102.666667,116.583333 L 105.166667,116.583333 M 106.833333,116.583333 L 111.833333,116.583333 M 113.500000,116.583333 L 116.000000,116.583333 M 117.666667,116.583333 L 122.666667,116.583333 M 124.333333,116.583333 L 126.833333,116.583333 M 128.500000,116.583333 L 130.755404,116.583333 "/>\n<path d="M 102.666667,116.583333 L 105.166667,116.583333 M 106.833333,116.583333 L 111.833333,116.583333 M 113.500000,116.583333 L 116.000000,116.583333 M 117.666667,116.583333 L 122.666667,116.583333 M 124.333333,116.583333 L 126.833333,116.583333 M 128.500000,116.583333 L 130.755404,116.583333 "/> </g> 
  Visible = true
  X = 0
  Y = 0
  centerLine_color = rgb(0,0,255)
  centerLine_len_dash = 6
  centerLine_len_dot = 3
  centerLine_len_gap = 2
  centerLine_width = 0.32
  click1_x = 156.906
  click1_y = 139.992
  click2_x = 156.906
  click2_y = 139.992
FEATURE [Drawing::FeatureViewPython] centerLines012  # drawing view (typed FeaturePython)
  Rotation = 0
  ViewResult = <g transform="scale(1.200000,1.200000)" stroke="rgb(0,0,255)"  stroke-width="0.266667" > <path d="M 102.666667,116.583333 L 102.666667,119.083333 M 102.666667,120.750000 L 102.666667,125.750000 M 102.666667,127.416667 L 102.666667,129.916667 M 102.666667,131.583333 L 102.666667,136.583333 M 102.666667,138.250000 L 102.666667,140.750000 M 102.666667,142.416667 L 102.666667,144.718312 "/>\n<path d="M 102.666667,116.583333 L 102.666667,119.083333 M 102.666667,120.750000 L 102.666667,125.750000 M 102.666667,127.416667 L 102.666667,129.916667 M 102.666667,131.583333 L 102.666667,136.583333 M 102.666667,138.250000 L 102.666667,140.750000 M 102.666667,142.416667 L 102.666667,144.718312 "/> </g> 
  Visible = true
  X = 0
  Y = 0
  centerLine_color = rgb(0,0,255)
  centerLine_len_dash = 6
  centerLine_len_dot = 3
  centerLine_len_gap = 2
  centerLine_width = 0.32
  click1_x = 123.429
  click1_y = 173.662
  click2_x = 123.429
  click2_y = 173.662
FEATURE [Drawing::FeatureViewPython] dim140  # drawing view (typed FeaturePython)
  Rotation = 0
  ViewResult = <g> \n  <line x1="125.600000" y1="177.900000" x2="125.600000" y2="181.875377" style="stroke:rgb(0,0,255);stroke-width:0.50" />\n<line x1="154.400000" y1="177.900000" x2="154.400000" y2="181.875377" style="stroke:rgb(0,0,255);stroke-width:0.50" />\n<line x1="125.600000" y1="180.875377" x2="154.400000" y2="180.875377" style="stroke:rgb(0,0,255);stroke-width:0.50" /> \n  <polygon points="154.400000,180.875377 151.400000,179.875377 150.400000,180.875377 151.400000,181.875377" style="fill:rgb(0,0,255);stroke:rgb(0,0,255);stroke-width:0" /><polygon points="125.600000,180.875377 128.600000,181.875377 129.600000,180.875377 128.600000,179.875377" style="fill:rgb(0,0,255);stroke:rgb(0,0,255);stroke-width:0" /> \n  <text x="144.285811" y="179.803417" font-family="inherit" font-size="3.6" fill="rgb(0,0,255)" text-anchor="inherit" transform="rotate(0.000000 144.285811,179.803417)" >24</text> </g>
  Visible = true
  X = 0
  Y = 0
  arrowL1 = 3
  arrowL2 = 1
  arrowW = 2
  arrow_scheme = 0
  autoPlaceOffset = 2
  autoPlaceText = false
  click1_x = 138.283
  click1_y = 180.875
  click2_x = 144.286
  click2_y = 179.803
  comma_decimal_place = false
  dimension_line_overshoot = 1
  gap_datum_points = 2
  halfDimension_linear = false
  lineColor = rgb(0,0,255)
  strokeWidth = 0.5
  textFormat_linear = %(value)3.3f
  textRenderer_color = rgb(0,0,255)
  textRenderer_family = inherit
  textRenderer_size = 3.6
  unit_custom_scale = 1
  unit_scheme = 0
FEATURE [Drawing::FeatureViewPython] dim139  # drawing view (typed FeaturePython)
  Rotation = 0
  ViewResult = <g> \n  <line x1="120.800000" y1="177.900000" x2="120.800000" y2="181.838088" style="stroke:rgb(0,0,255);stroke-width:0.50" />\n<line x1="125.600000" y1="177.900000" x2="125.600000" y2="181.838088" style="stroke:rgb(0,0,255);stroke-width:0.50" />\n<line x1="120.800000" y1="180.838088" x2="125.600000" y2="180.838088" style="stroke:rgb(0,0,255);stroke-width:0.50" /> \n  <polygon points="125.600000,180.838088 128.600000,181.838088 129.600000,180.838088 128.600000,179.838088" style="fill:rgb(0,0,255);stroke:rgb(0,0,255);stroke-width:0" /><polygon points="120.800000,180.838088 117.800000,179.838088 116.800000,180.838088 117.800000,181.838088" style="fill:rgb(0,0,255);stroke:rgb(0,0,255);stroke-width:0" /> \n  <text x="123.200000" y="178.838088" font-family="inherit" font-size="3.6" fill="rgb(0,0,255)" text-anchor="middle" transform="rotate(0.000000 123.200000,178.838088)" >4</text> </g>
  Visible = true
  X = 0
  Y = 0
  arrowL1 = 3
  arrowL2 = 1
  arrowW = 2
  arrow_scheme = 0
  autoPlaceOffset = 2
  autoPlaceText = true
  click1_x = 124.995
  click1_y = 180.838
  click2_x = 124.995
  click2_y = 180.838
  comma_decimal_place = false
  dimension_line_overshoot = 1
  gap_datum_points = 2
  halfDimension_linear = false
  lineColor = rgb(0,0,255)
  strokeWidth = 0.5
  textFormat_linear = %(value)3.3f
  textRenderer_color = rgb(0,0,255)
  textRenderer_family = inherit
  textRenderer_size = 3.6
  unit_custom_scale = 1
  unit_scheme = 0
FEATURE [Drawing::FeatureViewPython] dim142  # drawing view (typed FeaturePython)
  Rotation = 0
  ViewResult = <g> \n  <line x1="154.400000" y1="177.900000" x2="154.400000" y2="181.838088" style="stroke:rgb(0,0,255);stroke-width:0.50" />\n<line x1="159.200000" y1="177.900000" x2="159.200000" y2="181.838088" style="stroke:rgb(0,0,255);stroke-width:0.50" />\n<line x1="154.400000" y1="180.838088" x2="159.200000" y2="180.838088" style="stroke:rgb(0,0,255);stroke-width:0.50" /> \n  <polygon points="159.200000,180.838088 162.200000,181.838088 163.200000,180.838088 162.200000,179.838088" style="fill:rgb(0,0,255);stroke:rgb(0,0,255);stroke-width:0" /><polygon points="154.400000,180.838088 151.400000,179.838088 150.400000,180.838088 151.400000,181.838088" style="fill:rgb(0,0,255);stroke:rgb(0,0,255);stroke-width:0" /> \n  <text x="156.800000" y="178.838088" font-family="inherit" font-size="3.6" fill="rgb(0,0,255)" text-anchor="middle" transform="rotate(0.000000 156.800000,178.838088)" >4</text> </g>
  Visible = true
  X = 0
  Y = 0
  arrowL1 = 3
  arrowL2 = 1
  arrowW = 2
  arrow_scheme = 0
  autoPlaceOffset = 2
  autoPlaceText = true
  click1_x = 159.962
  click1_y = 180.838
  click2_x = 159.962
  click2_y = 180.838
  comma_decimal_place = false
  dimension_line_overshoot = 1
  gap_datum_points = 2
  halfDimension_linear = false
  lineColor = rgb(0,0,255)
  strokeWidth = 0.5
  textFormat_linear = %(value)3.3f
  textRenderer_color = rgb(0,0,255)
  textRenderer_family = inherit
  textRenderer_size = 3.6
  unit_custom_scale = 1
  unit_scheme = 0
FEATURE [Drawing::FeatureViewPython] centerLines013  # drawing view (typed FeaturePython)
  Rotation = 0
  ViewResult = <g transform="scale(1.200000,1.200000)" stroke="rgb(0,0,255)"  stroke-width="0.266667" > <path d="M 102.666667,144.583333 L 105.166667,144.583333 M 106.833333,144.583333 L 111.833333,144.583333 M 113.500000,144.583333 L 116.000000,144.583333 M 117.666667,144.583333 L 122.666667,144.583333 M 124.333333,144.583333 L 126.833333,144.583333 M 128.500000,144.583333 L 130.720207,144.583333 "/>\n<path d="M 102.666667,144.583333 L 105.166667,144.583333 M 106.833333,144.583333 L 111.833333,144.583333 M 113.500000,144.583333 L 116.000000,144.583333 M 117.666667,144.583333 L 122.666667,144.583333 M 124.333333,144.583333 L 126.833333,144.583333 M 128.500000,144.583333 L 130.720207,144.583333 "/> </g> 
  Visible = true
  X = 0
  Y = 0
  centerLine_color = rgb(0,0,255)
  centerLine_len_dash = 6
  centerLine_len_dot = 3
  centerLine_len_gap = 2
  centerLine_width = 0.32
  click1_x = 156.864
  click1_y = 173.249
  click2_x = 156.864
  click2_y = 173.249
FEATURE [Drawing::FeatureViewPython] centerLines014  # drawing view (typed FeaturePython)
  Rotation = 0
  ViewResult = <g transform="scale(1.200000,1.200000)" stroke="rgb(0,0,255)"  stroke-width="0.266667" > <path d="M 130.666667,144.583333 L 130.666667,142.083333 M 130.666667,140.416667 L 130.666667,135.416667 M 130.666667,133.750000 L 130.666667,131.250000 M 130.666667,129.583333 L 130.666667,124.583333 M 130.666667,122.916667 L 130.666667,120.416667 M 130.666667,118.750000 L 130.666667,116.542560 "/>\n<path d="M 130.666667,144.583333 L 130.666667,142.083333 M 130.666667,140.416667 L 130.666667,135.416667 M 130.666667,133.750000 L 130.666667,131.250000 M 130.666667,129.583333 L 130.666667,124.583333 M 130.666667,122.916667 L 130.666667,120.416667 M 130.666667,118.750000 L 130.666667,116.542560 "/> </g> 
  Visible = true
  X = 0
  Y = 0
  centerLine_color = rgb(0,0,255)
  centerLine_len_dash = 6
  centerLine_len_dot = 3
  centerLine_len_gap = 2
  centerLine_width = 0.32
  click1_x = 156.873
  click1_y = 139.851
  click2_x = 156.873
  click2_y = 139.851
FEATURE [Drawing::FeatureViewPython] dim143  # drawing view (typed FeaturePython)
  Rotation = 0
  ViewResult = <g> \n  <line x1="161.200000" y1="175.900000" x2="163.738335" y2="175.900000" style="stroke:rgb(0,0,255);stroke-width:0.50" />\n<line x1="161.200000" y1="171.100000" x2="163.738335" y2="171.100000" style="stroke:rgb(0,0,255);stroke-width:0.50" />\n<line x1="162.738335" y1="175.900000" x2="162.738335" y2="171.100000" style="stroke:rgb(0,0,255);stroke-width:0.50" /> \n  <polygon points="162.738335,171.100000 163.738335,168.100000 162.738335,167.100000 161.738335,168.100000" style="fill:rgb(0,0,255);stroke:rgb(0,0,255);stroke-width:0" /><polygon points="162.738335,175.900000 161.738335,178.900000 162.738335,179.900000 163.738335,178.900000" style="fill:rgb(0,0,255);stroke:rgb(0,0,255);stroke-width:0" /> \n  <text x="166.303478" y="174.901767" font-family="inherit" font-size="3.6" fill="rgb(0,0,255)" text-anchor="inherit" transform="rotate(-90.000000 166.303478,174.901767)" >4</text> </g>
  Visible = true
  X = 0
  Y = 0
  arrowL1 = 3
  arrowL2 = 1
  arrowW = 2
  arrow_scheme = 0
  autoPlaceOffset = 2
  autoPlaceText = false
  click1_x = 162.738
  click1_y = 173.434
  click2_x = 166.303
  click2_y = 174.902
  comma_decimal_place = false
  dimension_line_overshoot = 1
  gap_datum_points = 2
  halfDimension_linear = false
  lineColor = rgb(0,0,255)
  strokeWidth = 0.5
  textFormat_linear = %(value)3.3f
  textRenderer_color = rgb(0,0,255)
  textRenderer_family = inherit
  textRenderer_size = 3.6
  unit_custom_scale = 1
  unit_scheme = 0
FEATURE [Drawing::FeatureViewPython] dim144  # drawing view (typed FeaturePython)
  Rotation = 0
  ViewResult = <g> \n  <line x1="161.200000" y1="171.100000" x2="163.747073" y2="171.100000" style="stroke:rgb(0,0,255);stroke-width:0.50" />\n<line x1="161.200000" y1="142.300000" x2="163.747073" y2="142.300000" style="stroke:rgb(0,0,255);stroke-width:0.50" />\n<line x1="162.747073" y1="171.100000" x2="162.747073" y2="142.300000" style="stroke:rgb(0,0,255);stroke-width:0.50" /> \n  <polygon points="162.747073,142.300000 161.747073,145.300000 162.747073,146.300000 163.747073,145.300000" style="fill:rgb(0,0,255);stroke:rgb(0,0,255);stroke-width:0" /><polygon points="162.747073,171.100000 163.747073,168.100000 162.747073,167.100000 161.747073,168.100000" style="fill:rgb(0,0,255);stroke:rgb(0,0,255);stroke-width:0" /> \n  <text x="166.242312" y="158.596476" font-family="inherit" font-size="3.6" fill="rgb(0,0,255)" text-anchor="inherit" transform="rotate(-90.000000 166.242312,158.596476)" >24</text> </g>
  Visible = true
  X = 0
  Y = 0
  arrowL1 = 3
  arrowL2 = 1
  arrowW = 2
  arrow_scheme = 0
  autoPlaceOffset = 2
  autoPlaceText = false
  click1_x = 162.747
  click1_y = 166.898
  click2_x = 166.242
  click2_y = 158.596
  comma_decimal_place = false
  dimension_line_overshoot = 1
  gap_datum_points = 2
  halfDimension_linear = false
  lineColor = rgb(0,0,255)
  strokeWidth = 0.5
  textFormat_linear = %(value)3.3f
  textRenderer_color = rgb(0,0,255)
  textRenderer_family = inherit
  textRenderer_size = 3.6
  unit_custom_scale = 1
  unit_scheme = 0
FEATURE [Drawing::FeatureViewPython] dim145  # drawing view (typed FeaturePython)
  Rotation = 0
  ViewResult = <g> \n  <line x1="161.200000" y1="142.300000" x2="163.747970" y2="142.300000" style="stroke:rgb(0,0,255);stroke-width:0.50" />\n<line x1="161.200000" y1="137.500000" x2="163.747970" y2="137.500000" style="stroke:rgb(0,0,255);stroke-width:0.50" />\n<line x1="162.747970" y1="142.300000" x2="162.747970" y2="137.500000" style="stroke:rgb(0,0,255);stroke-width:0.50" /> \n  <polygon points="162.747970,137.500000 163.747970,134.500000 162.747970,133.500000 161.747970,134.500000" style="fill:rgb(0,0,255);stroke:rgb(0,0,255);stroke-width:0" /><polygon points="162.747970,142.300000 161.747970,145.300000 162.747970,146.300000 163.747970,145.300000" style="fill:rgb(0,0,255);stroke:rgb(0,0,255);stroke-width:0" /> \n  <text x="166.071618" y="141.199651" font-family="inherit" font-size="3.6" fill="rgb(0,0,255)" text-anchor="inherit" transform="rotate(-90.000000 166.071618,141.199651)" >4</text> </g>
  Visible = true
  X = 0
  Y = 0
  arrowL1 = 3
  arrowL2 = 1
  arrowW = 2
  arrow_scheme = 0
  autoPlaceOffset = 2
  autoPlaceText = false
  click1_x = 162.748
  click1_y = 144.523
  click2_x = 166.072
  click2_y = 141.2
  comma_decimal_place = false
  dimension_line_overshoot = 1
  gap_datum_points = 2
  halfDimension_linear = false
  lineColor = rgb(0,0,255)
  strokeWidth = 0.5
  textFormat_linear = %(value)3.3f
  textRenderer_color = rgb(0,0,255)
  textRenderer_family = inherit
  textRenderer_size = 3.6
  unit_custom_scale = 1
  unit_scheme = 0
FEATURE [Drawing::FeatureViewPython] text083  # drawing view (typed FeaturePython)
  Rotation = 0
  ViewResult = <g> <text x="167.742593" y="138.658191" font-family="inherit" font-size="3,6" fill="rgb(0,0,255)" text-anchor="inherit" transform="rotate(0.000000 167.742593,138.658191)" >H1</text> </g>
  Visible = true
  X = 0
  Y = 0
  click1_x = 167.743
  click1_y = 138.658
  rotation = 0
  text = H1
  textRenderer_addText_color = rgb(0,0,255)
  textRenderer_addText_family = inherit
  textRenderer_addText_size = 3,6
FEATURE [Drawing::FeatureViewPython] text087  # drawing view (typed FeaturePython)
  Rotation = 0
  ViewResult = <g> <text x="148.668637" y="142.987033" font-family="inherit" font-size="3,6" fill="rgb(0,0,255)" text-anchor="inherit" transform="rotate(0.000000 148.668637,142.987033)" >H1</text> </g>
  Visible = true
  X = 0
  Y = 0
  click1_x = 148.669
  click1_y = 142.987
  rotation = 0
  text = H1
  textRenderer_addText_color = rgb(0,0,255)
  textRenderer_addText_family = inherit
  textRenderer_addText_size = 3,6
FEATURE [Drawing::FeatureViewPython] text099  # drawing view (typed FeaturePython)
  Rotation = 0
  ViewResult = <g> <text x="126.753878" y="143.257585" font-family="inherit" font-size="3,6" fill="rgb(0,0,255)" text-anchor="inherit" transform="rotate(0.000000 126.753878,143.257585)" >H1</text> </g>
  Visible = true
  X = 0
  Y = 0
  click1_x = 126.754
  click1_y = 143.258
  rotation = 0
  text = H1
  textRenderer_addText_color = rgb(0,0,255)
  textRenderer_addText_family = inherit
  textRenderer_addText_size = 3,6
FEATURE [Drawing::FeatureViewPython] text100  # drawing view (typed FeaturePython)
  Rotation = 0
  ViewResult = <g> <text x="127.024431" y="172.341986" font-family="inherit" font-size="3,6" fill="rgb(0,0,255)" text-anchor="inherit" transform="rotate(0.000000 127.024431,172.341986)" >H1</text> </g>
  Visible = true
  X = 0
  Y = 0
  click1_x = 127.024
  click1_y = 172.342
  rotation = 0
  text = H1
  textRenderer_addText_color = rgb(0,0,255)
  textRenderer_addText_family = inherit
  textRenderer_addText_size = 3,6
FEATURE [Drawing::FeatureViewPython] text101  # drawing view (typed FeaturePython)
  Rotation = 0
  ViewResult = <g> <text x="148.262808" y="172.477263" font-family="inherit" font-size="3,6" fill="rgb(0,0,255)" text-anchor="inherit" transform="rotate(0.000000 148.262808,172.477263)" >H1</text> </g>
  Visible = true
  X = 0
  Y = 0
  click1_x = 148.263
  click1_y = 172.477
  rotation = 0
  text = H1
  textRenderer_addText_color = rgb(0,0,255)
  textRenderer_addText_family = inherit
  textRenderer_addText_size = 3,6
FEATURE [Drawing::FeatureViewPython] centerLines015  # drawing view (typed FeaturePython)
  Rotation = 0
  ViewResult = <g transform="scale(1.200000,1.200000)" stroke="rgb(0,0,255)"  stroke-width="0.266667" > <path d="M 116.666667,153.583333 L 116.666667,156.083333 "/>\n<path d="M 116.666667,153.583333 L 116.666667,156.083333 "/> </g> 
  Visible = true
  X = 0
  Y = 0
  centerLine_color = rgb(0,0,255)
  centerLine_len_dash = 6
  centerLine_len_dot = 3
  centerLine_len_gap = 2
  centerLine_width = 0.32
  click1_x = 140.058
  click1_y = 187.91
  click2_x = 140.058
  click2_y = 187.91
FEATURE [Drawing::FeatureViewPython] dim141  # drawing view (typed FeaturePython)
  Rotation = 0
  ViewResult = <g> \n  <line x1="140.000000" y1="185.300000" x2="140.000000" y2="185.878353" style="stroke:rgb(0,0,255);stroke-width:0.50" />\n<line x1="125.600000" y1="177.900000" x2="125.600000" y2="187.878353" style="stroke:rgb(0,0,255);stroke-width:0.50" />\n<line x1="140.000000" y1="186.878353" x2="125.600000" y2="186.878353" style="stroke:rgb(0,0,255);stroke-width:0.50" /> \n  <polygon points="125.600000,186.878353 128.600000,187.878353 129.600000,186.878353 128.600000,185.878353" style="fill:rgb(0,0,255);stroke:rgb(0,0,255);stroke-width:0" /><polygon points="140.000000,186.878353 137.000000,185.878353 136.000000,186.878353 137.000000,187.878353" style="fill:rgb(0,0,255);stroke:rgb(0,0,255);stroke-width:0" /> \n  <text x="131.279363" y="190.308625" font-family="inherit" font-size="3.6" fill="rgb(0,0,255)" text-anchor="inherit" transform="rotate(0.000000 131.279363,190.308625)" >12</text> </g>
  Visible = true
  X = 0
  Y = 0
  arrowL1 = 3
  arrowL2 = 1
  arrowW = 2
  arrow_scheme = 0
  autoPlaceOffset = 2
  autoPlaceText = false
  click1_x = 131.279
  click1_y = 186.878
  click2_x = 131.279
  click2_y = 190.309
  comma_decimal_place = false
  dimension_line_overshoot = 1
  gap_datum_points = 2
  halfDimension_linear = false
  lineColor = rgb(0,0,255)
  strokeWidth = 0.5
  textFormat_linear = %(value)3.3f
  textRenderer_color = rgb(0,0,255)
  textRenderer_family = inherit
  textRenderer_size = 3.6
  unit_custom_scale = 1
  unit_scheme = 0
FEATURE [Drawing::FeatureViewPython] dim146  # drawing view (typed FeaturePython)
  Rotation = 0
  ViewResult = <g> \n  <line x1="140.000000" y1="185.300000" x2="140.000000" y2="185.878353" style="stroke:rgb(0,0,255);stroke-width:0.50" />\n<line x1="154.400000" y1="177.900000" x2="154.400000" y2="187.878353" style="stroke:rgb(0,0,255);stroke-width:0.50" />\n<line x1="140.000000" y1="186.878353" x2="154.400000" y2="186.878353" style="stroke:rgb(0,0,255);stroke-width:0.50" /> \n  <polygon points="154.400000,186.878353 151.400000,185.878353 150.400000,186.878353 151.400000,187.878353" style="fill:rgb(0,0,255);stroke:rgb(0,0,255);stroke-width:0" /><polygon points="140.000000,186.878353 143.000000,187.878353 144.000000,186.878353 143.000000,185.878353" style="fill:rgb(0,0,255);stroke:rgb(0,0,255);stroke-width:0" /> \n  <text x="147.072907" y="190.237161" font-family="inherit" font-size="3.6" fill="rgb(0,0,255)" text-anchor="inherit" transform="rotate(0.000000 147.072907,190.237161)" >12</text> </g>
  Visible = true
  X = 0
  Y = 0
  arrowL1 = 3
  arrowL2 = 1
  arrowW = 2
  arrow_scheme = 0
  autoPlaceOffset = 2
  autoPlaceText = false
  click1_x = 149.145
  click1_y = 186.878
  click2_x = 147.073
  click2_y = 190.237
  comma_decimal_place = false
  dimension_line_overshoot = 1
  gap_datum_points = 2
  halfDimension_linear = false
  lineColor = rgb(0,0,255)
  strokeWidth = 0.5
  textFormat_linear = %(value)3.3f
  textRenderer_color = rgb(0,0,255)
  textRenderer_family = inherit
  textRenderer_size = 3.6
  unit_custom_scale = 1
  unit_scheme = 0
FEATURE [Drawing::FeatureViewPython] table004  # drawing view (typed FeaturePython)
  Rotation = 0
  ViewResult = <blob: 5565 chars omitted>
  Visible = true
  X = 0
  Y = 0
  border_color = rgb(0,0,0)
  border_width = 0.3
  click1_x = 237
  click1_y = 155
  column_widths = [20,20,20,20,20,20,24,22]
  contents = Ref | Metric | Drill | Depth | ⌴ ⌀ | ⌴ depth | Threaded | Direction | H1 | M2 | 1.60 | - | - | - | Yes | CW | H2 | M2 | 2.20 | - | - | - | No | - | H3 | M5 | 4.20 | - | - | 15.00 | Yes | CW
  extra_rows = 0
  padding_x = 1
  padding_y = 1
  row_heights = [7]
  textRenderer_table_color = rgb(0,0,0)
  textRenderer_table_family = inherit
  textRenderer_table_size = 5
FEATURE [Drawing::FeatureViewPython] text102  # drawing view (typed FeaturePython)
  Rotation = 0
  ViewResult = <g> <text x="220.000000" y="35.000000" font-family="inherit" font-size="4" fill="rgb(0,0,255)" text-anchor="inherit" transform="rotate(0.000000 220.000000,35.000000)" >Part number: WHC-OPNP-4NH-CAM</text> </g>
  Visible = true
  X = 0
  Y = 0
  click1_x = 220
  click1_y = 35
  rotation = 0
  text = Part number: WHC-OPNP-4NH-CAM
  textRenderer_addText_color = rgb(0,0,255)
  textRenderer_addText_family = inherit
  textRenderer_addText_size = 4
FEATURE [Drawing::FeatureViewPython] noteCircle009  # drawing view (typed FeaturePython)
  Rotation = 0
  ViewResult = <g> <line x1="85.547339" y1="63.423027" x2="68.000000" y2="72.700000" style="stroke:rgb(0,0,255);stroke-width:0.50" />\n<line x1="85.547339" y1="63.423027" x2="101.034357" y2="63.423027" style="stroke:rgb(0,0,255);stroke-width:0.50" />\n <circle cx ="101.034357" cy ="63.423027" r="4.500000" stroke="rgb(0,0,255)" fill="rgb(255,255,255)" /> \n<text x="99.534357" y="64.923027" font-family="inherit" font-size="5" fill="rgb(0,150,0)" text-anchor="inherit"  >5</text> </g>
  Visible = true
  X = 0
  Y = 0
  click1_x = 85.5473
  click1_y = 63.423
  click2_x = 101.034
  click2_y = 63.7918
  lineColor = rgb(0,0,255)
  noteCircle_fill = rgb(255,255,255)
  noteCircle_radius = 4.5
  noteText = 5
  strokeWidth = 0.5
  textRenderer_noteCircle_color = rgb(0,150,0)
  textRenderer_noteCircle_family = inherit
  textRenderer_noteCircle_size = 5
FEATURE [Drawing::FeatureViewPython] centerLines016  # drawing view (typed FeaturePython)
  Rotation = 0
  ViewResult = <blob: 2382 chars omitted>
  Visible = true
  X = 0
  Y = 0
  centerLine_color = rgb(0,0,255)
  centerLine_len_dash = 6
  centerLine_len_dot = 3
  centerLine_len_gap = 2
  centerLine_width = 0.32
  click1_x = 218.089
  click1_y = 96.4861
  click2_x = 218.089
  click2_y = 96.4861
FEATURE [Drawing::FeatureViewPython] centerLines017  # drawing view (typed FeaturePython)
  Rotation = 0
  ViewResult = <blob: 2382 chars omitted>
  Visible = true
  X = 0
  Y = 0
  centerLine_color = rgb(0,0,255)
  centerLine_len_dash = 6
  centerLine_len_dot = 3
  centerLine_len_gap = 2
  centerLine_width = 0.32
  click1_x = 61.8137
  click1_y = 114.609
  click2_x = 61.8137
  click2_y = 114.609
FEATURE [Drawing::FeatureViewPython] dim147  # drawing view (typed FeaturePython)
  Rotation = 0
  ViewResult = <g> \n  <line x1="68.000000" y1="212.928000" x2="68.000000" y2="219.563187" style="stroke:rgb(0,0,255);stroke-width:0.50" />\n<line x1="212.000000" y1="212.928000" x2="212.000000" y2="219.563187" style="stroke:rgb(0,0,255);stroke-width:0.50" />\n<line x1="68.000000" y1="218.563187" x2="212.000000" y2="218.563187" style="stroke:rgb(0,0,255);stroke-width:0.50" /> \n  <polygon points="212.000000,218.563187 209.000000,217.563187 208.000000,218.563187 209.000000,219.563187" style="fill:rgb(0,0,255);stroke:rgb(0,0,255);stroke-width:0" /><polygon points="68.000000,218.563187 71.000000,219.563187 72.000000,218.563187 71.000000,217.563187" style="fill:rgb(0,0,255);stroke:rgb(0,0,255);stroke-width:0" /> \n  <text x="140.000000" y="216.563187" font-family="inherit" font-size="3.6" fill="rgb(0,0,255)" text-anchor="middle" transform="rotate(0.000000 140.000000,216.563187)" >120</text> </g>
  Visible = true
  X = 0
  Y = 0
  arrowL1 = 3
  arrowL2 = 1
  arrowW = 2
  arrow_scheme = 0
  autoPlaceOffset = 2
  autoPlaceText = true
  click1_x = 212.524
  click1_y = 218.563
  click2_x = 212.524
  click2_y = 218.563
  comma_decimal_place = false
  dimension_line_overshoot = 1
  gap_datum_points = 2
  halfDimension_linear = false
  lineColor = rgb(0,0,255)
  strokeWidth = 0.5
  textFormat_linear = %(value)3.3f
  textRenderer_color = rgb(0,0,255)
  textRenderer_family = inherit
  textRenderer_size = 3.6
  unit_custom_scale = 1
  unit_scheme = 0
FEATURE [Drawing::FeatureViewPython] dim148  # drawing view (typed FeaturePython)
  Rotation = 0
  ViewResult = <g> \n  <line x1="212.000000" y1="212.928000" x2="212.000000" y2="219.547286" style="stroke:rgb(0,0,255);stroke-width:0.50" />\n<line x1="224.000000" y1="212.928000" x2="224.000000" y2="219.547286" style="stroke:rgb(0,0,255);stroke-width:0.50" />\n<line x1="212.000000" y1="218.547286" x2="224.000000" y2="218.547286" style="stroke:rgb(0,0,255);stroke-width:0.50" /> \n  <polygon points="224.000000,218.547286 221.000000,217.547286 220.000000,218.547286 221.000000,219.547286" style="fill:rgb(0,0,255);stroke:rgb(0,0,255);stroke-width:0" /><polygon points="212.000000,218.547286 215.000000,219.547286 216.000000,218.547286 215.000000,217.547286" style="fill:rgb(0,0,255);stroke:rgb(0,0,255);stroke-width:0" /> \n  <text x="218.000000" y="216.547286" font-family="inherit" font-size="3.6" fill="rgb(0,0,255)" text-anchor="middle" transform="rotate(0.000000 218.000000,216.547286)" >10</text> </g>
  Visible = true
  X = 0
  Y = 0
  arrowL1 = 3
  arrowL2 = 1
  arrowW = 2
  arrow_scheme = 0
  autoPlaceOffset = 2
  autoPlaceText = true
  click1_x = 228.506
  click1_y = 218.547
  click2_x = 228.506
  click2_y = 218.547
  comma_decimal_place = false
  dimension_line_overshoot = 1
  gap_datum_points = 2
  halfDimension_linear = false
  lineColor = rgb(0,0,255)
  strokeWidth = 0.5
  textFormat_linear = %(value)3.3f
  textRenderer_color = rgb(0,0,255)
  textRenderer_family = inherit
  textRenderer_size = 3.6
  unit_custom_scale = 1
  unit_scheme = 0
FEATURE [Drawing::FeatureViewPython] dim149  # drawing view (typed FeaturePython)
  Rotation = 0
  ViewResult = <g> \n  <line x1="68.000000" y1="208.928000" x2="68.000000" y2="195.745828" style="stroke:rgb(0,0,255);stroke-width:0.50" />\n<line x1="62.000000" y1="204.128000" x2="62.000000" y2="195.745828" style="stroke:rgb(0,0,255);stroke-width:0.50" />\n<line x1="68.000000" y1="196.745828" x2="62.000000" y2="196.745828" style="stroke:rgb(0,0,255);stroke-width:0.50" /> \n  <polygon points="62.000000,196.745828 59.000000,195.745828 58.000000,196.745828 59.000000,197.745828" style="fill:rgb(0,0,255);stroke:rgb(0,0,255);stroke-width:0" /><polygon points="68.000000,196.745828 71.000000,197.745828 72.000000,196.745828 71.000000,195.745828" style="fill:rgb(0,0,255);stroke:rgb(0,0,255);stroke-width:0" /> \n  <text x="65.000000" y="194.745828" font-family="inherit" font-size="3.6" fill="rgb(0,0,255)" text-anchor="middle" transform="rotate(0.000000 65.000000,194.745828)" >5</text> </g>
  Visible = true
  X = 0
  Y = 0
  arrowL1 = 3
  arrowL2 = 1
  arrowW = 2
  arrow_scheme = 0
  autoPlaceOffset = 2
  autoPlaceText = true
  click1_x = 66.4261
  click1_y = 196.746
  click2_x = 66.4261
  click2_y = 196.746
  comma_decimal_place = false
  dimension_line_overshoot = 1
  gap_datum_points = 2
  halfDimension_linear = false
  lineColor = rgb(0,0,255)
  strokeWidth = 0.5
  textFormat_linear = %(value)3.3f
  textRenderer_color = rgb(0,0,255)
  textRenderer_family = inherit
  textRenderer_size = 3.6
  unit_custom_scale = 1
  unit_scheme = 0
FEATURE [Drawing::FeatureViewPython] dim155  # drawing view (typed FeaturePython)
  Rotation = 0
  ViewResult = <g> \n  <line x1="218.000000" y1="204.128000" x2="218.000000" y2="195.940626" style="stroke:rgb(0,0,255);stroke-width:0.50" />\n<line x1="212.000000" y1="199.328000" x2="212.000000" y2="195.940626" style="stroke:rgb(0,0,255);stroke-width:0.50" />\n<line x1="218.000000" y1="196.940626" x2="212.000000" y2="196.940626" style="stroke:rgb(0,0,255);stroke-width:0.50" /> \n  <polygon points="212.000000,196.940626 209.000000,195.940626 208.000000,196.940626 209.000000,197.940626" style="fill:rgb(0,0,255);stroke:rgb(0,0,255);stroke-width:0" /><polygon points="218.000000,196.940626 221.000000,197.940626 222.000000,196.940626 221.000000,195.940626" style="fill:rgb(0,0,255);stroke:rgb(0,0,255);stroke-width:0" /> \n  <text x="215.000000" y="194.940626" font-family="inherit" font-size="3.6" fill="rgb(0,0,255)" text-anchor="middle" transform="rotate(0.000000 215.000000,194.940626)" >5</text> </g>
  Visible = true
  X = 0
  Y = 0
  arrowL1 = 3
  arrowL2 = 1
  arrowW = 2
  arrow_scheme = 0
  autoPlaceOffset = 2
  autoPlaceText = true
  click1_x = 212.33
  click1_y = 196.941
  click2_x = 212.33
  click2_y = 196.941
  comma_decimal_place = false
  dimension_line_overshoot = 1
  gap_datum_points = 2
  halfDimension_linear = false
  lineColor = rgb(0,0,255)
  strokeWidth = 0.5
  textFormat_linear = %(value)3.3f
  textRenderer_color = rgb(0,0,255)
  textRenderer_family = inherit
  textRenderer_size = 3.6
  unit_custom_scale = 1
  unit_scheme = 0
FEATURE [Drawing::FeatureViewPython] dim158  # drawing view (typed FeaturePython)
  Rotation = 0
  ViewResult = <g> \n  <line x1="56.000000" y1="212.928000" x2="56.000000" y2="219.368389" style="stroke:rgb(0,0,255);stroke-width:0.50" />\n<line x1="68.000000" y1="212.928000" x2="68.000000" y2="219.368389" style="stroke:rgb(0,0,255);stroke-width:0.50" />\n<line x1="56.000000" y1="218.368389" x2="68.000000" y2="218.368389" style="stroke:rgb(0,0,255);stroke-width:0.50" /> \n  <polygon points="68.000000,218.368389 65.000000,217.368389 64.000000,218.368389 65.000000,219.368389" style="fill:rgb(0,0,255);stroke:rgb(0,0,255);stroke-width:0" /><polygon points="56.000000,218.368389 59.000000,219.368389 60.000000,218.368389 59.000000,217.368389" style="fill:rgb(0,0,255);stroke:rgb(0,0,255);stroke-width:0" /> \n  <text x="62.000000" y="216.368389" font-family="inherit" font-size="3.6" fill="rgb(0,0,255)" text-anchor="middle" transform="rotate(0.000000 62.000000,216.368389)" >10</text> </g>
  Visible = true
  X = 0
  Y = 0
  arrowL1 = 3
  arrowL2 = 1
  arrowW = 2
  arrow_scheme = 0
  autoPlaceOffset = 2
  autoPlaceText = true
  click1_x = 67.4001
  click1_y = 218.368
  click2_x = 67.4001
  click2_y = 218.368
  comma_decimal_place = false
  dimension_line_overshoot = 1
  gap_datum_points = 2
  halfDimension_linear = false
  lineColor = rgb(0,0,255)
  strokeWidth = 0.5
  textFormat_linear = %(value)3.3f
  textRenderer_color = rgb(0,0,255)
  textRenderer_family = inherit
  textRenderer_size = 3.6
  unit_custom_scale = 1
  unit_scheme = 0
FEATURE [Drawing::FeatureViewPython] dim159  # drawing view (typed FeaturePython)
  Rotation = 0
  ViewResult = <g> \n  <line x1="54.000000" y1="210.928000" x2="47.309867" y2="210.928000" style="stroke:rgb(0,0,255);stroke-width:0.50" />\n<line x1="54.000000" y1="201.328000" x2="47.309867" y2="201.328000" style="stroke:rgb(0,0,255);stroke-width:0.50" />\n<line x1="48.309867" y1="210.928000" x2="48.309867" y2="201.328000" style="stroke:rgb(0,0,255);stroke-width:0.50" /> \n  <polygon points="48.309867,201.328000 49.309867,198.328000 48.309867,197.328000 47.309867,198.328000" style="fill:rgb(0,0,255);stroke:rgb(0,0,255);stroke-width:0" /><polygon points="48.309867,210.928000 47.309867,213.928000 48.309867,214.928000 49.309867,213.928000" style="fill:rgb(0,0,255);stroke:rgb(0,0,255);stroke-width:0" /> \n  <text x="46.309867" y="206.128000" font-family="inherit" font-size="3.6" fill="rgb(0,0,255)" text-anchor="middle" transform="rotate(-90.000000 46.309867,206.128000)" >8</text> </g>
  Visible = true
  X = 0
  Y = 0
  arrowL1 = 3
  arrowL2 = 1
  arrowW = 2
  arrow_scheme = 0
  autoPlaceOffset = 2
  autoPlaceText = true
  click1_x = 48.3099
  click1_y = 201.031
  click2_x = 48.3099
  click2_y = 201.031
  comma_decimal_place = false
  dimension_line_overshoot = 1
  gap_datum_points = 2
  halfDimension_linear = false
  lineColor = rgb(0,0,255)
  strokeWidth = 0.5
  textFormat_linear = %(value)3.3f
  textRenderer_color = rgb(0,0,255)
  textRenderer_family = inherit
  textRenderer_size = 3.6
  unit_custom_scale = 1
  unit_scheme = 0
FEATURE [Drawing::FeatureViewPython] dia021  # drawing view (typed FeaturePython)
  Rotation = 0
  ViewResult = <g>  <circle cx ="218.000000" cy ="206.128000" r="0.250000" stroke="none" fill="rgb(0,0,255)" /> \n<line x1="230.578319" y1="208.418115" x2="215.520757" y2="205.676608" style="stroke:rgb(0,0,255);stroke-width:0.50" />\n<polygon points="220.479243,206.579392 223.251599,208.100590 224.414549,207.295887 223.609846,206.132937" style="fill:rgb(0,0,255);stroke:rgb(0,0,255);stroke-width:0" />\n<polygon points="215.520757,205.676608 212.748401,204.155410 211.585451,204.960113 212.390154,206.123063" style="fill:rgb(0,0,255);stroke:rgb(0,0,255);stroke-width:0" />\n<line x1="230.578319" y1="208.418115" x2="250.774960" y2="208.418115" style="stroke:rgb(0,0,255);stroke-width:0.50" />\n<text x="240.676639" y="206.418115" font-family="inherit" font-size="3.6" fill="rgb(0,0,255)" text-anchor="middle" transform="rotate(0.000000 240.676639,206.418115)" >Ø4.2</text> </g>
  Visible = true
  X = 0
  Y = 0
  arrowL1 = 3
  arrowL2 = 1
  arrowW = 2
  arrow_scheme = 0
  autoPlaceOffset = 2
  autoPlaceText = true
  centerPointDia = 0.5
  click1_x = 230.578
  click1_y = 208.418
  click2_x = 250.775
  click2_y = 208.699
  click3_x = 250.775
  click3_y = 208.699
  comma_decimal_place = false
  lineColor = rgb(0,0,255)
  strokeWidth = 0.5
  textFormat_circular = Ø%(value)3.3f
  textRenderer_color = rgb(0,0,255)
  textRenderer_family = inherit
  textRenderer_size = 3.6
  unit_custom_scale = 1
  unit_scheme = 0
FEATURE [Drawing::FeatureViewPython] dim160  # drawing view (typed FeaturePython)
  Rotation = 0
  ViewResult = <g> \n  <line x1="60.000000" y1="206.128000" x2="52.731740" y2="206.128000" style="stroke:rgb(0,0,255);stroke-width:0.50" />\n<line x1="54.000000" y1="210.928000" x2="52.731740" y2="210.928000" style="stroke:rgb(0,0,255);stroke-width:0.50" />\n<line x1="53.731740" y1="206.128000" x2="53.731740" y2="210.928000" style="stroke:rgb(0,0,255);stroke-width:0.50" /> \n  <polygon points="53.731740,210.928000 52.731740,213.928000 53.731740,214.928000 54.731740,213.928000" style="fill:rgb(0,0,255);stroke:rgb(0,0,255);stroke-width:0" /><polygon points="53.731740,206.128000 54.731740,203.128000 53.731740,202.128000 52.731740,203.128000" style="fill:rgb(0,0,255);stroke:rgb(0,0,255);stroke-width:0" /> \n  <text x="51.731740" y="208.528000" font-family="inherit" font-size="3.6" fill="rgb(0,0,255)" text-anchor="middle" transform="rotate(-90.000000 51.731740,208.528000)" >4</text> </g>
  Visible = true
  X = 0
  Y = 0
  arrowL1 = 3
  arrowL2 = 1
  arrowW = 2
  arrow_scheme = 0
  autoPlaceOffset = 2
  autoPlaceText = true
  click1_x = 53.7317
  click1_y = 209.732
  click2_x = 53.7317
  click2_y = 209.732
  comma_decimal_place = false
  dimension_line_overshoot = 1
  gap_datum_points = 2
  halfDimension_linear = false
  lineColor = rgb(0,0,255)
  strokeWidth = 0.5
  textFormat_linear = %(value)3.3f
  textRenderer_color = rgb(0,0,255)
  textRenderer_family = inherit
  textRenderer_size = 3.6
  unit_custom_scale = 1
  unit_scheme = 0
FEATURE [Drawing::FeatureViewPython] text103  # drawing view (typed FeaturePython)
  Rotation = 0
  ViewResult = <g> <text x="238.152059" y="212.064731" font-family="inherit" font-size="3,6" fill="rgb(0,0,255)" text-anchor="inherit" transform="rotate(0.000000 238.152059,212.064731)" >H3</text> </g>
  Visible = true
  X = 0
  Y = 0
  click1_x = 238.152
  click1_y = 212.065
  rotation = 0
  text = H3
  textRenderer_addText_color = rgb(0,0,255)
  textRenderer_addText_family = inherit
  textRenderer_addText_size = 3,6
FEATURE [Drawing::FeatureViewPython] text104  # drawing view (typed FeaturePython)
  Rotation = 0
  ViewResult = <g> <text x="69.737630" y="207.070114" font-family="inherit" font-size="3,6" fill="rgb(0,0,255)" text-anchor="inherit" transform="rotate(0.000000 69.737630,207.070114)" >H3</text> </g>
  Visible = true
  X = 0
  Y = 0
  click1_x = 69.7376
  click1_y = 207.07
  rotation = 0
  text = H3
  textRenderer_addText_color = rgb(0,0,255)
  textRenderer_addText_family = inherit
  textRenderer_addText_size = 3,6
FEATURE [Part::Feature] Body006021005001  label="Camera Support Body001"
  shape: bbox 140 x 8 x 93 mm, 60 faces (baked)
FEATURE [Part::Feature] Body006021006001  label="Left Square001"
  shape: bbox 10 x 33.86 x 47 mm, 5 faces (baked)
FEATURE [Part::Feature] Body006021007001  label="Right Square001"
  shape: bbox 10 x 33.86 x 47 mm, 5 faces (baked)
FEATURE [Part::MultiFuse] Fusion
  Shapes = -> [Body006021005001,Body006021007001,Body006021006001]
FEATURE [Drawing::FeatureViewPart] Ortho019  label="Ortho_1_1"
  Direction = (0.57735,0.57735,0.57735)
  HiddenWidth = 0.15
  LineWidth = 0.35
  Rotation = -4.13e-14
  Scale = 0.8
  ShowHiddenLines = false
  ShowSmoothLines = false
  Source = -> Fusion
  Tolerance = 0.05
  ViewResult = <blob: 7552 chars omitted>
  Visible = true
  X = 370.37
  Y = -22.87
FEATURE [Part::Feature] Body006021005002  label="WHC-OPNP-4NH-CAM"
  shape: bbox 140 x 8 x 93 mm, 60 faces (baked)
FEATURE [Part::Feature] Body006021003001  label="WHC-OPNP-LNA"
  shape: bbox 27 x 138.9 x 6 mm, 162 faces (baked)
FEATURE [Part::Feature] Body006021004001  label="WHC-OPNP-NB"
  shape: bbox 27 x 6 x 23 mm, 19 faces (baked)
FEATURE [Part::Feature] Part__Mirroring002  label="WHC-OPNP-RNA"
  shape: bbox 27 x 138.9 x 6 mm, 162 faces (baked)
FEATURE [Part::Feature] Body006021007002  label="WHC-OPNP-4NH-B"
  shape: bbox 140 x 97.85 x 8 mm, 27 faces (baked)
FEATURE [Drawing::FeatureViewPython] dim161  # drawing view (typed FeaturePython)
  Rotation = 0
  ViewResult = <g> \n  <line x1="73.000000" y1="164.560000" x2="60.705377" y2="164.560000" style="stroke:rgb(0,0,255);stroke-width:0.50" />\n<line x1="73.000000" y1="179.420000" x2="60.705377" y2="179.420000" style="stroke:rgb(0,0,255);stroke-width:0.50" />\n<line x1="61.705377" y1="164.560000" x2="61.705377" y2="179.420000" style="stroke:rgb(0,0,255);stroke-width:0.50" /> \n  <polygon points="61.705377,179.420000 62.705377,176.420000 61.705377,175.420000 60.705377,176.420000" style="fill:rgb(0,0,255);stroke:rgb(0,0,255);stroke-width:0" /><polygon points="61.705377,164.560000 60.705377,167.560000 61.705377,168.560000 62.705377,167.560000" style="fill:rgb(0,0,255);stroke:rgb(0,0,255);stroke-width:0" /> \n  <text x="59.705377" y="171.990000" font-family="inherit" font-size="3.6" fill="rgb(0,0,255)" text-anchor="middle" transform="rotate(-90.000000 59.705377,171.990000)" >14.86</text> </g>
  Visible = false
  X = 0
  Y = 0
  arrowL1 = 3
  arrowL2 = 1
  arrowW = 2
  arrow_scheme = 0
  autoPlaceOffset = 2
  autoPlaceText = true
  click1_x = 61.7054
  click1_y = 175.158
  click2_x = 61.7054
  click2_y = 175.158
  comma_decimal_place = false
  dimension_line_overshoot = 1
  gap_datum_points = 2
  halfDimension_linear = false
  lineColor = rgb(0,0,255)
  strokeWidth = 0.5
  textFormat_linear = %(value)3.3f
  textRenderer_color = rgb(0,0,255)
  textRenderer_family = inherit
  textRenderer_size = 3.6
  unit_custom_scale = 1
  unit_scheme = 0
FEATURE [Drawing::FeatureViewPython] dim162  # drawing view (typed FeaturePython)
  Rotation = 0
  ViewResult = <g> \n  <line x1="73.000000" y1="164.560000" x2="60.601966" y2="164.560000" style="stroke:rgb(0,0,255);stroke-width:0.50" />\n<line x1="73.000000" y1="156.560000" x2="60.601966" y2="156.560000" style="stroke:rgb(0,0,255);stroke-width:0.50" />\n<line x1="61.601966" y1="164.560000" x2="61.601966" y2="156.560000" style="stroke:rgb(0,0,255);stroke-width:0.50" /> \n  <polygon points="61.601966,156.560000 62.601966,153.560000 61.601966,152.560000 60.601966,153.560000" style="fill:rgb(0,0,255);stroke:rgb(0,0,255);stroke-width:0" /><polygon points="61.601966,164.560000 60.601966,167.560000 61.601966,168.560000 62.601966,167.560000" style="fill:rgb(0,0,255);stroke:rgb(0,0,255);stroke-width:0" /> \n  <text x="59.601966" y="160.560000" font-family="inherit" font-size="3.6" fill="rgb(0,0,255)" text-anchor="middle" transform="rotate(-90.000000 59.601966,160.560000)" >8</text> </g>
  Visible = false
  X = 0
  Y = 0
  arrowL1 = 3
  arrowL2 = 1
  arrowW = 2
  arrow_scheme = 0
  autoPlaceOffset = 2
  autoPlaceText = true
  click1_x = 61.602
  click1_y = 157.935
  click2_x = 61.602
  click2_y = 157.935
  comma_decimal_place = false
  dimension_line_overshoot = 1
  gap_datum_points = 2
  halfDimension_linear = false
  lineColor = rgb(0,0,255)
  strokeWidth = 0.5
  textFormat_linear = %(value)3.3f
  textRenderer_color = rgb(0,0,255)
  textRenderer_family = inherit
  textRenderer_size = 3.6
  unit_custom_scale = 1
  unit_scheme = 0
FEATURE [Drawing::FeatureViewPython] dim163  # drawing view (typed FeaturePython)
  Rotation = 0
  ViewResult = <g> \n  <line x1="207.000000" y1="179.420000" x2="218.914186" y2="179.420000" style="stroke:rgb(0,0,255);stroke-width:0.50" />\n<line x1="207.000000" y1="164.560000" x2="218.914186" y2="164.560000" style="stroke:rgb(0,0,255);stroke-width:0.50" />\n<line x1="217.914186" y1="179.420000" x2="217.914186" y2="164.560000" style="stroke:rgb(0,0,255);stroke-width:0.50" /> \n  <polygon points="217.914186,164.560000 216.914186,167.560000 217.914186,168.560000 218.914186,167.560000" style="fill:rgb(0,0,255);stroke:rgb(0,0,255);stroke-width:0" /><polygon points="217.914186,179.420000 218.914186,176.420000 217.914186,175.420000 216.914186,176.420000" style="fill:rgb(0,0,255);stroke:rgb(0,0,255);stroke-width:0" /> \n  <text x="215.914186" y="171.990000" font-family="inherit" font-size="3.6" fill="rgb(0,0,255)" text-anchor="middle" transform="rotate(-90.000000 215.914186,171.990000)" >14.86</text> </g>
  Visible = false
  X = 0
  Y = 0
  arrowL1 = 3
  arrowL2 = 1
  arrowW = 2
  arrow_scheme = 0
  autoPlaceOffset = 2
  autoPlaceText = true
  click1_x = 217.914
  click1_y = 164.633
  click2_x = 217.914
  click2_y = 164.633
  comma_decimal_place = false
  dimension_line_overshoot = 1
  gap_datum_points = 2
  halfDimension_linear = false
  lineColor = rgb(0,0,255)
  strokeWidth = 0.5
  textFormat_linear = %(value)3.3f
  textRenderer_color = rgb(0,0,255)
  textRenderer_family = inherit
  textRenderer_size = 3.6
  unit_custom_scale = 1
  unit_scheme = 0
FEATURE [Drawing::FeatureViewPython] dim164  # drawing view (typed FeaturePython)
  Rotation = 0
  ViewResult = <g> \n  <line x1="207.000000" y1="164.560000" x2="218.948649" y2="164.560000" style="stroke:rgb(0,0,255);stroke-width:0.50" />\n<line x1="207.000000" y1="156.560000" x2="218.948649" y2="156.560000" style="stroke:rgb(0,0,255);stroke-width:0.50" />\n<line x1="217.948649" y1="164.560000" x2="217.948649" y2="156.560000" style="stroke:rgb(0,0,255);stroke-width:0.50" /> \n  <polygon points="217.948649,156.560000 218.948649,153.560000 217.948649,152.560000 216.948649,153.560000" style="fill:rgb(0,0,255);stroke:rgb(0,0,255);stroke-width:0" /><polygon points="217.948649,164.560000 216.948649,167.560000 217.948649,168.560000 218.948649,167.560000" style="fill:rgb(0,0,255);stroke:rgb(0,0,255);stroke-width:0" /> \n  <text x="215.948649" y="160.560000" font-family="inherit" font-size="3.6" fill="rgb(0,0,255)" text-anchor="middle" transform="rotate(-90.000000 215.948649,160.560000)" >8</text> </g>
  Visible = false
  X = 0
  Y = 0
  arrowL1 = 3
  arrowL2 = 1
  arrowW = 2
  arrow_scheme = 0
  autoPlaceOffset = 2
  autoPlaceText = true
  click1_x = 217.949
  click1_y = 159.946
  click2_x = 217.949
  click2_y = 159.946
  comma_decimal_place = false
  dimension_line_overshoot = 1
  gap_datum_points = 2
  halfDimension_linear = false
  lineColor = rgb(0,0,255)
  strokeWidth = 0.5
  textFormat_linear = %(value)3.3f
  textRenderer_color = rgb(0,0,255)
  textRenderer_family = inherit
  textRenderer_size = 3.6
  unit_custom_scale = 1
  unit_scheme = 0
FEATURE [Drawing::FeatureViewPython] text105  # drawing view (typed FeaturePython)
  Rotation = 0
  ViewResult = <g> <text x="202.914427" y="168.531704" font-family="inherit" font-size="3,6" fill="rgb(0,0,255)" text-anchor="inherit" transform="rotate(0.000000 202.914427,168.531704)" >H7</text> </g>
  Visible = false
  X = 0
  Y = 0
  click1_x = 202.914
  click1_y = 168.532
  rotation = 0
  text = H7
  textRenderer_addText_color = rgb(0,0,255)
  textRenderer_addText_family = inherit
  textRenderer_addText_size = 3,6
FEATURE [Drawing::FeatureViewPython] text106  # drawing view (typed FeaturePython)
  Rotation = 0
  ViewResult = <g> <text x="202.820485" y="183.280577" font-family="inherit" font-size="3,6" fill="rgb(0,0,255)" text-anchor="inherit" transform="rotate(0.000000 202.820485,183.280577)" >H7</text> </g>
  Visible = false
  X = 0
  Y = 0
  click1_x = 202.82
  click1_y = 183.281
  rotation = 0
  text = H7
  textRenderer_addText_color = rgb(0,0,255)
  textRenderer_addText_family = inherit
  textRenderer_addText_size = 3,6
FEATURE [Drawing::FeatureViewPython] text107  # drawing view (typed FeaturePython)
  Rotation = 0
  ViewResult = <g> <text x="72.643365" y="168.824803" font-family="inherit" font-size="3,6" fill="rgb(0,0,255)" text-anchor="inherit" transform="rotate(0.000000 72.643365,168.824803)" >H7</text> </g>
  Visible = false
  X = 0
  Y = 0
  click1_x = 72.6434
  click1_y = 168.825
  rotation = 0
  text = H7
  textRenderer_addText_color = rgb(0,0,255)
  textRenderer_addText_family = inherit
  textRenderer_addText_size = 3,6
FEATURE [Drawing::FeatureViewPython] text108  # drawing view (typed FeaturePython)
  Rotation = 0
  ViewResult = <g> <text x="72.643365" y="183.975747" font-family="inherit" font-size="3,6" fill="rgb(0,0,255)" text-anchor="inherit" transform="rotate(0.000000 72.643365,183.975747)" >H7</text> </g>
  Visible = false
  X = 0
  Y = 0
  click1_x = 72.6434
  click1_y = 183.976
  rotation = 0
  text = H7
  textRenderer_addText_color = rgb(0,0,255)
  textRenderer_addText_family = inherit
  textRenderer_addText_size = 3,6
FEATURE [Part::Feature] Body006021002001  label="WHC-OPNP-4NH-F"
  shape: bbox 140 x 150 x 8 mm, 88 faces (baked)
FEATURE [App::DocumentObjectGroup] Group005  label="Step Files"
  Group = -> [Body006021005002,Body006021003001,Body006021004001,Part__Mirroring002,Body006021007002,Body006021002001]
FEATURE [Part::Feature] Body006021003002  label="Lift001"
  shape: bbox 27 x 138.9 x 6 mm, 162 faces (baked)
FEATURE [Part::Feature] Body006021004002  label="Fix001"
  shape: bbox 27 x 6 x 23 mm, 19 faces (baked)
FEATURE [Part::MultiFuse] Fusion001
  Shapes = -> [Body006021003002,Body006021004002]
FEATURE [Drawing::FeatureViewPart] Ortho021  label="Ortho_1_002"
  Direction = (0.57735,0.57735,0.57735)
  HiddenWidth = 0.15
  LineWidth = 0.35
  Rotation = -4.13e-14
  Scale = 0.8
  ShowHiddenLines = false
  ShowSmoothLines = false
  Source = -> Fusion001
  Tolerance = 0.05
  ViewResult = <blob: 24984 chars omitted>
  Visible = false
  X = 410
  Y = 55
FEATURE [Part::Feature] Part__Mirroring003  label="Lift (Mirror #1)001"
  shape: bbox 27 x 138.9 x 6 mm, 162 faces (baked)
FEATURE [Part::Feature] Part__Mirroring001001  label="Fix (Mirror #2)001"
  shape: bbox 27 x 6 x 23 mm, 19 faces (baked)
FEATURE [Part::Feature] Body006021003003  label="Lift002"
  Placement = pos=(0,0,16) rot=(0,0,1;0rad)
  shape: bbox 27 x 138.9 x 6 mm, 162 faces (baked)
FEATURE [Part::Feature] Body006021004003  label="Fix002"
  Placement = pos=(0,0,16) rot=(0,0,1;0rad)
  shape: bbox 27 x 6 x 23 mm, 19 faces (baked)
FEATURE [Part::Feature] Body006021005003  label="Camera Support Body002"
  shape: bbox 140 x 8 x 93 mm, 60 faces (baked)
FEATURE [Part::Feature] Body006021006002  label="Left Square002"
  shape: bbox 10 x 33.86 x 47 mm, 5 faces (baked)
FEATURE [Part::Feature] Body006021007003  label="Right Square002"
  shape: bbox 10 x 33.86 x 47 mm, 5 faces (baked)
FEATURE [Part::Feature] Body006021002002  label="Body006021003"
  shape: bbox 140 x 150 x 8 mm, 88 faces (baked)
FEATURE [Part::Feature] Body006021007004  label="Body006021004"
  Placement = pos=(0,0,-36) rot=(0,0,1;0rad)
  shape: bbox 140 x 97.85 x 8 mm, 27 faces (baked)
FEATURE [Part::MultiFuse] Fusion002
  Shapes = -> [Part__Mirroring003,Part__Mirroring001001,Body006021007004,Body006021002002,Body006021004003,Body006021003003,Body006021006002,Body006021005003,Body006021007003]
FEATURE [Drawing::FeatureViewPart] Ortho023  label="Ortho_1_003"
  Direction = (0.57735,0.57735,0.57735)
  HiddenWidth = 0.15
  LineWidth = 0.35
  Rotation = -4.13e-14
  ShowHiddenLines = false
  ShowSmoothLines = false
  Source = -> Fusion002
  Tolerance = 0.05
  ViewResult = <blob: 56324 chars omitted>
  Visible = true
  X = 311.78
  Y = 65
FEATURE [Drawing::FeatureViewPython] table005  # drawing view (typed FeaturePython)
  Rotation = 0
  ViewResult = <blob: 4635 chars omitted>
  Visible = true
  X = 0
  Y = 0
  border_color = rgb(0,0,0)
  border_width = 0.3
  click1_x = 16.962
  click1_y = 22.4931
  column_widths = [70,50,20]
  contents = Part Number | Description | Units | WHC-OPNP-4NH-F | Front Plate | 1 | WHC-OPNP-4NH-B | Back Plate | 1 | WHC-OPNP-LNA | Left Nozzle Lift Body | 2 | WHC-OPNP-RNA | Right Nozzle Lift Body | 2 | WHC-OPNP-NB | Nozzle Lift Base | 4 | WHC-OPNP-4NH-CAM | Camera Plate | 1 | WHC-OPNP-4NH-CAM-SQ | Camera Plate Square | 2
  extra_rows = 0
  padding_x = 1
  padding_y = 1
  row_heights = [7]
  textRenderer_table_color = rgb(0,0,0)
  textRenderer_table_family = inherit
  textRenderer_table_size = 5
FEATURE [Drawing::FeaturePage] Page004  label="General View"
  EditableTexts = <owner>.org | 08/18/2020 | Jaume Olivé	 | 08/18/2020 | WEIGHT | 0 | 1 | Whitecat OpenPNP Head | General View
  Group = -> [Ortho023,table005]
  Template = /Applications/FreeCAD.app/Contents/Resources/data/Mod/Drawing/Templates/A3_Landscape.svg
FEATURE [App::Part] Part002  label="Camera Support"
  Group = -> [Body003]
  Origin = -> Origin005
FEATURE [Sketcher::SketchObject] Sketch003
  AttachmentOffset = pos=(0,0,86.5) rot=(0,0,1;0rad)
  MapMode = 3
  Placement = pos=(0,-86.5,1.92e-14) rot=(1,0,0;1.5708rad)
  Support = -> [Part002]
  sketch-geometry (50):
    g0: LineSegment StartX=64.2003 StartY=8 StartZ=0 EndX=64.2003 EndY=51.8686 EndZ=0
    g1: LineSegment StartX=64.2003 StartY=8 StartZ=0 EndX=84.2003 EndY=8 EndZ=0
    g2: GeomPoint X=74.2003 Y=8 Z=0
    g3: LineSegment StartX=84.2003 StartY=8 StartZ=0 EndX=84.2003 EndY=65 EndZ=0
    g4: LineSegment StartX=94.2003 StartY=55 StartZ=0 EndX=14 EndY=55 EndZ=0
    g5: LineSegment StartX=24 StartY=65 StartZ=0 EndX=24 EndY=8 EndZ=0
    g6: LineSegment StartX=24 StartY=8 StartZ=0 EndX=44 EndY=8 EndZ=0
    g7: LineSegment StartX=44 StartY=8 StartZ=0 EndX=44 EndY=45.3675 EndZ=0
    g8: GeomPoint X=34 Y=8 Z=0
    g9: LineSegment StartX=64.7033 StartY=55 StartZ=0 EndX=84.2003 EndY=114.131 EndZ=0
    g10: LineSegment StartX=93.6974 StartY=101 StartZ=0 EndX=14 EndY=101 EndZ=0
    g11: LineSegment StartX=23.5657 StartY=113.915 StartZ=0 EndX=43.5657 EndY=48.2824 EndZ=0
    g12: ArcOfCircle CenterX=93.6974 CenterY=111 CenterZ=0 NormalX=0 NormalY=0 NormalZ=1 AngleXU=0 Radius=10 StartAngle=4.71239 EndAngle=9.10628
    g13: ArcOfCircle CenterX=74.2003 CenterY=51.8686 CenterZ=0 NormalX=0 NormalY=0 NormalZ=1 AngleXU=0 Radius=10 StartAngle=2.82309 EndAngle=3.14159
    g14: ArcOfCircle CenterX=94.2003 CenterY=65 CenterZ=0 NormalX=0 NormalY=0 NormalZ=1 AngleXU=0 Radius=10 StartAngle=4.71239 EndAngle=9.42478
    g15: ArcOfCircle CenterX=14 CenterY=65 CenterZ=0 NormalX=0 NormalY=0 NormalZ=1 AngleXU=0 Radius=10 StartAngle=-9e-16 EndAngle=4.71239
    g16: ArcOfCircle CenterX=14 CenterY=111 CenterZ=0 NormalX=0 NormalY=0 NormalZ=1 AngleXU=0 Radius=10 StartAngle=0.295788 EndAngle=4.71239
    g17: ArcOfCircle CenterX=34 CenterY=45.3675 CenterZ=0 NormalX=0 NormalY=0 NormalZ=1 AngleXU=0 Radius=10 StartAngle=2e-16 EndAngle=0.295788
    g18: LineSegment StartX=-16 StartY=90 StartZ=0 EndX=-12 EndY=90 EndZ=0
    g19: LineSegment StartX=-12 StartY=90 StartZ=0 EndX=-12 EndY=94 EndZ=0
    g20: LineSegment StartX=-12 StartY=94 StartZ=0 EndX=12 EndY=94 EndZ=0
    g21: LineSegment StartX=12 StartY=94 StartZ=0 EndX=12 EndY=90 EndZ=0
    g22: LineSegment StartX=12 StartY=90 StartZ=0 EndX=16 EndY=90 EndZ=0
    g23: LineSegment StartX=16 StartY=90 StartZ=0 EndX=16 EndY=66 EndZ=0
    g24: LineSegment StartX=16 StartY=66 StartZ=0 EndX=12 EndY=66 EndZ=0
    g25: LineSegment StartX=12 StartY=66 StartZ=0 EndX=12 EndY=62 EndZ=0
    g26: LineSegment StartX=12 StartY=62 StartZ=0 EndX=-12 EndY=62 EndZ=0
    g27: LineSegment StartX=-12 StartY=62 StartZ=0 EndX=-12 EndY=66 EndZ=0
    g28: LineSegment StartX=-12 StartY=66 StartZ=0 EndX=-16 EndY=66 EndZ=0
    g29: LineSegment StartX=-16 StartY=90 StartZ=0 EndX=-16 EndY=66 EndZ=0
    g30: GeomPoint X=0 Y=62 Z=0
    g31: GeomPoint X=51.7773 Y=55 Z=0
    g32: GeomPoint X=51.7773 Y=101 Z=0
    g33: GeomPoint X=51.7773 Y=78 Z=0
    g34: GeomPoint X=16 Y=78 Z=0
    g35: Circle CenterX=-14 CenterY=92 CenterZ=0 NormalX=0 NormalY=0 NormalZ=1 AngleXU=0 Radius=1
    g36: GeomPoint X=-12 Y=92 Z=0
    g37: GeomPoint X=-14 Y=90 Z=0
    g38: Circle CenterX=14 CenterY=92 CenterZ=0 NormalX=0 NormalY=0 NormalZ=1 AngleXU=0 Radius=1
    g39: GeomPoint X=14 Y=90 Z=0
    g40: Circle CenterX=-14 CenterY=64 CenterZ=0 NormalX=0 NormalY=0 NormalZ=1 AngleXU=0 Radius=1
    g41: GeomPoint X=-12 Y=64 Z=0
    g42: Circle CenterX=14 CenterY=64 CenterZ=0 NormalX=0 NormalY=0 NormalZ=1 AngleXU=0 Radius=1
    g43: GeomPoint X=12 Y=64 Z=0
    g44: Circle CenterX=-24 CenterY=78 CenterZ=0 NormalX=0 NormalY=0 NormalZ=1 AngleXU=0 Radius=2.6
    g45: Circle CenterX=24 CenterY=78 CenterZ=0 NormalX=0 NormalY=0 NormalZ=1 AngleXU=0 Radius=2.6
    g46: Circle CenterX=-52 CenterY=83 CenterZ=0 NormalX=0 NormalY=0 NormalZ=1 AngleXU=0 Radius=2.6
    g47: Circle CenterX=52 CenterY=83 CenterZ=0 NormalX=0 NormalY=0 NormalZ=1 AngleXU=0 Radius=2.6
    g48: Circle CenterX=-52 CenterY=73 CenterZ=0 NormalX=0 NormalY=0 NormalZ=1 AngleXU=0 Radius=2.6
    g49: Circle CenterX=52 CenterY=73 CenterZ=0 NormalX=0 NormalY=0 NormalZ=1 AngleXU=0 Radius=2.6
  constraints (118):
    c: Vertical(g0)
    c: Coincident(g1,g0)
    c: Horizontal(g1)
    c: DistanceX(g1,g1) = 20
    c: Symmetric(g1,g1,g2)
    c: Coincident(g1,g3)
    c: Vertical(g3)
    c: Horizontal(g4)
    c: Vertical(g5)
    c: Coincident(g5,g6)
    c: Horizontal(g6)
    c: Coincident(g6,g7)
    c: Vertical(g7)
    c: Horizontal(g1,g5)
    c: Symmetric(g6,g6,g8)
    c: Equal(g6,g1)
    c: Horizontal(g10)
    c: Vertical(g9,g3)
    c: Vertical(g4,g10)
    c: Tangent(g9,g12) = 1.5708
    c: Tangent(g10,g12) = 1.5708
    c: Tangent(g0,g13) = 1.5708
    c: Tangent(g9,g13) = 1.5708
    c: Tangent(g3,g14) = 1.5708
    c: Tangent(g4,g14) = 1.5708
    c: Tangent(g4,g15) = 1.5708
    c: Tangent(g5,g15) = 1.5708
    c: Tangent(g10,g16) = 1.5708
    c: Tangent(g11,g16) = 1.5708
    c: Tangent(g7,g17) = -1.5708
    c: Tangent(g11,g17) = 1.5708
    c: Radius(g16) = 10
    c: Radius(g17) = 10
    c: Radius(g15) = 10
    c: Radius(g14) = 10
    c: Radius(g12) = 10
    c: Radius(g13) = 10
    c: DistanceY(g4,g10) = 46
    c: DistanceY(g1,g4) = 47
    c: Horizontal(g9,g4)
    c: Horizontal(g18)
    c: Coincident(g18,g19)
    c: Vertical(g19)
    c: Coincident(g19,g20)
    c: Horizontal(g20)
    c: Coincident(g20,g21)
    c: Vertical(g21)
    c: Coincident(g21,g22)
    c: Horizontal(g22)
    c: Coincident(g22,g23)
    c: Vertical(g23)
    c: Coincident(g23,g24)
    c: Horizontal(g24)
    c: Coincident(g24,g25)
    c: Vertical(g25)
    c: Coincident(g25,g26)
    c: Horizontal(g26)
    c: Coincident(g26,g27)
    c: Vertical(g27)
    c: Coincident(g27,g28)
    c: Horizontal(g28)
    c: DistanceY(g19,g19) = 4
    c: DistanceX(g18,g18) = 4
    c: Equal(g19,g21)
    c: Equal(g18,g22)
    c: Equal(g18,g28)
    c: Equal(g24,g18)
    c: Equal(g19,g27)
    c: Equal(g25,g19)
    c: Vertical(g28,g18)
    c: Coincident(g29,g18)
    c: Vertical(g29)
    c: DistanceY(g25,g20) = 32
    c: Horizontal(g29,g28)
    c: DistanceX(g18,g22) = 32
    c: Symmetric(g26,g26,g30)
    c: Vertical(g30,g-1)
    c: PointOnObject(g32,g10)
    c: PointOnObject(g31,g4)
    c: Vertical(g31,g32)
    c: Symmetric(g32,g31,g33)
    c: Symmetric(g23,g23,g34)
    c: Horizontal(g34,g33)
    c: Radius(g35) = 1
    c: Symmetric(g18,g18,g37)
    c: Symmetric(g19,g19,g36)
    c: Horizontal(g35,g36)
    c: Vertical(g35,g37)
    c: Radius(g38) = 1
    c: Horizontal(g35,g38)
    c: Symmetric(g22,g22,g39)
    c: Vertical(g39,g38)
    c: Radius(g40) = 1
    c: Vertical(g40,g35)
    c: Symmetric(g27,g27,g41)
    c: Horizontal(g40,g41)
    c: Radius(g42) = 1
    c: Vertical(g42,g38)
    c: Symmetric(g25,g25,g43)
    c: Horizontal(g43,g42)
    c: Radius(g44) = 2.6
    c: Horizontal(g44,g34)
    c: DistanceX(g44,g28) = 8
    c: Radius(g45) = 2.6
    c: Horizontal(g44,g45)
    c: DistanceX(g34,g45) = 8
    c: Radius(g46) = 2.6
    c: Radius(g47) = 2.6
    c: Radius(g48) = 2.6
    c: Vertical(g46,g48)
    c: DistanceY(g44,g46) = 5
    c: DistanceY(g48,g44) = 5
    c: DistanceX(g46,g44) = 28
    c: Radius(g49) = 2.6
    c: Vertical(g47,g49)
    c: Horizontal(g46,g47)
    c: Horizontal(g48,g49)
    c: DistanceX(g45,g47) = 28
FEATURE [PartDesign::Body] Body003
  Group = -> [Pad003,Pocket001,Pocket002,Pocket003,Sketch011,Pocket006]
  Origin = -> Origin006
  Tip = -> Pocket006
FEATURE [PartDesign::Pad] Pad003
  Length = 16
  Length2 = 100
  Midplane = true
  Profile = -> Sketch003
  Type = 0
FEATURE [Sketcher::SketchObject] Sketch004
  AttachmentOffset = pos=(0,0,8) rot=(0,0,1;0rad)
  MapMode = 2
  Placement = pos=(0,0,8) rot=(0,0,1;0rad)
  Support = -> [Part002]
  sketch-geometry (14):
    g0: LineSegment StartX=-44 StartY=-118.868 StartZ=0 EndX=-44 EndY=-114.249 EndZ=0
    g1: LineSegment StartX=-44 StartY=-114.249 StartZ=0 EndX=-48 EndY=-111.94 EndZ=0
    g2: LineSegment StartX=-48 StartY=-111.94 StartZ=0 EndX=-52 EndY=-114.249 EndZ=0
    g3: LineSegment StartX=-52 StartY=-114.249 StartZ=0 EndX=-52 EndY=-118.868 EndZ=0
    g4: LineSegment StartX=-52 StartY=-118.868 StartZ=0 EndX=-48 EndY=-121.178 EndZ=0
    g5: LineSegment StartX=-48 StartY=-121.178 StartZ=0 EndX=-44 EndY=-118.868 EndZ=0
    g6: Circle [constr] CenterX=-48 CenterY=-116.559 CenterZ=0 NormalX=0 NormalY=0 NormalZ=1 AngleXU=0 Radius=4.6188
    g7: LineSegment StartX=52 StartY=-118.868 StartZ=0 EndX=52 EndY=-114.249 EndZ=0
    g8: LineSegment StartX=52 StartY=-114.249 StartZ=0 EndX=48 EndY=-111.94 EndZ=0
    g9: LineSegment StartX=48 StartY=-111.94 StartZ=0 EndX=44 EndY=-114.249 EndZ=0
    g10: LineSegment StartX=44 StartY=-114.249 StartZ=0 EndX=44 EndY=-118.868 EndZ=0
    g11: LineSegment StartX=44 StartY=-118.868 StartZ=0 EndX=48 EndY=-121.178 EndZ=0
    g12: LineSegment StartX=48 StartY=-121.178 StartZ=0 EndX=52 EndY=-118.868 EndZ=0
    g13: Circle [constr] CenterX=48 CenterY=-116.559 CenterZ=0 NormalX=0 NormalY=0 NormalZ=1 AngleXU=0 Radius=4.6188
  constraints (30):
    c: Coincident(g0,g1)
    c: Coincident(g1,g2)
    c: Coincident(g2,g3)
    c: Coincident(g3,g4)
    c: Coincident(g4,g5)
    c: Coincident(g5,g0)
    c: Equal(g0, g1-g5) x5
    c: PointOnObject(g0,g6)
    c: PointOnObject(g1,g6)
    c: PointOnObject(g2,g6)
    c: PointOnObject(g3,g6)
    c: PointOnObject(g4,g6)
    c: PointOnObject(g5,g6)
    c: Vertical(g4,g6)
    c: DistanceX(g2,g0) = 8
    c: Coincident(g7,g8)
    c: Coincident(g8,g9)
    c: Coincident(g9,g10)
    c: Coincident(g10,g11)
    c: Coincident(g11,g12)
    c: Coincident(g12,g7)
    c: Equal(g7, g8-g12) x5
    c: PointOnObject(g7,g13)
    c: PointOnObject(g8,g13)
    c: PointOnObject(g9,g13)
    c: PointOnObject(g10,g13)
    c: PointOnObject(g11,g13)
    c: PointOnObject(g12,g13)
    c: Vertical(g11,g13)
    c: DistanceX(g9,g7) = 8
FEATURE [PartDesign::Pocket] Pocket001
  BaseFeature = -> Pad003
  Length = 18
  Length2 = 100
  Profile = -> Sketch004
  Reversed = true
  Type = 0
FEATURE [Sketcher::SketchObject] Sketch005
  AttachmentOffset = pos=(0,0,8) rot=(0,0,1;0rad)
  MapMode = 2
  Placement = pos=(0,0,8) rot=(0,0,1;0rad)
  Support = -> [Part002]
  sketch-geometry (2):
    g0: Circle CenterX=-48 CenterY=-116.559 CenterZ=0 NormalX=0 NormalY=0 NormalZ=1 AngleXU=0 Radius=2.6
    g1: Circle CenterX=48 CenterY=-116.559 CenterZ=0 NormalX=0 NormalY=0 NormalZ=1 AngleXU=0 Radius=2.6
  constraints (2):
    c: Radius(g0) = 2.6
    c: Radius(g1) = 2.6
FEATURE [PartDesign::Pocket] Pocket002
  BaseFeature = -> Pocket001
  Length = 80
  Length2 = 100
  Profile = -> Sketch005
  Reversed = true
  Type = 0
FEATURE [Sketcher::SketchObject] Sketch006
  AttachmentOffset = pos=(0,0,30) rot=(0,0,1;0rad)
  MapMode = 2
  Placement = pos=(0,0,30) rot=(0,0,1;0rad)
  Support = -> [Part002]
  sketch-geometry (2):
    g0: Circle CenterX=-48 CenterY=-116.559 CenterZ=0 NormalX=0 NormalY=0 NormalZ=1 AngleXU=0 Radius=5
    g1: Circle CenterX=48 CenterY=-116.559 CenterZ=0 NormalX=0 NormalY=0 NormalZ=1 AngleXU=0 Radius=5
  constraints (2):
    c: Radius(g0) = 5
    c: Radius(g1) = 5
FEATURE [PartDesign::Pocket] Pocket003
  BaseFeature = -> Pocket002
  Length = 80
  Length2 = 100
  Profile = -> Sketch006
  Reversed = true
  Type = 0
FEATURE [App::Part] Part003  label="Cable Chain"
  Group = -> [Body004,Body005]
  Origin = -> Origin007
FEATURE [Sketcher::SketchObject] Sketch009
  AttachmentOffset = pos=(0,0,-121.29) rot=(0,0,1;0rad)
  ExternalGeometry = -> [Part__Feature007]
  MapMode = 2
  Placement = pos=(0,0,-121.29) rot=(0,0,1;0rad)
  Support = -> [Part003]
  sketch-geometry (12):
    g0: LineSegment StartX=-250 StartY=-46.5 StartZ=0 EndX=107.755 EndY=-46.5 EndZ=0
    g1: LineSegment StartX=-250 StartY=-66.5 StartZ=0 EndX=127.755 EndY=-66.5 EndZ=0
    g2: LineSegment StartX=0 StartY=11.5 StartZ=0 EndX=127.755 EndY=11.5 EndZ=0
    g3: LineSegment StartX=0 StartY=-8.5 StartZ=0 EndX=107.755 EndY=-8.5 EndZ=0
    g4: LineSegment StartX=124.755 StartY=-25.5 StartZ=0 EndX=124.755 EndY=-29.5 EndZ=0
    g5: LineSegment StartX=144.755 StartY=-5.5 StartZ=0 EndX=144.755 EndY=-49.5 EndZ=0
    g6: ArcOfCircle CenterX=127.755 CenterY=-5.5 CenterZ=0 NormalX=0 NormalY=0 NormalZ=1 AngleXU=0 Radius=17 StartAngle=0 EndAngle=1.5708
    g7: ArcOfCircle CenterX=127.755 CenterY=-49.5 CenterZ=0 NormalX=0 NormalY=0 NormalZ=1 AngleXU=0 Radius=17 StartAngle=4.71239 EndAngle=6.28319
    g8: ArcOfCircle CenterX=107.755 CenterY=-25.5 CenterZ=0 NormalX=0 NormalY=0 NormalZ=1 AngleXU=0 Radius=17 StartAngle=0 EndAngle=1.5708
    g9: ArcOfCircle CenterX=107.755 CenterY=-29.5 CenterZ=0 NormalX=0 NormalY=0 NormalZ=1 AngleXU=0 Radius=17 StartAngle=4.71239 EndAngle=6.28319
    g10: LineSegment StartX=0 StartY=11.5 StartZ=0 EndX=0 EndY=-8.5 EndZ=0
    g11: LineSegment StartX=-250 StartY=-46.5 StartZ=0 EndX=-250 EndY=-66.5 EndZ=0
  constraints (31):
    c: Horizontal(g0)
    c: Horizontal(g1)
    c: DistanceY(g1,g0) = 20
    c: Vertical(g0,g1)
    c: Horizontal(g2)
    c: Horizontal(g3)
    c: DistanceY(g3,g2) = 20
    c: DistanceY(g0,g3) = 38
    c: Tangent(g2,g6) = 1.5708
    c: Tangent(g5,g6) = 1.5708
    c: Tangent(g1,g7) = -1.5708
    c: Tangent(g5,g7) = 1.5708
    c: Tangent(g3,g8) = 1.5708
    c: Tangent(g4,g8) = 1.5708
    c: Tangent(g0,g9) = -1.5708
    c: Tangent(g4,g9) = 1.5708
    c: Vertical(g4,g4)
    c: Vertical(g5,g5)
    c: DistanceX(g4,g5) = 20
    c: Radius(g8) = 17
    c: Radius(g6) = 17
    c: Vertical(g3,g0)
    c: Vertical(g2,g1)
    c: Vertical(g0,g-3)
    c: Coincident(g10,g2)
    c: Coincident(g10,g3)
    c: Coincident(g11,g0)
    c: Coincident(g11,g1)
    c: Horizontal(g1,g-3)
    c: Vertical(g2,g3)
    c: Vertical(g2,g-1)
FEATURE [PartDesign::Body] Body004
  Group = -> [Pad004]
  Origin = -> Origin008
  Tip = -> Pad004
FEATURE [PartDesign::Pad] Pad004
  Length = 38
  Length2 = 100
  Profile = -> Sketch009
  Type = 0
FEATURE [Sketcher::SketchObject] Sketch010
  AttachmentOffset = pos=(0,100,88.5) rot=(0,0,1;0rad)
  ExternalGeometry = -> [Sketch009]
  MapMode = 3
  Placement = pos=(0,-88.5,100) rot=(1,0,0;1.5708rad)
  Support = -> [Part003]
  sketch-geometry (12):
    g0: Circle CenterX=-30 CenterY=-191.29 CenterZ=0 NormalX=0 NormalY=0 NormalZ=1 AngleXU=0 Radius=2.6
    g1: Circle CenterX=-30 CenterY=-251.29 CenterZ=0 NormalX=0 NormalY=0 NormalZ=1 AngleXU=0 Radius=2.6
    g2: Circle CenterX=30 CenterY=-191.29 CenterZ=0 NormalX=0 NormalY=0 NormalZ=1 AngleXU=0 Radius=2.6
    g3: Circle CenterX=30 CenterY=-251.29 CenterZ=0 NormalX=0 NormalY=0 NormalZ=1 AngleXU=0 Radius=2.6
    g4: LineSegment StartX=-35 StartY=-181.29 StartZ=0 EndX=35 EndY=-181.29 EndZ=0
    g5: LineSegment StartX=40 StartY=-186.29 StartZ=0 EndX=40 EndY=-256.29 EndZ=0
    g6: LineSegment StartX=35 StartY=-261.29 StartZ=0 EndX=-35 EndY=-261.29 EndZ=0
    g7: LineSegment StartX=-40 StartY=-256.29 StartZ=0 EndX=-40 EndY=-186.29 EndZ=0
    g8: ArcOfCircle CenterX=-35 CenterY=-186.29 CenterZ=0 NormalX=0 NormalY=0 NormalZ=1 AngleXU=0 Radius=5 StartAngle=1.5708 EndAngle=3.14159
    g9: ArcOfCircle CenterX=-35 CenterY=-256.29 CenterZ=0 NormalX=0 NormalY=0 NormalZ=1 AngleXU=0 Radius=5 StartAngle=3.14159 EndAngle=4.71239
    g10: ArcOfCircle CenterX=35 CenterY=-256.29 CenterZ=0 NormalX=0 NormalY=0 NormalZ=1 AngleXU=0 Radius=5 StartAngle=4.71239 EndAngle=6.28319
    g11: ArcOfCircle CenterX=35 CenterY=-186.29 CenterZ=0 NormalX=0 NormalY=0 NormalZ=1 AngleXU=0 Radius=5 StartAngle=8.08e-14 EndAngle=1.5708
  constraints (30):
    c: Radius(g0) = 2.6
    c: Radius(g1) = 2.6
    c: DistanceY(g1,g0) = 60
    c: Symmetric(g0,g1,g-3)
    c: Radius(g2) = 2.6
    c: Radius(g3) = 2.6
    c: Vertical(g2,g3)
    c: Horizontal(g3,g1)
    c: Symmetric(g0,g2,g-2)
    c: DistanceX(g0,g2) = 60
    c: Horizontal(g4)
    c: Horizontal(g6)
    c: Vertical(g5)
    c: Vertical(g7)
    c: Tangent(g4,g8) = 1.5708
    c: Tangent(g7,g8) = 1.5708
    c: Tangent(g6,g9) = 1.5708
    c: Tangent(g7,g9) = 1.5708
    c: Tangent(g5,g10) = 1.5708
    c: Tangent(g6,g10) = 1.5708
    c: Tangent(g4,g11) = 1.5708
    c: Tangent(g5,g11) = 1.5708
    c: Radius(g8) = 5
    c: Radius(g11) = 5
    c: Radius(g9) = 5
    c: Radius(g10) = 5
    c: DistanceY(g0,g4) = 10
    c: DistanceX(g7,g0) = 10
    c: DistanceX(g2,g5) = 10
    c: DistanceY(g6,g1) = 10
FEATURE [PartDesign::Body] Body005
  Group = -> [Sketch010,Pad005]
  Origin = -> Origin009
  Tip = -> Pad005
FEATURE [PartDesign::Pad] Pad005
  Length = 6
  Length2 = 100
  Profile = -> Sketch010
  Type = 0
FEATURE [Sketcher::SketchObject] Sketch011
  AttachmentOffset = pos=(0,0,86.5) rot=(0,0,1;0rad)
  ExternalGeometry = -> [Sketch003]
  MapMode = 3
  Placement = pos=(0,-86.5,1.92e-14) rot=(1,0,0;1.5708rad)
  Support = -> [Part002]
  sketch-geometry (4):
    g0: LineSegment StartX=-16 StartY=94 StartZ=0 EndX=16 EndY=94 EndZ=0
    g1: LineSegment StartX=16 StartY=94 StartZ=0 EndX=16 EndY=62 EndZ=0
    g2: LineSegment StartX=16 StartY=62 StartZ=0 EndX=-16 EndY=62 EndZ=0
    g3: LineSegment StartX=-16 StartY=62 StartZ=0 EndX=-16 EndY=94 EndZ=0
  constraints (12):
    c: Coincident(g0,g1)
    c: Coincident(g1,g2)
    c: Coincident(g2,g3)
    c: Coincident(g3,g0)
    c: Horizontal(g0)
    c: Horizontal(g2)
    c: Vertical(g1)
    c: Vertical(g3)
    c: Vertical(g0,g-4)
    c: Vertical(g0,g-6)
    c: Horizontal(g0,g-3)
    c: Horizontal(g1,g-5)
FEATURE [PartDesign::Pocket] Pocket006
  BaseFeature = -> Pocket003
  Length = 8
  Length2 = 100
  Profile = -> Sketch011
  Type = 0
FEATURE [App::Part] Part004  label="Plastic Flange Bracket"
  Group = -> [Body006]
  Origin = -> Origin010
FEATURE [Sketcher::SketchObject] Sketch012
  MapMode = 2
  Support = -> [Part004]
  sketch-geometry (8):
    g0: LineSegment StartX=-36.289 StartY=-68.365 StartZ=0 EndX=-32.289 EndY=-68.365 EndZ=0
    g1: LineSegment StartX=-32.289 StartY=-68.365 StartZ=0 EndX=-32.289 EndY=-69.765 EndZ=0
    g2: LineSegment StartX=-32.289 StartY=-69.765 StartZ=0 EndX=-36.289 EndY=-69.765 EndZ=0
    g3: LineSegment StartX=-36.289 StartY=-69.765 StartZ=0 EndX=-36.289 EndY=-68.365 EndZ=0
    g4: LineSegment StartX=-37.689 StartY=-66.365 StartZ=0 EndX=-30.889 EndY=-66.365 EndZ=0
    g5: LineSegment StartX=-30.889 StartY=-66.365 StartZ=0 EndX=-30.889 EndY=-70.765 EndZ=0
    g6: LineSegment StartX=-30.889 StartY=-70.765 StartZ=0 EndX=-37.689 EndY=-70.765 EndZ=0
    g7: LineSegment StartX=-37.689 StartY=-70.765 StartZ=0 EndX=-37.689 EndY=-66.365 EndZ=0
  constraints (22):
    c: Coincident(g0,g1)
    c: Coincident(g1,g2)
    c: Coincident(g2,g3)
    c: Coincident(g3,g0)
    c: Horizontal(g0)
    c: Horizontal(g2)
    c: Vertical(g1)
    c: Vertical(g3)
    c: DistanceX(g0,g0) = 4
    c: DistanceY(g1,g1) = 1.4
    c: Coincident(g4,g5)
    c: Coincident(g5,g6)
    c: Coincident(g6,g7)
    c: Coincident(g7,g4)
    c: Horizontal(g4)
    c: Horizontal(g6)
    c: Vertical(g5)
    c: Vertical(g7)
    c: DistanceX(g4,g0) = 1.4
    c: DistanceX(g0,g4) = 1.4
    c: DistanceY(g0,g4) = 2
    c: DistanceY(g5,g1) = 1
FEATURE [PartDesign::Body] Body006
  Group = -> [Pad006]
  Origin = -> Origin011
  Tip = -> Pad006
FEATURE [PartDesign::Pad] Pad006
  Length = 1.4
  Length2 = 100
  Profile = -> Sketch012
  Type = 0
FEATURE [App::Part] Part005  label="Cable Chain Support"
  Group = -> [Body006021,Body006022]
  Origin = -> Origin012
FEATURE [Sketcher::SketchObject] Sketch013
  ExternalGeometry = -> [Pad004]
  MapMode = 4
  Placement = pos=(0,0,0) rot=(0.57735,0.57735,0.57735;2.0944rad)
  Support = -> [Part005]
  sketch-geometry (10):
    g0: LineSegment StartX=44.9115 StartY=-121.29 StartZ=0 EndX=36.9115 EndY=-121.29 EndZ=0
    g1: LineSegment StartX=-61.0885 StartY=-59.3229 StartZ=0 EndX=-61.0885 EndY=-42.9612 EndZ=0
    g2: LineSegment StartX=-61.0885 StartY=-42.9612 StartZ=0 EndX=-45.0885 EndY=-42.9612 EndZ=0
    g3: LineSegment StartX=-45.0885 StartY=-42.9612 StartZ=0 EndX=-45.0885 EndY=-50.639 EndZ=0
    g4: LineSegment StartX=-61.0885 StartY=-59.3229 StartZ=0 EndX=-3.9523 EndY=-59.3229 EndZ=0
    g5: LineSegment StartX=36.9115 StartY=-70.322 StartZ=0 EndX=36.9115 EndY=-121.29 EndZ=0
    g6: LineSegment StartX=36.9115 StartY=-70.322 StartZ=0 EndX=-3.9523 EndY=-59.3229 EndZ=0
    g7: LineSegment StartX=0.451654 StartY=-50.639 StartZ=0 EndX=44.9115 EndY=-62.6061 EndZ=0
    g8: LineSegment StartX=0.451654 StartY=-50.639 StartZ=0 EndX=-45.0885 EndY=-50.639 EndZ=0
    g9: LineSegment StartX=44.9115 StartY=-62.6061 StartZ=0 EndX=44.9115 EndY=-121.29 EndZ=0
  constraints (23):
    c: Horizontal(g0)
    c: Vertical(g1)
    c: DistanceX(g0,g0) = 8
    c: Coincident(g2,g1)
    c: Horizontal(g2)
    c: Coincident(g3,g2)
    c: Vertical(g3)
    c: Coincident(g1,g4)
    c: Horizontal(g4)
    c: Coincident(g5,g0)
    c: Coincident(g6,g5)
    c: Coincident(g6,g4)
    c: Parallel(g7,g6)
    c: Vertical(g7,g0)
    c: Horizontal(g7,g3)
    c: Coincident(g8,g7)
    c: Coincident(g8,g3)
    c: Coincident(g9,g7)
    c: Coincident(g9,g0)
    c: Vertical(g5,g0)
    c: Block(g1)
    c: Block(g2)
    c: DistanceX(g1,g0) = 98
FEATURE [PartDesign::Body] Body006021  label="Cable Chain Support Main"
  Group = -> [Pad007,Sketch015,Pocket008,Pocket009,Pocket010,Sketch019,Pocket011,Pocket014]
  Origin = -> Origin013
  Tip = -> Pocket014
FEATURE [PartDesign::Pad] Pad007
  Length = 72
  Length2 = 100
  Midplane = true
  Profile = -> Sketch013
  Type = 0
FEATURE [Sketcher::SketchObject] Sketch015
  ExternalGeometry = -> [Pad007]
  MapMode = 2
  Placement = pos=(-210,3226,645) rot=(0,0,1;0rad)
  Support = -> [Sketch015]
  sketch-geometry (3):
    g0: Circle CenterX=182 CenterY=-3279.56 CenterZ=0 NormalX=0 NormalY=0 NormalZ=1 AngleXU=0 Radius=2.6
    g1: Circle CenterX=210 CenterY=-3279.56 CenterZ=0 NormalX=0 NormalY=0 NormalZ=1 AngleXU=0 Radius=2.6
    g2: Circle CenterX=238 CenterY=-3279.56 CenterZ=0 NormalX=0 NormalY=0 NormalZ=1 AngleXU=0 Radius=2.6
  constraints (5):
    c: Vertical(g0,g-3)
    c: Vertical(g1,g-4)
    c: Vertical(g2,g-5)
    c: Horizontal(g0,g1)
    c: Horizontal(g1,g2)
FEATURE [PartDesign::Pocket] Pocket008
  BaseFeature = -> Pad007
  Length = 5
  Length2 = 100
  Profile = -> Sketch015
  Type = 1
FEATURE [Sketcher::SketchObject] Sketch016
  MapMode = 2
  Support = -> [Part005]
  sketch-geometry (2):
    g0: Circle CenterX=0 CenterY=-25.1 CenterZ=0 NormalX=0 NormalY=0 NormalZ=1 AngleXU=0 Radius=2.6
    g1: Circle CenterX=0 CenterY=-25.1 CenterZ=0 NormalX=0 NormalY=0 NormalZ=1 AngleXU=0 Radius=2.6
  constraints (2):
    c: Radius(g0) = 2.6
    c: Radius(g1) = 2.6
FEATURE [PartDesign::Pocket] Pocket009
  BaseFeature = -> Pocket008
  Length = 5
  Length2 = 100
  Profile = -> Sketch016
  Type = 1
FEATURE [PartDesign::Body] Body006022
  Group = -> [Pad008,Pocket013]
  Origin = -> Origin014
  Tip = -> Pocket013
FEATURE [Sketcher::SketchObject] Sketch017
  ExternalGeometry = -> [Pad007]
  MapMode = 4
  Placement = pos=(0,0,0) rot=(0.57735,0.57735,0.57735;2.0944rad)
  Support = -> [Part005]
  sketch-geometry (4):
    g0: LineSegment StartX=-20.1 StartY=0 StartZ=0 EndX=-29.4088 EndY=0 EndZ=0
    g1: LineSegment StartX=-29.4088 StartY=0 StartZ=0 EndX=-29.4088 EndY=-50.639 EndZ=0
    g2: LineSegment StartX=-29.4088 StartY=-50.639 StartZ=0 EndX=-20.1 EndY=-50.639 EndZ=0
    g3: LineSegment StartX=-20.1 StartY=-50.639 StartZ=0 EndX=-20.1 EndY=0 EndZ=0
FEATURE [PartDesign::Pad] Pad008
  Length = 10
  Length2 = 100
  Midplane = true
  Profile = -> Sketch017
  Type = 0
FEATURE [Sketcher::SketchObject] Sketch018
  ExternalGeometry = -> [Sketch009,Pocket009]
  MapMode = 3
  Placement = pos=(0,0,0) rot=(1,0,0;1.5708rad)
  Support = -> [Part005]
  sketch-geometry (3):
    g0: Circle CenterX=0.007718 CenterY=-112.29 CenterZ=0 NormalX=0 NormalY=0 NormalZ=1 AngleXU=0 Radius=2.1
    g1: Circle CenterX=0.007718 CenterY=-90.29 CenterZ=0 NormalX=0 NormalY=0 NormalZ=1 AngleXU=0 Radius=2.1
    g2: Circle CenterX=-9.99228 CenterY=-101.29 CenterZ=0 NormalX=0 NormalY=0 NormalZ=1 AngleXU=0 Radius=2.1
  constraints (8):
    c: Radius(g0) = 2.1
    c: Radius(g1) = 2.1
    c: Vertical(g1,g0)
    c: DistanceY(g0,g1) = 22
    c: Radius(g2) = 2.1
    c: DistanceX(g0,g2) = -10
    c: DistanceY(g0,g2) = 11
    c: DistanceY(g-4,g0) = 9
FEATURE [PartDesign::Pocket] Pocket010  label="Cable Chain Fix"
  BaseFeature = -> Pocket009
  Length = 5
  Length2 = 100
  Profile = -> Sketch018
  Type = 1
FEATURE [Sketcher::SketchObject] Sketch019
  ExternalGeometry = -> [Sketch018,Pocket010]
  MapMode = 5
  Placement = pos=(0,44.9115,0) rot=(0,0.707107,0.707107;3.14159rad)
  Support = -> [Pocket010]
  sketch-geometry (21):
    g0: LineSegment StartX=3.49228 StartY=-92.3107 StartZ=0 EndX=3.49228 EndY=-88.2693 EndZ=0
    g1: LineSegment StartX=3.49228 StartY=-88.2693 StartZ=0 EndX=-0.007718 EndY=-86.2485 EndZ=0
    g2: LineSegment StartX=-0.007718 StartY=-86.2485 StartZ=0 EndX=-3.50772 EndY=-88.2693 EndZ=0
    g3: LineSegment StartX=-3.50772 StartY=-88.2693 StartZ=0 EndX=-3.50772 EndY=-92.3107 EndZ=0
    g4: LineSegment StartX=-3.50772 StartY=-92.3107 StartZ=0 EndX=-0.007718 EndY=-94.3315 EndZ=0
    g5: LineSegment StartX=-0.007718 StartY=-94.3315 StartZ=0 EndX=3.49228 EndY=-92.3107 EndZ=0
    g6: Circle [constr] CenterX=-0.007718 CenterY=-90.29 CenterZ=0 NormalX=0 NormalY=0 NormalZ=1 AngleXU=0 Radius=4.04145
    g7: LineSegment StartX=6.49228 StartY=-103.311 StartZ=0 EndX=9.99228 EndY=-105.331 EndZ=0
    g8: LineSegment StartX=9.99228 StartY=-105.331 StartZ=0 EndX=13.4923 EndY=-103.311 EndZ=0
    g9: LineSegment StartX=13.4923 StartY=-103.311 StartZ=0 EndX=13.4923 EndY=-99.2693 EndZ=0
    g10: LineSegment StartX=13.4923 StartY=-99.2693 StartZ=0 EndX=9.99228 EndY=-97.2485 EndZ=0
    g11: LineSegment StartX=9.99228 StartY=-97.2485 StartZ=0 EndX=6.49228 EndY=-99.2693 EndZ=0
    g12: LineSegment StartX=6.49228 StartY=-99.2693 StartZ=0 EndX=6.49228 EndY=-103.311 EndZ=0
    g13: Circle [constr] CenterX=9.99228 CenterY=-101.29 CenterZ=0 NormalX=0 NormalY=0 NormalZ=1 AngleXU=0 Radius=4.04145
    g14: LineSegment StartX=3.49228 StartY=-114.311 StartZ=0 EndX=3.49228 EndY=-110.269 EndZ=0
    g15: LineSegment StartX=3.49228 StartY=-110.269 StartZ=0 EndX=-0.007718 EndY=-108.249 EndZ=0
    g16: LineSegment StartX=-0.007718 StartY=-108.249 StartZ=0 EndX=-3.50772 EndY=-110.269 EndZ=0
    g17: LineSegment StartX=-3.50772 StartY=-110.269 StartZ=0 EndX=-3.50772 EndY=-114.311 EndZ=0
    g18: LineSegment StartX=-3.50772 StartY=-114.311 StartZ=0 EndX=-0.007718 EndY=-116.331 EndZ=0
    g19: LineSegment StartX=-0.007718 StartY=-116.331 StartZ=0 EndX=3.49228 EndY=-114.311 EndZ=0
    g20: Circle [constr] CenterX=-0.007718 CenterY=-112.29 CenterZ=0 NormalX=0 NormalY=0 NormalZ=1 AngleXU=0 Radius=4.04145
  constraints (51):
    c: Coincident(g0,g1)
    c: Coincident(g1,g2)
    c: Coincident(g2,g3)
    c: Coincident(g3,g4)
    c: Coincident(g4,g5)
    c: Coincident(g5,g0)
    c: Equal(g0, g1-g5) x5
    c: PointOnObject(g0,g6)
    c: PointOnObject(g1,g6)
    c: PointOnObject(g2,g6)
    c: PointOnObject(g3,g6)
    c: PointOnObject(g4,g6)
    c: PointOnObject(g5,g6)
    c: Vertical(g6,g4)
    c: DistanceX(g2,g0) = 7
    c: Horizontal(g6,g-5)
    c: Vertical(g6,g-5)
    c: Coincident(g7,g8)
    c: Coincident(g8,g9)
    c: Coincident(g9,g10)
    c: Coincident(g10,g11)
    c: Coincident(g11,g12)
    c: Coincident(g12,g7)
    c: Equal(g7, g8-g12) x5
    c: PointOnObject(g7,g13)
    c: PointOnObject(g8,g13)
    c: PointOnObject(g9,g13)
    c: PointOnObject(g10,g13)
    c: PointOnObject(g11,g13)
    c: PointOnObject(g12,g13)
    c: Coincident(g14,g15)
    c: Coincident(g15,g16)
    c: Coincident(g16,g17)
    c: Coincident(g17,g18)
    c: Coincident(g18,g19)
    c: Coincident(g19,g14)
    c: Equal(g14, g15-g19) x5
    c: PointOnObject(g14,g20)
    c: PointOnObject(g15,g20)
    c: PointOnObject(g16,g20)
    c: PointOnObject(g17,g20)
    c: PointOnObject(g18,g20)
    c: PointOnObject(g19,g20)
    c: Vertical(g13,g7)
    c: Vertical(g20,g18)
    c: DistanceX(g11,g9) = 7
    c: DistanceX(g16,g14) = 7
    c: Horizontal(g13,g-3)
    c: Vertical(g13,g-3)
    c: Horizontal(g20,g-4)
    c: Vertical(g20,g-4)
FEATURE [PartDesign::Pocket] Pocket011
  BaseFeature = -> Pocket010
  Length = 3.1
  Length2 = 100
  Profile = -> Sketch019
  Type = 0
FEATURE [Sketcher::SketchObject] Sketch021
  MapMode = 5
  Support = -> [Pad008]
  sketch-geometry (2):
    g0: Circle CenterX=0 CenterY=-13.1 CenterZ=0 NormalX=0 NormalY=0 NormalZ=1 AngleXU=0 Radius=2.6
    g1: Circle CenterX=0 CenterY=-25.1 CenterZ=0 NormalX=0 NormalY=0 NormalZ=1 AngleXU=0 Radius=2.6
FEATURE [PartDesign::Pocket] Pocket013
  BaseFeature = -> Pad008
  Length = 5
  Length2 = 100
  Profile = -> Sketch021
  Type = 1
FEATURE [Sketcher::SketchObject] Sketch022
  MapMode = 5
  Placement = pos=(0,0,-59.3229) rot=(1,0,0;3.14159rad)
  Support = -> [Pocket011]
  sketch-geometry (14):
    g0: LineSegment StartX=4 StartY=22.7906 StartZ=0 EndX=4 EndY=27.4094 EndZ=0
    g1: LineSegment StartX=4 StartY=27.4094 StartZ=0 EndX=0 EndY=29.7188 EndZ=0
    g2: LineSegment StartX=0 StartY=29.7188 StartZ=0 EndX=-4 EndY=27.4094 EndZ=0
    g3: LineSegment StartX=-4 StartY=27.4094 StartZ=0 EndX=-4 EndY=22.7906 EndZ=0
    g4: LineSegment StartX=-4 StartY=22.7906 StartZ=0 EndX=0 EndY=20.4812 EndZ=0
    g5: LineSegment StartX=0 StartY=20.4812 StartZ=0 EndX=4 EndY=22.7906 EndZ=0
    g6: Circle [constr] CenterX=0 CenterY=25.1 CenterZ=0 NormalX=0 NormalY=0 NormalZ=1 AngleXU=0 Radius=4.6188
    g7: LineSegment StartX=4 StartY=22.8147 StartZ=0 EndX=4 EndY=27.4335 EndZ=0
    g8: LineSegment StartX=4 StartY=27.4335 StartZ=0 EndX=-4e-16 EndY=29.7429 EndZ=0
    g9: LineSegment StartX=-4e-16 StartY=29.7429 StartZ=0 EndX=-4 EndY=27.4335 EndZ=0
    g10: LineSegment StartX=-4 StartY=27.4335 StartZ=0 EndX=-4 EndY=22.8147 EndZ=0
    g11: LineSegment StartX=-4 StartY=22.8147 StartZ=0 EndX=0 EndY=20.5053 EndZ=0
    g12: LineSegment StartX=0 StartY=20.5053 StartZ=0 EndX=4 EndY=22.8147 EndZ=0
    g13: Circle [constr] CenterX=0 CenterY=25.1241 CenterZ=0 NormalX=0 NormalY=0 NormalZ=1 AngleXU=0 Radius=4.6188
  constraints (30):
    c: Coincident(g0,g1)
    c: Coincident(g1,g2)
    c: Coincident(g2,g3)
    c: Coincident(g3,g4)
    c: Coincident(g4,g5)
    c: Coincident(g5,g0)
    c: Equal(g0, g1-g5) x5
    c: PointOnObject(g0,g6)
    c: PointOnObject(g1,g6)
    c: PointOnObject(g2,g6)
    c: PointOnObject(g3,g6)
    c: PointOnObject(g4,g6)
    c: PointOnObject(g5,g6)
    c: Coincident(g7,g8)
    c: Coincident(g8,g9)
    c: Coincident(g9,g10)
    c: Coincident(g10,g11)
    c: Coincident(g11,g12)
    c: Coincident(g12,g7)
    c: Equal(g7, g8-g12) x5
    c: PointOnObject(g7,g13)
    c: PointOnObject(g8,g13)
    c: PointOnObject(g9,g13)
    c: PointOnObject(g10,g13)
    c: PointOnObject(g11,g13)
    c: PointOnObject(g12,g13)
    c: Vertical(g6,g4)
    c: Vertical(g13,g11)
    c: DistanceX(g2,g0) = 8
    c: DistanceX(g9,g7) = 8
FEATURE [PartDesign::Pocket] Pocket014
  BaseFeature = -> Pocket011
  Length = 4
  Length2 = 100
  Profile = -> Sketch022
  Type = 0
FEATURE [App::Part] Part006  label="Front"
  Group = -> [Body006021002]
  Origin = -> Origin015
FEATURE [Sketcher::SketchObject] Sketch023  label="FrontContour"
  MapMode = 2
  Support = -> [Part006]
  sketch-geometry (9):
    g0: LineSegment StartX=-65 StartY=20.59 StartZ=0 EndX=65 EndY=20.59 EndZ=0
    g1: LineSegment StartX=65 StartY=-129.41 StartZ=0 EndX=-65 EndY=-129.41 EndZ=0
    g2: ArcOfCircle CenterX=-65 CenterY=15.59 CenterZ=0 NormalX=0 NormalY=0 NormalZ=1 AngleXU=0 Radius=5 StartAngle=1.5708 EndAngle=3.14363
    g3: ArcOfCircle CenterX=65 CenterY=15.59 CenterZ=0 NormalX=0 NormalY=0 NormalZ=1 AngleXU=0 Radius=5 StartAngle=6.28115 EndAngle=7.85398
    g4: ArcOfCircle CenterX=-65 CenterY=-124.41 CenterZ=0 NormalX=0 NormalY=0 NormalZ=1 AngleXU=0 Radius=5 StartAngle=3.14363 EndAngle=4.71239
    g5: ArcOfCircle CenterX=65 CenterY=-124.41 CenterZ=0 NormalX=0 NormalY=0 NormalZ=1 AngleXU=0 Radius=5 StartAngle=4.71239 EndAngle=6.28115
    g6: GeomPoint X=0 Y=20.59 Z=0
    g7: LineSegment StartX=-70 StartY=15.5798 StartZ=0 EndX=-70 EndY=-124.42 EndZ=0
    g8: LineSegment StartX=70 StartY=15.5798 StartZ=0 EndX=70 EndY=-124.42 EndZ=0
  constraints (24):
    c: Horizontal(g0)
    c: Horizontal(g1)
    c: Tangent(g0,g2) = 1.5708
    c: Tangent(g0,g3) = 1.5708
    c: Tangent(g1,g4) = 1.5708
    c: Tangent(g1,g5) = 1.5708
    c: Radius(g2) = 5
    c: Symmetric(g0,g0,g6)
    c: Vertical(g6,g-1)
    c: DistanceY(g-1,g6) = 20.59
    c: Coincident(g7,g2)
    c: Coincident(g7,g4)
    c: Vertical(g7)
    c: Coincident(g8,g3)
    c: Coincident(g8,g5)
    c: Vertical(g8)
    c: Horizontal(g3,g2)
    c: DistanceX(g2,g3) = 140
    c: Horizontal(g4,g5)
    c: Equal(g2,g3)
    c: Equal(g3,g5)
    c: Radius(g4) = 5
    c: DistanceY(g5,g3) = 140
    c: Equal(g1,g0)
FEATURE [PartDesign::Body] Body006021002
  Group = -> [Pad009,Sketch025,Hole001,Sketch027,Hole003,Sketch028,Hole004,Sketch029,Hole005,Sketch030,Pocket015,Sketch031,Hole006,Sketch044,Hole,Sketch060,Pocket018,Sketch061,Hole023,Sketch062,Hole024]
  Origin = -> Origin016
  Tip = -> Hole024
FEATURE [PartDesign::Pad] Pad009
  Length = 8
  Length2 = 100
  Profile = -> Sketch023
  Type = 0
FEATURE [PartDesign::Hole] Hole001
  BaseFeature = -> Pad009
  Depth = 25
  DepthType = 0
  Diameter = 5.5
  DrillPoint = 1
  DrillPointAngle = 118
  HoleCutCountersinkAngle = 90
  HoleCutDepth = 3
  HoleCutDiameter = 10
  HoleCutType = 1
  ModelActualThread = false
  Profile = -> Sketch025
  Tapered = false
  TaperedAngle = 90
  ThreadAngle = 0
  ThreadClass = 0
  ThreadCutOffInner = 0
  ThreadCutOffOuter = 0
  ThreadDirection = 0
  ThreadFit = 0
  ThreadPitch = 0
  ThreadSize = 6
  ThreadType = 1
  Threaded = false
FEATURE [PartDesign::Hole] Hole003
  BaseFeature = -> Hole001
  Depth = 25
  DepthType = 0
  Diameter = 7.2
  DrillPoint = 1
  DrillPointAngle = 118
  HoleCutCountersinkAngle = 90
  HoleCutDepth = 3
  HoleCutDiameter = 12
  HoleCutType = 1
  ModelActualThread = false
  Profile = -> Sketch027
  Tapered = false
  TaperedAngle = 90
  ThreadAngle = 0
  ThreadClass = 0
  ThreadCutOffInner = 0
  ThreadCutOffOuter = 0
  ThreadDirection = 0
  ThreadFit = 0
  ThreadPitch = 0
  ThreadSize = 0
  ThreadType = 0
  Threaded = false
FEATURE [Sketcher::SketchObject] Sketch028  label="HiwinHoles"
  MapMode = 5
  Placement = pos=(0,0,8) rot=(0,0,1;0rad)
  Support = -> [Hole003]
  sketch-geometry (40):
    g0: Circle CenterX=-42 CenterY=-35.56 CenterZ=0 NormalX=0 NormalY=0 NormalZ=1 AngleXU=0 Radius=1.5
    g1: Circle CenterX=-14 CenterY=-35.56 CenterZ=0 NormalX=0 NormalY=0 NormalZ=1 AngleXU=0 Radius=1.5
    g2: LineSegment [constr] StartX=-42 StartY=-35.56 StartZ=0 EndX=-14 EndY=-35.56 EndZ=0
    g3: Circle CenterX=14 CenterY=-35.56 CenterZ=0 NormalX=0 NormalY=0 NormalZ=1 AngleXU=0 Radius=1.5
    g4: LineSegment [constr] StartX=-14 StartY=-35.56 StartZ=0 EndX=14 EndY=-35.56 EndZ=0
    g5: Circle CenterX=42 CenterY=-35.56 CenterZ=0 NormalX=0 NormalY=0 NormalZ=1 AngleXU=0 Radius=1.5
    g6: LineSegment [constr] StartX=14 StartY=-35.56 StartZ=0 EndX=42 EndY=-35.56 EndZ=0
    g7: Circle CenterX=-42 CenterY=-50.56 CenterZ=0 NormalX=0 NormalY=0 NormalZ=1 AngleXU=0 Radius=1.5
    g8: LineSegment [constr] StartX=-42 StartY=-35.56 StartZ=0 EndX=-42 EndY=-50.56 EndZ=0
    g9: Circle CenterX=-14 CenterY=-50.56 CenterZ=0 NormalX=0 NormalY=0 NormalZ=1 AngleXU=0 Radius=1.5
    g10: LineSegment [constr] StartX=-42 StartY=-50.56 StartZ=0 EndX=-14 EndY=-50.56 EndZ=0
    g11: Circle CenterX=14 CenterY=-50.56 CenterZ=0 NormalX=0 NormalY=0 NormalZ=1 AngleXU=0 Radius=1.5
    g12: LineSegment [constr] StartX=-14 StartY=-50.56 StartZ=0 EndX=14 EndY=-50.56 EndZ=0
    g13: Circle CenterX=42 CenterY=-50.56 CenterZ=0 NormalX=0 NormalY=0 NormalZ=1 AngleXU=0 Radius=1.5
    g14: LineSegment [constr] StartX=14 StartY=-50.56 StartZ=0 EndX=42 EndY=-50.56 EndZ=0
    g15: Circle CenterX=-42 CenterY=-65.56 CenterZ=0 NormalX=0 NormalY=0 NormalZ=1 AngleXU=0 Radius=1.5
    g16: LineSegment [constr] StartX=-42 StartY=-50.56 StartZ=0 EndX=-42 EndY=-65.56 EndZ=0
    g17: Circle CenterX=-14 CenterY=-65.56 CenterZ=0 NormalX=0 NormalY=0 NormalZ=1 AngleXU=0 Radius=1.5
    g18: LineSegment [constr] StartX=-42 StartY=-65.56 StartZ=0 EndX=-14 EndY=-65.56 EndZ=0
    g19: Circle CenterX=14 CenterY=-65.56 CenterZ=0 NormalX=0 NormalY=0 NormalZ=1 AngleXU=0 Radius=1.5
    g20: LineSegment [constr] StartX=-14 StartY=-65.56 StartZ=0 EndX=14 EndY=-65.56 EndZ=0
    g21: Circle CenterX=42 CenterY=-65.56 CenterZ=0 NormalX=0 NormalY=0 NormalZ=1 AngleXU=0 Radius=1.5
    g22: LineSegment [constr] StartX=14 StartY=-65.56 StartZ=0 EndX=42 EndY=-65.56 EndZ=0
    g23: Circle CenterX=-42 CenterY=-80.56 CenterZ=0 NormalX=0 NormalY=0 NormalZ=1 AngleXU=0 Radius=1.5
    g24: LineSegment [constr] StartX=-42 StartY=-65.56 StartZ=0 EndX=-42 EndY=-80.56 EndZ=0
    g25: Circle CenterX=-14 CenterY=-80.56 CenterZ=0 NormalX=0 NormalY=0 NormalZ=1 AngleXU=0 Radius=1.5
    g26: LineSegment [constr] StartX=-42 StartY=-80.56 StartZ=0 EndX=-14 EndY=-80.56 EndZ=0
    g27: Circle CenterX=14 CenterY=-80.56 CenterZ=0 NormalX=0 NormalY=0 NormalZ=1 AngleXU=0 Radius=1.5
    g28: LineSegment [constr] StartX=-14 StartY=-80.56 StartZ=0 EndX=14 EndY=-80.56 EndZ=0
    g29: Circle CenterX=42 CenterY=-80.56 CenterZ=0 NormalX=0 NormalY=0 NormalZ=1 AngleXU=0 Radius=1.5
    g30: LineSegment [constr] StartX=14 StartY=-80.56 StartZ=0 EndX=42 EndY=-80.56 EndZ=0
    g31: Circle CenterX=-42 CenterY=-95.56 CenterZ=0 NormalX=0 NormalY=0 NormalZ=1 AngleXU=0 Radius=1.5
    g32: LineSegment [constr] StartX=-42 StartY=-80.56 StartZ=0 EndX=-42 EndY=-95.56 EndZ=0
    g33: Circle CenterX=-14 CenterY=-95.56 CenterZ=0 NormalX=0 NormalY=0 NormalZ=1 AngleXU=0 Radius=1.5
    g34: LineSegment [constr] StartX=-42 StartY=-95.56 StartZ=0 EndX=-14 EndY=-95.56 EndZ=0
    g35: Circle CenterX=14 CenterY=-95.56 CenterZ=0 NormalX=0 NormalY=0 NormalZ=1 AngleXU=0 Radius=1.5
    g36: LineSegment [constr] StartX=-14 StartY=-95.56 StartZ=0 EndX=14 EndY=-95.56 EndZ=0
    g37: Circle CenterX=42 CenterY=-95.56 CenterZ=0 NormalX=0 NormalY=0 NormalZ=1 AngleXU=0 Radius=1.5
    g38: LineSegment [constr] StartX=14 StartY=-95.56 StartZ=0 EndX=42 EndY=-95.56 EndZ=0
    g39: GeomPoint X=0 Y=-35.56 Z=0
  constraints (99):
    c: Radius(g0) = 1.5
    c: Equal(g0,g1) = 1.5
    c: Coincident(g0,g2)
    c: Coincident(g1,g2)
    c: Distance(g2) = 28
    c: Angle(g2) = 0
    c: Equal(g0,g3) = 1.5
    c: Coincident(g1,g4)
    c: Coincident(g3,g4)
    c: Equal(g2,g4)
    c: Parallel(g4,g2)
    c: Equal(g0,g5) = 1.5
    c: Coincident(g3,g6)
    c: Coincident(g5,g6)
    c: Equal(g2,g6)
    c: Parallel(g6,g2)
    c: Equal(g0,g7) = 1.5
    c: Coincident(g0,g8)
    c: Coincident(g7,g8)
    c: Distance(g8) = 15
    c: Perpendicular(g8,g2)
    c: Equal(g0,g9) = 1.5
    c: Coincident(g7,g10)
    c: Coincident(g9,g10)
    c: Equal(g2,g10)
    c: Parallel(g10,g2)
    c: Equal(g0,g11) = 1.5
    c: Coincident(g9,g12)
    c: Coincident(g11,g12)
    c: Equal(g2,g12)
    c: Parallel(g12,g2)
    c: Equal(g0,g13) = 1.5
    c: Coincident(g11,g14)
    c: Coincident(g13,g14)
    c: Equal(g2,g14)
    c: Parallel(g14,g2)
    c: Equal(g0,g15) = 1.5
    c: Coincident(g7,g16)
    c: Coincident(g15,g16)
    c: Equal(g8,g16)
    c: Perpendicular(g16,g2)
    c: Equal(g0,g17) = 1.5
    c: Coincident(g15,g18)
    c: Coincident(g17,g18)
    c: Equal(g2,g18)
    c: Parallel(g18,g2)
    c: Equal(g0,g19) = 1.5
    c: Coincident(g17,g20)
    c: Coincident(g19,g20)
    c: Equal(g2,g20)
    c: Parallel(g20,g2)
    c: Equal(g0,g21) = 1.5
    c: Coincident(g19,g22)
    c: Coincident(g21,g22)
    c: Equal(g2,g22)
    c: Parallel(g22,g2)
    c: Equal(g0,g23) = 1.5
    c: Coincident(g15,g24)
    c: Coincident(g23,g24)
    c: Equal(g8,g24)
    c: Perpendicular(g24,g2)
    c: Equal(g0,g25) = 1.5
    c: Coincident(g23,g26)
    c: Coincident(g25,g26)
    c: Equal(g2,g26)
    c: Parallel(g26,g2)
    c: Equal(g0,g27) = 1.5
    c: Coincident(g25,g28)
    c: Coincident(g27,g28)
    c: Equal(g2,g28)
    c: Parallel(g28,g2)
    c: Equal(g0,g29) = 1.5
    c: Coincident(g27,g30)
    c: Coincident(g29,g30)
    c: Equal(g2,g30)
    c: Parallel(g30,g2)
    c: Equal(g0,g31) = 1.5
    c: Coincident(g23,g32)
    c: Coincident(g31,g32)
    c: Equal(g8,g32)
    c: Perpendicular(g32,g2)
    c: Equal(g0,g33) = 1.5
    c: Coincident(g31,g34)
    c: Coincident(g33,g34)
    c: Equal(g2,g34)
    c: Parallel(g34,g2)
    c: Equal(g0,g35) = 1.5
    c: Coincident(g33,g36)
    c: Coincident(g35,g36)
    c: Equal(g2,g36)
    c: Parallel(g36,g2)
    c: Equal(g0,g37) = 1.5
    c: Coincident(g35,g38)
    c: Coincident(g37,g38)
    c: Equal(g2,g38)
    c: Parallel(g38,g2)
    c: Symmetric(g4,g4,g39)
    c: Vertical(g39,g-1)
    c: DistanceY(g39,g-1) = 35.56
FEATURE [PartDesign::Hole] Hole004
  BaseFeature = -> Hole003
  Depth = 25
  DepthType = 0
  Diameter = 1.6
  DrillPoint = 1
  DrillPointAngle = 118
  HoleCutCountersinkAngle = 90
  HoleCutDepth = 0
  HoleCutDiameter = 2
  HoleCutType = 0
  ModelActualThread = false
  Profile = -> Sketch028
  Tapered = false
  TaperedAngle = 90
  ThreadAngle = 60
  ThreadClass = 0
  ThreadCutOffInner = 0.0433013
  ThreadCutOffOuter = 0.0866025
  ThreadDirection = 1
  ThreadFit = 0
  ThreadPitch = 0.4
  ThreadSize = 1
  ThreadType = 1
  Threaded = true
FEATURE [PartDesign::Hole] Hole005
  BaseFeature = -> Hole004
  Depth = 25
  DepthType = 0
  Diameter = 3.3
  DrillPoint = 1
  DrillPointAngle = 118
  HoleCutCountersinkAngle = 90
  HoleCutDepth = 1.8
  HoleCutDiameter = 6
  HoleCutType = 1
  ModelActualThread = false
  Profile = -> Sketch029
  Tapered = false
  TaperedAngle = 90
  ThreadAngle = 0
  ThreadClass = 0
  ThreadCutOffInner = 0
  ThreadCutOffOuter = 0
  ThreadDirection = 0
  ThreadFit = 0
  ThreadPitch = 0
  ThreadSize = 3
  ThreadType = 1
  Threaded = false
FEATURE [Sketcher::SketchObject] Sketch030  label="MotorHole"
  ExternalGeometry = -> [Sketch029]
  MapMode = 5
  Placement = pos=(0,0,8) rot=(0,0,1;0rad)
  Support = -> [Hole005]
  sketch-geometry (4):
    g0: Circle CenterX=-28 CenterY=-8.91 CenterZ=0 NormalX=0 NormalY=0 NormalZ=1 AngleXU=0 Radius=15
    g1: Circle CenterX=28 CenterY=-8.91 CenterZ=0 NormalX=0 NormalY=0 NormalZ=1 AngleXU=0 Radius=15
    g2: GeomPoint X=-28 Y=-8.91 Z=0
    g3: GeomPoint X=28 Y=-8.91 Z=0
  constraints (9):
    c: Radius(g0) = 15
    c: Equal(g1,g0)
    c: Horizontal(g0,g1)
    c: Vertical(g0,g2)
    c: Horizontal(g0,g2)
    c: Vertical(g1,g3)
    c: DistanceX(g0,g-3) = 15.5
    c: DistanceY(g0,g-3) = 15.5
    c: DistanceX(g1,g-4) = 15.5
FEATURE [PartDesign::Pocket] Pocket015
  BaseFeature = -> Hole005
  Length = 5
  Length2 = 100
  Profile = -> Sketch030
  Type = 1
FEATURE [Sketcher::SketchObject] Sketch031  label="LimitHoles"
  ExternalGeometry = -> [Sketch029]
  MapMode = 5
  Placement = pos=(0,0,8) rot=(0,0,1;0rad)
  Support = -> [Pocket015]
  sketch-geometry (8):
    g0: Circle CenterX=-45.38 CenterY=16.99 CenterZ=0 NormalX=0 NormalY=0 NormalZ=1 AngleXU=0 Radius=1.1
    g1: Circle CenterX=-38.62 CenterY=16.99 CenterZ=0 NormalX=0 NormalY=0 NormalZ=1 AngleXU=0 Radius=1.1
    g2: Circle CenterX=-17.38 CenterY=16.99 CenterZ=0 NormalX=0 NormalY=0 NormalZ=1 AngleXU=0 Radius=1.1
    g3: Circle CenterX=-10.62 CenterY=16.99 CenterZ=0 NormalX=0 NormalY=0 NormalZ=1 AngleXU=0 Radius=1.1
    g4: Circle CenterX=10.62 CenterY=16.99 CenterZ=0 NormalX=0 NormalY=0 NormalZ=1 AngleXU=0 Radius=1.1
    g5: Circle CenterX=17.38 CenterY=16.99 CenterZ=0 NormalX=0 NormalY=0 NormalZ=1 AngleXU=0 Radius=1.1
    g6: Circle CenterX=38.62 CenterY=16.99 CenterZ=0 NormalX=0 NormalY=0 NormalZ=1 AngleXU=0 Radius=1.1
    g7: Circle CenterX=45.38 CenterY=16.99 CenterZ=0 NormalX=0 NormalY=0 NormalZ=1 AngleXU=0 Radius=1.1
  constraints (24):
    c: Equal(g7,g6)
    c: Equal(g6,g5)
    c: Equal(g5,g4)
    c: Equal(g4,g3)
    c: Equal(g3,g2)
    c: Equal(g2,g1)
    c: Equal(g1,g0)
    c: Radius(g0) = 1.1
    c: Horizontal(g0,g1)
    c: Horizontal(g1,g2)
    c: Horizontal(g2,g3)
    c: Horizontal(g3,g4)
    c: Horizontal(g4,g5)
    c: Horizontal(g5,g6)
    c: Horizontal(g6,g7)
    c: DistanceX(g0,g1) = 6.76
    c: DistanceX(g2,g3) = 6.76
    c: DistanceX(g4,g5) = 6.76
    c: DistanceX(g6,g7) = 6.76
    c: DistanceX(g0,g-3) = 1.88
    c: DistanceX(g-4,g3) = 1.88
    c: DistanceX(g4,g-5) = 1.88
    c: DistanceY(g-3,g0) = 10.4
    c: DistanceX(g-6,g7) = 1.88
FEATURE [PartDesign::Hole] Hole006
  BaseFeature = -> Pocket015
  Depth = 25
  DepthType = 0
  Diameter = 1.6
  DrillPoint = 1
  DrillPointAngle = 118
  HoleCutCountersinkAngle = 90
  HoleCutDepth = 0
  HoleCutDiameter = 2
  HoleCutType = 0
  ModelActualThread = false
  Profile = -> Sketch031
  Tapered = false
  TaperedAngle = 90
  ThreadAngle = 60
  ThreadClass = 0
  ThreadCutOffInner = 0.0433013
  ThreadCutOffOuter = 0.0866025
  ThreadDirection = 1
  ThreadFit = 0
  ThreadPitch = 0.4
  ThreadSize = 1
  ThreadType = 1
  Threaded = true
FEATURE [App::Part] Part  label="Back"
  Group = -> [Body,Sketch]
  Origin = -> Origin
  Placement = pos=(0,0,-43) rot=(0,0,1;0rad)
FEATURE [PartDesign::Body] Body
  Group = -> [Pad,Sketch033,Hole007,Sketch035,Hole009,Sketch036,Hole010,Sketch051,Hole018]
  Origin = -> Origin017
  Tip = -> Hole018
FEATURE [Sketcher::SketchObject] Sketch  label="BackContour"
  ExternalGeometry = -> [Sketch023]
  MapMode = 5
  Support = -> [XY_Plane]
  sketch-geometry (17):
    g0: LineSegment StartX=-38 StartY=-31.56 StartZ=0 EndX=38 EndY=-31.56 EndZ=0
    g1: LineSegment StartX=43 StartY=-36.56 StartZ=0 EndX=43 EndY=-96.5441 EndZ=0
    g2: LineSegment StartX=48 StartY=-101.544 StartZ=0 EndX=65 EndY=-101.544 EndZ=0
    g3: LineSegment StartX=70 StartY=-106.544 StartZ=0 EndX=70 EndY=-124.41 EndZ=0
    g4: LineSegment StartX=65 StartY=-129.41 StartZ=0 EndX=-65 EndY=-129.41 EndZ=0
    g5: LineSegment StartX=-70 StartY=-124.41 StartZ=0 EndX=-70 EndY=-106.544 EndZ=0
    g6: LineSegment StartX=-65 StartY=-101.544 StartZ=0 EndX=-48 EndY=-101.544 EndZ=0
    g7: LineSegment StartX=-43 StartY=-96.5441 StartZ=0 EndX=-43 EndY=-36.56 EndZ=0
    g8: ArcOfCircle CenterX=-38 CenterY=-36.56 CenterZ=0 NormalX=0 NormalY=0 NormalZ=1 AngleXU=0 Radius=5 StartAngle=1.5708 EndAngle=3.14159
    g9: ArcOfCircle CenterX=38 CenterY=-36.56 CenterZ=0 NormalX=0 NormalY=0 NormalZ=1 AngleXU=0 Radius=5 StartAngle=-2.7e-15 EndAngle=1.5708
    g10: ArcOfCircle CenterX=48 CenterY=-96.5441 CenterZ=0 NormalX=0 NormalY=0 NormalZ=1 AngleXU=0 Radius=5 StartAngle=3.14159 EndAngle=4.71239
    g11: ArcOfCircle CenterX=65 CenterY=-106.544 CenterZ=0 NormalX=0 NormalY=0 NormalZ=1 AngleXU=0 Radius=5 StartAngle=-2.66e-14 EndAngle=1.5708
    g12: ArcOfCircle CenterX=-48 CenterY=-96.5441 CenterZ=0 NormalX=0 NormalY=0 NormalZ=1 AngleXU=0 Radius=5 StartAngle=4.71239 EndAngle=6.28319
    g13: ArcOfCircle CenterX=-65 CenterY=-106.544 CenterZ=0 NormalX=0 NormalY=0 NormalZ=1 AngleXU=0 Radius=5 StartAngle=1.5708 EndAngle=3.14159
    g14: ArcOfCircle CenterX=-65 CenterY=-124.41 CenterZ=0 NormalX=0 NormalY=0 NormalZ=1 AngleXU=0 Radius=5 StartAngle=3.14159 EndAngle=4.71239
    g15: ArcOfCircle CenterX=65 CenterY=-124.41 CenterZ=0 NormalX=0 NormalY=0 NormalZ=1 AngleXU=0 Radius=5 StartAngle=4.71239 EndAngle=6.28319
    g16: GeomPoint X=0 Y=-31.56 Z=0
  constraints (40):
    c: Horizontal(g0)
    c: Vertical(g1)
    c: Horizontal(g2)
    c: Vertical(g3)
    c: Horizontal(g4)
    c: Vertical(g5)
    c: Horizontal(g6)
    c: Vertical(g7)
    c: Tangent(g0,g8) = 1.5708
    c: Tangent(g7,g8) = 1.5708
    c: Tangent(g0,g9) = 1.5708
    c: Tangent(g1,g9) = 1.5708
    c: Tangent(g1,g10) = -1.5708
    c: Tangent(g2,g10) = -1.5708
    c: Tangent(g2,g11) = 1.5708
    c: Tangent(g3,g11) = 1.5708
    c: Tangent(g6,g12) = -1.5708
    c: Tangent(g7,g12) = -1.5708
    c: Tangent(g5,g13) = 1.5708
    c: Tangent(g6,g13) = 1.5708
    c: Tangent(g4,g14) = 1.5708
    c: Tangent(g5,g14) = 1.5708
    c: Tangent(g3,g15) = 1.5708
    c: Tangent(g4,g15) = 1.5708
    c: Radius(g15) = 5
    c: Equal(g15,g11)
    c: Equal(g11,g10)
    c: Equal(g10,g9)
    c: Equal(g9,g8)
    c: Equal(g8,g12)
    c: Equal(g12,g13)
    c: Equal(g13,g14)
    c: Horizontal(g7,g1)
    c: Symmetric(g0,g0,g16)
    c: Vertical(g16,g-1)
    c: DistanceX(g0,g0) = 76
    c: DistanceY(g16,g-1) = 31.56
    c: Horizontal(g4,g-3)
    c: PointOnObject(g5,g-4)
    c: PointOnObject(g3,g-5)
FEATURE [PartDesign::Pad] Pad
  Length = 8
  Length2 = 100
  Profile = -> Sketch
  Type = 0
FEATURE [Sketcher::SketchObject] Sketch033  label="BackBottomWheels"
  ExternalGeometry = -> [Sketch025]
  MapMode = 5
  Placement = pos=(0,0,0) rot=(1,0,0;3.14159rad)
  Support = -> [Pad]
  sketch-geometry (2):
    g0: Circle CenterX=-48 CenterY=116.56 CenterZ=0 NormalX=0 NormalY=0 NormalZ=1 AngleXU=0 Radius=2.6
    g1: Circle CenterX=48 CenterY=116.56 CenterZ=0 NormalX=0 NormalY=0 NormalZ=1 AngleXU=0 Radius=2.6
  constraints (6):
    c: Equal(g0,g1)
    c: Equal(g1,g-3)
    c: Horizontal(g-3,g0)
    c: Horizontal(g0,g1)
    c: Vertical(g0,g-3)
    c: Vertical(g1,g-4)
FEATURE [PartDesign::Hole] Hole007
  BaseFeature = -> Pad
  Depth = 25
  DepthType = 0
  Diameter = 4.2
  DrillPoint = 1
  DrillPointAngle = 118
  HoleCutCountersinkAngle = 90
  HoleCutDepth = 0
  HoleCutDiameter = 5
  HoleCutType = 0
  ModelActualThread = false
  Profile = -> Sketch033
  Tapered = false
  TaperedAngle = 90
  ThreadAngle = 60
  ThreadClass = 0
  ThreadCutOffInner = 0.0866025
  ThreadCutOffOuter = 0.173205
  ThreadDirection = 0
  ThreadFit = 0
  ThreadPitch = 0.8
  ThreadSize = 6
  ThreadType = 1
  Threaded = true
FEATURE [Sketcher::SketchObject] Sketch035  label="BackTopWheels"
  ExternalGeometry = -> [Sketch027]
  MapMode = 5
  Placement = pos=(0,0,0) rot=(1,0,0;3.14159rad)
  Support = -> [Pad]
  sketch-geometry (2):
    g0: Circle CenterX=-28 CenterY=56.56 CenterZ=0 NormalX=0 NormalY=0 NormalZ=1 AngleXU=0 Radius=2.6
    g1: Circle CenterX=28 CenterY=56.56 CenterZ=0 NormalX=0 NormalY=0 NormalZ=1 AngleXU=0 Radius=2.6
  constraints (6):
    c: Horizontal(g-3,g0)
    c: Horizontal(g0,g1)
    c: Equal(g0,g1)
    c: Equal(g1,g-3)
    c: Vertical(g0,g-3)
    c: Vertical(g1,g-4)
FEATURE [PartDesign::Hole] Hole009
  BaseFeature = -> Hole007
  Depth = 25
  DepthType = 0
  Diameter = 7.2
  DrillPoint = 1
  DrillPointAngle = 118
  HoleCutCountersinkAngle = 90
  HoleCutDepth = 3
  HoleCutDiameter = 12
  HoleCutType = 0
  ModelActualThread = false
  Profile = -> Sketch035
  Tapered = false
  TaperedAngle = 90
  ThreadAngle = 0
  ThreadClass = 0
  ThreadCutOffInner = 0
  ThreadCutOffOuter = 0
  ThreadDirection = 0
  ThreadFit = 0
  ThreadPitch = 0
  ThreadSize = 0
  ThreadType = 0
  Threaded = false
FEATURE [Sketcher::SketchObject] Sketch036  label="BeltTensorHoles"
  ExternalGeometry = -> [Sketch027,Sketch025]
  MapMode = 2
  Support = -> [Hole009]
  sketch-geometry (2):
    g0: Circle CenterX=-28 CenterY=-71.57 CenterZ=0 NormalX=0 NormalY=0 NormalZ=1 AngleXU=0 Radius=2.6
    g1: Circle CenterX=28 CenterY=-71.57 CenterZ=0 NormalX=0 NormalY=0 NormalZ=1 AngleXU=0 Radius=2.6
  constraints (6):
    c: Equal(g-4,g0)
    c: Equal(g0,g1)
    c: Horizontal(g0,g1)
    c: Vertical(g0,g-3)
    c: Vertical(g1,g-5)
    c: DistanceY(g0,g-1) = 71.57
FEATURE [PartDesign::Hole] Hole010
  BaseFeature = -> Hole009
  Depth = 25
  DepthType = 0
  Diameter = 4.2
  DrillPoint = 1
  DrillPointAngle = 118
  HoleCutCountersinkAngle = 90
  HoleCutDepth = 0
  HoleCutDiameter = 5
  HoleCutType = 0
  ModelActualThread = false
  Profile = -> Sketch036
  Reversed = true
  Tapered = false
  TaperedAngle = 90
  ThreadAngle = 60
  ThreadClass = 0
  ThreadCutOffInner = 0.0866025
  ThreadCutOffOuter = 0.173205
  ThreadDirection = 0
  ThreadFit = 0
  ThreadPitch = 0.8
  ThreadSize = 6
  ThreadType = 1
  Threaded = true
FEATURE [App::Part] Part007  label="Nozzle"
  Group = -> [Body006021003,Body006021004]
  Origin = -> Origin018
  Placement = pos=(0,0,16) rot=(0,0,1;0rad)
FEATURE [PartDesign::Body] Body006021003  label="Lift"
  Group = -> [Sketch037,Pad010,Sketch038,Hole011,Sketch039,Hole012,Sketch052,Hole019]
  Origin = -> Origin019
  Tip = -> Hole019
FEATURE [Sketcher::SketchObject] Sketch037
  ExternalGeometry = -> [Sketch030]
  MapMode = 5
  Support = -> [XY_Plane019]
  sketch-geometry (189):
    g0: LineSegment StartX=-32.57 StartY=26.255 StartZ=0 EndX=-32.57 EndY=25.925 EndZ=0
    g1: LineSegment StartX=-34 StartY=27.015 StartZ=0 EndX=-32.57 EndY=26.255 EndZ=0
    g2: LineSegment StartX=-32.57 StartY=25.925 StartZ=0 EndX=-34 EndY=25.165 EndZ=0
    g3: LineSegment StartX=-34 StartY=25.165 StartZ=0 EndX=-34 EndY=25.015 EndZ=0
    g4: LineSegment StartX=-32.57 StartY=24.255 StartZ=0 EndX=-32.57 EndY=23.925 EndZ=0
    g5: LineSegment StartX=-34 StartY=25.015 StartZ=0 EndX=-32.57 EndY=24.255 EndZ=0
    g6: LineSegment StartX=-32.57 StartY=23.925 StartZ=0 EndX=-34 EndY=23.165 EndZ=0
    g7: LineSegment StartX=-34 StartY=23.165 StartZ=0 EndX=-34 EndY=23.015 EndZ=0
    g8: LineSegment [constr] StartX=-32.57 StartY=26.255 StartZ=0 EndX=-32.57 EndY=24.255 EndZ=0
    g9: LineSegment StartX=-32.57 StartY=22.255 StartZ=0 EndX=-32.57 EndY=21.925 EndZ=0
    g10: LineSegment StartX=-34 StartY=23.015 StartZ=0 EndX=-32.57 EndY=22.255 EndZ=0
    g11: LineSegment StartX=-32.57 StartY=21.925 StartZ=0 EndX=-34 EndY=21.165 EndZ=0
    g12: LineSegment StartX=-34 StartY=21.165 StartZ=0 EndX=-34 EndY=21.015 EndZ=0
    g13: LineSegment [constr] StartX=-32.57 StartY=24.255 StartZ=0 EndX=-32.57 EndY=22.255 EndZ=0
    g14: LineSegment StartX=-32.57 StartY=20.255 StartZ=0 EndX=-32.57 EndY=19.925 EndZ=0
    g15: LineSegment StartX=-34 StartY=21.015 StartZ=0 EndX=-32.57 EndY=20.255 EndZ=0
    g16: LineSegment StartX=-32.57 StartY=19.925 StartZ=0 EndX=-34 EndY=19.165 EndZ=0
    g17: LineSegment StartX=-34 StartY=19.165 StartZ=0 EndX=-34 EndY=19.015 EndZ=0
    g18: LineSegment [constr] StartX=-32.57 StartY=22.255 StartZ=0 EndX=-32.57 EndY=20.255 EndZ=0
    g19: LineSegment StartX=-32.57 StartY=18.255 StartZ=0 EndX=-32.57 EndY=17.925 EndZ=0
    g20: LineSegment StartX=-34 StartY=19.015 StartZ=0 EndX=-32.57 EndY=18.255 EndZ=0
    g21: LineSegment StartX=-32.57 StartY=17.925 StartZ=0 EndX=-34 EndY=17.165 EndZ=0
    g22: LineSegment StartX=-34 StartY=17.165 StartZ=0 EndX=-34 EndY=17.015 EndZ=0
    g23: LineSegment [constr] StartX=-32.57 StartY=20.255 StartZ=0 EndX=-32.57 EndY=18.255 EndZ=0
    g24: LineSegment StartX=-32.57 StartY=16.255 StartZ=0 EndX=-32.57 EndY=15.925 EndZ=0
    g25: LineSegment StartX=-34 StartY=17.015 StartZ=0 EndX=-32.57 EndY=16.255 EndZ=0
    g26: LineSegment StartX=-32.57 StartY=15.925 StartZ=0 EndX=-34 EndY=15.165 EndZ=0
    g27: LineSegment StartX=-34 StartY=15.165 StartZ=0 EndX=-34 EndY=15.015 EndZ=0
    g28: LineSegment [constr] StartX=-32.57 StartY=18.255 StartZ=0 EndX=-32.57 EndY=16.255 EndZ=0
    g29: LineSegment StartX=-32.57 StartY=14.255 StartZ=0 EndX=-32.57 EndY=13.925 EndZ=0
    g30: LineSegment StartX=-34 StartY=15.015 StartZ=0 EndX=-32.57 EndY=14.255 EndZ=0
    g31: LineSegment StartX=-32.57 StartY=13.925 StartZ=0 EndX=-34 EndY=13.165 EndZ=0
    g32: LineSegment StartX=-34 StartY=13.165 StartZ=0 EndX=-34 EndY=13.015 EndZ=0
    g33: LineSegment [constr] StartX=-32.57 StartY=16.255 StartZ=0 EndX=-32.57 EndY=14.255 EndZ=0
    g34: LineSegment StartX=-32.57 StartY=12.255 StartZ=0 EndX=-32.57 EndY=11.925 EndZ=0
    g35: LineSegment StartX=-34 StartY=13.015 StartZ=0 EndX=-32.57 EndY=12.255 EndZ=0
    g36: LineSegment StartX=-32.57 StartY=11.925 StartZ=0 EndX=-34 EndY=11.165 EndZ=0
    g37: LineSegment StartX=-34 StartY=11.165 StartZ=0 EndX=-34 EndY=11.015 EndZ=0
    g38: LineSegment [constr] StartX=-32.57 StartY=14.255 StartZ=0 EndX=-32.57 EndY=12.255 EndZ=0
    g39: LineSegment StartX=-32.57 StartY=10.255 StartZ=0 EndX=-32.57 EndY=9.925 EndZ=0
    g40: LineSegment StartX=-34 StartY=11.015 StartZ=0 EndX=-32.57 EndY=10.255 EndZ=0
    g41: LineSegment StartX=-32.57 StartY=9.925 StartZ=0 EndX=-34 EndY=9.165 EndZ=0
    g42: LineSegment StartX=-34 StartY=9.165 StartZ=0 EndX=-34 EndY=9.015 EndZ=0
    g43: LineSegment [constr] StartX=-32.57 StartY=12.255 StartZ=0 EndX=-32.57 EndY=10.255 EndZ=0
    g44: LineSegment StartX=-32.57 StartY=8.255 StartZ=0 EndX=-32.57 EndY=7.925 EndZ=0
    g45: LineSegment StartX=-34 StartY=9.015 StartZ=0 EndX=-32.57 EndY=8.255 EndZ=0
    g46: LineSegment StartX=-32.57 StartY=7.925 StartZ=0 EndX=-34 EndY=7.165 EndZ=0
    g47: LineSegment StartX=-34 StartY=7.165 StartZ=0 EndX=-34 EndY=7.015 EndZ=0
    g48: LineSegment [constr] StartX=-32.57 StartY=10.255 StartZ=0 EndX=-32.57 EndY=8.255 EndZ=0
    g49: LineSegment StartX=-32.57 StartY=6.255 StartZ=0 EndX=-32.57 EndY=5.925 EndZ=0
    g50: LineSegment StartX=-34 StartY=7.015 StartZ=0 EndX=-32.57 EndY=6.255 EndZ=0
    g51: LineSegment StartX=-32.57 StartY=5.925 StartZ=0 EndX=-34 EndY=5.165 EndZ=0
    g52: LineSegment StartX=-34 StartY=5.165 StartZ=0 EndX=-34 EndY=5.015 EndZ=0
    g53: LineSegment [constr] StartX=-32.57 StartY=8.255 StartZ=0 EndX=-32.57 EndY=6.255 EndZ=0
    g54: LineSegment StartX=-32.57 StartY=4.255 StartZ=0 EndX=-32.57 EndY=3.925 EndZ=0
    g55: LineSegment StartX=-34 StartY=5.015 StartZ=0 EndX=-32.57 EndY=4.255 EndZ=0
    g56: LineSegment StartX=-32.57 StartY=3.925 StartZ=0 EndX=-34 EndY=3.165 EndZ=0
    g57: LineSegment StartX=-34 StartY=3.165 StartZ=0 EndX=-34 EndY=3.015 EndZ=0
    g58: LineSegment [constr] StartX=-32.57 StartY=6.255 StartZ=0 EndX=-32.57 EndY=4.255 EndZ=0
    g59: LineSegment StartX=-32.57 StartY=2.255 StartZ=0 EndX=-32.57 EndY=1.925 EndZ=0
    g60: LineSegment StartX=-34 StartY=3.015 StartZ=0 EndX=-32.57 EndY=2.255 EndZ=0
    g61: LineSegment StartX=-32.57 StartY=1.925 StartZ=0 EndX=-34 EndY=1.165 EndZ=0
    g62: LineSegment StartX=-34 StartY=1.165 StartZ=0 EndX=-34 EndY=1.015 EndZ=0
    g63: LineSegment [constr] StartX=-32.57 StartY=4.255 StartZ=0 EndX=-32.57 EndY=2.255 EndZ=0
    g64: LineSegment StartX=-32.57 StartY=0.255 StartZ=0 EndX=-32.57 EndY=-0.075 EndZ=0
    g65: LineSegment StartX=-34 StartY=1.015 StartZ=0 EndX=-32.57 EndY=0.255 EndZ=0
    g66: LineSegment StartX=-32.57 StartY=-0.075 StartZ=0 EndX=-34 EndY=-0.835 EndZ=0
    g67: LineSegment StartX=-34 StartY=-0.835 StartZ=0 EndX=-34 EndY=-0.985 EndZ=0
    g68: LineSegment [constr] StartX=-32.57 StartY=2.255 StartZ=0 EndX=-32.57 EndY=0.255 EndZ=0
    g69: LineSegment StartX=-32.57 StartY=-1.745 StartZ=0 EndX=-32.57 EndY=-2.075 EndZ=0
    g70: LineSegment StartX=-34 StartY=-0.985 StartZ=0 EndX=-32.57 EndY=-1.745 EndZ=0
    g71: LineSegment StartX=-32.57 StartY=-2.075 StartZ=0 EndX=-34 EndY=-2.835 EndZ=0
    g72: LineSegment StartX=-34 StartY=-2.835 StartZ=0 EndX=-34 EndY=-2.985 EndZ=0
    g73: LineSegment [constr] StartX=-32.57 StartY=0.255 StartZ=0 EndX=-32.57 EndY=-1.745 EndZ=0
    g74: LineSegment StartX=-32.57 StartY=-3.745 StartZ=0 EndX=-32.57 EndY=-4.075 EndZ=0
    g75: LineSegment StartX=-34 StartY=-2.985 StartZ=0 EndX=-32.57 EndY=-3.745 EndZ=0
    g76: LineSegment StartX=-32.57 StartY=-4.075 StartZ=0 EndX=-34 EndY=-4.835 EndZ=0
    g77: LineSegment StartX=-34 StartY=-4.835 StartZ=0 EndX=-34 EndY=-4.985 EndZ=0
    g78: LineSegment [constr] StartX=-32.57 StartY=-1.745 StartZ=0 EndX=-32.57 EndY=-3.745 EndZ=0
    g79: LineSegment StartX=-32.57 StartY=-5.745 StartZ=0 EndX=-32.57 EndY=-6.075 EndZ=0
    g80: LineSegment StartX=-34 StartY=-4.985 StartZ=0 EndX=-32.57 EndY=-5.745 EndZ=0
    g81: LineSegment StartX=-32.57 StartY=-6.075 StartZ=0 EndX=-34 EndY=-6.835 EndZ=0
    g82: LineSegment StartX=-34 StartY=-6.835 StartZ=0 EndX=-34 EndY=-6.985 EndZ=0
    g83: LineSegment [constr] StartX=-32.57 StartY=-3.745 StartZ=0 EndX=-32.57 EndY=-5.745 EndZ=0
    g84: LineSegment StartX=-32.57 StartY=-7.745 StartZ=0 EndX=-32.57 EndY=-8.075 EndZ=0
    g85: LineSegment StartX=-34 StartY=-6.985 StartZ=0 EndX=-32.57 EndY=-7.745 EndZ=0
    g86: LineSegment StartX=-32.57 StartY=-8.075 StartZ=0 EndX=-34 EndY=-8.835 EndZ=0
    g87: LineSegment StartX=-34 StartY=-8.835 StartZ=0 EndX=-34 EndY=-8.985 EndZ=0
    g88: LineSegment [constr] StartX=-32.57 StartY=-5.745 StartZ=0 EndX=-32.57 EndY=-7.745 EndZ=0
    g89: LineSegment StartX=-32.57 StartY=-9.745 StartZ=0 EndX=-32.57 EndY=-10.075 EndZ=0
    g90: LineSegment StartX=-34 StartY=-8.985 StartZ=0 EndX=-32.57 EndY=-9.745 EndZ=0
    g91: LineSegment StartX=-32.57 StartY=-10.075 StartZ=0 EndX=-34 EndY=-10.835 EndZ=0
    g92: LineSegment StartX=-34 StartY=-10.835 StartZ=0 EndX=-34 EndY=-10.985 EndZ=0
    g93: LineSegment [constr] StartX=-32.57 StartY=-7.745 StartZ=0 EndX=-32.57 EndY=-9.745 EndZ=0
    g94: LineSegment StartX=-32.57 StartY=-11.745 StartZ=0 EndX=-32.57 EndY=-12.075 EndZ=0
    g95: LineSegment StartX=-34 StartY=-10.985 StartZ=0 EndX=-32.57 EndY=-11.745 EndZ=0
    g96: LineSegment StartX=-32.57 StartY=-12.075 StartZ=0 EndX=-34 EndY=-12.835 EndZ=0
    g97: LineSegment StartX=-34 StartY=-12.835 StartZ=0 EndX=-34 EndY=-12.985 EndZ=0
    g98: LineSegment [constr] StartX=-32.57 StartY=-9.745 StartZ=0 EndX=-32.57 EndY=-11.745 EndZ=0
    g99: LineSegment StartX=-32.57 StartY=-13.745 StartZ=0 EndX=-32.57 EndY=-14.075 EndZ=0
    g100: LineSegment StartX=-34 StartY=-12.985 StartZ=0 EndX=-32.57 EndY=-13.745 EndZ=0
    g101: LineSegment StartX=-32.57 StartY=-14.075 StartZ=0 EndX=-34 EndY=-14.835 EndZ=0
    g102: LineSegment StartX=-34 StartY=-14.835 StartZ=0 EndX=-34 EndY=-14.985 EndZ=0
    g103: LineSegment [constr] StartX=-32.57 StartY=-11.745 StartZ=0 EndX=-32.57 EndY=-13.745 EndZ=0
    g104: LineSegment StartX=-32.57 StartY=-15.745 StartZ=0 EndX=-32.57 EndY=-16.075 EndZ=0
    g105: LineSegment StartX=-34 StartY=-14.985 StartZ=0 EndX=-32.57 EndY=-15.745 EndZ=0
    g106: LineSegment StartX=-32.57 StartY=-16.075 StartZ=0 EndX=-34 EndY=-16.835 EndZ=0
    g107: LineSegment StartX=-34 StartY=-16.835 StartZ=0 EndX=-34 EndY=-16.985 EndZ=0
    g108: LineSegment [constr] StartX=-32.57 StartY=-13.745 StartZ=0 EndX=-32.57 EndY=-15.745 EndZ=0
    g109: LineSegment StartX=-32.57 StartY=-17.745 StartZ=0 EndX=-32.57 EndY=-18.075 EndZ=0
    g110: LineSegment StartX=-34 StartY=-16.985 StartZ=0 EndX=-32.57 EndY=-17.745 EndZ=0
    g111: LineSegment StartX=-32.57 StartY=-18.075 StartZ=0 EndX=-34 EndY=-18.835 EndZ=0
    g112: LineSegment StartX=-34 StartY=-18.835 StartZ=0 EndX=-34 EndY=-18.985 EndZ=0
    g113: LineSegment [constr] StartX=-32.57 StartY=-15.745 StartZ=0 EndX=-32.57 EndY=-17.745 EndZ=0
    g114: LineSegment StartX=-32.57 StartY=-19.745 StartZ=0 EndX=-32.57 EndY=-20.075 EndZ=0
    g115: LineSegment StartX=-34 StartY=-18.985 StartZ=0 EndX=-32.57 EndY=-19.745 EndZ=0
    g116: LineSegment StartX=-32.57 StartY=-20.075 StartZ=0 EndX=-34 EndY=-20.835 EndZ=0
    g117: LineSegment StartX=-34 StartY=-20.835 StartZ=0 EndX=-34 EndY=-20.985 EndZ=0
    g118: LineSegment [constr] StartX=-32.57 StartY=-17.745 StartZ=0 EndX=-32.57 EndY=-19.745 EndZ=0
    g119: LineSegment StartX=-32.57 StartY=-21.745 StartZ=0 EndX=-32.57 EndY=-22.075 EndZ=0
    g120: LineSegment StartX=-34 StartY=-20.985 StartZ=0 EndX=-32.57 EndY=-21.745 EndZ=0
    g121: LineSegment StartX=-32.57 StartY=-22.075 StartZ=0 EndX=-34 EndY=-22.835 EndZ=0
    g122: LineSegment StartX=-34 StartY=-22.835 StartZ=0 EndX=-34 EndY=-22.985 EndZ=0
    g123: LineSegment [constr] StartX=-32.57 StartY=-19.745 StartZ=0 EndX=-32.57 EndY=-21.745 EndZ=0
    g124: LineSegment StartX=-32.57 StartY=-23.745 StartZ=0 EndX=-32.57 EndY=-24.075 EndZ=0
    g125: LineSegment StartX=-34 StartY=-22.985 StartZ=0 EndX=-32.57 EndY=-23.745 EndZ=0
    g126: LineSegment StartX=-32.57 StartY=-24.075 StartZ=0 EndX=-34 EndY=-24.835 EndZ=0
    g127: LineSegment StartX=-34 StartY=-24.835 StartZ=0 EndX=-34 EndY=-24.985 EndZ=0
    g128: LineSegment [constr] StartX=-32.57 StartY=-21.745 StartZ=0 EndX=-32.57 EndY=-23.745 EndZ=0
    g129: LineSegment StartX=-32.57 StartY=-25.745 StartZ=0 EndX=-32.57 EndY=-26.075 EndZ=0
    g130: LineSegment StartX=-34 StartY=-24.985 StartZ=0 EndX=-32.57 EndY=-25.745 EndZ=0
    g131: LineSegment StartX=-32.57 StartY=-26.075 StartZ=0 EndX=-34 EndY=-26.835 EndZ=0
    g132: LineSegment StartX=-34 StartY=-26.835 StartZ=0 EndX=-34 EndY=-26.985 EndZ=0
    g133: LineSegment [constr] StartX=-32.57 StartY=-23.745 StartZ=0 EndX=-32.57 EndY=-25.745 EndZ=0
    g134: LineSegment StartX=-32.57 StartY=-27.745 StartZ=0 EndX=-32.57 EndY=-28.075 EndZ=0
    g135: LineSegment StartX=-34 StartY=-26.985 StartZ=0 EndX=-32.57 EndY=-27.745 EndZ=0
    g136: LineSegment StartX=-32.57 StartY=-28.075 StartZ=0 EndX=-34 EndY=-28.835 EndZ=0
    g137: LineSegment StartX=-34 StartY=-28.835 StartZ=0 EndX=-34 EndY=-28.985 EndZ=0
    g138: LineSegment [constr] StartX=-32.57 StartY=-25.745 StartZ=0 EndX=-32.57 EndY=-27.745 EndZ=0
    g139: LineSegment StartX=-32.57 StartY=-29.745 StartZ=0 EndX=-32.57 EndY=-30.075 EndZ=0
    g140: LineSegment StartX=-34 StartY=-28.985 StartZ=0 EndX=-32.57 EndY=-29.745 EndZ=0
    g141: LineSegment StartX=-32.57 StartY=-30.075 StartZ=0 EndX=-34 EndY=-30.835 EndZ=0
    g142: LineSegment StartX=-34 StartY=-30.835 StartZ=0 EndX=-34 EndY=-30.985 EndZ=0
    g143: LineSegment [constr] StartX=-32.57 StartY=-27.745 StartZ=0 EndX=-32.57 EndY=-29.745 EndZ=0
    g144: LineSegment StartX=-32.57 StartY=-31.745 StartZ=0 EndX=-32.57 EndY=-32.075 EndZ=0
    g145: LineSegment StartX=-34 StartY=-30.985 StartZ=0 EndX=-32.57 EndY=-31.745 EndZ=0
    g146: LineSegment StartX=-32.57 StartY=-32.075 StartZ=0 EndX=-34 EndY=-32.835 EndZ=0
    g147: LineSegment StartX=-34 StartY=-32.835 StartZ=0 EndX=-34 EndY=-32.985 EndZ=0
    g148: LineSegment [constr] StartX=-32.57 StartY=-29.745 StartZ=0 EndX=-32.57 EndY=-31.745 EndZ=0
    g149: LineSegment StartX=-32.57 StartY=-33.745 StartZ=0 EndX=-32.57 EndY=-34.075 EndZ=0
    g150: LineSegment StartX=-34 StartY=-32.985 StartZ=0 EndX=-32.57 EndY=-33.745 EndZ=0
    g151: LineSegment StartX=-32.57 StartY=-34.075 StartZ=0 EndX=-34 EndY=-34.835 EndZ=0
    g152: LineSegment StartX=-34 StartY=-34.835 StartZ=0 EndX=-34 EndY=-34.985 EndZ=0
    g153: LineSegment [constr] StartX=-32.57 StartY=-31.745 StartZ=0 EndX=-32.57 EndY=-33.745 EndZ=0
    g154: LineSegment StartX=-32.57 StartY=-35.745 StartZ=0 EndX=-32.57 EndY=-36.075 EndZ=0
    g155: LineSegment StartX=-34 StartY=-34.985 StartZ=0 EndX=-32.57 EndY=-35.745 EndZ=0
    g156: LineSegment StartX=-32.57 StartY=-36.075 StartZ=0 EndX=-34 EndY=-36.835 EndZ=0
    g157: LineSegment StartX=-34 StartY=-36.835 StartZ=0 EndX=-34 EndY=-36.985 EndZ=0
    g158: LineSegment [constr] StartX=-32.57 StartY=-33.745 StartZ=0 EndX=-32.57 EndY=-35.745 EndZ=0
    g159: LineSegment StartX=-32.57 StartY=-37.745 StartZ=0 EndX=-32.57 EndY=-38.075 EndZ=0
    g160: LineSegment StartX=-34 StartY=-36.985 StartZ=0 EndX=-32.57 EndY=-37.745 EndZ=0
    g161: LineSegment StartX=-32.57 StartY=-38.075 StartZ=0 EndX=-34 EndY=-38.835 EndZ=0
    g162: LineSegment StartX=-34 StartY=-38.835 StartZ=0 EndX=-34 EndY=-38.985 EndZ=0
    g163: LineSegment [constr] StartX=-32.57 StartY=-35.745 StartZ=0 EndX=-32.57 EndY=-37.745 EndZ=0
    g164: LineSegment StartX=-32.57 StartY=-39.745 StartZ=0 EndX=-32.57 EndY=-40.075 EndZ=0
    g165: LineSegment StartX=-34 StartY=-38.985 StartZ=0 EndX=-32.57 EndY=-39.745 EndZ=0
    g166: LineSegment StartX=-32.57 StartY=-40.075 StartZ=0 EndX=-34 EndY=-40.835 EndZ=0
    g167: LineSegment StartX=-34 StartY=-40.835 StartZ=0 EndX=-34 EndY=-40.985 EndZ=0
    g168: LineSegment [constr] StartX=-32.57 StartY=-37.745 StartZ=0 EndX=-32.57 EndY=-39.745 EndZ=0
    g169: LineSegment StartX=-32.57 StartY=-41.745 StartZ=0 EndX=-32.57 EndY=-42.075 EndZ=0
    g170: LineSegment StartX=-34 StartY=-40.985 StartZ=0 EndX=-32.57 EndY=-41.745 EndZ=0
    g171: LineSegment StartX=-32.57 StartY=-42.075 StartZ=0 EndX=-34 EndY=-42.835 EndZ=0
    g172: LineSegment StartX=-34 StartY=-42.835 StartZ=0 EndX=-34 EndY=-42.985 EndZ=0
    g173: LineSegment [constr] StartX=-32.57 StartY=-39.745 StartZ=0 EndX=-32.57 EndY=-41.745 EndZ=0
    g174: LineSegment StartX=-32.57 StartY=-43.745 StartZ=0 EndX=-32.57 EndY=-44.075 EndZ=0
    g175: LineSegment StartX=-34 StartY=-42.985 StartZ=0 EndX=-32.57 EndY=-43.745 EndZ=0
    g176: LineSegment StartX=-32.57 StartY=-44.075 StartZ=0 EndX=-34 EndY=-44.835 EndZ=0
    g177: LineSegment [constr] StartX=-32.57 StartY=-41.745 StartZ=0 EndX=-32.57 EndY=-43.745 EndZ=0
    g178: GeomPoint X=-24.2509 Y=-8.91 Z=0
    g179: GeomPoint X=-34 Y=-8.91 Z=0
    g180: LineSegment StartX=-34 StartY=27.015 StartZ=0 EndX=-56.0389 EndY=27.015 EndZ=0
    g181: GeomPoint X=-29 Y=-10.845 Z=0
    g182: LineSegment StartX=-56.0389 StartY=-111.835 StartZ=0 EndX=-29.0389 EndY=-111.835 EndZ=0
    g183: GeomPoint X=-34 Y=-42.91 Z=0
    g184: LineSegment StartX=-29.0389 StartY=-49.125 StartZ=0 EndX=-29.0389 EndY=-111.835 EndZ=0
    g185: LineSegment StartX=-56.0389 StartY=27.015 StartZ=0 EndX=-56.0389 EndY=-111.835 EndZ=0
    g186: GeomPoint X=-28 Y=-42.91 Z=0
    g187: ArcOfCircle CenterX=-28 CenterY=-42.91 CenterZ=0 NormalX=0 NormalY=0 NormalZ=1 AngleXU=0 Radius=6.30124 StartAngle=3.45205 EndAngle=4.54675
    g188: GeomPoint X=-42.5389 Y=-111.835 Z=0
  constraints (669):
    c: Vertical(g0)
    c: DistanceY(g0,g0) = 0.33
    c: PointOnObject(g1,g0)
    c: Horizontal(g0,g1)
    c: DistanceY(g0,g1) = 0.76
    c: DistanceX(g1,g0) = 1.43
    c: PointOnObject(g2,g0)
    c: Horizontal(g2,g0)
    c: Vertical(g2,g1)
    c: Vertical(g3)
    c: PointOnObject(g3,g2)
    c: Vertical(g3,g2)
    c: DistanceY(g3,g3) = 0.15
    c: DistanceY(g2,g0) = 0.76
    c: Vertical(g4)
    c: DistanceY(g4,g4) = 0.33
    c: PointOnObject(g5,g4)
    c: Horizontal(g4,g5)
    c: DistanceY(g4,g5) = 0.76
    c: DistanceX(g5,g4) = 1.43
    c: PointOnObject(g6,g4)
    c: Horizontal(g6,g4)
    c: Vertical(g6,g5)
    c: Vertical(g7)
    c: PointOnObject(g7,g6)
    c: Vertical(g7,g6)
    c: DistanceY(g7,g7) = 0.15
    c: DistanceY(g6,g4) = 0.76
    c: Coincident(g0,g8)
    c: Coincident(g4,g8)
    c: Distance(g8) = 2
    c: Angle(g8) = -1.5708
    c: Vertical(g9)
    c: DistanceY(g9,g9) = 0.33
    c: PointOnObject(g10,g9)
    c: Horizontal(g9,g10)
    c: DistanceY(g9,g10) = 0.76
    c: DistanceX(g10,g9) = 1.43
    c: PointOnObject(g11,g9)
    c: Horizontal(g11,g9)
    c: Vertical(g11,g10)
    c: Vertical(g12)
    c: PointOnObject(g12,g11)
    c: Vertical(g12,g11)
    c: DistanceY(g12,g12) = 0.15
    c: DistanceY(g11,g9) = 0.76
    c: Coincident(g4,g13)
    c: Coincident(g9,g13)
    c: Equal(g8,g13)
    c: Parallel(g13,g8)
    c: Vertical(g14)
    c: DistanceY(g14,g14) = 0.33
    c: PointOnObject(g15,g14)
    c: Horizontal(g14,g15)
    c: DistanceY(g14,g15) = 0.76
    c: DistanceX(g15,g14) = 1.43
    c: PointOnObject(g16,g14)
    c: Horizontal(g16,g14)
    c: Vertical(g16,g15)
    c: Vertical(g17)
    c: PointOnObject(g17,g16)
    c: Vertical(g17,g16)
    c: DistanceY(g17,g17) = 0.15
    c: DistanceY(g16,g14) = 0.76
    c: Coincident(g9,g18)
    c: Coincident(g14,g18)
    c: Equal(g8,g18)
    c: Parallel(g18,g8)
    c: Vertical(g19)
    c: DistanceY(g19,g19) = 0.33
    c: PointOnObject(g20,g19)
    c: Horizontal(g19,g20)
    c: DistanceY(g19,g20) = 0.76
    c: DistanceX(g20,g19) = 1.43
    c: PointOnObject(g21,g19)
    c: Horizontal(g21,g19)
    c: Vertical(g21,g20)
    c: Vertical(g22)
    c: PointOnObject(g22,g21)
    c: Vertical(g22,g21)
    c: DistanceY(g22,g22) = 0.15
    c: DistanceY(g21,g19) = 0.76
    c: Coincident(g14,g23)
    c: Coincident(g19,g23)
    c: Equal(g8,g23)
    c: Parallel(g23,g8)
    c: Vertical(g24)
    c: DistanceY(g24,g24) = 0.33
    c: PointOnObject(g25,g24)
    c: Horizontal(g24,g25)
    c: DistanceY(g24,g25) = 0.76
    c: DistanceX(g25,g24) = 1.43
    c: PointOnObject(g26,g24)
    c: Horizontal(g26,g24)
    c: Vertical(g26,g25)
    c: Vertical(g27)
    c: PointOnObject(g27,g26)
    c: Vertical(g27,g26)
    c: DistanceY(g27,g27) = 0.15
    c: DistanceY(g26,g24) = 0.76
    c: Coincident(g19,g28)
    c: Coincident(g24,g28)
    c: Equal(g8,g28)
    c: Parallel(g28,g8)
    c: Vertical(g29)
    c: DistanceY(g29,g29) = 0.33
    c: PointOnObject(g30,g29)
    c: Horizontal(g29,g30)
    c: DistanceY(g29,g30) = 0.76
    c: DistanceX(g30,g29) = 1.43
    c: PointOnObject(g31,g29)
    c: Horizontal(g31,g29)
    c: Vertical(g31,g30)
    c: Vertical(g32)
    c: PointOnObject(g32,g31)
    c: Vertical(g32,g31)
    c: DistanceY(g32,g32) = 0.15
    c: DistanceY(g31,g29) = 0.76
    c: Coincident(g24,g33)
    c: Coincident(g29,g33)
    c: Equal(g8,g33)
    c: Parallel(g33,g8)
    c: Vertical(g34)
    c: DistanceY(g34,g34) = 0.33
    c: PointOnObject(g35,g34)
    c: Horizontal(g34,g35)
    c: DistanceY(g34,g35) = 0.76
    c: DistanceX(g35,g34) = 1.43
    c: PointOnObject(g36,g34)
    c: Horizontal(g36,g34)
    c: Vertical(g36,g35)
    c: Vertical(g37)
    c: PointOnObject(g37,g36)
    c: Vertical(g37,g36)
    c: DistanceY(g37,g37) = 0.15
    c: DistanceY(g36,g34) = 0.76
    c: Coincident(g29,g38)
    c: Coincident(g34,g38)
    c: Equal(g8,g38)
    c: Parallel(g38,g8)
    c: Vertical(g39)
    c: DistanceY(g39,g39) = 0.33
    c: PointOnObject(g40,g39)
    c: Horizontal(g39,g40)
    c: DistanceY(g39,g40) = 0.76
    c: DistanceX(g40,g39) = 1.43
    c: PointOnObject(g41,g39)
    c: Horizontal(g41,g39)
    c: Vertical(g41,g40)
    c: Vertical(g42)
    c: PointOnObject(g42,g41)
    c: Vertical(g42,g41)
    c: DistanceY(g42,g42) = 0.15
    c: DistanceY(g41,g39) = 0.76
    c: Coincident(g34,g43)
    c: Coincident(g39,g43)
    c: Equal(g8,g43)
    c: Parallel(g43,g8)
    c: Vertical(g44)
    c: DistanceY(g44,g44) = 0.33
    c: PointOnObject(g45,g44)
    c: Horizontal(g44,g45)
    c: DistanceY(g44,g45) = 0.76
    c: DistanceX(g45,g44) = 1.43
    c: PointOnObject(g46,g44)
    c: Horizontal(g46,g44)
    c: Vertical(g46,g45)
    c: Vertical(g47)
    c: PointOnObject(g47,g46)
    c: Vertical(g47,g46)
    c: DistanceY(g47,g47) = 0.15
    c: DistanceY(g46,g44) = 0.76
    c: Coincident(g39,g48)
    c: Coincident(g44,g48)
    c: Equal(g8,g48)
    c: Parallel(g48,g8)
    c: Vertical(g49)
    c: DistanceY(g49,g49) = 0.33
    c: PointOnObject(g50,g49)
    c: Horizontal(g49,g50)
    c: DistanceY(g49,g50) = 0.76
    c: DistanceX(g50,g49) = 1.43
    c: PointOnObject(g51,g49)
    c: Horizontal(g51,g49)
    c: Vertical(g51,g50)
    c: Vertical(g52)
    c: PointOnObject(g52,g51)
    c: Vertical(g52,g51)
    c: DistanceY(g52,g52) = 0.15
    c: DistanceY(g51,g49) = 0.76
    c: Coincident(g44,g53)
    c: Coincident(g49,g53)
    c: Equal(g8,g53)
    c: Parallel(g53,g8)
    c: Vertical(g54)
    c: DistanceY(g54,g54) = 0.33
    c: PointOnObject(g55,g54)
    c: Horizontal(g54,g55)
    c: DistanceY(g54,g55) = 0.76
    c: DistanceX(g55,g54) = 1.43
    c: PointOnObject(g56,g54)
    c: Horizontal(g56,g54)
    c: Vertical(g56,g55)
    c: Vertical(g57)
    c: PointOnObject(g57,g56)
    c: Vertical(g57,g56)
    c: DistanceY(g57,g57) = 0.15
    c: DistanceY(g56,g54) = 0.76
    c: Coincident(g49,g58)
    c: Coincident(g54,g58)
    c: Equal(g8,g58)
    c: Parallel(g58,g8)
    c: Vertical(g59)
    c: DistanceY(g59,g59) = 0.33
    c: PointOnObject(g60,g59)
    c: Horizontal(g59,g60)
    c: DistanceY(g59,g60) = 0.76
    c: DistanceX(g60,g59) = 1.43
    c: PointOnObject(g61,g59)
    c: Horizontal(g61,g59)
    c: Vertical(g61,g60)
    c: Vertical(g62)
    c: PointOnObject(g62,g61)
    c: Vertical(g62,g61)
    c: DistanceY(g62,g62) = 0.15
    c: DistanceY(g61,g59) = 0.76
    c: Coincident(g54,g63)
    c: Coincident(g59,g63)
    c: Equal(g8,g63)
    c: Parallel(g63,g8)
    c: Vertical(g64)
    c: DistanceY(g64,g64) = 0.33
    c: PointOnObject(g65,g64)
    c: Horizontal(g64,g65)
    c: DistanceY(g64,g65) = 0.76
    c: DistanceX(g65,g64) = 1.43
    c: PointOnObject(g66,g64)
    c: Horizontal(g66,g64)
    c: Vertical(g66,g65)
    c: Vertical(g67)
    c: PointOnObject(g67,g66)
    c: Vertical(g67,g66)
    c: DistanceY(g67,g67) = 0.15
    c: DistanceY(g66,g64) = 0.76
    c: Coincident(g59,g68)
    c: Coincident(g64,g68)
    c: Equal(g8,g68)
    c: Parallel(g68,g8)
    c: Vertical(g69)
    c: DistanceY(g69,g69) = 0.33
    c: PointOnObject(g70,g69)
    c: Horizontal(g69,g70)
    c: DistanceY(g69,g70) = 0.76
    c: DistanceX(g70,g69) = 1.43
    c: PointOnObject(g71,g69)
    c: Horizontal(g71,g69)
    c: Vertical(g71,g70)
    c: Vertical(g72)
    c: PointOnObject(g72,g71)
    c: Vertical(g72,g71)
    c: DistanceY(g72,g72) = 0.15
    c: DistanceY(g71,g69) = 0.76
    c: Coincident(g64,g73)
    c: Coincident(g69,g73)
    c: Equal(g8,g73)
    c: Parallel(g73,g8)
    c: Vertical(g74)
    c: DistanceY(g74,g74) = 0.33
    c: PointOnObject(g75,g74)
    c: Horizontal(g74,g75)
    c: DistanceY(g74,g75) = 0.76
    c: DistanceX(g75,g74) = 1.43
    c: PointOnObject(g76,g74)
    c: Horizontal(g76,g74)
    c: Vertical(g76,g75)
    c: Vertical(g77)
    c: PointOnObject(g77,g76)
    c: Vertical(g77,g76)
    c: DistanceY(g77,g77) = 0.15
    c: DistanceY(g76,g74) = 0.76
    c: Coincident(g69,g78)
    c: Coincident(g74,g78)
    c: Equal(g8,g78)
    c: Parallel(g78,g8)
    c: Vertical(g79)
    c: DistanceY(g79,g79) = 0.33
    c: PointOnObject(g80,g79)
    c: Horizontal(g79,g80)
    c: DistanceY(g79,g80) = 0.76
    c: DistanceX(g80,g79) = 1.43
    c: PointOnObject(g81,g79)
    c: Horizontal(g81,g79)
    c: Vertical(g81,g80)
    c: Vertical(g82)
    c: PointOnObject(g82,g81)
    c: Vertical(g82,g81)
    c: DistanceY(g82,g82) = 0.15
    c: DistanceY(g81,g79) = 0.76
    c: Coincident(g74,g83)
    c: Coincident(g79,g83)
    c: Equal(g8,g83)
    c: Parallel(g83,g8)
    c: Vertical(g84)
    c: DistanceY(g84,g84) = 0.33
    c: PointOnObject(g85,g84)
    c: Horizontal(g84,g85)
    c: DistanceY(g84,g85) = 0.76
    c: DistanceX(g85,g84) = 1.43
    c: PointOnObject(g86,g84)
    c: Horizontal(g86,g84)
    c: Vertical(g86,g85)
    c: Vertical(g87)
    c: PointOnObject(g87,g86)
    c: Vertical(g87,g86)
    c: DistanceY(g87,g87) = 0.15
    c: DistanceY(g86,g84) = 0.76
    c: Coincident(g79,g88)
    c: Coincident(g84,g88)
    c: Equal(g8,g88)
    c: Parallel(g88,g8)
    c: Vertical(g89)
    c: DistanceY(g89,g89) = 0.33
    c: PointOnObject(g90,g89)
    c: Horizontal(g89,g90)
    c: DistanceY(g89,g90) = 0.76
    c: DistanceX(g90,g89) = 1.43
    c: PointOnObject(g91,g89)
    c: Horizontal(g91,g89)
    c: Vertical(g91,g90)
    c: Vertical(g92)
    c: PointOnObject(g92,g91)
    c: Vertical(g92,g91)
    c: DistanceY(g92,g92) = 0.15
    c: DistanceY(g91,g89) = 0.76
    c: Coincident(g84,g93)
    c: Coincident(g89,g93)
    c: Equal(g8,g93)
    c: Parallel(g93,g8)
    c: Vertical(g94)
    c: DistanceY(g94,g94) = 0.33
    c: PointOnObject(g95,g94)
    c: Horizontal(g94,g95)
    c: DistanceY(g94,g95) = 0.76
    c: DistanceX(g95,g94) = 1.43
    c: PointOnObject(g96,g94)
    c: Horizontal(g96,g94)
    c: Vertical(g96,g95)
    c: Vertical(g97)
    c: PointOnObject(g97,g96)
    c: Vertical(g97,g96)
    c: DistanceY(g97,g97) = 0.15
    c: DistanceY(g96,g94) = 0.76
    c: Coincident(g89,g98)
    c: Coincident(g94,g98)
    c: Equal(g8,g98)
    c: Parallel(g98,g8)
    c: Vertical(g99)
    c: DistanceY(g99,g99) = 0.33
    c: PointOnObject(g100,g99)
    c: Horizontal(g99,g100)
    c: DistanceY(g99,g100) = 0.76
    c: DistanceX(g100,g99) = 1.43
    c: PointOnObject(g101,g99)
    c: Horizontal(g101,g99)
    c: Vertical(g101,g100)
    c: Vertical(g102)
    c: PointOnObject(g102,g101)
    c: Vertical(g102,g101)
    c: DistanceY(g102,g102) = 0.15
    c: DistanceY(g101,g99) = 0.76
    c: Coincident(g94,g103)
    c: Coincident(g99,g103)
    c: Equal(g8,g103)
    c: Parallel(g103,g8)
    c: Vertical(g104)
    c: DistanceY(g104,g104) = 0.33
    c: PointOnObject(g105,g104)
    c: Horizontal(g104,g105)
    c: DistanceY(g104,g105) = 0.76
    c: DistanceX(g105,g104) = 1.43
    c: PointOnObject(g106,g104)
    c: Horizontal(g106,g104)
    c: Vertical(g106,g105)
    c: Vertical(g107)
    c: PointOnObject(g107,g106)
    c: Vertical(g107,g106)
    c: DistanceY(g107,g107) = 0.15
    c: DistanceY(g106,g104) = 0.76
    c: Coincident(g99,g108)
    c: Coincident(g104,g108)
    c: Equal(g8,g108)
    c: Parallel(g108,g8)
    c: Vertical(g109)
    c: DistanceY(g109,g109) = 0.33
    c: PointOnObject(g110,g109)
    c: Horizontal(g109,g110)
    c: DistanceY(g109,g110) = 0.76
    c: DistanceX(g110,g109) = 1.43
    c: PointOnObject(g111,g109)
    c: Horizontal(g111,g109)
    c: Vertical(g111,g110)
    c: Vertical(g112)
    c: PointOnObject(g112,g111)
    c: Vertical(g112,g111)
    c: DistanceY(g112,g112) = 0.15
    c: DistanceY(g111,g109) = 0.76
    c: Coincident(g104,g113)
    c: Coincident(g109,g113)
    c: Equal(g8,g113)
    c: Parallel(g113,g8)
    c: Vertical(g114)
    c: DistanceY(g114,g114) = 0.33
    c: PointOnObject(g115,g114)
    c: Horizontal(g114,g115)
    c: DistanceY(g114,g115) = 0.76
    c: DistanceX(g115,g114) = 1.43
    c: PointOnObject(g116,g114)
    c: Horizontal(g116,g114)
    c: Vertical(g116,g115)
    c: Vertical(g117)
    c: PointOnObject(g117,g116)
    c: Vertical(g117,g116)
    c: DistanceY(g117,g117) = 0.15
    c: DistanceY(g116,g114) = 0.76
    c: Coincident(g109,g118)
    c: Coincident(g114,g118)
    c: Equal(g8,g118)
    c: Parallel(g118,g8)
    c: Vertical(g119)
    c: DistanceY(g119,g119) = 0.33
    c: PointOnObject(g120,g119)
    c: Horizontal(g119,g120)
    c: DistanceY(g119,g120) = 0.76
    c: DistanceX(g120,g119) = 1.43
    c: PointOnObject(g121,g119)
    c: Horizontal(g121,g119)
    c: Vertical(g121,g120)
    c: Vertical(g122)
    c: PointOnObject(g122,g121)
    c: Vertical(g122,g121)
    c: DistanceY(g122,g122) = 0.15
    c: DistanceY(g121,g119) = 0.76
    c: Coincident(g114,g123)
    c: Coincident(g119,g123)
    c: Equal(g8,g123)
    c: Parallel(g123,g8)
    c: Vertical(g124)
    c: DistanceY(g124,g124) = 0.33
    c: PointOnObject(g125,g124)
    c: Horizontal(g124,g125)
    c: DistanceY(g124,g125) = 0.76
    c: DistanceX(g125,g124) = 1.43
    c: PointOnObject(g126,g124)
    c: Horizontal(g126,g124)
    c: Vertical(g126,g125)
    c: Vertical(g127)
    c: PointOnObject(g127,g126)
    c: Vertical(g127,g126)
    c: DistanceY(g127,g127) = 0.15
    c: DistanceY(g126,g124) = 0.76
    c: Coincident(g119,g128)
    c: Coincident(g124,g128)
    c: Equal(g8,g128)
    c: Parallel(g128,g8)
    c: Vertical(g129)
    c: DistanceY(g129,g129) = 0.33
    c: PointOnObject(g130,g129)
    c: Horizontal(g129,g130)
    c: DistanceY(g129,g130) = 0.76
    c: DistanceX(g130,g129) = 1.43
    c: PointOnObject(g131,g129)
    c: Horizontal(g131,g129)
    c: Vertical(g131,g130)
    c: Vertical(g132)
    c: PointOnObject(g132,g131)
    c: Vertical(g132,g131)
    c: DistanceY(g132,g132) = 0.15
    c: DistanceY(g131,g129) = 0.76
    c: Coincident(g124,g133)
    c: Coincident(g129,g133)
    c: Equal(g8,g133)
    c: Parallel(g133,g8)
    c: Vertical(g134)
    c: DistanceY(g134,g134) = 0.33
    c: PointOnObject(g135,g134)
    c: Horizontal(g134,g135)
    c: DistanceY(g134,g135) = 0.76
    c: DistanceX(g135,g134) = 1.43
    c: PointOnObject(g136,g134)
    c: Horizontal(g136,g134)
    c: Vertical(g136,g135)
    c: Vertical(g137)
    c: PointOnObject(g137,g136)
    c: Vertical(g137,g136)
    c: DistanceY(g137,g137) = 0.15
    c: DistanceY(g136,g134) = 0.76
    c: Coincident(g129,g138)
    c: Coincident(g134,g138)
    c: Equal(g8,g138)
    c: Parallel(g138,g8)
    c: Vertical(g139)
    c: DistanceY(g139,g139) = 0.33
    c: PointOnObject(g140,g139)
    c: Horizontal(g139,g140)
    c: DistanceY(g139,g140) = 0.76
    c: DistanceX(g140,g139) = 1.43
    c: PointOnObject(g141,g139)
    c: Horizontal(g141,g139)
    c: Vertical(g141,g140)
    c: Vertical(g142)
    c: PointOnObject(g142,g141)
    c: Vertical(g142,g141)
    c: DistanceY(g142,g142) = 0.15
    c: DistanceY(g141,g139) = 0.76
    c: Coincident(g134,g143)
    c: Coincident(g139,g143)
    c: Equal(g8,g143)
    c: Parallel(g143,g8)
    c: Vertical(g144)
    c: DistanceY(g144,g144) = 0.33
    c: PointOnObject(g145,g144)
    c: Horizontal(g144,g145)
    c: DistanceY(g144,g145) = 0.76
    c: DistanceX(g145,g144) = 1.43
    c: PointOnObject(g146,g144)
    c: Horizontal(g146,g144)
    c: Vertical(g146,g145)
    c: Vertical(g147)
    c: PointOnObject(g147,g146)
    c: Vertical(g147,g146)
    c: DistanceY(g147,g147) = 0.15
    c: DistanceY(g146,g144) = 0.76
    c: Coincident(g139,g148)
    c: Coincident(g144,g148)
    c: Equal(g8,g148)
    c: Parallel(g148,g8)
    c: Vertical(g149)
    c: DistanceY(g149,g149) = 0.33
    c: PointOnObject(g150,g149)
    c: Horizontal(g149,g150)
    c: DistanceY(g149,g150) = 0.76
    c: DistanceX(g150,g149) = 1.43
    c: PointOnObject(g151,g149)
    c: Horizontal(g151,g149)
    c: Vertical(g151,g150)
    c: Vertical(g152)
    c: PointOnObject(g152,g151)
    c: Vertical(g152,g151)
    c: DistanceY(g152,g152) = 0.15
    c: DistanceY(g151,g149) = 0.76
    c: Coincident(g144,g153)
    c: Coincident(g149,g153)
    c: Equal(g8,g153)
    c: Parallel(g153,g8)
    c: Vertical(g154)
    c: DistanceY(g154,g154) = 0.33
    c: PointOnObject(g155,g154)
    c: Horizontal(g154,g155)
    c: DistanceY(g154,g155) = 0.76
    c: DistanceX(g155,g154) = 1.43
    c: PointOnObject(g156,g154)
    c: Horizontal(g156,g154)
    c: Vertical(g156,g155)
    c: Vertical(g157)
    c: PointOnObject(g157,g156)
    c: Vertical(g157,g156)
    c: DistanceY(g157,g157) = 0.15
    c: DistanceY(g156,g154) = 0.76
    c: Coincident(g149,g158)
    c: Coincident(g154,g158)
    c: Equal(g8,g158)
    c: Parallel(g158,g8)
    c: Vertical(g159)
    c: DistanceY(g159,g159) = 0.33
    c: PointOnObject(g160,g159)
    c: Horizontal(g159,g160)
    c: DistanceY(g159,g160) = 0.76
    c: DistanceX(g160,g159) = 1.43
    c: PointOnObject(g161,g159)
    c: Horizontal(g161,g159)
    c: Vertical(g161,g160)
    c: Vertical(g162)
    c: PointOnObject(g162,g161)
    c: Vertical(g162,g161)
    c: DistanceY(g162,g162) = 0.15
    c: DistanceY(g161,g159) = 0.76
    c: Coincident(g154,g163)
    c: Coincident(g159,g163)
    c: Equal(g8,g163)
    c: Parallel(g163,g8)
    c: Vertical(g164)
    c: DistanceY(g164,g164) = 0.33
    c: PointOnObject(g165,g164)
    c: Horizontal(g164,g165)
    c: DistanceY(g164,g165) = 0.76
    c: DistanceX(g165,g164) = 1.43
    c: PointOnObject(g166,g164)
    c: Horizontal(g166,g164)
    c: Vertical(g166,g165)
    c: Vertical(g167)
    c: PointOnObject(g167,g166)
    c: Vertical(g167,g166)
    c: DistanceY(g167,g167) = 0.15
    c: DistanceY(g166,g164) = 0.76
    c: Coincident(g159,g168)
    c: Coincident(g164,g168)
    c: Equal(g8,g168)
    c: Parallel(g168,g8)
    c: Vertical(g169)
    c: DistanceY(g169,g169) = 0.33
    c: PointOnObject(g170,g169)
    c: Horizontal(g169,g170)
    c: DistanceY(g169,g170) = 0.76
    c: DistanceX(g170,g169) = 1.43
    c: PointOnObject(g171,g169)
    c: Horizontal(g171,g169)
    c: Vertical(g171,g170)
    c: Vertical(g172)
    c: PointOnObject(g172,g171)
    c: Vertical(g172,g171)
    c: DistanceY(g172,g172) = 0.15
    c: DistanceY(g171,g169) = 0.76
    c: Coincident(g164,g173)
    c: Coincident(g169,g173)
    c: Equal(g8,g173)
    c: Parallel(g173,g8)
    c: Vertical(g174)
    c: DistanceY(g174,g174) = 0.33
    c: PointOnObject(g175,g174)
    c: Horizontal(g174,g175)
    c: DistanceY(g174,g175) = 0.76
    c: DistanceX(g175,g174) = 1.43
    c: PointOnObject(g176,g174)
    c: Horizontal(g176,g174)
    c: Vertical(g176,g175)
    c: DistanceY(g176,g174) = 0.76
    c: Coincident(g169,g177)
    c: Coincident(g174,g177)
    c: Equal(g8,g177)
    c: Parallel(g177,g8)
    c: Horizontal(g178,g-3)
    c: Symmetric(g87,g87,g179)
    c: DistanceX(g179,g-3) = 6
    c: Horizontal(g180)
    c: PointOnObject(g180,g3)
    c: Horizontal(g180,g1)
    c: DistanceX(g181,g-3) = 1
    c: Horizontal(g182)
    c: DistanceX(g182,g182) = 27
    c: DistanceY(g179,g-3) = 0
    c: Symmetric(g172,g172,g183)
    c: Vertical(g184)
    c: DistanceY(g184,g184) = 62.71
    c: PointOnObject(g182,g184)
    c: Horizontal(g182,g184)
    c: Vertical(g185)
    c: PointOnObject(g185,g182)
    c: PointOnObject(g185,g180)
    c: Vertical(g185,g180)
    c: Vertical(g185,g182)
    c: DistanceY(g184,g176) = 4.29
    c: Horizontal(g186,g183)
    c: DistanceX(g183,g186) = 6
    c: Coincident(g187,g186)
    c: PointOnObject(g187,g184)
    c: PointOnObject(g187,g176)
    c: Horizontal(g187,g184)
    c: Vertical(g187,g176)
    c: Symmetric(g182,g182,g188)
FEATURE [PartDesign::Pad] Pad010
  Length = 6
  Length2 = 100
  Profile = -> Sketch037
  Type = 0
FEATURE [Sketcher::SketchObject] Sketch038
  ExternalGeometry = -> [Sketch028,Sketch037]
  MapMode = 5
  Placement = pos=(0,0,6) rot=(0,0,1;0rad)
  Support = -> [Pad010]
  sketch-geometry (6):
    g0: Circle CenterX=-48 CenterY=-69.585 CenterZ=0 NormalX=0 NormalY=0 NormalZ=1 AngleXU=0 Radius=1.6
    g1: Circle CenterX=-36 CenterY=-69.585 CenterZ=0 NormalX=0 NormalY=0 NormalZ=1 AngleXU=0 Radius=1.6
    g2: Circle CenterX=-48 CenterY=-82.585 CenterZ=0 NormalX=0 NormalY=0 NormalZ=1 AngleXU=0 Radius=1.6
    g3: Circle CenterX=-36 CenterY=-82.585 CenterZ=0 NormalX=0 NormalY=0 NormalZ=1 AngleXU=0 Radius=1.6
    g4: LineSegment [constr] StartX=-48 StartY=-69.585 StartZ=0 EndX=-36 EndY=-82.585 EndZ=0
    g5: GeomPoint X=-42 Y=-76.085 Z=0
  constraints (13):
    c: Equal(g0,g1)
    c: Equal(g1,g3)
    c: Equal(g3,g2)
    c: Radius(g0) = 1.6
    c: Horizontal(g0,g1)
    c: Horizontal(g2,g3)
    c: Vertical(g0,g2)
    c: Vertical(g3,g1)
    c: DistanceX(g2,g3) = 12
    c: DistanceY(g2,g0) = 13
    c: Coincident(g4,g0)
    c: Coincident(g4,g3)
    c: Symmetric(g4,g4,g5)
FEATURE [PartDesign::Hole] Hole011
  BaseFeature = -> Pad010
  Depth = 25
  DepthType = 0
  Diameter = 2.2
  DrillPoint = 1
  DrillPointAngle = 118
  HoleCutCountersinkAngle = 90
  HoleCutDepth = 0
  HoleCutDiameter = 2
  HoleCutType = 0
  ModelActualThread = false
  Profile = -> Sketch038
  Tapered = false
  TaperedAngle = 90
  ThreadAngle = 0
  ThreadClass = 0
  ThreadCutOffInner = 0
  ThreadCutOffOuter = 0
  ThreadDirection = 0
  ThreadFit = 0
  ThreadPitch = 0
  ThreadSize = 1
  ThreadType = 1
  Threaded = false
FEATURE [Sketcher::SketchObject] Sketch039
  ExternalGeometry = -> [Sketch037]
  MapMode = 5
  Placement = pos=(0,0,6) rot=(0,0,1;0rad)
  Support = -> [Hole011]
  sketch-geometry (7):
    g0: Circle CenterX=-53.0389 CenterY=-108.835 CenterZ=0 NormalX=0 NormalY=0 NormalZ=1 AngleXU=0 Radius=1.1
    g1: Circle CenterX=-46.0389 CenterY=-108.835 CenterZ=0 NormalX=0 NormalY=0 NormalZ=1 AngleXU=0 Radius=1.1
    g2: Circle CenterX=-39.0389 CenterY=-108.835 CenterZ=0 NormalX=0 NormalY=0 NormalZ=1 AngleXU=0 Radius=1.1
    g3: Circle CenterX=-32.0389 CenterY=-108.835 CenterZ=0 NormalX=0 NormalY=0 NormalZ=1 AngleXU=0 Radius=1.1
    g4: LineSegment [constr] StartX=-46.0389 StartY=-108.835 StartZ=0 EndX=-39.0389 EndY=-108.835 EndZ=0
    g5: GeomPoint X=-42.5389 Y=-108.835 Z=0
    g6: GeomPoint X=-42.5389 Y=-111.835 Z=0
  constraints (16):
    c: Horizontal(g0,g1)
    c: Horizontal(g1,g2)
    c: Horizontal(g2,g3)
    c: Equal(g0,g1)
    c: Equal(g1,g2)
    c: Equal(g2,g3)
    c: Radius(g3) = 1.1
    c: DistanceX(g1,g2) = 7
    c: DistanceX(g0,g1) = 7
    c: DistanceX(g2,g3) = 7
    c: Coincident(g4,g1)
    c: Coincident(g4,g2)
    c: Symmetric(g4,g4,g5)
    c: Symmetric(g-3,g-3,g6)
    c: Vertical(g6,g5)
    c: DistanceY(g-3,g0) = 3
FEATURE [PartDesign::Hole] Hole012
  BaseFeature = -> Hole011
  Depth = 25
  DepthType = 0
  Diameter = 2.2
  DrillPoint = 1
  DrillPointAngle = 118
  HoleCutCountersinkAngle = 90
  HoleCutDepth = 0
  HoleCutDiameter = 2
  HoleCutType = 0
  ModelActualThread = false
  Profile = -> Sketch039
  Tapered = false
  TaperedAngle = 90
  ThreadAngle = 0
  ThreadClass = 0
  ThreadCutOffInner = 0
  ThreadCutOffOuter = 0
  ThreadDirection = 0
  ThreadFit = 0
  ThreadPitch = 0
  ThreadSize = 1
  ThreadType = 1
  Threaded = false
FEATURE [Part::Mirroring] Part__Mirroring  label="Lift (Mirror #1)"
  Base = (0,0,0)
  Normal = (1,0,0)
  Placement = pos=(-56,0,16) rot=(0,0,1;0rad)
  Source = -> Body006021003
FEATURE [App::DocumentObjectGroup] Group003  label="Nozzle Lifts"
  Group = -> [Part__Mirroring,Part__Mirroring001,Part007]
FEATURE [Sketcher::SketchObject] Sketch044  label="CameraSupportHolesFix"
  ExternalGeometry = -> [Sketch027,Sketch025,Sketch023]
  MapMode = 5
  Placement = pos=(0,0,8) rot=(0,0,1;0rad)
  Support = -> [Hole006]
  sketch-geometry (4):
    g0: LineSegment [constr] StartX=-48 StartY=-116.56 StartZ=0 EndX=-48 EndY=-56.56 EndZ=0
    g1: GeomPoint X=-48 Y=-86.56 Z=0
    g2: Circle CenterX=-65 CenterY=-86.56 CenterZ=0 NormalX=0 NormalY=0 NormalZ=1 AngleXU=0 Radius=2.6
    g3: Circle CenterX=65 CenterY=-86.56 CenterZ=0 NormalX=0 NormalY=0 NormalZ=1 AngleXU=0 Radius=2.6
  constraints (10):
    c: Coincident(g0,g-4)
    c: Vertical(g0)
    c: Horizontal(g0,g-3)
    c: Symmetric(g0,g0,g1)
    c: Radius(g2) = 2.6
    c: Horizontal(g2,g1)
    c: DistanceX(g-5,g2) = 5
    c: Equal(g3,g2)
    c: Horizontal(g2,g3)
    c: DistanceX(g3,g-6) = 5
FEATURE [App::Part] Part008  label="Camera support"
  Group = -> [Body006021005,Body006021006,Body006021007]
  Origin = -> Origin021
FEATURE [PartDesign::Body] Body006021005  label="Camera Support Body"
  Group = -> [Sketch045,Pad012,Sketch046,Pocket,Sketch049,Hole017,Sketch053,Pocket016,Sketch054,Hole020,Sketch055,Pocket017,Sketch056,Hole021,Sketch058,Hole022]
  Origin = -> Origin022
  Placement = pos=(0,-82.56,8) rot=(0,0,1;0rad)
  Tip = -> Hole022
FEATURE [PartDesign::Hole] Hole
  BaseFeature = -> Hole006
  Depth = 25
  DepthType = 0
  Diameter = 5.5
  DrillPoint = 1
  DrillPointAngle = 118
  HoleCutCountersinkAngle = 90
  HoleCutDepth = 0
  HoleCutDiameter = 5
  HoleCutType = 0
  ModelActualThread = false
  Profile = -> Sketch044
  Tapered = false
  TaperedAngle = 90
  ThreadAngle = 0
  ThreadClass = 0
  ThreadCutOffInner = 0
  ThreadCutOffOuter = 0
  ThreadDirection = 0
  ThreadFit = 0
  ThreadPitch = 0
  ThreadSize = 6
  ThreadType = 1
  Threaded = false
FEATURE [Sketcher::SketchObject] Sketch049  label="Camera Support Fix Holes"
  ExternalGeometry = -> [Sketch044,Sketch023]
  MapMode = 5
  Placement = pos=(0,0,0) rot=(1,0,0;3.14159rad)
  sketch-geometry (2):
    g0: Circle CenterX=-65 CenterY=4 CenterZ=0 NormalX=0 NormalY=0 NormalZ=1 AngleXU=0 Radius=2.6
    g1: Circle CenterX=65 CenterY=4 CenterZ=0 NormalX=0 NormalY=0 NormalZ=1 AngleXU=0 Radius=2.6
  constraints (6):
    c: Equal(g0,g1)
    c: Radius(g0) = 2.6
    c: DistanceY(g-1,g0) = 4
    c: Horizontal(g0,g1)
    c: DistanceX(g0,g-1) = 65
    c: DistanceX(g-1,g1) = 65
FEATURE [PartDesign::Hole] Hole017
  BaseFeature = -> Pocket
  Depth = 15
  DepthType = 0
  Diameter = 4.2
  DrillPoint = 1
  DrillPointAngle = 118
  HoleCutCountersinkAngle = 90
  HoleCutDepth = 0
  HoleCutDiameter = 5
  HoleCutType = 0
  ModelActualThread = false
  Placement = pos=(0,0,0) rot=(1,0,0;1.5708rad)
  Profile = -> Sketch049
  Tapered = false
  TaperedAngle = 90
  ThreadAngle = 60
  ThreadClass = 0
  ThreadCutOffInner = 0.0866025
  ThreadCutOffOuter = 0.173205
  ThreadDirection = 1
  ThreadFit = 0
  ThreadPitch = 0.8
  ThreadSize = 6
  ThreadType = 1
  Threaded = true
FEATURE [Sketcher::SketchObject] Sketch051
  ExternalGeometry = -> [Sketch035]
  MapMode = 2
  Support = -> [Hole018]
  sketch-geometry (3):
    g0: Circle CenterX=-28 CenterY=-35.56 CenterZ=0 NormalX=0 NormalY=0 NormalZ=1 AngleXU=0 Radius=2.6
    g1: Circle CenterX=0 CenterY=-35.56 CenterZ=0 NormalX=0 NormalY=0 NormalZ=1 AngleXU=0 Radius=2.6
    g2: Circle CenterX=28 CenterY=-35.56 CenterZ=0 NormalX=0 NormalY=0 NormalZ=1 AngleXU=0 Radius=2.6
  constraints (9):
    c: Equal(g0,g1)
    c: Equal(g1,g2)
    c: Radius(g0) = 2.6
    c: Horizontal(g0,g1)
    c: Horizontal(g1,g2)
    c: Vertical(g0,g-3)
    c: Vertical(g2,g-4)
    c: Vertical(g1,g-1)
    c: DistanceY(g1,g-1) = 35.56
FEATURE [PartDesign::Hole] Hole018
  BaseFeature = -> Hole010
  Depth = 25
  DepthType = 0
  Diameter = 5.5
  DrillPoint = 1
  DrillPointAngle = 118
  HoleCutCountersinkAngle = 90
  HoleCutDepth = 0
  HoleCutDiameter = 5
  HoleCutType = 0
  ModelActualThread = false
  Profile = -> Sketch051
  Reversed = true
  Tapered = false
  TaperedAngle = 90
  ThreadAngle = 0
  ThreadClass = 0
  ThreadCutOffInner = 0
  ThreadCutOffOuter = 0
  ThreadDirection = 0
  ThreadFit = 0
  ThreadPitch = 0
  ThreadSize = 6
  ThreadType = 1
  Threaded = false
FEATURE [Drawing::FeaturePage] Page  label="Back Plate"
  EditableTexts = <owner>.org | 08/18/2020 | Jaume Olivé	 | 08/18/2020 | WEIGHT | 2 | 1 | Whitecat OpenPNP Head | Back Plate
  Group = -> [View,dim001,dim002,dim003,dim004,dim005,centerLines001,dim006,dim007,dim008,dim009,dim010,dim011,dim012,dim013,dim014,dim015,rad001,centerLines002,dim016,dim017,dim018,dim019,dim020,dia001,text001,dia002,text002,dia003,dia004,text003,text004,dia005,dia006,dia007,text005,text006,text007,dia008,dia009,text008,text009,text010,table001,Ortho013,text072,noteCircle004]
  Template = /Applications/FreeCAD.app/Contents/Resources/data/Mod/Drawing/Templates/A3_Landscape.svg
FEATURE [Drawing::FeatureViewPart] View
  Direction = (0,0,1)
  HiddenWidth = 0.15
  LineWidth = 0.35
  Rotation = 0
  ShowHiddenLines = false
  ShowSmoothLines = false
  Source = -> Body
  Tolerance = 0.05
  ViewResult = <g id="View"\n   transform="rotate(0,150,30) translate(150,30) scale(1,1)"\n  >\n<g   fill="none"\n   stroke="rgb(0, 0, 0)"\n   stroke-linecap="butt"\n   stroke-linejoin="miter"\n   stroke-width="0.350000"\n   transform="scale(1,-1)"\n  >\n<path id= "1" d=" M -65 -101.544 L -48 -101.544 " />\n<path d="M-65 -101.544 A5 5 0 0 1 -70 -106.544" /><path d="M-48 -101.544 A5 5 0 0 1 -43 -96.5441" /><path id= "4" d=" M -70 -124.41 L -70 -106.544 " />\n<path id= "5" d=" M -43 -96.5441 L -43 -36.56 " />\n<path d="M-70 -124.41 A5 5 0 0 1 -65 -129.41" /><path d="M-38 -31.56 A5 5 0 0 1 -43 -36.56" /><path id= "8" d=" M 65 -129.41 L -65 -129.41 " />\n<path id= "9" d=" M -38 -31.56 L 38 -31.56 " />\n<path d="M65 -129.41 A5 5 0 0 1 70 -124.41" /><path d="M43 -36.56 A5 5 0 0 1 38 -31.56" /><path id= "12" d=" M 70 -106.544 L 70 -124.41 " />\n<path id= "13" d=" M 43 -36.56 L 43 -96.5441 " />\n<path d="M70 -106.544 A5 5 0 0 1 65 -101.544" /><path d="M43 -96.5441 A5 5 0 0 1 48 -101.544" /><path id= "16" d=" M 48 -101.544 L 65 -101.544 " />\n<circle cx ="-28" cy ="-56.56" r ="3.6" /><circle cx ="-28" cy ="-35.56" r ="2.75" /><circle cx ="0" cy ="-35.56" r ="2.75" /><circle cx ="28" cy ="-35.56" r ="2.75" /><circle cx ="28" cy ="-56.56" r ="3.6" /><circle cx ="28" cy ="-71.57" r ="2.1" /><circle cx ="-28" cy ="-71.57" r ="2.1" /><circle cx ="-48" cy ="-116.56" r ="2.1" /><circle cx ="48" cy ="-116.56" r ="2.1" /></g>\n</g>
  Visible = true
  X = 150
  Y = 30
FEATURE [App::DocumentObjectGroup] Group004  label="Drawings"
  Group = -> [Page,Page001,Page002,Page003,Page004]
FEATURE [Drawing::FeaturePage] Page001  label="Left Nozzle Lift"
  EditableTexts = <owner>.org | 08/18/2020 | Jaume Olivé	 | 08/18/2020 | WEIGHT | 3 | 1 | Whitecat OpenPNP Head | Left Nozzle Lift
  Group = -> [Ortho,dim021,dim022,dim023,dim024,rad002,dim025,dim026,dim027,dim028,dim029,dim030,dim031,dim032,dim033,dim034,dim035,dia010,text011,text012,text013,text014,dia011,text015,text016,text017,text018,Ortho001,dim036,centerLines003,centerLines004,centerLines006,rad003,dim038,dim039,dim040,dim041,dia012,text019,text020,text021,text022,dim037,Ortho007,dim042,dim043,dim044,dim045,dim046,dim047,dim048,+34 more]
  Template = /Applications/FreeCAD.app/Contents/Resources/data/Mod/Drawing/Templates/A3_Landscape.svg
FEATURE [Drawing::FeatureViewPart] Ortho  label="Ortho_0_0"
  Direction = (0,0,1)
  HiddenWidth = 0.15
  LineWidth = 0.35
  Rotation = 0
  Scale = 1.2
  ShowHiddenLines = false
  ShowSmoothLines = false
  Source = -> Body006021003
  Tolerance = 0.05
  ViewResult = <blob: 8825 chars omitted>
  Visible = false
  X = 180.81
  Y = 64.89
FEATURE [Drawing::FeatureViewPart] Ortho008  label="Ortho_0_001"
  Direction = (1,0,0)
  HiddenWidth = 0.15
  LineWidth = 0.35
  Rotation = 180
  Scale = 1.2
  ShowHiddenLines = false
  ShowSmoothLines = false
  Source = -> Body006021003
  Tolerance = 0.05
  ViewResult = <blob: 21010 chars omitted>
  Visible = false
  X = 40
  Y = 64.89
FEATURE [Drawing::FeaturePage] Page002  label="Front Plate"
  EditableTexts = <owner>.org | 08/18/2020 | Jaume Olivé	 | 08/18/2020 | WEIGHT | 1 | 1 | Whitecat OpenPNP Head | Front Plate
  Group = -> [Ortho009,centerLines005,text028,text029,text030,text031,text032,text033,text034,text035,text036,text037,text038,text039,text040,text041,text042,text043,text044,text045,text046,text047,dim057,dim058,dim059,dim060,dim061,dim062,dim063,dim064,dim065,dia014,dim066,dim067,dim068,dim069,dim070,dim071,dia015,text048,text049,dim072,dim073,rad004,rad005,text050,text051,text052,text053,text054,text055,+74 more]
  Template = /Applications/FreeCAD.app/Contents/Resources/data/Mod/Drawing/Templates/A3_Landscape.svg
FEATURE [Drawing::FeatureViewPart] Ortho009  label="Ortho_0_002"
  Direction = (0,0,1)
  HiddenWidth = 0.15
  LineWidth = 0.35
  Rotation = 0
  ShowHiddenLines = false
  ShowSmoothLines = false
  Source = -> Body006021002
  Tolerance = 0.05
  ViewResult = <blob: 3388 chars omitted>
  Visible = false
  X = 140
  Y = 70
FEATURE [Drawing::FeatureViewPart] Ortho011  label="Ortho_Front_Plate_Preview"
  Direction = (0.57735,0.57735,0.57735)
  HiddenWidth = 0.15
  LineWidth = 0.35
  Rotation = -4.13e-14
  Scale = 0.7
  ShowHiddenLines = false
  ShowSmoothLines = false
  Source = -> Body006021002
  Tolerance = 0.05
  ViewResult = <blob: 14880 chars omitted>
  Visible = false
  X = 360
  Y = 50
FEATURE [Drawing::FeatureViewPart] Ortho013  label="Ortho_Back_Plate_Preview"
  Direction = (0.57735,0.57735,0.57735)
  HiddenWidth = 0.15
  LineWidth = 0.35
  Rotation = -4.13e-14
  Scale = 0.9
  ShowHiddenLines = false
  ShowSmoothLines = false
  Source = -> Body
  Tolerance = 0.05
  ViewResult = <blob: 4540 chars omitted>
  Visible = true
  X = 348.91
  Y = 10
FEATURE [Sketcher::SketchObject] Sketch052
  ExternalGeometry = -> [Sketch031]
  MapMode = 5
  Placement = pos=(0,0,6) rot=(0,0,1;0rad)
  Support = -> [Hole012]
  sketch-geometry (8):
    g0: LineSegment [constr] StartX=-45.38 StartY=16.99 StartZ=0 EndX=-38.62 EndY=16.99 EndZ=0
    g1: GeomPoint X=-42 Y=16.99 Z=0
    g2: Circle CenterX=-46 CenterY=-9.33 CenterZ=0 NormalX=0 NormalY=0 NormalZ=1 AngleXU=0 Radius=1.1
    g3: Circle CenterX=-38 CenterY=-9.33 CenterZ=0 NormalX=0 NormalY=0 NormalZ=1 AngleXU=0 Radius=1.1
    g4: Circle CenterX=-46 CenterY=-17.33 CenterZ=0 NormalX=0 NormalY=0 NormalZ=1 AngleXU=0 Radius=1.1
    g5: Circle CenterX=-38 CenterY=-17.33 CenterZ=0 NormalX=0 NormalY=0 NormalZ=1 AngleXU=0 Radius=1.1
    g6: LineSegment [constr] StartX=-46 StartY=-9.33 StartZ=0 EndX=-38 EndY=-17.33 EndZ=0
    g7: GeomPoint X=-42 Y=-13.33 Z=0
  constraints (18):
    c: Coincident(g0,g-3)
    c: Coincident(g0,g-4)
    c: Symmetric(g0,g0,g1)
    c: Equal(g2,g3)
    c: Equal(g3,g5)
    c: Equal(g5,g4)
    c: Radius(g2) = 1.1
    c: Horizontal(g2,g3)
    c: Horizontal(g4,g5)
    c: Vertical(g2,g4)
    c: Vertical(g3,g5)
    c: DistanceX(g2,g3) = 8
    c: DistanceY(g5,g3) = 8
    c: Coincident(g6,g2)
    c: Coincident(g6,g5)
    c: Symmetric(g6,g6,g7)
    c: Vertical(g7,g1)
    c: DistanceY(g7,g1) = 30.32
FEATURE [PartDesign::Hole] Hole019
  BaseFeature = -> Hole012
  Depth = 25
  DepthType = 0
  Diameter = 1.6
  DrillPoint = 1
  DrillPointAngle = 118
  HoleCutCountersinkAngle = 90
  HoleCutDepth = 0
  HoleCutDiameter = 2
  HoleCutType = 0
  ModelActualThread = false
  Profile = -> Sketch052
  Tapered = false
  TaperedAngle = 90
  ThreadAngle = 60
  ThreadClass = 0
  ThreadCutOffInner = 0.0433013
  ThreadCutOffOuter = 0.0866025
  ThreadDirection = 1
  ThreadFit = 0
  ThreadPitch = 0.4
  ThreadSize = 1
  ThreadType = 1
  Threaded = true
FEATURE [Sketcher::SketchObject] Sketch053
  ExternalGeometry = -> [Sketch046]
  MapMode = 5
  Placement = pos=(0,-1e-16,0) rot=(-1,0,0;1.5708rad)
  Support = -> [Hole017]
  sketch-geometry (4):
    g0: LineSegment StartX=-16 StartY=-86 StartZ=0 EndX=16 EndY=-86 EndZ=0
    g1: LineSegment StartX=16 StartY=-86 StartZ=0 EndX=16 EndY=-54 EndZ=0
    g2: LineSegment StartX=16 StartY=-54 StartZ=0 EndX=-16 EndY=-54 EndZ=0
    g3: LineSegment StartX=-16 StartY=-54 StartZ=0 EndX=-16 EndY=-86 EndZ=0
  constraints (12):
    c: Coincident(g0,g1)
    c: Coincident(g1,g2)
    c: Coincident(g2,g3)
    c: Coincident(g3,g0)
    c: Horizontal(g0)
    c: Horizontal(g2)
    c: Vertical(g1)
    c: Vertical(g3)
    c: Horizontal(g0,g-4)
    c: Vertical(g0,g-3)
    c: Vertical(g0,g-5)
    c: Horizontal(g2,g-6)
FEATURE [PartDesign::Pocket] Pocket016
  BaseFeature = -> Hole017
  Length = 4
  Length2 = 100
  Placement = pos=(0,0,0) rot=(1,0,0;1.5708rad)
  Profile = -> Sketch053
  Type = 0
FEATURE [Sketcher::SketchObject] Sketch054  label="Camera Fix Holes"
  ExternalGeometry = -> [Sketch046]
  MapMode = 5
  Placement = pos=(0,-1e-16,0) rot=(-1,0,0;1.5708rad)
  Support = -> [Pocket016]
  sketch-geometry (6):
    g0: Circle CenterX=-14 CenterY=-84 CenterZ=0 NormalX=0 NormalY=0 NormalZ=1 AngleXU=0 Radius=1.1
    g1: Circle CenterX=14 CenterY=-84 CenterZ=0 NormalX=0 NormalY=0 NormalZ=1 AngleXU=0 Radius=1.1
    g2: Circle CenterX=-14 CenterY=-56 CenterZ=0 NormalX=0 NormalY=0 NormalZ=1 AngleXU=0 Radius=1.1
    g3: Circle CenterX=14 CenterY=-56 CenterZ=0 NormalX=0 NormalY=0 NormalZ=1 AngleXU=0 Radius=1.1
    g4: LineSegment [constr] StartX=-16 StartY=-82 StartZ=0 EndX=-12 EndY=-86 EndZ=0
    g5: GeomPoint X=-14 Y=-84 Z=0
  constraints (15):
    c: Equal(g0,g1)
    c: Equal(g1,g3)
    c: Equal(g3,g2)
    c: Radius(g0) = 1.1
    c: Horizontal(g0,g1)
    c: Horizontal(g2,g3)
    c: Vertical(g0,g2)
    c: Vertical(g1,g3)
    c: DistanceX(g0,g1) = 28
    c: DistanceY(g3,g1) = -28
    c: Coincident(g4,g-3)
    c: Coincident(g4,g-4)
    c: Symmetric(g4,g4,g5)
    c: Horizontal(g0,g5)
    c: Vertical(g0,g5)
FEATURE [PartDesign::Hole] Hole020
  BaseFeature = -> Pocket016
  Depth = 25
  DepthType = 0
  Diameter = 1.6
  DrillPoint = 1
  DrillPointAngle = 118
  HoleCutCountersinkAngle = 90
  HoleCutDepth = 0
  HoleCutDiameter = 2
  HoleCutType = 0
  ModelActualThread = false
  Placement = pos=(0,0,0) rot=(1,0,0;1.5708rad)
  Profile = -> Sketch054
  Tapered = false
  TaperedAngle = 90
  ThreadAngle = 60
  ThreadClass = 0
  ThreadCutOffInner = 0.0433013
  ThreadCutOffOuter = 0.0866025
  ThreadDirection = 1
  ThreadFit = 0
  ThreadPitch = 0.4
  ThreadSize = 1
  ThreadType = 1
  Threaded = true
FEATURE [Sketcher::SketchObject] Sketch055  label="Camera Power Supply Hole"
  ExternalGeometry = -> [Sketch046]
  MapMode = 5
  Placement = pos=(0,-1e-16,0) rot=(-1,0,0;1.5708rad)
  Support = -> [Hole020]
  sketch-geometry (9):
    g0: LineSegment StartX=-39 StartY=-83 StartZ=0 EndX=-31 EndY=-83 EndZ=0
    g1: LineSegment StartX=-31 StartY=-83 StartZ=0 EndX=-31 EndY=-86 EndZ=0
    g2: LineSegment StartX=-31 StartY=-86 StartZ=0 EndX=-39 EndY=-86 EndZ=0
    g3: LineSegment StartX=-39 StartY=-86 StartZ=0 EndX=-39 EndY=-83 EndZ=0
    g4: GeomPoint X=-31 Y=-84.5 Z=0
    g5: LineSegment StartX=31 StartY=-83 StartZ=0 EndX=39 EndY=-83 EndZ=0
    g6: LineSegment StartX=39 StartY=-83 StartZ=0 EndX=39 EndY=-86 EndZ=0
    g7: LineSegment StartX=39 StartY=-86 StartZ=0 EndX=31 EndY=-86 EndZ=0
    g8: LineSegment StartX=31 StartY=-86 StartZ=0 EndX=31 EndY=-83 EndZ=0
  constraints (25):
    c: Coincident(g0,g1)
    c: Coincident(g1,g2)
    c: Coincident(g2,g3)
    c: Coincident(g3,g0)
    c: Horizontal(g0)
    c: Horizontal(g2)
    c: Vertical(g1)
    c: Vertical(g3)
    c: DistanceY(g3,g3) = 3
    c: DistanceX(g0,g0) = 8
    c: Symmetric(g1,g1,g4)
    c: DistanceX(g1,g-3) = 15
    c: Horizontal(g1,g-4)
    c: Coincident(g5,g6)
    c: Coincident(g6,g7)
    c: Coincident(g7,g8)
    c: Coincident(g8,g5)
    c: Horizontal(g5)
    c: Horizontal(g7)
    c: Vertical(g6)
    c: Vertical(g8)
    c: Equal(g0,g5)
    c: Equal(g3,g8)
    c: Horizontal(g1,g7)
    c: DistanceX(g-5,g5) = 15
FEATURE [PartDesign::Pocket] Pocket017
  BaseFeature = -> Hole020
  Length = 5
  Length2 = 100
  Placement = pos=(0,0,0) rot=(1,0,0;1.5708rad)
  Profile = -> Sketch055
  Type = 1
FEATURE [Sketcher::SketchObject] Sketch056  label="Camera Cable Fix"
  ExternalGeometry = -> [Sketch045]
  MapMode = 5
  Placement = pos=(0,-1e-16,0) rot=(-1,0,0;1.5708rad)
  Support = -> [Pocket017]
  sketch-geometry (12):
    g0: Circle CenterX=-33 CenterY=-51.65 CenterZ=0 NormalX=0 NormalY=0 NormalZ=1 AngleXU=0 Radius=1.1
    g1: Circle CenterX=-23 CenterY=-51.65 CenterZ=0 NormalX=0 NormalY=0 NormalZ=1 AngleXU=0 Radius=1.1
    g2: Circle CenterX=23 CenterY=-51.65 CenterZ=0 NormalX=0 NormalY=0 NormalZ=1 AngleXU=0 Radius=1.1
    g3: Circle CenterX=33 CenterY=-51.65 CenterZ=0 NormalX=0 NormalY=0 NormalZ=1 AngleXU=0 Radius=1.1
    g4: Circle CenterX=-47 CenterY=-51.65 CenterZ=0 NormalX=0 NormalY=0 NormalZ=1 AngleXU=0 Radius=1.1
    g5: Circle CenterX=-47 CenterY=-61.65 CenterZ=0 NormalX=0 NormalY=0 NormalZ=1 AngleXU=0 Radius=1.1
    g6: Circle CenterX=47 CenterY=-51.65 CenterZ=0 NormalX=0 NormalY=0 NormalZ=1 AngleXU=0 Radius=1.1
    g7: Circle CenterX=47 CenterY=-61.65 CenterZ=0 NormalX=0 NormalY=0 NormalZ=1 AngleXU=0 Radius=1.1
    g8: Circle CenterX=-63.57 CenterY=-58.19 CenterZ=0 NormalX=0 NormalY=0 NormalZ=1 AngleXU=0 Radius=1.1
    g9: Circle CenterX=-56 CenterY=-51.65 CenterZ=0 NormalX=0 NormalY=0 NormalZ=1 AngleXU=0 Radius=1.1
    g10: Circle CenterX=56 CenterY=-51.65 CenterZ=0 NormalX=0 NormalY=0 NormalZ=1 AngleXU=0 Radius=1.1
    g11: Circle CenterX=63.57 CenterY=-58.19 CenterZ=0 NormalX=0 NormalY=0 NormalZ=1 AngleXU=0 Radius=1.1
  constraints (36):
    c: Equal(g0,g1)
    c: Equal(g1,g2)
    c: Equal(g2,g3)
    c: Radius(g0) = 1.1
    c: Horizontal(g0,g1)
    c: Horizontal(g1,g2)
    c: Horizontal(g2,g3)
    c: DistanceX(g2,g3) = 10
    c: DistanceX(g-3,g0) = 27
    c: DistanceX(g0,g1) = 10
    c: DistanceX(g3,g-3) = 27
    c: Equal(g4,g5)
    c: Equal(g5,g6)
    c: Equal(g6,g7)
    c: Equal(g7,g0)
    c: Vertical(g4,g5)
    c: Vertical(g6,g7)
    c: DistanceY(g5,g4) = 10
    c: DistanceY(g7,g6) = 10
    c: Horizontal(g4,g6)
    c: DistanceX(g-3,g4) = 13
    c: DistanceX(g6,g-3) = 13
    c: Equal(g8,g9)
    c: Equal(g9,g5)
    c: DistanceX(g-3,g9) = 4
    c: DistanceX(g8,g9) = 7.57
    c: DistanceY(g8,g-3) = 11.19
    c: Equal(g10,g11)
    c: Equal(g11,g9)
    c: DistanceY(g9,g-3) = 4.65
    c: Horizontal(g9,g10)
    c: DistanceX(g10,g-3) = 4
    c: Horizontal(g11,g8)
    c: DistanceX(g10,g11) = 7.57
    c: Horizontal(g9,g4)
    c: Horizontal(g4,g0)
FEATURE [PartDesign::Hole] Hole021
  BaseFeature = -> Pocket017
  Depth = 25
  DepthType = 0
  Diameter = 1.6
  DrillPoint = 1
  DrillPointAngle = 118
  HoleCutCountersinkAngle = 90
  HoleCutDepth = 0
  HoleCutDiameter = 2
  HoleCutType = 0
  ModelActualThread = false
  Placement = pos=(0,0,0) rot=(1,0,0;1.5708rad)
  Profile = -> Sketch056
  Tapered = false
  TaperedAngle = 90
  ThreadAngle = 60
  ThreadClass = 0
  ThreadCutOffInner = 0.0433013
  ThreadCutOffOuter = 0.0866025
  ThreadDirection = 1
  ThreadFit = 0
  ThreadPitch = 0.4
  ThreadSize = 1
  ThreadType = 1
  Threaded = true
FEATURE [Sketcher::SketchObject] Sketch058  label="Camera Square Fix"
  ExternalGeometry = -> [Sketch045]
  MapMode = 5
  Placement = pos=(0,-1e-16,0) rot=(-1,0,0;1.5708rad)
  Support = -> [Hole021]
  sketch-geometry (6):
    g0: Circle CenterX=65 CenterY=-35 CenterZ=0 NormalX=0 NormalY=0 NormalZ=1 AngleXU=0 Radius=1.1
    g1: Circle CenterX=65 CenterY=-20 CenterZ=0 NormalX=0 NormalY=0 NormalZ=1 AngleXU=0 Radius=1.1
    g2: Circle CenterX=-65 CenterY=-35 CenterZ=0 NormalX=0 NormalY=0 NormalZ=1 AngleXU=0 Radius=1.1
    g3: Circle CenterX=-65 CenterY=-20 CenterZ=0 NormalX=0 NormalY=0 NormalZ=1 AngleXU=0 Radius=1.1
    g4: GeomPoint X=-65 Y=0 Z=0
    g5: GeomPoint X=65 Y=0 Z=0
  constraints (14):
    c: Equal(g2,g0)
    c: Equal(g0,g1)
    c: Equal(g1,g3)
    c: Radius(g2) = 1.1
    c: Vertical(g2,g3)
    c: Vertical(g0,g1)
    c: Symmetric(g-3,g-3,g4)
    c: Symmetric(g-4,g-4,g5)
    c: Vertical(g2,g4)
    c: Vertical(g0,g5)
    c: Horizontal(g2,g0)
    c: Horizontal(g3,g1)
    c: DistanceY(g-5,g2) = 12
    c: DistanceY(g3,g-3) = 20
FEATURE [PartDesign::Hole] Hole022
  BaseFeature = -> Hole021
  Depth = 25
  DepthType = 0
  Diameter = 2.2
  DrillPoint = 1
  DrillPointAngle = 118
  HoleCutCountersinkAngle = 90
  HoleCutDepth = 0
  HoleCutDiameter = 2
  HoleCutType = 0
  ModelActualThread = false
  Placement = pos=(0,0,0) rot=(1,0,0;1.5708rad)
  Profile = -> Sketch058
  Tapered = false
  TaperedAngle = 90
  ThreadAngle = 60
  ThreadClass = 0
  ThreadCutOffInner = 0.0433013
  ThreadCutOffOuter = 0.0866025
  ThreadDirection = 0
  ThreadFit = 0
  ThreadPitch = 0.4
  ThreadSize = 1
  ThreadType = 1
  Threaded = false
FEATURE [Sketcher::SketchObject] Sketch060  label="Front Cable Hole"
  ExternalGeometry = -> [Sketch023]
  MapMode = 5
  Support = -> [XY_Plane016]
  sketch-geometry (2):
    g0: Circle CenterX=-62 CenterY=-34.4202 CenterZ=0 NormalX=0 NormalY=0 NormalZ=1 AngleXU=0 Radius=5
    g1: Circle CenterX=62 CenterY=-34.4202 CenterZ=0 NormalX=0 NormalY=0 NormalZ=1 AngleXU=0 Radius=5
  constraints (6):
    c: Equal(g0,g1)
    c: Radius(g0) = 5
    c: Horizontal(g0,g1)
    c: DistanceX(g1,g-3) = 8
    c: DistanceX(g-4,g0) = 8
    c: DistanceY(g-4,g0) = 90
FEATURE [PartDesign::Pocket] Pocket018
  BaseFeature = -> Hole
  Length = 5
  Length2 = 100
  Profile = -> Sketch060
  Reversed = true
  Type = 1
FEATURE [Sketcher::SketchObject] Sketch061
  ExternalGeometry = -> [Sketch044,Sketch060]
  MapMode = 5
  Placement = pos=(0,0,8) rot=(0,0,1;0rad)
  Support = -> [Pocket018]
  sketch-geometry (4):
    g0: Circle CenterX=-57 CenterY=-66.56 CenterZ=0 NormalX=0 NormalY=0 NormalZ=1 AngleXU=0 Radius=1.1
    g1: Circle CenterX=-57 CenterY=-76.56 CenterZ=0 NormalX=0 NormalY=0 NormalZ=1 AngleXU=0 Radius=1.1
    g2: Circle CenterX=57 CenterY=-66.56 CenterZ=0 NormalX=0 NormalY=0 NormalZ=1 AngleXU=0 Radius=1.1
    g3: Circle CenterX=57 CenterY=-76.56 CenterZ=0 NormalX=0 NormalY=0 NormalZ=1 AngleXU=0 Radius=1.1
  constraints (12):
    c: Equal(g0,g1)
    c: Equal(g1,g2)
    c: Equal(g2,g3)
    c: Radius(g0) = 1.1
    c: Vertical(g0,g1)
    c: Vertical(g2,g3)
    c: Horizontal(g0,g2)
    c: Horizontal(g1,g3)
    c: DistanceY(g1,g0) = 10
    c: DistanceY(g-3,g1) = 10
    c: DistanceX(g-5,g0) = 5
    c: DistanceX(g2,g-6) = 5
FEATURE [PartDesign::Hole] Hole023
  BaseFeature = -> Pocket018
  Depth = 25
  DepthType = 0
  Diameter = 1.6
  DrillPoint = 1
  DrillPointAngle = 118
  HoleCutCountersinkAngle = 90
  HoleCutDepth = 0
  HoleCutDiameter = 2
  HoleCutType = 0
  ModelActualThread = false
  Profile = -> Sketch061
  Tapered = false
  TaperedAngle = 90
  ThreadAngle = 60
  ThreadClass = 0
  ThreadCutOffInner = 0.0433013
  ThreadCutOffOuter = 0.0866025
  ThreadDirection = 1
  ThreadFit = 0
  ThreadPitch = 0.4
  ThreadSize = 1
  ThreadType = 1
  Threaded = true
FEATURE [Drawing::FeaturePage] Page003  label="Camera"
  EditableTexts = <owner>.org | 08/18/2020 | Jaume Olivé	 | 08/18/2020 | WEIGHT | 4 | 1 | Whitecat OpenPNP Head | Camera
  Group = -> [Ortho014,centerLines008,centerLines009,centerLines010,dim114,dim115,dim116,dim117,dim118,rad009,dim122,dim123,dim126,dim127,dim128,dim129,dim130,dim131,dim132,dim133,dim134,dim135,dim136,dim124,dim125,text084,text085,text086,text088,text089,text090,text091,text092,text093,text094,dim120,dim121,dim137,dim150,dim151,dim152,dim153,dim154,dim156,dim157,dia022,text095,text096,text097,text098,dim119,+37 more]
  Template = /Applications/FreeCAD.app/Contents/Resources/data/Mod/Drawing/Templates/A3_Landscape.svg
FEATURE [Drawing::FeatureViewPart] Ortho014  label="Ortho_CameraSupport"
  Direction = (0,1,0)
  HiddenWidth = 0.15
  LineWidth = 0.35
  Rotation = 90
  Scale = 1.2
  ShowHiddenLines = false
  ShowSmoothLines = false
  Source = -> Body006021005
  Tolerance = 0.05
  ViewResult = <blob: 2599 chars omitted>
  Visible = true
  X = 140
  Y = 63.1
FEATURE [Drawing::FeatureViewPart] Ortho017  label="Ortho_0_003"
  Direction = (0,0,-1)
  HiddenWidth = 0.15
  LineWidth = 0.35
  Rotation = 180
  Scale = 1.2
  ShowHiddenLines = false
  ShowSmoothLines = false
  Source = -> Body006021005
  Tolerance = 0.05
  ViewResult = <g id="Ortho_0_003"\n   transform="rotate(180,140,310) translate(140,310) scale(1.2,1.2)"\n  >\n<g   fill="none"\n   stroke="rgb(0, 0, 0)"\n   stroke-linecap="butt"\n   stroke-linejoin="miter"\n   stroke-width="0.291667"\n   transform="scale(1,-1)"\n  >\n<path id= "1" d=" M -70 -82.56 L -70 -90.56 " />\n<path id= "2" d=" M -70 -82.56 L -60 -82.56 " />\n<path id= "3" d=" M -70 -90.56 L -60 -90.56 " />\n<path id= "4" d=" M -60 -82.56 L -60 -90.56 " />\n<circle cx ="-65" cy ="-86.56" r ="2.1" /><path id= "6" d=" M -60 -82.56 L 60 -82.56 " />\n<path id= "7" d=" M 60 -82.56 L 70 -82.56 " />\n<path id= "8" d=" M -60 -90.56 L 60 -90.56 " />\n<path id= "9" d=" M 60 -90.56 L 70 -90.56 " />\n<path id= "10" d=" M 70 -82.56 L 70 -90.56 " />\n<path id= "11" d=" M 60 -82.56 L 60 -90.56 " />\n<circle cx ="65" cy ="-86.56" r ="2.1" /></g>\n</g>
  Visible = true
  X = 140
  Y = 310
FEATURE [Sketcher::SketchObject] Sketch062
  ExternalGeometry = -> [Sketch044,Sketch023]
  MapMode = 5
  Placement = pos=(0,0,8) rot=(0,0,1;0rad)
  Support = -> [Hole023]
  sketch-geometry (4):
    g0: Circle CenterX=-65 CenterY=-109.42 CenterZ=0 NormalX=0 NormalY=0 NormalZ=1 AngleXU=0 Radius=1.1
    g1: Circle CenterX=-65 CenterY=-94.56 CenterZ=0 NormalX=0 NormalY=0 NormalZ=1 AngleXU=0 Radius=1.1
    g2: Circle CenterX=65 CenterY=-109.42 CenterZ=0 NormalX=0 NormalY=0 NormalZ=1 AngleXU=0 Radius=1.1
    g3: Circle CenterX=65 CenterY=-94.56 CenterZ=0 NormalX=0 NormalY=0 NormalZ=1 AngleXU=0 Radius=1.1
  constraints (12):
    c: Equal(g0,g1)
    c: Equal(g1,g2)
    c: Equal(g2,g3)
    c: Radius(g0) = 1.1
    c: Vertical(g0,g1)
    c: Vertical(g2,g3)
    c: Horizontal(g0,g2)
    c: Horizontal(g1,g3)
    c: Vertical(g1,g-3)
    c: Vertical(g3,g-4)
    c: DistanceY(g-5,g0) = 15
    c: DistanceY(g1,g-3) = 8
FEATURE [PartDesign::Hole] Hole024
  BaseFeature = -> Hole023
  Depth = 25
  DepthType = 0
  Diameter = 2.2
  DrillPoint = 1
  DrillPointAngle = 118
  HoleCutCountersinkAngle = 90
  HoleCutDepth = 0
  HoleCutDiameter = 2
  HoleCutType = 0
  ModelActualThread = false
  Profile = -> Sketch062
  Tapered = false
  TaperedAngle = 90
  ThreadAngle = 0
  ThreadClass = 0
  ThreadCutOffInner = 0
  ThreadCutOffOuter = 0
  ThreadDirection = 0
  ThreadFit = 0
  ThreadPitch = 0
  ThreadSize = 1
  ThreadType = 1
  Threaded = false
